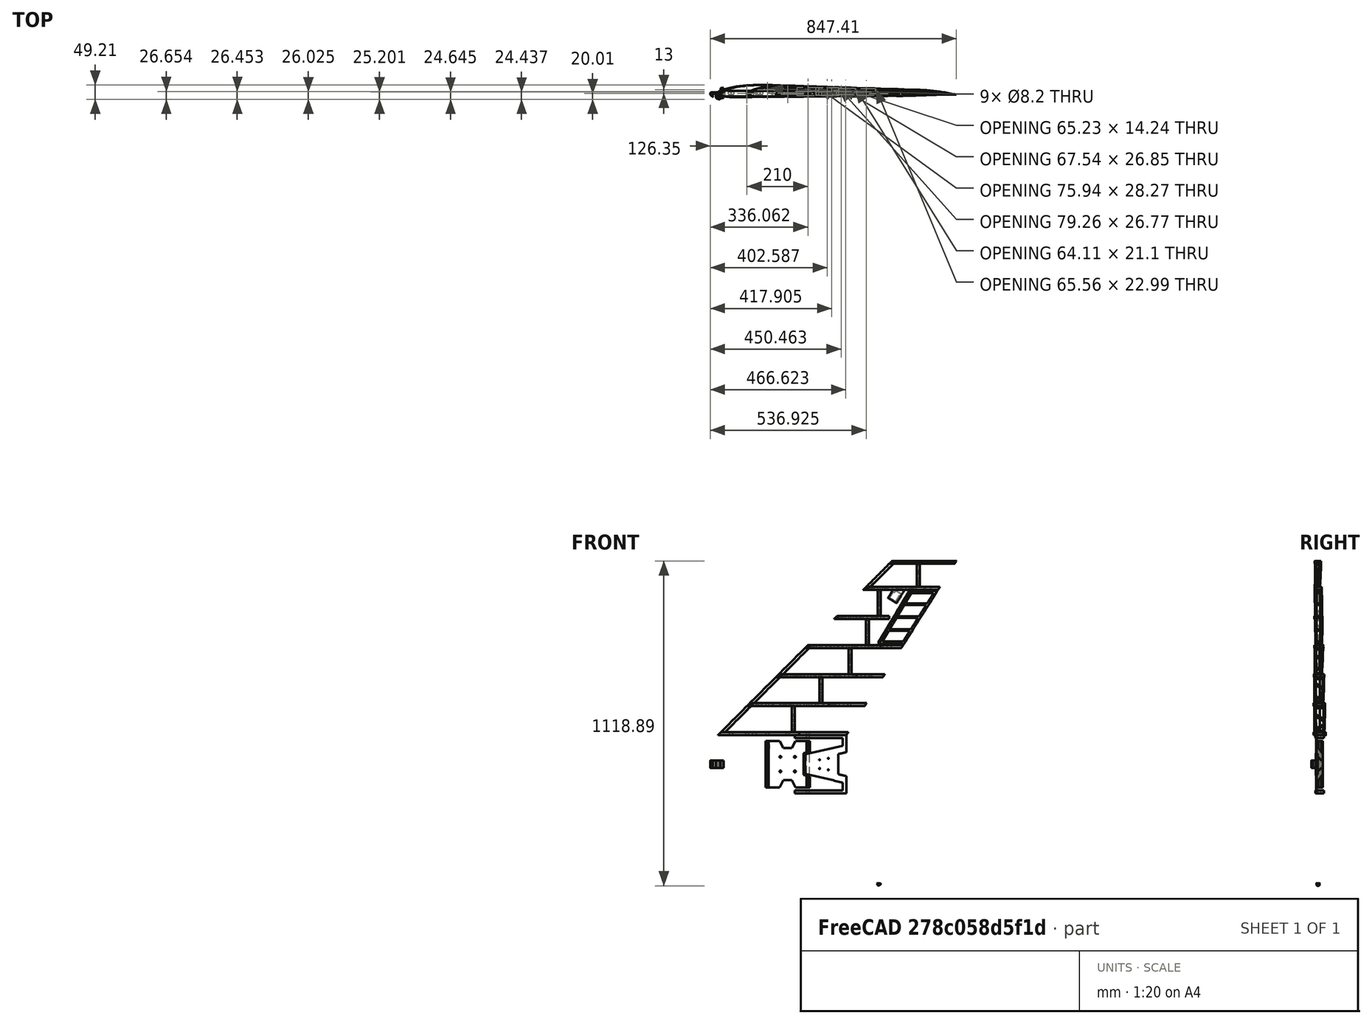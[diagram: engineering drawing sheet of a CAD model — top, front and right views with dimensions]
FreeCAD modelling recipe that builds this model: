
FCSTD DOCUMENT  (FreeCAD 1.0R39109 (Git))
Label: SD7037_mirrored
License: All rights reserved
LicenseURL: https://en.wikipedia.org/wiki/All_rights_reserved
objects: Sketcher::SketchObject×213, PartDesign::Pocket×145, PartDesign::Plane×49, PartDesign::Body×35, PartDesign::AdditiveLoft×28, Part::Mirroring×25, PartDesign::Pad×13, PartDesign::Fillet×8, PartDesign::Chamfer×5, Part::Part2DObjectPython×3, PartDesign::FeatureBase×2, Part::Scale×2, Part::Cut×2, App::DocumentObjectGroup×1, PartDesign::ShapeBinder×1
note: 1144 computed .brp shape members not serialized (recipe doc carries the construction recipe); baked Part::Feature solids carry a one-line shape summary decoded from their .brp

FEATURE [Part::Part2DObjectPython] Wire  # Draft 2D object (typed FeaturePython)
  Area = 0.0605284
  ChamferSize = 0
  Closed = true
  End = (1,0,0)
  FilletRadius = 0
  Length = 2.02979
  MakeFace = true
  Points = (61) [(1,0,0),(0.99672,0.00042,0),(0.98707,0.0018,0),(0.97146,0.00436,0),(0.95041,0.00811,0),(0.9245,0.01295,0),(0.89425,0.01865,0),(0.86015,0.0249,0),+53 more]
  Start = (1,0,0)
  Subdivisions = 0
FEATURE [App::DocumentObjectGroup] sd7037
  Group = -> [Wire]
FEATURE [Part::Part2DObjectPython] BSpline  label="wingtip"  # Draft 2D object (typed FeaturePython)
  Area = 2965.6
  Closed = true
  MakeFace = true
  Parameterization = 1
  Points = (60) [(221,0,0),(220.275,0.09282,0),(218.142,0.3978,0),(214.693,0.96356,0),(210.041,1.79231,0),(204.315,2.86195,0),(197.629,4.12165,0),(190.093,5.5029,0),+52 more]
FEATURE [Part::Part2DObjectPython] BSpline001  label="wingbase"  # Draft 2D object (typed FeaturePython)
  Area = 11862.4
  Closed = true
  MakeFace = true
  Parameterization = 1
  Points = (60) [(442,0,0),(440.55,0.18564,0),(436.285,0.7956,0),(429.385,1.92712,0),(420.081,3.58462,0),(408.629,5.7239,0),(395.258,8.2433,0),(380.186,11.0058,0),+52 more]
FEATURE [Sketcher::SketchObject] Sketch
  ArcFitTolerance = 1e-06
  FullyConstrained = false
  MakeInternals = false
  Placement = pos=(600,0,-600) rot=(0,0,1;0rad)
  sketch-geometry (123):
    g0: BSplineCurve PolesCount=61 KnotsCount=61 Degree=3 IsPeriodic=1
    g1-g61: Circle [constr] x61 (B-spline internal-alignment scaffolding for g0; pole/knot coordinates omitted)
    g62-g122: GeomPoint [constr] x61 (B-spline internal-alignment scaffolding for g0; pole/knot coordinates omitted)
  constraints (123):
    c: InternalAlignment(g1,g0)
    c: Weight(g1) = 1
    c: InternalAlignment(g2,g0)
    c: Equal(g2,g1)
    c: InternalAlignment(g3,g0)
    c: Equal(g3,g1)
    c: InternalAlignment(g4,g0)
    c: Equal(g4,g1)
    c: InternalAlignment(g5,g0)
    c: Equal(g5,g1)
    c: InternalAlignment(g6,g0)
    c: Equal(g6,g1)
    c: InternalAlignment(g7,g0)
    c: Equal(g7,g1)
    c: InternalAlignment(g8,g0)
    c: Equal(g8,g1)
    c: InternalAlignment(g9,g0)
    c: Equal(g9,g1)
    c: InternalAlignment(g10,g0)
    c: Equal(g10,g1)
    c: InternalAlignment(g11,g0)
    c: Equal(g11,g1)
    c: InternalAlignment(g12,g0)
    c: Equal(g12,g1)
    c: InternalAlignment(g13,g0)
    c: Equal(g13,g1)
    c: InternalAlignment(g14,g0)
    c: Equal(g14,g1)
    c: InternalAlignment(g15,g0)
    c: Equal(g15,g1)
    c: InternalAlignment(g16,g0)
    c: Equal(g16,g1)
    c: InternalAlignment(g17,g0)
    c: Equal(g17,g1)
    c: InternalAlignment(g18,g0)
    c: Equal(g18,g1)
    c: InternalAlignment(g19,g0)
    c: Equal(g19,g1)
    c: InternalAlignment(g20,g0)
    c: Equal(g20,g1)
    c: InternalAlignment(g21,g0)
    c: Equal(g21,g1)
    c: InternalAlignment(g22,g0)
    c: Equal(g22,g1)
    c: InternalAlignment(g23,g0)
    c: Equal(g23,g1)
    c: InternalAlignment(g24,g0)
    c: Equal(g24,g1)
    c: InternalAlignment(g25,g0)
    c: Equal(g25,g1)
    c: InternalAlignment(g26,g0)
    c: Equal(g26,g1)
    c: InternalAlignment(g27,g0)
    c: Equal(g27,g1)
    c: InternalAlignment(g28,g0)
    c: Equal(g28,g1)
    c: InternalAlignment(g29,g0)
    c: Equal(g29,g1)
    c: InternalAlignment(g30,g0)
    c: Equal(g30,g1)
    c: InternalAlignment(g31,g0)
    c: Equal(g31,g1)
    c: InternalAlignment(g32,g0)
    c: Equal(g32,g1)
    c: InternalAlignment(g33,g0)
    c: Equal(g33,g1)
    c: InternalAlignment(g34,g0)
    c: Equal(g34,g1)
    c: InternalAlignment(g35,g0)
    c: Equal(g35,g1)
    c: InternalAlignment(g36,g0)
    c: Equal(g36,g1)
    c: InternalAlignment(g37,g0)
    c: Equal(g37,g1)
    c: InternalAlignment(g38,g0)
    c: Equal(g38,g1)
    c: InternalAlignment(g39,g0)
    c: Equal(g39,g1)
    c: InternalAlignment(g40,g0)
    c: Equal(g40,g1)
    c: InternalAlignment(g41,g0)
    c: Equal(g41,g1)
    c: InternalAlignment(g42,g0)
    c: Equal(g42,g1)
    c: InternalAlignment(g43,g0)
    c: Equal(g43,g1)
    c: InternalAlignment(g44,g0)
    c: Equal(g44,g1)
    c: InternalAlignment(g45,g0)
    c: Equal(g45,g1)
    c: InternalAlignment(g46,g0)
    c: Equal(g46,g1)
    c: InternalAlignment(g47,g0)
    c: Equal(g47,g1)
    c: InternalAlignment(g48,g0)
    c: Equal(g48,g1)
    c: InternalAlignment(g49,g0)
    c: Equal(g49,g1)
    c: InternalAlignment(g50,g0)
    c: Equal(g50,g1)
    c: InternalAlignment(g51,g0)
    c: Equal(g51,g1)
    c: InternalAlignment(g52,g0)
    c: Equal(g52,g1)
    c: InternalAlignment(g53,g0)
    c: Equal(g53,g1)
    c: InternalAlignment(g54,g0)
    c: Equal(g54,g1)
    c: InternalAlignment(g55,g0)
    c: Equal(g55,g1)
    c: InternalAlignment(g56,g0)
    c: Equal(g56,g1)
    c: InternalAlignment(g57,g0)
    c: Equal(g57,g1)
    c: InternalAlignment(g58,g0)
    c: Equal(g58,g1)
    c: InternalAlignment(g59,g0)
    c: Equal(g59,g1)
    c: InternalAlignment(g60,g0)
    c: Equal(g60,g1)
    c: InternalAlignment(g61,g0)
    c: Equal(g61,g1)
    c: InternalAlignment(g62-g122 -> g0) x61
FEATURE [Sketcher::SketchObject] Sketch001
  ArcFitTolerance = 1e-06
  FullyConstrained = false
  MakeInternals = false
  sketch-geometry (123):
    g0: BSplineCurve PolesCount=61 KnotsCount=61 Degree=3 IsPeriodic=1
    g1-g61: Circle [constr] x61 (B-spline internal-alignment scaffolding for g0; pole/knot coordinates omitted)
    g62-g122: GeomPoint [constr] x61 (B-spline internal-alignment scaffolding for g0; pole/knot coordinates omitted)
  constraints (123):
    c: InternalAlignment(g1,g0)
    c: Weight(g1) = 1
    c: InternalAlignment(g2,g0)
    c: Equal(g2,g1)
    c: InternalAlignment(g3,g0)
    c: Equal(g3,g1)
    c: InternalAlignment(g4,g0)
    c: Equal(g4,g1)
    c: InternalAlignment(g5,g0)
    c: Equal(g5,g1)
    c: InternalAlignment(g6,g0)
    c: Equal(g6,g1)
    c: InternalAlignment(g7,g0)
    c: Equal(g7,g1)
    c: InternalAlignment(g8,g0)
    c: Equal(g8,g1)
    c: InternalAlignment(g9,g0)
    c: Equal(g9,g1)
    c: InternalAlignment(g10,g0)
    c: Equal(g10,g1)
    c: InternalAlignment(g11,g0)
    c: Equal(g11,g1)
    c: InternalAlignment(g12,g0)
    c: Equal(g12,g1)
    c: InternalAlignment(g13,g0)
    c: Equal(g13,g1)
    c: InternalAlignment(g14,g0)
    c: Equal(g14,g1)
    c: InternalAlignment(g15,g0)
    c: Equal(g15,g1)
    c: InternalAlignment(g16,g0)
    c: Equal(g16,g1)
    c: InternalAlignment(g17,g0)
    c: Equal(g17,g1)
    c: InternalAlignment(g18,g0)
    c: Equal(g18,g1)
    c: InternalAlignment(g19,g0)
    c: Equal(g19,g1)
    c: InternalAlignment(g20,g0)
    c: Equal(g20,g1)
    c: InternalAlignment(g21,g0)
    c: Equal(g21,g1)
    c: InternalAlignment(g22,g0)
    c: Equal(g22,g1)
    c: InternalAlignment(g23,g0)
    c: Equal(g23,g1)
    c: InternalAlignment(g24,g0)
    c: Equal(g24,g1)
    c: InternalAlignment(g25,g0)
    c: Equal(g25,g1)
    c: InternalAlignment(g26,g0)
    c: Equal(g26,g1)
    c: InternalAlignment(g27,g0)
    c: Equal(g27,g1)
    c: InternalAlignment(g28,g0)
    c: Equal(g28,g1)
    c: InternalAlignment(g29,g0)
    c: Equal(g29,g1)
    c: InternalAlignment(g30,g0)
    c: Equal(g30,g1)
    c: InternalAlignment(g31,g0)
    c: Equal(g31,g1)
    c: InternalAlignment(g32,g0)
    c: Equal(g32,g1)
    c: InternalAlignment(g33,g0)
    c: Equal(g33,g1)
    c: InternalAlignment(g34,g0)
    c: Equal(g34,g1)
    c: InternalAlignment(g35,g0)
    c: Equal(g35,g1)
    c: InternalAlignment(g36,g0)
    c: Equal(g36,g1)
    c: InternalAlignment(g37,g0)
    c: Equal(g37,g1)
    c: InternalAlignment(g38,g0)
    c: Equal(g38,g1)
    c: InternalAlignment(g39,g0)
    c: Equal(g39,g1)
    c: InternalAlignment(g40,g0)
    c: Equal(g40,g1)
    c: InternalAlignment(g41,g0)
    c: Equal(g41,g1)
    c: InternalAlignment(g42,g0)
    c: Equal(g42,g1)
    c: InternalAlignment(g43,g0)
    c: Equal(g43,g1)
    c: InternalAlignment(g44,g0)
    c: Equal(g44,g1)
    c: InternalAlignment(g45,g0)
    c: Equal(g45,g1)
    c: InternalAlignment(g46,g0)
    c: Equal(g46,g1)
    c: InternalAlignment(g47,g0)
    c: Equal(g47,g1)
    c: InternalAlignment(g48,g0)
    c: Equal(g48,g1)
    c: InternalAlignment(g49,g0)
    c: Equal(g49,g1)
    c: InternalAlignment(g50,g0)
    c: Equal(g50,g1)
    c: InternalAlignment(g51,g0)
    c: Equal(g51,g1)
    c: InternalAlignment(g52,g0)
    c: Equal(g52,g1)
    c: InternalAlignment(g53,g0)
    c: Equal(g53,g1)
    c: InternalAlignment(g54,g0)
    c: Equal(g54,g1)
    c: InternalAlignment(g55,g0)
    c: Equal(g55,g1)
    c: InternalAlignment(g56,g0)
    c: Equal(g56,g1)
    c: InternalAlignment(g57,g0)
    c: Equal(g57,g1)
    c: InternalAlignment(g58,g0)
    c: Equal(g58,g1)
    c: InternalAlignment(g59,g0)
    c: Equal(g59,g1)
    c: InternalAlignment(g60,g0)
    c: Equal(g60,g1)
    c: InternalAlignment(g61,g0)
    c: Equal(g61,g1)
    c: InternalAlignment(g62-g122 -> g0) x61
FEATURE [PartDesign::AdditiveLoft] AdditiveLoft
  Closed = false
  Profile = -> Sketch001
  Refine = true
  Ruled = false
  Sections = -> [Sketch]
  Suppressed = false
FEATURE [PartDesign::Plane] DatumPlane
  AttachmentOffset = pos=(0,0,0) rot=(0,-1,0;0.785398rad)
  AttachmentSupport = -> [AdditiveLoft]
  Length = 397.552
  MapMode = 5
  Placement = pos=(0,0,0) rot=(0,-1,0;0.785398rad)
  ResizeMode = 0
  Width = 78.2374
FEATURE [Sketcher::SketchObject] Sketch002
  ArcFitTolerance = 1e-06
  AttachmentSupport = -> [DatumPlane]
  FullyConstrained = false
  MakeInternals = false
  MapMode = 5
  Placement = pos=(0,0,0) rot=(0,-1,0;0.785398rad)
  sketch-geometry (1):
    g0: Circle CenterX=28.3343 CenterY=4.75298 CenterZ=0 NormalX=0 NormalY=0 NormalZ=1 AngleXU=0 Radius=4.1
  constraints (1):
    c: Diameter(g0) = 8.2
FEATURE [PartDesign::Pocket] Pocket
  BaseFeature = -> AdditiveLoft
  Direction = (0.707107,0,-0.707107)
  Length = 1000
  Length2 = 5
  Profile = -> Sketch002
  ReferenceAxis = -> Sketch002 [N_Axis]
  Refine = true
  Suppressed = false
  Type = 0
FEATURE [Sketcher::SketchObject] Sketch003
  ArcFitTolerance = 1e-06
  FullyConstrained = false
  MakeInternals = false
  Placement = pos=(600,0,-600) rot=(0,0,1;0rad)
  sketch-geometry (123):
    g0: BSplineCurve PolesCount=61 KnotsCount=61 Degree=3 IsPeriodic=1
    g1-g61: Circle [constr] x61 (B-spline internal-alignment scaffolding for g0; pole/knot coordinates omitted)
    g62-g122: GeomPoint [constr] x61 (B-spline internal-alignment scaffolding for g0; pole/knot coordinates omitted)
  constraints (123):
    c: InternalAlignment(g1,g0)
    c: Weight(g1) = 1
    c: InternalAlignment(g2,g0)
    c: Equal(g2,g1)
    c: InternalAlignment(g3,g0)
    c: Equal(g3,g1)
    c: InternalAlignment(g4,g0)
    c: Equal(g4,g1)
    c: InternalAlignment(g5,g0)
    c: Equal(g5,g1)
    c: InternalAlignment(g6,g0)
    c: Equal(g6,g1)
    c: InternalAlignment(g7,g0)
    c: Equal(g7,g1)
    c: InternalAlignment(g8,g0)
    c: Equal(g8,g1)
    c: InternalAlignment(g9,g0)
    c: Equal(g9,g1)
    c: InternalAlignment(g10,g0)
    c: Equal(g10,g1)
    c: InternalAlignment(g11,g0)
    c: Equal(g11,g1)
    c: InternalAlignment(g12,g0)
    c: Equal(g12,g1)
    c: InternalAlignment(g13,g0)
    c: Equal(g13,g1)
    c: InternalAlignment(g14,g0)
    c: Equal(g14,g1)
    c: InternalAlignment(g15,g0)
    c: Equal(g15,g1)
    c: InternalAlignment(g16,g0)
    c: Equal(g16,g1)
    c: InternalAlignment(g17,g0)
    c: Equal(g17,g1)
    c: InternalAlignment(g18,g0)
    c: Equal(g18,g1)
    c: InternalAlignment(g19,g0)
    c: Equal(g19,g1)
    c: InternalAlignment(g20,g0)
    c: Equal(g20,g1)
    c: InternalAlignment(g21,g0)
    c: Equal(g21,g1)
    c: InternalAlignment(g22,g0)
    c: Equal(g22,g1)
    c: InternalAlignment(g23,g0)
    c: Equal(g23,g1)
    c: InternalAlignment(g24,g0)
    c: Equal(g24,g1)
    c: InternalAlignment(g25,g0)
    c: Equal(g25,g1)
    c: InternalAlignment(g26,g0)
    c: Equal(g26,g1)
    c: InternalAlignment(g27,g0)
    c: Equal(g27,g1)
    c: InternalAlignment(g28,g0)
    c: Equal(g28,g1)
    c: InternalAlignment(g29,g0)
    c: Equal(g29,g1)
    c: InternalAlignment(g30,g0)
    c: Equal(g30,g1)
    c: InternalAlignment(g31,g0)
    c: Equal(g31,g1)
    c: InternalAlignment(g32,g0)
    c: Equal(g32,g1)
    c: InternalAlignment(g33,g0)
    c: Equal(g33,g1)
    c: InternalAlignment(g34,g0)
    c: Equal(g34,g1)
    c: InternalAlignment(g35,g0)
    c: Equal(g35,g1)
    c: InternalAlignment(g36,g0)
    c: Equal(g36,g1)
    c: InternalAlignment(g37,g0)
    c: Equal(g37,g1)
    c: InternalAlignment(g38,g0)
    c: Equal(g38,g1)
    c: InternalAlignment(g39,g0)
    c: Equal(g39,g1)
    c: InternalAlignment(g40,g0)
    c: Equal(g40,g1)
    c: InternalAlignment(g41,g0)
    c: Equal(g41,g1)
    c: InternalAlignment(g42,g0)
    c: Equal(g42,g1)
    c: InternalAlignment(g43,g0)
    c: Equal(g43,g1)
    c: InternalAlignment(g44,g0)
    c: Equal(g44,g1)
    c: InternalAlignment(g45,g0)
    c: Equal(g45,g1)
    c: InternalAlignment(g46,g0)
    c: Equal(g46,g1)
    c: InternalAlignment(g47,g0)
    c: Equal(g47,g1)
    c: InternalAlignment(g48,g0)
    c: Equal(g48,g1)
    c: InternalAlignment(g49,g0)
    c: Equal(g49,g1)
    c: InternalAlignment(g50,g0)
    c: Equal(g50,g1)
    c: InternalAlignment(g51,g0)
    c: Equal(g51,g1)
    c: InternalAlignment(g52,g0)
    c: Equal(g52,g1)
    c: InternalAlignment(g53,g0)
    c: Equal(g53,g1)
    c: InternalAlignment(g54,g0)
    c: Equal(g54,g1)
    c: InternalAlignment(g55,g0)
    c: Equal(g55,g1)
    c: InternalAlignment(g56,g0)
    c: Equal(g56,g1)
    c: InternalAlignment(g57,g0)
    c: Equal(g57,g1)
    c: InternalAlignment(g58,g0)
    c: Equal(g58,g1)
    c: InternalAlignment(g59,g0)
    c: Equal(g59,g1)
    c: InternalAlignment(g60,g0)
    c: Equal(g60,g1)
    c: InternalAlignment(g61,g0)
    c: Equal(g61,g1)
    c: InternalAlignment(g62-g122 -> g0) x61
FEATURE [Sketcher::SketchObject] Sketch004
  ArcFitTolerance = 1e-06
  FullyConstrained = false
  MakeInternals = false
  sketch-geometry (123):
    g0: BSplineCurve PolesCount=61 KnotsCount=61 Degree=3 IsPeriodic=1
    g1-g61: Circle [constr] x61 (B-spline internal-alignment scaffolding for g0; pole/knot coordinates omitted)
    g62-g122: GeomPoint [constr] x61 (B-spline internal-alignment scaffolding for g0; pole/knot coordinates omitted)
  constraints (123):
    c: InternalAlignment(g1,g0)
    c: Weight(g1) = 1
    c: InternalAlignment(g2,g0)
    c: Equal(g2,g1)
    c: InternalAlignment(g3,g0)
    c: Equal(g3,g1)
    c: InternalAlignment(g4,g0)
    c: Equal(g4,g1)
    c: InternalAlignment(g5,g0)
    c: Equal(g5,g1)
    c: InternalAlignment(g6,g0)
    c: Equal(g6,g1)
    c: InternalAlignment(g7,g0)
    c: Equal(g7,g1)
    c: InternalAlignment(g8,g0)
    c: Equal(g8,g1)
    c: InternalAlignment(g9,g0)
    c: Equal(g9,g1)
    c: InternalAlignment(g10,g0)
    c: Equal(g10,g1)
    c: InternalAlignment(g11,g0)
    c: Equal(g11,g1)
    c: InternalAlignment(g12,g0)
    c: Equal(g12,g1)
    c: InternalAlignment(g13,g0)
    c: Equal(g13,g1)
    c: InternalAlignment(g14,g0)
    c: Equal(g14,g1)
    c: InternalAlignment(g15,g0)
    c: Equal(g15,g1)
    c: InternalAlignment(g16,g0)
    c: Equal(g16,g1)
    c: InternalAlignment(g17,g0)
    c: Equal(g17,g1)
    c: InternalAlignment(g18,g0)
    c: Equal(g18,g1)
    c: InternalAlignment(g19,g0)
    c: Equal(g19,g1)
    c: InternalAlignment(g20,g0)
    c: Equal(g20,g1)
    c: InternalAlignment(g21,g0)
    c: Equal(g21,g1)
    c: InternalAlignment(g22,g0)
    c: Equal(g22,g1)
    c: InternalAlignment(g23,g0)
    c: Equal(g23,g1)
    c: InternalAlignment(g24,g0)
    c: Equal(g24,g1)
    c: InternalAlignment(g25,g0)
    c: Equal(g25,g1)
    c: InternalAlignment(g26,g0)
    c: Equal(g26,g1)
    c: InternalAlignment(g27,g0)
    c: Equal(g27,g1)
    c: InternalAlignment(g28,g0)
    c: Equal(g28,g1)
    c: InternalAlignment(g29,g0)
    c: Equal(g29,g1)
    c: InternalAlignment(g30,g0)
    c: Equal(g30,g1)
    c: InternalAlignment(g31,g0)
    c: Equal(g31,g1)
    c: InternalAlignment(g32,g0)
    c: Equal(g32,g1)
    c: InternalAlignment(g33,g0)
    c: Equal(g33,g1)
    c: InternalAlignment(g34,g0)
    c: Equal(g34,g1)
    c: InternalAlignment(g35,g0)
    c: Equal(g35,g1)
    c: InternalAlignment(g36,g0)
    c: Equal(g36,g1)
    c: InternalAlignment(g37,g0)
    c: Equal(g37,g1)
    c: InternalAlignment(g38,g0)
    c: Equal(g38,g1)
    c: InternalAlignment(g39,g0)
    c: Equal(g39,g1)
    c: InternalAlignment(g40,g0)
    c: Equal(g40,g1)
    c: InternalAlignment(g41,g0)
    c: Equal(g41,g1)
    c: InternalAlignment(g42,g0)
    c: Equal(g42,g1)
    c: InternalAlignment(g43,g0)
    c: Equal(g43,g1)
    c: InternalAlignment(g44,g0)
    c: Equal(g44,g1)
    c: InternalAlignment(g45,g0)
    c: Equal(g45,g1)
    c: InternalAlignment(g46,g0)
    c: Equal(g46,g1)
    c: InternalAlignment(g47,g0)
    c: Equal(g47,g1)
    c: InternalAlignment(g48,g0)
    c: Equal(g48,g1)
    c: InternalAlignment(g49,g0)
    c: Equal(g49,g1)
    c: InternalAlignment(g50,g0)
    c: Equal(g50,g1)
    c: InternalAlignment(g51,g0)
    c: Equal(g51,g1)
    c: InternalAlignment(g52,g0)
    c: Equal(g52,g1)
    c: InternalAlignment(g53,g0)
    c: Equal(g53,g1)
    c: InternalAlignment(g54,g0)
    c: Equal(g54,g1)
    c: InternalAlignment(g55,g0)
    c: Equal(g55,g1)
    c: InternalAlignment(g56,g0)
    c: Equal(g56,g1)
    c: InternalAlignment(g57,g0)
    c: Equal(g57,g1)
    c: InternalAlignment(g58,g0)
    c: Equal(g58,g1)
    c: InternalAlignment(g59,g0)
    c: Equal(g59,g1)
    c: InternalAlignment(g60,g0)
    c: Equal(g60,g1)
    c: InternalAlignment(g61,g0)
    c: Equal(g61,g1)
    c: InternalAlignment(g62-g122 -> g0) x61
FEATURE [PartDesign::AdditiveLoft] AdditiveLoft001
  Closed = false
  Profile = -> Sketch004
  Refine = true
  Ruled = false
  Sections = -> [Sketch003]
  Suppressed = false
FEATURE [PartDesign::Plane] DatumPlane001
  AttachmentOffset = pos=(0,0,0) rot=(0,-1,0;0.785398rad)
  AttachmentSupport = -> [AdditiveLoft001]
  Length = 412.402
  MapMode = 5
  Placement = pos=(0,0,0) rot=(0,-1,0;0.785398rad)
  ResizeMode = 0
  Width = 84.5785
FEATURE [Sketcher::SketchObject] Sketch005
  ArcFitTolerance = 1e-06
  AttachmentSupport = -> [DatumPlane001]
  FullyConstrained = false
  MakeInternals = false
  MapMode = 5
  Placement = pos=(0,0,0) rot=(0,-1,0;0.785398rad)
  sketch-geometry (1):
    g0: Circle CenterX=28.3343 CenterY=4.75298 CenterZ=0 NormalX=0 NormalY=0 NormalZ=1 AngleXU=0 Radius=4.1
  constraints (1):
    c: Diameter(g0) = 8.2
FEATURE [PartDesign::Pocket] Pocket001
  BaseFeature = -> AdditiveLoft001
  Direction = (0.707107,0,-0.707107)
  Length = 1000
  Length2 = 5
  Profile = -> Sketch005
  ReferenceAxis = -> Sketch005 [N_Axis]
  Refine = true
  Suppressed = false
  Type = 0
FEATURE [Sketcher::SketchObject] Sketch006
  ArcFitTolerance = 1e-06
  FullyConstrained = false
  MakeInternals = false
  Placement = pos=(600,0,-600) rot=(0,0,1;0rad)
  sketch-geometry (123):
    g0: BSplineCurve PolesCount=61 KnotsCount=61 Degree=3 IsPeriodic=1
    g1-g61: Circle [constr] x61 (B-spline internal-alignment scaffolding for g0; pole/knot coordinates omitted)
    g62-g122: GeomPoint [constr] x61 (B-spline internal-alignment scaffolding for g0; pole/knot coordinates omitted)
  constraints (123):
    c: InternalAlignment(g1,g0)
    c: Weight(g1) = 1
    c: InternalAlignment(g2,g0)
    c: Equal(g2,g1)
    c: InternalAlignment(g3,g0)
    c: Equal(g3,g1)
    c: InternalAlignment(g4,g0)
    c: Equal(g4,g1)
    c: InternalAlignment(g5,g0)
    c: Equal(g5,g1)
    c: InternalAlignment(g6,g0)
    c: Equal(g6,g1)
    c: InternalAlignment(g7,g0)
    c: Equal(g7,g1)
    c: InternalAlignment(g8,g0)
    c: Equal(g8,g1)
    c: InternalAlignment(g9,g0)
    c: Equal(g9,g1)
    c: InternalAlignment(g10,g0)
    c: Equal(g10,g1)
    c: InternalAlignment(g11,g0)
    c: Equal(g11,g1)
    c: InternalAlignment(g12,g0)
    c: Equal(g12,g1)
    c: InternalAlignment(g13,g0)
    c: Equal(g13,g1)
    c: InternalAlignment(g14,g0)
    c: Equal(g14,g1)
    c: InternalAlignment(g15,g0)
    c: Equal(g15,g1)
    c: InternalAlignment(g16,g0)
    c: Equal(g16,g1)
    c: InternalAlignment(g17,g0)
    c: Equal(g17,g1)
    c: InternalAlignment(g18,g0)
    c: Equal(g18,g1)
    c: InternalAlignment(g19,g0)
    c: Equal(g19,g1)
    c: InternalAlignment(g20,g0)
    c: Equal(g20,g1)
    c: InternalAlignment(g21,g0)
    c: Equal(g21,g1)
    c: InternalAlignment(g22,g0)
    c: Equal(g22,g1)
    c: InternalAlignment(g23,g0)
    c: Equal(g23,g1)
    c: InternalAlignment(g24,g0)
    c: Equal(g24,g1)
    c: InternalAlignment(g25,g0)
    c: Equal(g25,g1)
    c: InternalAlignment(g26,g0)
    c: Equal(g26,g1)
    c: InternalAlignment(g27,g0)
    c: Equal(g27,g1)
    c: InternalAlignment(g28,g0)
    c: Equal(g28,g1)
    c: InternalAlignment(g29,g0)
    c: Equal(g29,g1)
    c: InternalAlignment(g30,g0)
    c: Equal(g30,g1)
    c: InternalAlignment(g31,g0)
    c: Equal(g31,g1)
    c: InternalAlignment(g32,g0)
    c: Equal(g32,g1)
    c: InternalAlignment(g33,g0)
    c: Equal(g33,g1)
    c: InternalAlignment(g34,g0)
    c: Equal(g34,g1)
    c: InternalAlignment(g35,g0)
    c: Equal(g35,g1)
    c: InternalAlignment(g36,g0)
    c: Equal(g36,g1)
    c: InternalAlignment(g37,g0)
    c: Equal(g37,g1)
    c: InternalAlignment(g38,g0)
    c: Equal(g38,g1)
    c: InternalAlignment(g39,g0)
    c: Equal(g39,g1)
    c: InternalAlignment(g40,g0)
    c: Equal(g40,g1)
    c: InternalAlignment(g41,g0)
    c: Equal(g41,g1)
    c: InternalAlignment(g42,g0)
    c: Equal(g42,g1)
    c: InternalAlignment(g43,g0)
    c: Equal(g43,g1)
    c: InternalAlignment(g44,g0)
    c: Equal(g44,g1)
    c: InternalAlignment(g45,g0)
    c: Equal(g45,g1)
    c: InternalAlignment(g46,g0)
    c: Equal(g46,g1)
    c: InternalAlignment(g47,g0)
    c: Equal(g47,g1)
    c: InternalAlignment(g48,g0)
    c: Equal(g48,g1)
    c: InternalAlignment(g49,g0)
    c: Equal(g49,g1)
    c: InternalAlignment(g50,g0)
    c: Equal(g50,g1)
    c: InternalAlignment(g51,g0)
    c: Equal(g51,g1)
    c: InternalAlignment(g52,g0)
    c: Equal(g52,g1)
    c: InternalAlignment(g53,g0)
    c: Equal(g53,g1)
    c: InternalAlignment(g54,g0)
    c: Equal(g54,g1)
    c: InternalAlignment(g55,g0)
    c: Equal(g55,g1)
    c: InternalAlignment(g56,g0)
    c: Equal(g56,g1)
    c: InternalAlignment(g57,g0)
    c: Equal(g57,g1)
    c: InternalAlignment(g58,g0)
    c: Equal(g58,g1)
    c: InternalAlignment(g59,g0)
    c: Equal(g59,g1)
    c: InternalAlignment(g60,g0)
    c: Equal(g60,g1)
    c: InternalAlignment(g61,g0)
    c: Equal(g61,g1)
    c: InternalAlignment(g62-g122 -> g0) x61
FEATURE [Sketcher::SketchObject] Sketch007
  ArcFitTolerance = 1e-06
  FullyConstrained = false
  MakeInternals = false
  sketch-geometry (123):
    g0: BSplineCurve PolesCount=61 KnotsCount=61 Degree=3 IsPeriodic=1
    g1-g61: Circle [constr] x61 (B-spline internal-alignment scaffolding for g0; pole/knot coordinates omitted)
    g62-g122: GeomPoint [constr] x61 (B-spline internal-alignment scaffolding for g0; pole/knot coordinates omitted)
  constraints (123):
    c: InternalAlignment(g1,g0)
    c: Weight(g1) = 1
    c: InternalAlignment(g2,g0)
    c: Equal(g2,g1)
    c: InternalAlignment(g3,g0)
    c: Equal(g3,g1)
    c: InternalAlignment(g4,g0)
    c: Equal(g4,g1)
    c: InternalAlignment(g5,g0)
    c: Equal(g5,g1)
    c: InternalAlignment(g6,g0)
    c: Equal(g6,g1)
    c: InternalAlignment(g7,g0)
    c: Equal(g7,g1)
    c: InternalAlignment(g8,g0)
    c: Equal(g8,g1)
    c: InternalAlignment(g9,g0)
    c: Equal(g9,g1)
    c: InternalAlignment(g10,g0)
    c: Equal(g10,g1)
    c: InternalAlignment(g11,g0)
    c: Equal(g11,g1)
    c: InternalAlignment(g12,g0)
    c: Equal(g12,g1)
    c: InternalAlignment(g13,g0)
    c: Equal(g13,g1)
    c: InternalAlignment(g14,g0)
    c: Equal(g14,g1)
    c: InternalAlignment(g15,g0)
    c: Equal(g15,g1)
    c: InternalAlignment(g16,g0)
    c: Equal(g16,g1)
    c: InternalAlignment(g17,g0)
    c: Equal(g17,g1)
    c: InternalAlignment(g18,g0)
    c: Equal(g18,g1)
    c: InternalAlignment(g19,g0)
    c: Equal(g19,g1)
    c: InternalAlignment(g20,g0)
    c: Equal(g20,g1)
    c: InternalAlignment(g21,g0)
    c: Equal(g21,g1)
    c: InternalAlignment(g22,g0)
    c: Equal(g22,g1)
    c: InternalAlignment(g23,g0)
    c: Equal(g23,g1)
    c: InternalAlignment(g24,g0)
    c: Equal(g24,g1)
    c: InternalAlignment(g25,g0)
    c: Equal(g25,g1)
    c: InternalAlignment(g26,g0)
    c: Equal(g26,g1)
    c: InternalAlignment(g27,g0)
    c: Equal(g27,g1)
    c: InternalAlignment(g28,g0)
    c: Equal(g28,g1)
    c: InternalAlignment(g29,g0)
    c: Equal(g29,g1)
    c: InternalAlignment(g30,g0)
    c: Equal(g30,g1)
    c: InternalAlignment(g31,g0)
    c: Equal(g31,g1)
    c: InternalAlignment(g32,g0)
    c: Equal(g32,g1)
    c: InternalAlignment(g33,g0)
    c: Equal(g33,g1)
    c: InternalAlignment(g34,g0)
    c: Equal(g34,g1)
    c: InternalAlignment(g35,g0)
    c: Equal(g35,g1)
    c: InternalAlignment(g36,g0)
    c: Equal(g36,g1)
    c: InternalAlignment(g37,g0)
    c: Equal(g37,g1)
    c: InternalAlignment(g38,g0)
    c: Equal(g38,g1)
    c: InternalAlignment(g39,g0)
    c: Equal(g39,g1)
    c: InternalAlignment(g40,g0)
    c: Equal(g40,g1)
    c: InternalAlignment(g41,g0)
    c: Equal(g41,g1)
    c: InternalAlignment(g42,g0)
    c: Equal(g42,g1)
    c: InternalAlignment(g43,g0)
    c: Equal(g43,g1)
    c: InternalAlignment(g44,g0)
    c: Equal(g44,g1)
    c: InternalAlignment(g45,g0)
    c: Equal(g45,g1)
    c: InternalAlignment(g46,g0)
    c: Equal(g46,g1)
    c: InternalAlignment(g47,g0)
    c: Equal(g47,g1)
    c: InternalAlignment(g48,g0)
    c: Equal(g48,g1)
    c: InternalAlignment(g49,g0)
    c: Equal(g49,g1)
    c: InternalAlignment(g50,g0)
    c: Equal(g50,g1)
    c: InternalAlignment(g51,g0)
    c: Equal(g51,g1)
    c: InternalAlignment(g52,g0)
    c: Equal(g52,g1)
    c: InternalAlignment(g53,g0)
    c: Equal(g53,g1)
    c: InternalAlignment(g54,g0)
    c: Equal(g54,g1)
    c: InternalAlignment(g55,g0)
    c: Equal(g55,g1)
    c: InternalAlignment(g56,g0)
    c: Equal(g56,g1)
    c: InternalAlignment(g57,g0)
    c: Equal(g57,g1)
    c: InternalAlignment(g58,g0)
    c: Equal(g58,g1)
    c: InternalAlignment(g59,g0)
    c: Equal(g59,g1)
    c: InternalAlignment(g60,g0)
    c: Equal(g60,g1)
    c: InternalAlignment(g61,g0)
    c: Equal(g61,g1)
    c: InternalAlignment(g62-g122 -> g0) x61
FEATURE [PartDesign::AdditiveLoft] AdditiveLoft002
  Closed = false
  Profile = -> Sketch007
  Refine = true
  Ruled = false
  Sections = -> [Sketch006]
  Suppressed = false
FEATURE [PartDesign::Plane] DatumPlane002
  AttachmentOffset = pos=(0,0,0) rot=(0,-1,0;0.785398rad)
  AttachmentSupport = -> [AdditiveLoft002]
  Length = 554.997
  MapMode = 5
  Placement = pos=(0,0,0) rot=(0,-1,0;0.785398rad)
  ResizeMode = 0
  Width = 85.8053
FEATURE [Sketcher::SketchObject] Sketch008
  ArcFitTolerance = 1e-06
  AttachmentSupport = -> [DatumPlane002]
  FullyConstrained = false
  MakeInternals = false
  MapMode = 5
  Placement = pos=(0,0,0) rot=(0,-1,0;0.785398rad)
  sketch-geometry (1):
    g0: Circle CenterX=28.3343 CenterY=4.75298 CenterZ=0 NormalX=0 NormalY=0 NormalZ=1 AngleXU=0 Radius=4.1
  constraints (1):
    c: Diameter(g0) = 8.2
FEATURE [PartDesign::Pocket] Pocket002
  BaseFeature = -> AdditiveLoft002
  Direction = (0.707107,0,-0.707107)
  Length = 1000
  Length2 = 5
  Profile = -> Sketch008
  ReferenceAxis = -> Sketch008 [N_Axis]
  Refine = true
  Suppressed = false
  Type = 0
FEATURE [Sketcher::SketchObject] Sketch009
  ArcFitTolerance = 1e-06
  FullyConstrained = false
  MakeInternals = false
  Placement = pos=(600,0,-600) rot=(0,0,1;0rad)
  sketch-geometry (123):
    g0: BSplineCurve PolesCount=61 KnotsCount=61 Degree=3 IsPeriodic=1
    g1-g61: Circle [constr] x61 (B-spline internal-alignment scaffolding for g0; pole/knot coordinates omitted)
    g62-g122: GeomPoint [constr] x61 (B-spline internal-alignment scaffolding for g0; pole/knot coordinates omitted)
  constraints (123):
    c: InternalAlignment(g1,g0)
    c: Weight(g1) = 1
    c: InternalAlignment(g2,g0)
    c: Equal(g2,g1)
    c: InternalAlignment(g3,g0)
    c: Equal(g3,g1)
    c: InternalAlignment(g4,g0)
    c: Equal(g4,g1)
    c: InternalAlignment(g5,g0)
    c: Equal(g5,g1)
    c: InternalAlignment(g6,g0)
    c: Equal(g6,g1)
    c: InternalAlignment(g7,g0)
    c: Equal(g7,g1)
    c: InternalAlignment(g8,g0)
    c: Equal(g8,g1)
    c: InternalAlignment(g9,g0)
    c: Equal(g9,g1)
    c: InternalAlignment(g10,g0)
    c: Equal(g10,g1)
    c: InternalAlignment(g11,g0)
    c: Equal(g11,g1)
    c: InternalAlignment(g12,g0)
    c: Equal(g12,g1)
    c: InternalAlignment(g13,g0)
    c: Equal(g13,g1)
    c: InternalAlignment(g14,g0)
    c: Equal(g14,g1)
    c: InternalAlignment(g15,g0)
    c: Equal(g15,g1)
    c: InternalAlignment(g16,g0)
    c: Equal(g16,g1)
    c: InternalAlignment(g17,g0)
    c: Equal(g17,g1)
    c: InternalAlignment(g18,g0)
    c: Equal(g18,g1)
    c: InternalAlignment(g19,g0)
    c: Equal(g19,g1)
    c: InternalAlignment(g20,g0)
    c: Equal(g20,g1)
    c: InternalAlignment(g21,g0)
    c: Equal(g21,g1)
    c: InternalAlignment(g22,g0)
    c: Equal(g22,g1)
    c: InternalAlignment(g23,g0)
    c: Equal(g23,g1)
    c: InternalAlignment(g24,g0)
    c: Equal(g24,g1)
    c: InternalAlignment(g25,g0)
    c: Equal(g25,g1)
    c: InternalAlignment(g26,g0)
    c: Equal(g26,g1)
    c: InternalAlignment(g27,g0)
    c: Equal(g27,g1)
    c: InternalAlignment(g28,g0)
    c: Equal(g28,g1)
    c: InternalAlignment(g29,g0)
    c: Equal(g29,g1)
    c: InternalAlignment(g30,g0)
    c: Equal(g30,g1)
    c: InternalAlignment(g31,g0)
    c: Equal(g31,g1)
    c: InternalAlignment(g32,g0)
    c: Equal(g32,g1)
    c: InternalAlignment(g33,g0)
    c: Equal(g33,g1)
    c: InternalAlignment(g34,g0)
    c: Equal(g34,g1)
    c: InternalAlignment(g35,g0)
    c: Equal(g35,g1)
    c: InternalAlignment(g36,g0)
    c: Equal(g36,g1)
    c: InternalAlignment(g37,g0)
    c: Equal(g37,g1)
    c: InternalAlignment(g38,g0)
    c: Equal(g38,g1)
    c: InternalAlignment(g39,g0)
    c: Equal(g39,g1)
    c: InternalAlignment(g40,g0)
    c: Equal(g40,g1)
    c: InternalAlignment(g41,g0)
    c: Equal(g41,g1)
    c: InternalAlignment(g42,g0)
    c: Equal(g42,g1)
    c: InternalAlignment(g43,g0)
    c: Equal(g43,g1)
    c: InternalAlignment(g44,g0)
    c: Equal(g44,g1)
    c: InternalAlignment(g45,g0)
    c: Equal(g45,g1)
    c: InternalAlignment(g46,g0)
    c: Equal(g46,g1)
    c: InternalAlignment(g47,g0)
    c: Equal(g47,g1)
    c: InternalAlignment(g48,g0)
    c: Equal(g48,g1)
    c: InternalAlignment(g49,g0)
    c: Equal(g49,g1)
    c: InternalAlignment(g50,g0)
    c: Equal(g50,g1)
    c: InternalAlignment(g51,g0)
    c: Equal(g51,g1)
    c: InternalAlignment(g52,g0)
    c: Equal(g52,g1)
    c: InternalAlignment(g53,g0)
    c: Equal(g53,g1)
    c: InternalAlignment(g54,g0)
    c: Equal(g54,g1)
    c: InternalAlignment(g55,g0)
    c: Equal(g55,g1)
    c: InternalAlignment(g56,g0)
    c: Equal(g56,g1)
    c: InternalAlignment(g57,g0)
    c: Equal(g57,g1)
    c: InternalAlignment(g58,g0)
    c: Equal(g58,g1)
    c: InternalAlignment(g59,g0)
    c: Equal(g59,g1)
    c: InternalAlignment(g60,g0)
    c: Equal(g60,g1)
    c: InternalAlignment(g61,g0)
    c: Equal(g61,g1)
    c: InternalAlignment(g62-g122 -> g0) x61
FEATURE [Sketcher::SketchObject] Sketch010
  ArcFitTolerance = 1e-06
  FullyConstrained = false
  MakeInternals = false
  sketch-geometry (123):
    g0: BSplineCurve PolesCount=61 KnotsCount=61 Degree=3 IsPeriodic=1
    g1-g61: Circle [constr] x61 (B-spline internal-alignment scaffolding for g0; pole/knot coordinates omitted)
    g62-g122: GeomPoint [constr] x61 (B-spline internal-alignment scaffolding for g0; pole/knot coordinates omitted)
  constraints (123):
    c: InternalAlignment(g1,g0)
    c: Weight(g1) = 1
    c: InternalAlignment(g2,g0)
    c: Equal(g2,g1)
    c: InternalAlignment(g3,g0)
    c: Equal(g3,g1)
    c: InternalAlignment(g4,g0)
    c: Equal(g4,g1)
    c: InternalAlignment(g5,g0)
    c: Equal(g5,g1)
    c: InternalAlignment(g6,g0)
    c: Equal(g6,g1)
    c: InternalAlignment(g7,g0)
    c: Equal(g7,g1)
    c: InternalAlignment(g8,g0)
    c: Equal(g8,g1)
    c: InternalAlignment(g9,g0)
    c: Equal(g9,g1)
    c: InternalAlignment(g10,g0)
    c: Equal(g10,g1)
    c: InternalAlignment(g11,g0)
    c: Equal(g11,g1)
    c: InternalAlignment(g12,g0)
    c: Equal(g12,g1)
    c: InternalAlignment(g13,g0)
    c: Equal(g13,g1)
    c: InternalAlignment(g14,g0)
    c: Equal(g14,g1)
    c: InternalAlignment(g15,g0)
    c: Equal(g15,g1)
    c: InternalAlignment(g16,g0)
    c: Equal(g16,g1)
    c: InternalAlignment(g17,g0)
    c: Equal(g17,g1)
    c: InternalAlignment(g18,g0)
    c: Equal(g18,g1)
    c: InternalAlignment(g19,g0)
    c: Equal(g19,g1)
    c: InternalAlignment(g20,g0)
    c: Equal(g20,g1)
    c: InternalAlignment(g21,g0)
    c: Equal(g21,g1)
    c: InternalAlignment(g22,g0)
    c: Equal(g22,g1)
    c: InternalAlignment(g23,g0)
    c: Equal(g23,g1)
    c: InternalAlignment(g24,g0)
    c: Equal(g24,g1)
    c: InternalAlignment(g25,g0)
    c: Equal(g25,g1)
    c: InternalAlignment(g26,g0)
    c: Equal(g26,g1)
    c: InternalAlignment(g27,g0)
    c: Equal(g27,g1)
    c: InternalAlignment(g28,g0)
    c: Equal(g28,g1)
    c: InternalAlignment(g29,g0)
    c: Equal(g29,g1)
    c: InternalAlignment(g30,g0)
    c: Equal(g30,g1)
    c: InternalAlignment(g31,g0)
    c: Equal(g31,g1)
    c: InternalAlignment(g32,g0)
    c: Equal(g32,g1)
    c: InternalAlignment(g33,g0)
    c: Equal(g33,g1)
    c: InternalAlignment(g34,g0)
    c: Equal(g34,g1)
    c: InternalAlignment(g35,g0)
    c: Equal(g35,g1)
    c: InternalAlignment(g36,g0)
    c: Equal(g36,g1)
    c: InternalAlignment(g37,g0)
    c: Equal(g37,g1)
    c: InternalAlignment(g38,g0)
    c: Equal(g38,g1)
    c: InternalAlignment(g39,g0)
    c: Equal(g39,g1)
    c: InternalAlignment(g40,g0)
    c: Equal(g40,g1)
    c: InternalAlignment(g41,g0)
    c: Equal(g41,g1)
    c: InternalAlignment(g42,g0)
    c: Equal(g42,g1)
    c: InternalAlignment(g43,g0)
    c: Equal(g43,g1)
    c: InternalAlignment(g44,g0)
    c: Equal(g44,g1)
    c: InternalAlignment(g45,g0)
    c: Equal(g45,g1)
    c: InternalAlignment(g46,g0)
    c: Equal(g46,g1)
    c: InternalAlignment(g47,g0)
    c: Equal(g47,g1)
    c: InternalAlignment(g48,g0)
    c: Equal(g48,g1)
    c: InternalAlignment(g49,g0)
    c: Equal(g49,g1)
    c: InternalAlignment(g50,g0)
    c: Equal(g50,g1)
    c: InternalAlignment(g51,g0)
    c: Equal(g51,g1)
    c: InternalAlignment(g52,g0)
    c: Equal(g52,g1)
    c: InternalAlignment(g53,g0)
    c: Equal(g53,g1)
    c: InternalAlignment(g54,g0)
    c: Equal(g54,g1)
    c: InternalAlignment(g55,g0)
    c: Equal(g55,g1)
    c: InternalAlignment(g56,g0)
    c: Equal(g56,g1)
    c: InternalAlignment(g57,g0)
    c: Equal(g57,g1)
    c: InternalAlignment(g58,g0)
    c: Equal(g58,g1)
    c: InternalAlignment(g59,g0)
    c: Equal(g59,g1)
    c: InternalAlignment(g60,g0)
    c: Equal(g60,g1)
    c: InternalAlignment(g61,g0)
    c: Equal(g61,g1)
    c: InternalAlignment(g62-g122 -> g0) x61
FEATURE [PartDesign::AdditiveLoft] AdditiveLoft003
  Closed = false
  Profile = -> Sketch010
  Refine = true
  Ruled = false
  Sections = -> [Sketch009]
  Suppressed = false
FEATURE [PartDesign::Plane] DatumPlane003
  AttachmentOffset = pos=(0,0,0) rot=(0,-1,0;0.785398rad)
  AttachmentSupport = -> [AdditiveLoft003]
  Length = 700.703
  MapMode = 5
  Placement = pos=(0,0,0) rot=(0,-1,0;0.785398rad)
  ResizeMode = 0
  Width = 86.4487
FEATURE [Sketcher::SketchObject] Sketch011
  ArcFitTolerance = 1e-06
  AttachmentSupport = -> [DatumPlane003]
  FullyConstrained = false
  MakeInternals = false
  MapMode = 5
  Placement = pos=(0,0,0) rot=(0,-1,0;0.785398rad)
  sketch-geometry (1):
    g0: Circle CenterX=28.3343 CenterY=4.75298 CenterZ=0 NormalX=0 NormalY=0 NormalZ=1 AngleXU=0 Radius=4.1
  constraints (1):
    c: Diameter(g0) = 8.2
FEATURE [PartDesign::Pocket] Pocket003
  BaseFeature = -> AdditiveLoft003
  Direction = (0.707107,0,-0.707107)
  Length = 1000
  Length2 = 5
  Profile = -> Sketch011
  ReferenceAxis = -> Sketch011 [N_Axis]
  Refine = true
  Suppressed = false
  Type = 0
FEATURE [Sketcher::SketchObject] Sketch012
  ArcFitTolerance = 1e-06
  FullyConstrained = false
  MakeInternals = false
  Placement = pos=(600,0,-600) rot=(0,0,1;0rad)
  sketch-geometry (123):
    g0: BSplineCurve PolesCount=61 KnotsCount=61 Degree=3 IsPeriodic=1
    g1-g61: Circle [constr] x61 (B-spline internal-alignment scaffolding for g0; pole/knot coordinates omitted)
    g62-g122: GeomPoint [constr] x61 (B-spline internal-alignment scaffolding for g0; pole/knot coordinates omitted)
  constraints (123):
    c: InternalAlignment(g1,g0)
    c: Weight(g1) = 1
    c: InternalAlignment(g2,g0)
    c: Equal(g2,g1)
    c: InternalAlignment(g3,g0)
    c: Equal(g3,g1)
    c: InternalAlignment(g4,g0)
    c: Equal(g4,g1)
    c: InternalAlignment(g5,g0)
    c: Equal(g5,g1)
    c: InternalAlignment(g6,g0)
    c: Equal(g6,g1)
    c: InternalAlignment(g7,g0)
    c: Equal(g7,g1)
    c: InternalAlignment(g8,g0)
    c: Equal(g8,g1)
    c: InternalAlignment(g9,g0)
    c: Equal(g9,g1)
    c: InternalAlignment(g10,g0)
    c: Equal(g10,g1)
    c: InternalAlignment(g11,g0)
    c: Equal(g11,g1)
    c: InternalAlignment(g12,g0)
    c: Equal(g12,g1)
    c: InternalAlignment(g13,g0)
    c: Equal(g13,g1)
    c: InternalAlignment(g14,g0)
    c: Equal(g14,g1)
    c: InternalAlignment(g15,g0)
    c: Equal(g15,g1)
    c: InternalAlignment(g16,g0)
    c: Equal(g16,g1)
    c: InternalAlignment(g17,g0)
    c: Equal(g17,g1)
    c: InternalAlignment(g18,g0)
    c: Equal(g18,g1)
    c: InternalAlignment(g19,g0)
    c: Equal(g19,g1)
    c: InternalAlignment(g20,g0)
    c: Equal(g20,g1)
    c: InternalAlignment(g21,g0)
    c: Equal(g21,g1)
    c: InternalAlignment(g22,g0)
    c: Equal(g22,g1)
    c: InternalAlignment(g23,g0)
    c: Equal(g23,g1)
    c: InternalAlignment(g24,g0)
    c: Equal(g24,g1)
    c: InternalAlignment(g25,g0)
    c: Equal(g25,g1)
    c: InternalAlignment(g26,g0)
    c: Equal(g26,g1)
    c: InternalAlignment(g27,g0)
    c: Equal(g27,g1)
    c: InternalAlignment(g28,g0)
    c: Equal(g28,g1)
    c: InternalAlignment(g29,g0)
    c: Equal(g29,g1)
    c: InternalAlignment(g30,g0)
    c: Equal(g30,g1)
    c: InternalAlignment(g31,g0)
    c: Equal(g31,g1)
    c: InternalAlignment(g32,g0)
    c: Equal(g32,g1)
    c: InternalAlignment(g33,g0)
    c: Equal(g33,g1)
    c: InternalAlignment(g34,g0)
    c: Equal(g34,g1)
    c: InternalAlignment(g35,g0)
    c: Equal(g35,g1)
    c: InternalAlignment(g36,g0)
    c: Equal(g36,g1)
    c: InternalAlignment(g37,g0)
    c: Equal(g37,g1)
    c: InternalAlignment(g38,g0)
    c: Equal(g38,g1)
    c: InternalAlignment(g39,g0)
    c: Equal(g39,g1)
    c: InternalAlignment(g40,g0)
    c: Equal(g40,g1)
    c: InternalAlignment(g41,g0)
    c: Equal(g41,g1)
    c: InternalAlignment(g42,g0)
    c: Equal(g42,g1)
    c: InternalAlignment(g43,g0)
    c: Equal(g43,g1)
    c: InternalAlignment(g44,g0)
    c: Equal(g44,g1)
    c: InternalAlignment(g45,g0)
    c: Equal(g45,g1)
    c: InternalAlignment(g46,g0)
    c: Equal(g46,g1)
    c: InternalAlignment(g47,g0)
    c: Equal(g47,g1)
    c: InternalAlignment(g48,g0)
    c: Equal(g48,g1)
    c: InternalAlignment(g49,g0)
    c: Equal(g49,g1)
    c: InternalAlignment(g50,g0)
    c: Equal(g50,g1)
    c: InternalAlignment(g51,g0)
    c: Equal(g51,g1)
    c: InternalAlignment(g52,g0)
    c: Equal(g52,g1)
    c: InternalAlignment(g53,g0)
    c: Equal(g53,g1)
    c: InternalAlignment(g54,g0)
    c: Equal(g54,g1)
    c: InternalAlignment(g55,g0)
    c: Equal(g55,g1)
    c: InternalAlignment(g56,g0)
    c: Equal(g56,g1)
    c: InternalAlignment(g57,g0)
    c: Equal(g57,g1)
    c: InternalAlignment(g58,g0)
    c: Equal(g58,g1)
    c: InternalAlignment(g59,g0)
    c: Equal(g59,g1)
    c: InternalAlignment(g60,g0)
    c: Equal(g60,g1)
    c: InternalAlignment(g61,g0)
    c: Equal(g61,g1)
    c: InternalAlignment(g62-g122 -> g0) x61
FEATURE [Sketcher::SketchObject] Sketch013
  ArcFitTolerance = 1e-06
  FullyConstrained = false
  MakeInternals = false
  sketch-geometry (123):
    g0: BSplineCurve PolesCount=61 KnotsCount=61 Degree=3 IsPeriodic=1
    g1-g61: Circle [constr] x61 (B-spline internal-alignment scaffolding for g0; pole/knot coordinates omitted)
    g62-g122: GeomPoint [constr] x61 (B-spline internal-alignment scaffolding for g0; pole/knot coordinates omitted)
  constraints (123):
    c: InternalAlignment(g1,g0)
    c: Weight(g1) = 1
    c: InternalAlignment(g2,g0)
    c: Equal(g2,g1)
    c: InternalAlignment(g3,g0)
    c: Equal(g3,g1)
    c: InternalAlignment(g4,g0)
    c: Equal(g4,g1)
    c: InternalAlignment(g5,g0)
    c: Equal(g5,g1)
    c: InternalAlignment(g6,g0)
    c: Equal(g6,g1)
    c: InternalAlignment(g7,g0)
    c: Equal(g7,g1)
    c: InternalAlignment(g8,g0)
    c: Equal(g8,g1)
    c: InternalAlignment(g9,g0)
    c: Equal(g9,g1)
    c: InternalAlignment(g10,g0)
    c: Equal(g10,g1)
    c: InternalAlignment(g11,g0)
    c: Equal(g11,g1)
    c: InternalAlignment(g12,g0)
    c: Equal(g12,g1)
    c: InternalAlignment(g13,g0)
    c: Equal(g13,g1)
    c: InternalAlignment(g14,g0)
    c: Equal(g14,g1)
    c: InternalAlignment(g15,g0)
    c: Equal(g15,g1)
    c: InternalAlignment(g16,g0)
    c: Equal(g16,g1)
    c: InternalAlignment(g17,g0)
    c: Equal(g17,g1)
    c: InternalAlignment(g18,g0)
    c: Equal(g18,g1)
    c: InternalAlignment(g19,g0)
    c: Equal(g19,g1)
    c: InternalAlignment(g20,g0)
    c: Equal(g20,g1)
    c: InternalAlignment(g21,g0)
    c: Equal(g21,g1)
    c: InternalAlignment(g22,g0)
    c: Equal(g22,g1)
    c: InternalAlignment(g23,g0)
    c: Equal(g23,g1)
    c: InternalAlignment(g24,g0)
    c: Equal(g24,g1)
    c: InternalAlignment(g25,g0)
    c: Equal(g25,g1)
    c: InternalAlignment(g26,g0)
    c: Equal(g26,g1)
    c: InternalAlignment(g27,g0)
    c: Equal(g27,g1)
    c: InternalAlignment(g28,g0)
    c: Equal(g28,g1)
    c: InternalAlignment(g29,g0)
    c: Equal(g29,g1)
    c: InternalAlignment(g30,g0)
    c: Equal(g30,g1)
    c: InternalAlignment(g31,g0)
    c: Equal(g31,g1)
    c: InternalAlignment(g32,g0)
    c: Equal(g32,g1)
    c: InternalAlignment(g33,g0)
    c: Equal(g33,g1)
    c: InternalAlignment(g34,g0)
    c: Equal(g34,g1)
    c: InternalAlignment(g35,g0)
    c: Equal(g35,g1)
    c: InternalAlignment(g36,g0)
    c: Equal(g36,g1)
    c: InternalAlignment(g37,g0)
    c: Equal(g37,g1)
    c: InternalAlignment(g38,g0)
    c: Equal(g38,g1)
    c: InternalAlignment(g39,g0)
    c: Equal(g39,g1)
    c: InternalAlignment(g40,g0)
    c: Equal(g40,g1)
    c: InternalAlignment(g41,g0)
    c: Equal(g41,g1)
    c: InternalAlignment(g42,g0)
    c: Equal(g42,g1)
    c: InternalAlignment(g43,g0)
    c: Equal(g43,g1)
    c: InternalAlignment(g44,g0)
    c: Equal(g44,g1)
    c: InternalAlignment(g45,g0)
    c: Equal(g45,g1)
    c: InternalAlignment(g46,g0)
    c: Equal(g46,g1)
    c: InternalAlignment(g47,g0)
    c: Equal(g47,g1)
    c: InternalAlignment(g48,g0)
    c: Equal(g48,g1)
    c: InternalAlignment(g49,g0)
    c: Equal(g49,g1)
    c: InternalAlignment(g50,g0)
    c: Equal(g50,g1)
    c: InternalAlignment(g51,g0)
    c: Equal(g51,g1)
    c: InternalAlignment(g52,g0)
    c: Equal(g52,g1)
    c: InternalAlignment(g53,g0)
    c: Equal(g53,g1)
    c: InternalAlignment(g54,g0)
    c: Equal(g54,g1)
    c: InternalAlignment(g55,g0)
    c: Equal(g55,g1)
    c: InternalAlignment(g56,g0)
    c: Equal(g56,g1)
    c: InternalAlignment(g57,g0)
    c: Equal(g57,g1)
    c: InternalAlignment(g58,g0)
    c: Equal(g58,g1)
    c: InternalAlignment(g59,g0)
    c: Equal(g59,g1)
    c: InternalAlignment(g60,g0)
    c: Equal(g60,g1)
    c: InternalAlignment(g61,g0)
    c: Equal(g61,g1)
    c: InternalAlignment(g62-g122 -> g0) x61
FEATURE [PartDesign::AdditiveLoft] AdditiveLoft004
  Closed = false
  Profile = -> Sketch013
  Refine = true
  Ruled = false
  Sections = -> [Sketch012]
  Suppressed = false
FEATURE [PartDesign::Plane] DatumPlane004
  AttachmentOffset = pos=(0,0,0) rot=(0,-1,0;0.785398rad)
  AttachmentSupport = -> [AdditiveLoft004]
  Length = 780.707
  MapMode = 5
  Placement = pos=(0,0,0) rot=(0,-1,0;0.785398rad)
  ResizeMode = 0
  Width = 88.5274
FEATURE [Sketcher::SketchObject] Sketch014
  ArcFitTolerance = 1e-06
  AttachmentSupport = -> [DatumPlane004]
  FullyConstrained = false
  MakeInternals = false
  MapMode = 5
  Placement = pos=(0,0,0) rot=(0,-1,0;0.785398rad)
  sketch-geometry (1):
    g0: Circle CenterX=28.3343 CenterY=4.75298 CenterZ=0 NormalX=0 NormalY=0 NormalZ=1 AngleXU=0 Radius=4.1
  constraints (1):
    c: Diameter(g0) = 8.2
FEATURE [PartDesign::Pocket] Pocket004
  BaseFeature = -> AdditiveLoft004
  Direction = (0.707107,0,-0.707107)
  Length = 1000
  Length2 = 5
  Profile = -> Sketch014
  ReferenceAxis = -> Sketch014 [N_Axis]
  Refine = true
  Suppressed = false
  Type = 0
FEATURE [Sketcher::SketchObject] Sketch015
  ArcFitTolerance = 1e-06
  FullyConstrained = false
  MakeInternals = false
  Placement = pos=(600,0,-600) rot=(0,0,1;0rad)
  sketch-geometry (123):
    g0: BSplineCurve PolesCount=61 KnotsCount=61 Degree=3 IsPeriodic=1
    g1-g61: Circle [constr] x61 (B-spline internal-alignment scaffolding for g0; pole/knot coordinates omitted)
    g62-g122: GeomPoint [constr] x61 (B-spline internal-alignment scaffolding for g0; pole/knot coordinates omitted)
  constraints (123):
    c: InternalAlignment(g1,g0)
    c: Weight(g1) = 1
    c: InternalAlignment(g2,g0)
    c: Equal(g2,g1)
    c: InternalAlignment(g3,g0)
    c: Equal(g3,g1)
    c: InternalAlignment(g4,g0)
    c: Equal(g4,g1)
    c: InternalAlignment(g5,g0)
    c: Equal(g5,g1)
    c: InternalAlignment(g6,g0)
    c: Equal(g6,g1)
    c: InternalAlignment(g7,g0)
    c: Equal(g7,g1)
    c: InternalAlignment(g8,g0)
    c: Equal(g8,g1)
    c: InternalAlignment(g9,g0)
    c: Equal(g9,g1)
    c: InternalAlignment(g10,g0)
    c: Equal(g10,g1)
    c: InternalAlignment(g11,g0)
    c: Equal(g11,g1)
    c: InternalAlignment(g12,g0)
    c: Equal(g12,g1)
    c: InternalAlignment(g13,g0)
    c: Equal(g13,g1)
    c: InternalAlignment(g14,g0)
    c: Equal(g14,g1)
    c: InternalAlignment(g15,g0)
    c: Equal(g15,g1)
    c: InternalAlignment(g16,g0)
    c: Equal(g16,g1)
    c: InternalAlignment(g17,g0)
    c: Equal(g17,g1)
    c: InternalAlignment(g18,g0)
    c: Equal(g18,g1)
    c: InternalAlignment(g19,g0)
    c: Equal(g19,g1)
    c: InternalAlignment(g20,g0)
    c: Equal(g20,g1)
    c: InternalAlignment(g21,g0)
    c: Equal(g21,g1)
    c: InternalAlignment(g22,g0)
    c: Equal(g22,g1)
    c: InternalAlignment(g23,g0)
    c: Equal(g23,g1)
    c: InternalAlignment(g24,g0)
    c: Equal(g24,g1)
    c: InternalAlignment(g25,g0)
    c: Equal(g25,g1)
    c: InternalAlignment(g26,g0)
    c: Equal(g26,g1)
    c: InternalAlignment(g27,g0)
    c: Equal(g27,g1)
    c: InternalAlignment(g28,g0)
    c: Equal(g28,g1)
    c: InternalAlignment(g29,g0)
    c: Equal(g29,g1)
    c: InternalAlignment(g30,g0)
    c: Equal(g30,g1)
    c: InternalAlignment(g31,g0)
    c: Equal(g31,g1)
    c: InternalAlignment(g32,g0)
    c: Equal(g32,g1)
    c: InternalAlignment(g33,g0)
    c: Equal(g33,g1)
    c: InternalAlignment(g34,g0)
    c: Equal(g34,g1)
    c: InternalAlignment(g35,g0)
    c: Equal(g35,g1)
    c: InternalAlignment(g36,g0)
    c: Equal(g36,g1)
    c: InternalAlignment(g37,g0)
    c: Equal(g37,g1)
    c: InternalAlignment(g38,g0)
    c: Equal(g38,g1)
    c: InternalAlignment(g39,g0)
    c: Equal(g39,g1)
    c: InternalAlignment(g40,g0)
    c: Equal(g40,g1)
    c: InternalAlignment(g41,g0)
    c: Equal(g41,g1)
    c: InternalAlignment(g42,g0)
    c: Equal(g42,g1)
    c: InternalAlignment(g43,g0)
    c: Equal(g43,g1)
    c: InternalAlignment(g44,g0)
    c: Equal(g44,g1)
    c: InternalAlignment(g45,g0)
    c: Equal(g45,g1)
    c: InternalAlignment(g46,g0)
    c: Equal(g46,g1)
    c: InternalAlignment(g47,g0)
    c: Equal(g47,g1)
    c: InternalAlignment(g48,g0)
    c: Equal(g48,g1)
    c: InternalAlignment(g49,g0)
    c: Equal(g49,g1)
    c: InternalAlignment(g50,g0)
    c: Equal(g50,g1)
    c: InternalAlignment(g51,g0)
    c: Equal(g51,g1)
    c: InternalAlignment(g52,g0)
    c: Equal(g52,g1)
    c: InternalAlignment(g53,g0)
    c: Equal(g53,g1)
    c: InternalAlignment(g54,g0)
    c: Equal(g54,g1)
    c: InternalAlignment(g55,g0)
    c: Equal(g55,g1)
    c: InternalAlignment(g56,g0)
    c: Equal(g56,g1)
    c: InternalAlignment(g57,g0)
    c: Equal(g57,g1)
    c: InternalAlignment(g58,g0)
    c: Equal(g58,g1)
    c: InternalAlignment(g59,g0)
    c: Equal(g59,g1)
    c: InternalAlignment(g60,g0)
    c: Equal(g60,g1)
    c: InternalAlignment(g61,g0)
    c: Equal(g61,g1)
    c: InternalAlignment(g62-g122 -> g0) x61
FEATURE [Sketcher::SketchObject] Sketch016
  ArcFitTolerance = 1e-06
  FullyConstrained = false
  MakeInternals = false
  sketch-geometry (123):
    g0: BSplineCurve PolesCount=61 KnotsCount=61 Degree=3 IsPeriodic=1
    g1-g61: Circle [constr] x61 (B-spline internal-alignment scaffolding for g0; pole/knot coordinates omitted)
    g62-g122: GeomPoint [constr] x61 (B-spline internal-alignment scaffolding for g0; pole/knot coordinates omitted)
  constraints (123):
    c: InternalAlignment(g1,g0)
    c: Weight(g1) = 1
    c: InternalAlignment(g2,g0)
    c: Equal(g2,g1)
    c: InternalAlignment(g3,g0)
    c: Equal(g3,g1)
    c: InternalAlignment(g4,g0)
    c: Equal(g4,g1)
    c: InternalAlignment(g5,g0)
    c: Equal(g5,g1)
    c: InternalAlignment(g6,g0)
    c: Equal(g6,g1)
    c: InternalAlignment(g7,g0)
    c: Equal(g7,g1)
    c: InternalAlignment(g8,g0)
    c: Equal(g8,g1)
    c: InternalAlignment(g9,g0)
    c: Equal(g9,g1)
    c: InternalAlignment(g10,g0)
    c: Equal(g10,g1)
    c: InternalAlignment(g11,g0)
    c: Equal(g11,g1)
    c: InternalAlignment(g12,g0)
    c: Equal(g12,g1)
    c: InternalAlignment(g13,g0)
    c: Equal(g13,g1)
    c: InternalAlignment(g14,g0)
    c: Equal(g14,g1)
    c: InternalAlignment(g15,g0)
    c: Equal(g15,g1)
    c: InternalAlignment(g16,g0)
    c: Equal(g16,g1)
    c: InternalAlignment(g17,g0)
    c: Equal(g17,g1)
    c: InternalAlignment(g18,g0)
    c: Equal(g18,g1)
    c: InternalAlignment(g19,g0)
    c: Equal(g19,g1)
    c: InternalAlignment(g20,g0)
    c: Equal(g20,g1)
    c: InternalAlignment(g21,g0)
    c: Equal(g21,g1)
    c: InternalAlignment(g22,g0)
    c: Equal(g22,g1)
    c: InternalAlignment(g23,g0)
    c: Equal(g23,g1)
    c: InternalAlignment(g24,g0)
    c: Equal(g24,g1)
    c: InternalAlignment(g25,g0)
    c: Equal(g25,g1)
    c: InternalAlignment(g26,g0)
    c: Equal(g26,g1)
    c: InternalAlignment(g27,g0)
    c: Equal(g27,g1)
    c: InternalAlignment(g28,g0)
    c: Equal(g28,g1)
    c: InternalAlignment(g29,g0)
    c: Equal(g29,g1)
    c: InternalAlignment(g30,g0)
    c: Equal(g30,g1)
    c: InternalAlignment(g31,g0)
    c: Equal(g31,g1)
    c: InternalAlignment(g32,g0)
    c: Equal(g32,g1)
    c: InternalAlignment(g33,g0)
    c: Equal(g33,g1)
    c: InternalAlignment(g34,g0)
    c: Equal(g34,g1)
    c: InternalAlignment(g35,g0)
    c: Equal(g35,g1)
    c: InternalAlignment(g36,g0)
    c: Equal(g36,g1)
    c: InternalAlignment(g37,g0)
    c: Equal(g37,g1)
    c: InternalAlignment(g38,g0)
    c: Equal(g38,g1)
    c: InternalAlignment(g39,g0)
    c: Equal(g39,g1)
    c: InternalAlignment(g40,g0)
    c: Equal(g40,g1)
    c: InternalAlignment(g41,g0)
    c: Equal(g41,g1)
    c: InternalAlignment(g42,g0)
    c: Equal(g42,g1)
    c: InternalAlignment(g43,g0)
    c: Equal(g43,g1)
    c: InternalAlignment(g44,g0)
    c: Equal(g44,g1)
    c: InternalAlignment(g45,g0)
    c: Equal(g45,g1)
    c: InternalAlignment(g46,g0)
    c: Equal(g46,g1)
    c: InternalAlignment(g47,g0)
    c: Equal(g47,g1)
    c: InternalAlignment(g48,g0)
    c: Equal(g48,g1)
    c: InternalAlignment(g49,g0)
    c: Equal(g49,g1)
    c: InternalAlignment(g50,g0)
    c: Equal(g50,g1)
    c: InternalAlignment(g51,g0)
    c: Equal(g51,g1)
    c: InternalAlignment(g52,g0)
    c: Equal(g52,g1)
    c: InternalAlignment(g53,g0)
    c: Equal(g53,g1)
    c: InternalAlignment(g54,g0)
    c: Equal(g54,g1)
    c: InternalAlignment(g55,g0)
    c: Equal(g55,g1)
    c: InternalAlignment(g56,g0)
    c: Equal(g56,g1)
    c: InternalAlignment(g57,g0)
    c: Equal(g57,g1)
    c: InternalAlignment(g58,g0)
    c: Equal(g58,g1)
    c: InternalAlignment(g59,g0)
    c: Equal(g59,g1)
    c: InternalAlignment(g60,g0)
    c: Equal(g60,g1)
    c: InternalAlignment(g61,g0)
    c: Equal(g61,g1)
    c: InternalAlignment(g62-g122 -> g0) x61
FEATURE [PartDesign::AdditiveLoft] AdditiveLoft005
  Closed = false
  Profile = -> Sketch016
  Refine = true
  Ruled = false
  Sections = -> [Sketch015]
  Suppressed = false
FEATURE [PartDesign::Plane] DatumPlane005
  AttachmentOffset = pos=(0,0,0) rot=(0,-1,0;0.785398rad)
  AttachmentSupport = -> [AdditiveLoft005]
  Length = 979.625
  MapMode = 5
  Placement = pos=(0,0,0) rot=(0,-1,0;0.785398rad)
  ResizeMode = 0
  Width = 93.2747
FEATURE [Sketcher::SketchObject] Sketch017
  ArcFitTolerance = 1e-06
  AttachmentSupport = -> [DatumPlane005]
  FullyConstrained = false
  MakeInternals = false
  MapMode = 5
  Placement = pos=(0,0,0) rot=(0,-1,0;0.785398rad)
  sketch-geometry (1):
    g0: Circle CenterX=28.3343 CenterY=4.75298 CenterZ=0 NormalX=0 NormalY=0 NormalZ=1 AngleXU=0 Radius=4.1
  constraints (1):
    c: Diameter(g0) = 8.2
FEATURE [PartDesign::Pocket] Pocket005
  BaseFeature = -> AdditiveLoft005
  Direction = (0.707107,0,-0.707107)
  Length = 1000
  Length2 = 5
  Profile = -> Sketch017
  ReferenceAxis = -> Sketch017 [N_Axis]
  Refine = true
  Suppressed = false
  Type = 0
FEATURE [Sketcher::SketchObject] Sketch018
  ArcFitTolerance = 1e-06
  FullyConstrained = false
  MakeInternals = false
  Placement = pos=(600,0,-600) rot=(0,0,1;0rad)
  sketch-geometry (123):
    g0: BSplineCurve PolesCount=61 KnotsCount=61 Degree=3 IsPeriodic=1
    g1-g61: Circle [constr] x61 (B-spline internal-alignment scaffolding for g0; pole/knot coordinates omitted)
    g62-g122: GeomPoint [constr] x61 (B-spline internal-alignment scaffolding for g0; pole/knot coordinates omitted)
  constraints (123):
    c: InternalAlignment(g1,g0)
    c: Weight(g1) = 1
    c: InternalAlignment(g2,g0)
    c: Equal(g2,g1)
    c: InternalAlignment(g3,g0)
    c: Equal(g3,g1)
    c: InternalAlignment(g4,g0)
    c: Equal(g4,g1)
    c: InternalAlignment(g5,g0)
    c: Equal(g5,g1)
    c: InternalAlignment(g6,g0)
    c: Equal(g6,g1)
    c: InternalAlignment(g7,g0)
    c: Equal(g7,g1)
    c: InternalAlignment(g8,g0)
    c: Equal(g8,g1)
    c: InternalAlignment(g9,g0)
    c: Equal(g9,g1)
    c: InternalAlignment(g10,g0)
    c: Equal(g10,g1)
    c: InternalAlignment(g11,g0)
    c: Equal(g11,g1)
    c: InternalAlignment(g12,g0)
    c: Equal(g12,g1)
    c: InternalAlignment(g13,g0)
    c: Equal(g13,g1)
    c: InternalAlignment(g14,g0)
    c: Equal(g14,g1)
    c: InternalAlignment(g15,g0)
    c: Equal(g15,g1)
    c: InternalAlignment(g16,g0)
    c: Equal(g16,g1)
    c: InternalAlignment(g17,g0)
    c: Equal(g17,g1)
    c: InternalAlignment(g18,g0)
    c: Equal(g18,g1)
    c: InternalAlignment(g19,g0)
    c: Equal(g19,g1)
    c: InternalAlignment(g20,g0)
    c: Equal(g20,g1)
    c: InternalAlignment(g21,g0)
    c: Equal(g21,g1)
    c: InternalAlignment(g22,g0)
    c: Equal(g22,g1)
    c: InternalAlignment(g23,g0)
    c: Equal(g23,g1)
    c: InternalAlignment(g24,g0)
    c: Equal(g24,g1)
    c: InternalAlignment(g25,g0)
    c: Equal(g25,g1)
    c: InternalAlignment(g26,g0)
    c: Equal(g26,g1)
    c: InternalAlignment(g27,g0)
    c: Equal(g27,g1)
    c: InternalAlignment(g28,g0)
    c: Equal(g28,g1)
    c: InternalAlignment(g29,g0)
    c: Equal(g29,g1)
    c: InternalAlignment(g30,g0)
    c: Equal(g30,g1)
    c: InternalAlignment(g31,g0)
    c: Equal(g31,g1)
    c: InternalAlignment(g32,g0)
    c: Equal(g32,g1)
    c: InternalAlignment(g33,g0)
    c: Equal(g33,g1)
    c: InternalAlignment(g34,g0)
    c: Equal(g34,g1)
    c: InternalAlignment(g35,g0)
    c: Equal(g35,g1)
    c: InternalAlignment(g36,g0)
    c: Equal(g36,g1)
    c: InternalAlignment(g37,g0)
    c: Equal(g37,g1)
    c: InternalAlignment(g38,g0)
    c: Equal(g38,g1)
    c: InternalAlignment(g39,g0)
    c: Equal(g39,g1)
    c: InternalAlignment(g40,g0)
    c: Equal(g40,g1)
    c: InternalAlignment(g41,g0)
    c: Equal(g41,g1)
    c: InternalAlignment(g42,g0)
    c: Equal(g42,g1)
    c: InternalAlignment(g43,g0)
    c: Equal(g43,g1)
    c: InternalAlignment(g44,g0)
    c: Equal(g44,g1)
    c: InternalAlignment(g45,g0)
    c: Equal(g45,g1)
    c: InternalAlignment(g46,g0)
    c: Equal(g46,g1)
    c: InternalAlignment(g47,g0)
    c: Equal(g47,g1)
    c: InternalAlignment(g48,g0)
    c: Equal(g48,g1)
    c: InternalAlignment(g49,g0)
    c: Equal(g49,g1)
    c: InternalAlignment(g50,g0)
    c: Equal(g50,g1)
    c: InternalAlignment(g51,g0)
    c: Equal(g51,g1)
    c: InternalAlignment(g52,g0)
    c: Equal(g52,g1)
    c: InternalAlignment(g53,g0)
    c: Equal(g53,g1)
    c: InternalAlignment(g54,g0)
    c: Equal(g54,g1)
    c: InternalAlignment(g55,g0)
    c: Equal(g55,g1)
    c: InternalAlignment(g56,g0)
    c: Equal(g56,g1)
    c: InternalAlignment(g57,g0)
    c: Equal(g57,g1)
    c: InternalAlignment(g58,g0)
    c: Equal(g58,g1)
    c: InternalAlignment(g59,g0)
    c: Equal(g59,g1)
    c: InternalAlignment(g60,g0)
    c: Equal(g60,g1)
    c: InternalAlignment(g61,g0)
    c: Equal(g61,g1)
    c: InternalAlignment(g62-g122 -> g0) x61
FEATURE [Sketcher::SketchObject] Sketch019
  ArcFitTolerance = 1e-06
  FullyConstrained = false
  MakeInternals = false
  sketch-geometry (123):
    g0: BSplineCurve PolesCount=61 KnotsCount=61 Degree=3 IsPeriodic=1
    g1-g61: Circle [constr] x61 (B-spline internal-alignment scaffolding for g0; pole/knot coordinates omitted)
    g62-g122: GeomPoint [constr] x61 (B-spline internal-alignment scaffolding for g0; pole/knot coordinates omitted)
  constraints (123):
    c: InternalAlignment(g1,g0)
    c: Weight(g1) = 1
    c: InternalAlignment(g2,g0)
    c: Equal(g2,g1)
    c: InternalAlignment(g3,g0)
    c: Equal(g3,g1)
    c: InternalAlignment(g4,g0)
    c: Equal(g4,g1)
    c: InternalAlignment(g5,g0)
    c: Equal(g5,g1)
    c: InternalAlignment(g6,g0)
    c: Equal(g6,g1)
    c: InternalAlignment(g7,g0)
    c: Equal(g7,g1)
    c: InternalAlignment(g8,g0)
    c: Equal(g8,g1)
    c: InternalAlignment(g9,g0)
    c: Equal(g9,g1)
    c: InternalAlignment(g10,g0)
    c: Equal(g10,g1)
    c: InternalAlignment(g11,g0)
    c: Equal(g11,g1)
    c: InternalAlignment(g12,g0)
    c: Equal(g12,g1)
    c: InternalAlignment(g13,g0)
    c: Equal(g13,g1)
    c: InternalAlignment(g14,g0)
    c: Equal(g14,g1)
    c: InternalAlignment(g15,g0)
    c: Equal(g15,g1)
    c: InternalAlignment(g16,g0)
    c: Equal(g16,g1)
    c: InternalAlignment(g17,g0)
    c: Equal(g17,g1)
    c: InternalAlignment(g18,g0)
    c: Equal(g18,g1)
    c: InternalAlignment(g19,g0)
    c: Equal(g19,g1)
    c: InternalAlignment(g20,g0)
    c: Equal(g20,g1)
    c: InternalAlignment(g21,g0)
    c: Equal(g21,g1)
    c: InternalAlignment(g22,g0)
    c: Equal(g22,g1)
    c: InternalAlignment(g23,g0)
    c: Equal(g23,g1)
    c: InternalAlignment(g24,g0)
    c: Equal(g24,g1)
    c: InternalAlignment(g25,g0)
    c: Equal(g25,g1)
    c: InternalAlignment(g26,g0)
    c: Equal(g26,g1)
    c: InternalAlignment(g27,g0)
    c: Equal(g27,g1)
    c: InternalAlignment(g28,g0)
    c: Equal(g28,g1)
    c: InternalAlignment(g29,g0)
    c: Equal(g29,g1)
    c: InternalAlignment(g30,g0)
    c: Equal(g30,g1)
    c: InternalAlignment(g31,g0)
    c: Equal(g31,g1)
    c: InternalAlignment(g32,g0)
    c: Equal(g32,g1)
    c: InternalAlignment(g33,g0)
    c: Equal(g33,g1)
    c: InternalAlignment(g34,g0)
    c: Equal(g34,g1)
    c: InternalAlignment(g35,g0)
    c: Equal(g35,g1)
    c: InternalAlignment(g36,g0)
    c: Equal(g36,g1)
    c: InternalAlignment(g37,g0)
    c: Equal(g37,g1)
    c: InternalAlignment(g38,g0)
    c: Equal(g38,g1)
    c: InternalAlignment(g39,g0)
    c: Equal(g39,g1)
    c: InternalAlignment(g40,g0)
    c: Equal(g40,g1)
    c: InternalAlignment(g41,g0)
    c: Equal(g41,g1)
    c: InternalAlignment(g42,g0)
    c: Equal(g42,g1)
    c: InternalAlignment(g43,g0)
    c: Equal(g43,g1)
    c: InternalAlignment(g44,g0)
    c: Equal(g44,g1)
    c: InternalAlignment(g45,g0)
    c: Equal(g45,g1)
    c: InternalAlignment(g46,g0)
    c: Equal(g46,g1)
    c: InternalAlignment(g47,g0)
    c: Equal(g47,g1)
    c: InternalAlignment(g48,g0)
    c: Equal(g48,g1)
    c: InternalAlignment(g49,g0)
    c: Equal(g49,g1)
    c: InternalAlignment(g50,g0)
    c: Equal(g50,g1)
    c: InternalAlignment(g51,g0)
    c: Equal(g51,g1)
    c: InternalAlignment(g52,g0)
    c: Equal(g52,g1)
    c: InternalAlignment(g53,g0)
    c: Equal(g53,g1)
    c: InternalAlignment(g54,g0)
    c: Equal(g54,g1)
    c: InternalAlignment(g55,g0)
    c: Equal(g55,g1)
    c: InternalAlignment(g56,g0)
    c: Equal(g56,g1)
    c: InternalAlignment(g57,g0)
    c: Equal(g57,g1)
    c: InternalAlignment(g58,g0)
    c: Equal(g58,g1)
    c: InternalAlignment(g59,g0)
    c: Equal(g59,g1)
    c: InternalAlignment(g60,g0)
    c: Equal(g60,g1)
    c: InternalAlignment(g61,g0)
    c: Equal(g61,g1)
    c: InternalAlignment(g62-g122 -> g0) x61
FEATURE [PartDesign::AdditiveLoft] AdditiveLoft006
  Closed = false
  Profile = -> Sketch019
  Refine = true
  Ruled = false
  Sections = -> [Sketch018]
  Suppressed = false
FEATURE [PartDesign::Plane] DatumPlane006
  AttachmentOffset = pos=(0,0,0) rot=(0,-1,0;0.785398rad)
  AttachmentSupport = -> [AdditiveLoft006]
  Length = 1085.8
  MapMode = 5
  Placement = pos=(0,0,0) rot=(0,-1,0;0.785398rad)
  ResizeMode = 0
  Width = 95.6111
FEATURE [Sketcher::SketchObject] Sketch020
  ArcFitTolerance = 1e-06
  AttachmentSupport = -> [DatumPlane006]
  FullyConstrained = false
  MakeInternals = false
  MapMode = 5
  Placement = pos=(0,0,0) rot=(0,-1,0;0.785398rad)
  sketch-geometry (1):
    g0: Circle CenterX=28.3343 CenterY=4.75298 CenterZ=0 NormalX=0 NormalY=0 NormalZ=1 AngleXU=0 Radius=4.1
  constraints (1):
    c: Diameter(g0) = 8.2
FEATURE [PartDesign::Pocket] Pocket006
  BaseFeature = -> AdditiveLoft006
  Direction = (0.707107,0,-0.707107)
  Length = 1000
  Length2 = 5
  Profile = -> Sketch020
  ReferenceAxis = -> Sketch020 [N_Axis]
  Refine = true
  Suppressed = false
  Type = 0
FEATURE [Sketcher::SketchObject] Sketch021
  ArcFitTolerance = 1e-06
  AttachmentSupport = -> [Pocket]
  FullyConstrained = false
  MakeInternals = false
  MapMode = 5
  Placement = pos=(0,0,-600) rot=(1,0,0;3.14159rad)
  sketch-geometry (4):
    g0: LineSegment StartX=-85.1873 StartY=206.739 StartZ=0 EndX=-85.1873 EndY=-145.098 EndZ=0
    g1: LineSegment StartX=-85.1873 StartY=-145.098 StartZ=0 EndX=963.672 EndY=-145.098 EndZ=0
    g2: LineSegment StartX=963.672 StartY=-145.098 StartZ=0 EndX=963.672 EndY=206.739 EndZ=0
    g3: LineSegment StartX=963.672 StartY=206.739 StartZ=0 EndX=-85.1873 EndY=206.739 EndZ=0
  constraints (8):
    c: Coincident(g0,g1)
    c: Coincident(g1,g2)
    c: Coincident(g2,g3)
    c: Coincident(g3,g0)
    c: Vertical(g0)
    c: Vertical(g2)
    c: Horizontal(g1)
    c: Horizontal(g3)
FEATURE [PartDesign::Pocket] Pocket007
  BaseFeature = -> Pocket
  Direction = (0,0,1)
  Length = 590
  Length2 = 5
  Profile = -> Sketch021
  ReferenceAxis = -> Sketch021 [N_Axis]
  Refine = true
  Suppressed = false
  Type = 0
FEATURE [Sketcher::SketchObject] Sketch022
  ArcFitTolerance = 1e-06
  AttachmentSupport = -> [Pocket001]
  FullyConstrained = false
  MakeInternals = false
  MapMode = 5
  sketch-geometry (4):
    g0: LineSegment StartX=-74.3122 StartY=118.602 StartZ=0 EndX=-74.3122 EndY=-69.0004 EndZ=0
    g1: LineSegment StartX=-74.3122 StartY=-69.0005 StartZ=0 EndX=870.96 EndY=-69.0005 EndZ=0
    g2: LineSegment StartX=870.96 StartY=-69.0005 StartZ=0 EndX=870.96 EndY=118.602 EndZ=0
    g3: LineSegment StartX=870.96 StartY=118.602 StartZ=0 EndX=-74.3122 EndY=118.602 EndZ=0
  constraints (8):
    c: Coincident(g0,g1)
    c: Coincident(g1,g2)
    c: Coincident(g2,g3)
    c: Coincident(g3,g0)
    c: Vertical(g0)
    c: Vertical(g2)
    c: Horizontal(g1)
    c: Horizontal(g3)
FEATURE [PartDesign::Pocket] Pocket008
  BaseFeature = -> Pocket001
  Direction = (0,0,-1)
  Length = 100
  Length2 = 5
  Profile = -> Sketch022
  ReferenceAxis = -> Sketch022 [N_Axis]
  Refine = true
  Suppressed = false
  Type = 0
FEATURE [Sketcher::SketchObject] Sketch023
  ArcFitTolerance = 1e-06
  AttachmentSupport = -> [Pocket008]
  FullyConstrained = false
  MakeInternals = false
  MapMode = 5
  Placement = pos=(0,0,-600) rot=(1,0,0;3.14159rad)
  sketch-geometry (4):
    g0: LineSegment StartX=26.9533 StartY=164.686 StartZ=0 EndX=26.9533 EndY=-77.9053 EndZ=0
    g1: LineSegment StartX=26.9533 StartY=-77.9053 StartZ=0 EndX=1059.07 EndY=-77.9053 EndZ=0
    g2: LineSegment StartX=1059.07 StartY=-77.9053 StartZ=0 EndX=1059.07 EndY=164.686 EndZ=0
    g3: LineSegment StartX=1059.07 StartY=164.686 StartZ=0 EndX=26.9533 EndY=164.686 EndZ=0
  constraints (8):
    c: Coincident(g0,g1)
    c: Coincident(g1,g2)
    c: Coincident(g2,g3)
    c: Coincident(g3,g0)
    c: Vertical(g0)
    c: Vertical(g2)
    c: Horizontal(g1)
    c: Horizontal(g3)
FEATURE [PartDesign::Pocket] Pocket009
  BaseFeature = -> Pocket008
  Direction = (0,0,1)
  Length = 490
  Length2 = 5
  Profile = -> Sketch023
  ReferenceAxis = -> Sketch023 [N_Axis]
  Refine = true
  Suppressed = false
  Type = 0
FEATURE [Sketcher::SketchObject] Sketch024
  ArcFitTolerance = 1e-06
  AttachmentSupport = -> [Pocket002]
  FullyConstrained = false
  MakeInternals = false
  MapMode = 5
  sketch-geometry (4):
    g0: LineSegment StartX=-34.6749 StartY=103.814 StartZ=0 EndX=-34.6749 EndY=-124.102 EndZ=0
    g1: LineSegment StartX=-34.6749 StartY=-124.102 StartZ=0 EndX=635.695 EndY=-124.102 EndZ=0
    g2: LineSegment StartX=635.695 StartY=-124.102 StartZ=0 EndX=635.695 EndY=103.814 EndZ=0
    g3: LineSegment StartX=635.695 StartY=103.814 StartZ=0 EndX=-34.6749 EndY=103.814 EndZ=0
  constraints (8):
    c: Coincident(g0,g1)
    c: Coincident(g1,g2)
    c: Coincident(g2,g3)
    c: Coincident(g3,g0)
    c: Vertical(g0)
    c: Vertical(g2)
    c: Horizontal(g1)
    c: Horizontal(g3)
FEATURE [PartDesign::Pocket] Pocket010
  BaseFeature = -> Pocket002
  Direction = (0,0,-1)
  Length = 200
  Length2 = 5
  Profile = -> Sketch024
  ReferenceAxis = -> Sketch024 [N_Axis]
  Refine = true
  Suppressed = false
  Type = 0
FEATURE [Sketcher::SketchObject] Sketch025
  ArcFitTolerance = 1e-06
  AttachmentSupport = -> [Pocket010]
  FullyConstrained = false
  MakeInternals = false
  MapMode = 5
  Placement = pos=(0,0,-600) rot=(1,0,0;3.14159rad)
  sketch-geometry (4):
    g0: LineSegment StartX=120.377 StartY=171.986 StartZ=0 EndX=120.377 EndY=-157.538 EndZ=0
    g1: LineSegment StartX=120.377 StartY=-157.538 StartZ=0 EndX=998.806 EndY=-157.538 EndZ=0
    g2: LineSegment StartX=998.806 StartY=-157.538 StartZ=0 EndX=998.806 EndY=171.986 EndZ=0
    g3: LineSegment StartX=998.806 StartY=171.986 StartZ=0 EndX=120.377 EndY=171.986 EndZ=0
  constraints (8):
    c: Coincident(g0,g1)
    c: Coincident(g1,g2)
    c: Coincident(g2,g3)
    c: Coincident(g3,g0)
    c: Vertical(g0)
    c: Vertical(g2)
    c: Horizontal(g1)
    c: Horizontal(g3)
FEATURE [PartDesign::Pocket] Pocket011
  BaseFeature = -> Pocket010
  Direction = (0,0,1)
  Length = 390
  Length2 = 5
  Profile = -> Sketch025
  ReferenceAxis = -> Sketch025 [N_Axis]
  Refine = true
  Suppressed = false
  Type = 0
FEATURE [Sketcher::SketchObject] Sketch026
  ArcFitTolerance = 1e-06
  AttachmentSupport = -> [Pocket003]
  FullyConstrained = false
  MakeInternals = false
  MapMode = 5
  sketch-geometry (4):
    g0: LineSegment StartX=-344.991 StartY=348.339 StartZ=0 EndX=-344.991 EndY=-308.863 EndZ=0
    g1: LineSegment StartX=-344.991 StartY=-308.863 StartZ=0 EndX=993.672 EndY=-308.863 EndZ=0
    g2: LineSegment StartX=993.672 StartY=-308.863 StartZ=0 EndX=993.672 EndY=348.339 EndZ=0
    g3: LineSegment StartX=993.672 StartY=348.339 StartZ=0 EndX=-344.991 EndY=348.339 EndZ=0
  constraints (8):
    c: Coincident(g0,g1)
    c: Coincident(g1,g2)
    c: Coincident(g2,g3)
    c: Coincident(g3,g0)
    c: Vertical(g0)
    c: Vertical(g2)
    c: Horizontal(g1)
    c: Horizontal(g3)
FEATURE [PartDesign::Pocket] Pocket012
  BaseFeature = -> Pocket003
  Direction = (0,0,-1)
  Length = 300
  Length2 = 5
  Profile = -> Sketch026
  ReferenceAxis = -> Sketch026 [N_Axis]
  Refine = true
  Suppressed = false
  Type = 0
FEATURE [Sketcher::SketchObject] Sketch027
  ArcFitTolerance = 1e-06
  AttachmentSupport = -> [Pocket012]
  FullyConstrained = false
  MakeInternals = false
  MapMode = 5
  Placement = pos=(0,0,-600) rot=(1,0,0;3.14159rad)
  sketch-geometry (4):
    g0: LineSegment StartX=196.967 StartY=129.212 StartZ=0 EndX=196.967 EndY=-99.542 EndZ=0
    g1: LineSegment StartX=196.967 StartY=-99.542 StartZ=0 EndX=981.265 EndY=-99.542 EndZ=0
    g2: LineSegment StartX=981.265 StartY=-99.542 StartZ=0 EndX=981.265 EndY=129.212 EndZ=0
    g3: LineSegment StartX=981.265 StartY=129.212 StartZ=0 EndX=196.967 EndY=129.212 EndZ=0
  constraints (8):
    c: Coincident(g0,g1)
    c: Coincident(g1,g2)
    c: Coincident(g2,g3)
    c: Coincident(g3,g0)
    c: Vertical(g0)
    c: Vertical(g2)
    c: Horizontal(g1)
    c: Horizontal(g3)
FEATURE [PartDesign::Pocket] Pocket013
  BaseFeature = -> Pocket012
  Direction = (0,0,1)
  Length = 290
  Length2 = 5
  Profile = -> Sketch027
  ReferenceAxis = -> Sketch027 [N_Axis]
  Refine = true
  Suppressed = false
  Type = 0
FEATURE [Sketcher::SketchObject] Sketch028
  ArcFitTolerance = 1e-06
  AttachmentSupport = -> [Pocket004]
  FullyConstrained = false
  MakeInternals = false
  MapMode = 5
  sketch-geometry (4):
    g0: LineSegment StartX=-165.265 StartY=216.038 StartZ=0 EndX=-165.265 EndY=-118.015 EndZ=0
    g1: LineSegment StartX=-165.265 StartY=-118.015 StartZ=0 EndX=853.838 EndY=-118.015 EndZ=0
    g2: LineSegment StartX=853.838 StartY=-118.015 StartZ=0 EndX=853.838 EndY=216.038 EndZ=0
    g3: LineSegment StartX=853.838 StartY=216.038 StartZ=0 EndX=-165.265 EndY=216.038 EndZ=0
  constraints (8):
    c: Coincident(g0,g1)
    c: Coincident(g1,g2)
    c: Coincident(g2,g3)
    c: Coincident(g3,g0)
    c: Vertical(g0)
    c: Vertical(g2)
    c: Horizontal(g1)
    c: Horizontal(g3)
FEATURE [PartDesign::Pocket] Pocket014
  BaseFeature = -> Pocket004
  Direction = (0,0,-1)
  Length = 400
  Length2 = 5
  Profile = -> Sketch028
  ReferenceAxis = -> Sketch028 [N_Axis]
  Refine = true
  Suppressed = false
  Type = 0
FEATURE [Sketcher::SketchObject] Sketch029
  ArcFitTolerance = 1e-06
  AttachmentSupport = -> [Pocket014]
  FullyConstrained = false
  MakeInternals = false
  MapMode = 5
  Placement = pos=(0,0,-600) rot=(1,0,0;3.14159rad)
  sketch-geometry (4):
    g0: LineSegment StartX=315.981 StartY=60.9079 StartZ=0 EndX=315.981 EndY=-70.6615 EndZ=0
    g1: LineSegment StartX=315.981 StartY=-70.6615 StartZ=0 EndX=912.479 EndY=-70.6615 EndZ=0
    g2: LineSegment StartX=912.479 StartY=-70.6615 StartZ=0 EndX=912.479 EndY=60.9079 EndZ=0
    g3: LineSegment StartX=912.479 StartY=60.9079 StartZ=0 EndX=315.981 EndY=60.9079 EndZ=0
  constraints (8):
    c: Coincident(g0,g1)
    c: Coincident(g1,g2)
    c: Coincident(g2,g3)
    c: Coincident(g3,g0)
    c: Vertical(g0)
    c: Vertical(g2)
    c: Horizontal(g1)
    c: Horizontal(g3)
FEATURE [PartDesign::Pocket] Pocket015
  BaseFeature = -> Pocket014
  Direction = (0,0,1)
  Length = 190
  Length2 = 5
  Profile = -> Sketch029
  ReferenceAxis = -> Sketch029 [N_Axis]
  Refine = true
  Suppressed = false
  Type = 0
FEATURE [Sketcher::SketchObject] Sketch030
  ArcFitTolerance = 1e-06
  AttachmentSupport = -> [Pocket005]
  FullyConstrained = false
  MakeInternals = false
  MapMode = 5
  sketch-geometry (4):
    g0: LineSegment StartX=-414.799 StartY=329.855 StartZ=0 EndX=-414.799 EndY=-231.413 EndZ=0
    g1: LineSegment StartX=-414.799 StartY=-231.413 StartZ=0 EndX=1174.17 EndY=-231.413 EndZ=0
    g2: LineSegment StartX=1174.17 StartY=-231.413 StartZ=0 EndX=1174.17 EndY=329.855 EndZ=0
    g3: LineSegment StartX=1174.17 StartY=329.855 StartZ=0 EndX=-414.799 EndY=329.855 EndZ=0
  constraints (8):
    c: Coincident(g0,g1)
    c: Coincident(g1,g2)
    c: Coincident(g2,g3)
    c: Coincident(g3,g0)
    c: Vertical(g0)
    c: Vertical(g2)
    c: Horizontal(g1)
    c: Horizontal(g3)
FEATURE [PartDesign::Pocket] Pocket016
  BaseFeature = -> Pocket005
  Direction = (0,0,-1)
  Length = 500
  Length2 = 5
  Profile = -> Sketch030
  ReferenceAxis = -> Sketch030 [N_Axis]
  Refine = true
  Suppressed = false
  Type = 0
FEATURE [Sketcher::SketchObject] Sketch031
  ArcFitTolerance = 1e-06
  AttachmentSupport = -> [Pocket016]
  FullyConstrained = false
  MakeInternals = false
  MapMode = 5
  Placement = pos=(0,0,-600) rot=(1,0,0;3.14159rad)
  sketch-geometry (4):
    g0: LineSegment StartX=419.766 StartY=113.124 StartZ=0 EndX=419.766 EndY=-100.841 EndZ=0
    g1: LineSegment StartX=419.766 StartY=-100.841 StartZ=0 EndX=947.907 EndY=-100.841 EndZ=0
    g2: LineSegment StartX=947.907 StartY=-100.841 StartZ=0 EndX=947.907 EndY=113.124 EndZ=0
    g3: LineSegment StartX=947.907 StartY=113.124 StartZ=0 EndX=419.766 EndY=113.124 EndZ=0
  constraints (8):
    c: Coincident(g0,g1)
    c: Coincident(g1,g2)
    c: Coincident(g2,g3)
    c: Coincident(g3,g0)
    c: Vertical(g0)
    c: Vertical(g2)
    c: Horizontal(g1)
    c: Horizontal(g3)
FEATURE [PartDesign::Pocket] Pocket017
  BaseFeature = -> Pocket016
  Direction = (0,0,1)
  Length = 90
  Length2 = 5
  Profile = -> Sketch031
  ReferenceAxis = -> Sketch031 [N_Axis]
  Refine = true
  Suppressed = false
  Type = 0
FEATURE [Sketcher::SketchObject] Sketch032
  ArcFitTolerance = 1e-06
  AttachmentSupport = -> [Pocket006]
  FullyConstrained = false
  MakeInternals = false
  MapMode = 5
  sketch-geometry (4):
    g0: LineSegment StartX=-130.893 StartY=206.881 StartZ=0 EndX=-130.893 EndY=-202.09 EndZ=0
    g1: LineSegment StartX=-130.893 StartY=-202.09 StartZ=0 EndX=1174.56 EndY=-202.09 EndZ=0
    g2: LineSegment StartX=1174.56 StartY=-202.09 StartZ=0 EndX=1174.56 EndY=206.881 EndZ=0
    g3: LineSegment StartX=1174.56 StartY=206.881 StartZ=0 EndX=-130.893 EndY=206.881 EndZ=0
  constraints (8):
    c: Coincident(g0,g1)
    c: Coincident(g1,g2)
    c: Coincident(g2,g3)
    c: Coincident(g3,g0)
    c: Vertical(g0)
    c: Vertical(g2)
    c: Horizontal(g1)
    c: Horizontal(g3)
FEATURE [PartDesign::Pocket] Pocket018
  BaseFeature = -> Pocket006
  Direction = (0,0,-1)
  Length = 590
  Length2 = 5
  Profile = -> Sketch032
  ReferenceAxis = -> Sketch032 [N_Axis]
  Refine = true
  Suppressed = false
  Type = 0
FEATURE [Sketcher::SketchObject] Sketch033
  ArcFitTolerance = 1e-06
  AttachmentSupport = -> [Pocket018]
  FullyConstrained = false
  MakeInternals = false
  MapMode = 5
  Placement = pos=(0,0,-600) rot=(1,0,0;3.14159rad)
  sketch-geometry (41):
    g0: LineSegment StartX=622.272 StartY=-9.09095 StartZ=0 EndX=622.272 EndY=2.65076 EndZ=0
    g1: LineSegment StartX=622.272 StartY=2.65076 StartZ=0 EndX=615.944 EndY=2.41174 EndZ=0
    g2: LineSegment StartX=615.944 StartY=2.41174 StartZ=0 EndX=611.391 EndY=2.06446 EndZ=0
    g3: LineSegment StartX=611.391 StartY=2.06446 StartZ=0 EndX=607.57 EndY=1.52425 EndZ=0
    g4: LineSegment StartX=607.57 StartY=1.52425 StartZ=0 EndX=604.406 EndY=0.906861 EndZ=0
    g5: LineSegment StartX=604.406 StartY=0.906861 StartZ=0 EndX=602.824 EndY=0.250887 EndZ=0
    g6: LineSegment StartX=602.824 StartY=0.250887 StartZ=0 EndX=602.631 EndY=-0.983889 EndZ=0
    g7: LineSegment StartX=602.631 StartY=-0.983889 StartZ=0 EndX=603.982 EndY=-2.60453 EndZ=0
    g8: LineSegment StartX=603.982 StartY=-2.60453 StartZ=0 EndX=606.451 EndY=-4.34094 EndZ=0
    g9: LineSegment StartX=606.451 StartY=-4.34094 StartZ=0 EndX=608.767 EndY=-5.42136 EndZ=0
    g10: LineSegment StartX=608.767 StartY=-5.42136 StartZ=0 EndX=611.583 EndY=-6.61755 EndZ=0
    g11: LineSegment StartX=611.583 StartY=-6.61755 StartZ=0 EndX=613.981 EndY=-7.41803 EndZ=0
    g12: LineSegment StartX=613.981 StartY=-7.41803 StartZ=0 EndX=616.407 EndY=-8.2382 EndZ=0
    g13: LineSegment StartX=616.407 StartY=-8.2382 StartZ=0 EndX=618.606 EndY=-8.97135 EndZ=0
    g14: LineSegment StartX=618.606 StartY=-8.97135 StartZ=0 EndX=620.77 EndY=-9.58189 EndZ=0
    g15: LineSegment StartX=620.77 StartY=-9.58189 StartZ=0 EndX=622.272 EndY=-9.82025 EndZ=0
    g16: LineSegment StartX=622.272 StartY=-9.82025 StartZ=0 EndX=622.272 EndY=-9.09095 EndZ=0
    g17: LineSegment StartX=784.834 StartY=-1.79823 StartZ=0 EndX=784.834 EndY=-3.99384 EndZ=0
    g18: LineSegment StartX=784.834 StartY=-3.99384 StartZ=0 EndX=768.945 EndY=-6.7131 EndZ=0
    g19: LineSegment StartX=768.945 StartY=-6.7131 StartZ=0 EndX=757.689 EndY=-8.24877 EndZ=0
    g20: LineSegment StartX=757.689 StartY=-8.24877 StartZ=0 EndX=752.959 EndY=-1.2705 EndZ=0
    g21: LineSegment StartX=752.959 StartY=-1.2705 StartZ=0 EndX=768.238 EndY=-1.79823 EndZ=0
    g22: LineSegment StartX=768.238 StartY=-1.79823 StartZ=0 EndX=777.747 EndY=-1.79823 EndZ=0
    g23: LineSegment StartX=777.747 StartY=-1.79823 StartZ=0 EndX=784.834 EndY=-1.79823 EndZ=0
    g24: LineSegment StartX=753.14 StartY=-8.87517 StartZ=0 EndX=747.811 EndY=-1.0133 EndZ=0
    g25: LineSegment StartX=753.14 StartY=-8.87517 StartZ=0 EndX=736.521 EndY=-10.9456 EndZ=0
    g26: LineSegment StartX=736.521 StartY=-10.9456 StartZ=0 EndX=727.789 EndY=-11.8784 EndZ=0
    g27: LineSegment StartX=727.789 StartY=-11.8784 StartZ=0 EndX=718.222 EndY=-12.7318 EndZ=0
    g28: LineSegment StartX=718.222 StartY=-12.7318 StartZ=0 EndX=711.079 EndY=-13.2783 EndZ=0
    g29: LineSegment StartX=711.079 StartY=-13.2783 StartZ=0 EndX=719.382 EndY=0 EndZ=0
    g30: LineSegment StartX=719.382 StartY=0 StartZ=0 EndX=737.395 EndY=-0.797295 EndZ=0
    g31: LineSegment StartX=737.395 StartY=-0.797295 StartZ=0 EndX=747.811 EndY=-1.0133 EndZ=0
    g32: LineSegment StartX=714.396 StartY=0.172416 StartZ=0 EndX=705.846 EndY=-13.5027 EndZ=0
    g33: LineSegment StartX=705.846 StartY=-13.5027 StartZ=0 EndX=684.767 EndY=-14.2148 EndZ=0
    g34: LineSegment StartX=684.767 StartY=-14.2148 StartZ=0 EndX=675.331 EndY=-14.2148 EndZ=0
    g35: LineSegment StartX=675.331 StartY=-14.2148 StartZ=0 EndX=664.237 EndY=1.35063 EndZ=0
    g36: LineSegment StartX=664.237 StartY=1.35063 StartZ=0 EndX=714.396 EndY=0.172416 EndZ=0
    g37: LineSegment StartX=647.42 StartY=1.98171 StartZ=0 EndX=647.42 EndY=-13.1521 EndZ=0
    g38: LineSegment StartX=647.42 StartY=-13.1521 StartZ=0 EndX=668.784 EndY=-14.3504 EndZ=0
    g39: LineSegment StartX=668.784 StartY=-14.3504 StartZ=0 EndX=658.785 EndY=1.40188 EndZ=0
    g40: LineSegment StartX=658.785 StartY=1.40188 StartZ=0 EndX=647.42 EndY=1.98171 EndZ=0
  constraints (51):
    c: Vertical(g0)
    c: Coincident(g0,g1)
    c: Coincident(g1,g2)
    c: Coincident(g2,g3)
    c: Coincident(g3,g4)
    c: Coincident(g4,g5)
    c: Coincident(g5,g6)
    c: Coincident(g6,g7)
    c: Coincident(g7,g8)
    c: Coincident(g8,g9)
    c: Coincident(g9,g10)
    c: Coincident(g10,g11)
    c: Coincident(g11,g12)
    c: Coincident(g12,g13)
    c: Coincident(g13,g14)
    c: Coincident(g14,g15)
    c: Coincident(g15,g16)
    c: Coincident(g16,g0)
    c: Vertical(g16)
    c: Vertical(g17)
    c: Coincident(g17,g18)
    c: Coincident(g18,g19)
    c: Coincident(g19,g20)
    c: Coincident(g20,g21)
    c: Coincident(g21,g22)
    c: Horizontal(g22)
    c: Coincident(g22,g23)
    c: Coincident(g23,g17)
    c: Horizontal(g23)
    c: Parallel(g20,g24)
    c: Coincident(g24,g25)
    c: Coincident(g25,g26)
    c: Coincident(g26,g27)
    c: Coincident(g27,g28)
    c: Coincident(g28,g29)
    c: PointOnObject(g29,g-1)
    c: Coincident(g29,g30)
    c: Coincident(g30,g31)
    c: Coincident(g31,g24)
    c: Coincident(g32,g33)
    c: Coincident(g33,g34)
    c: Horizontal(g34)
    c: Coincident(g34,g35)
    c: Coincident(g35,g36)
    c: Coincident(g36,g32)
    c: Parallel(g29,g32)
    c: Vertical(g37)
    c: Coincident(g37,g38)
    c: Coincident(g38,g39)
    c: Coincident(g39,g40)
    c: Coincident(g40,g37)
FEATURE [PartDesign::Pocket] Pocket019
  BaseFeature = -> Pocket018
  Direction = (0,0,1)
  Length = 15
  Length2 = 5
  Profile = -> Sketch033
  ReferenceAxis = -> Sketch033 [N_Axis]
  Refine = true
  Suppressed = false
  Type = 0
FEATURE [PartDesign::Body] Body006
  AllowCompound = false
  Group = -> [Sketch019,Sketch018,AdditiveLoft006,DatumPlane006,Sketch020,Pocket006,Sketch032,Pocket018,Sketch033,Pocket019]
  Origin = -> Origin006
  Placement = pos=(0,0,-100) rot=(0,0,1;0rad)
  Tip = -> Pocket019
FEATURE [Sketcher::SketchObject] Sketch034
  ArcFitTolerance = 1e-06
  AttachmentSupport = -> [Pocket017]
  FullyConstrained = false
  MakeInternals = false
  MapMode = 5
  Placement = pos=(0,0,-510) rot=(1,0,0;3.14159rad)
  sketch-geometry (45):
    g0: LineSegment StartX=532.976 StartY=-11.1364 StartZ=0 EndX=532.976 EndY=2.92211 EndZ=0
    g1: LineSegment StartX=532.976 StartY=2.92211 StartZ=0 EndX=530.009 EndY=2.78788 EndZ=0
    g2: LineSegment StartX=530.009 StartY=2.78788 StartZ=0 EndX=522.08 EndY=2.34558 EndZ=0
    g3: LineSegment StartX=522.08 StartY=2.34558 StartZ=0 EndX=517.625 EndY=1.96648 EndZ=0
    g4: LineSegment StartX=517.625 StartY=1.96648 StartZ=0 EndX=514.687 EndY=1.52419 EndZ=0
    g5: LineSegment StartX=514.687 StartY=1.52419 StartZ=0 EndX=513.202 EndY=0.987121 EndZ=0
    g6: LineSegment StartX=513.202 StartY=0.987121 StartZ=0 EndX=512.404 EndY=0 EndZ=0
    g7: LineSegment StartX=512.404 StartY=0 StartZ=0 EndX=512.447 EndY=-1.01113 EndZ=0
    g8: LineSegment StartX=512.447 StartY=-1.01113 StartZ=0 EndX=512.981 EndY=-2.04573 EndZ=0
    g9: LineSegment StartX=512.981 StartY=-2.04573 StartZ=0 EndX=513.932 EndY=-2.86253 EndZ=0
    g10: LineSegment StartX=513.932 StartY=-2.86253 StartZ=0 EndX=516.867 EndY=-4.50992 EndZ=0
    g11: LineSegment StartX=516.867 StartY=-4.50992 StartZ=0 EndX=519.236 EndY=-5.89997 EndZ=0
    g12: LineSegment StartX=519.236 StartY=-5.89997 StartZ=0 EndX=523.249 EndY=-7.66914 EndZ=0
    g13: LineSegment StartX=523.249 StartY=-7.66914 StartZ=0 EndX=527.608 EndY=-9.50148 EndZ=0
    g14: LineSegment StartX=527.608 StartY=-9.50148 StartZ=0 EndX=531.026 EndY=-10.5855 EndZ=0
    g15: LineSegment StartX=531.026 StartY=-10.5855 StartZ=0 EndX=532.976 EndY=-11.1364 EndZ=0
    g16: LineSegment StartX=709.1 StartY=-1.48937 StartZ=0 EndX=709.1 EndY=-7.02794 EndZ=0
    g17: LineSegment StartX=709.1 StartY=-7.02794 StartZ=0 EndX=681.162 EndY=-10.1406 EndZ=0
    g18: LineSegment StartX=681.162 StartY=-10.1406 StartZ=0 EndX=669.975 EndY=-11.3087 EndZ=0
    g19: LineSegment StartX=669.975 StartY=-11.3087 StartZ=0 EndX=663.046 EndY=-0.328372 EndZ=0
    g20: LineSegment StartX=663.046 StartY=-0.328372 StartZ=0 EndX=681.551 EndY=-1.11233 EndZ=0
    g21: LineSegment StartX=681.551 StartY=-1.11233 StartZ=0 EndX=709.1 EndY=-1.48937 EndZ=0
    g22: LineSegment StartX=665.656 StartY=-12.5357 StartZ=0 EndX=658 EndY=-0.404047 EndZ=0
    g23: LineSegment StartX=658 StartY=-0.404047 StartZ=0 EndX=634.363 EndY=0.273619 EndZ=0
    g24: LineSegment StartX=634.363 StartY=0.273619 StartZ=0 EndX=626.916 EndY=0.464469 EndZ=0
    g25: LineSegment StartX=626.916 StartY=0.464469 StartZ=0 EndX=618.81 EndY=-16.0334 EndZ=0
    g26: LineSegment StartX=618.81 StartY=-16.0334 StartZ=0 EndX=632.431 EndY=-15.4678 EndZ=0
    g27: LineSegment StartX=632.431 StartY=-15.4678 StartZ=0 EndX=646.309 EndY=-14.6728 EndZ=0
    g28: LineSegment StartX=646.309 StartY=-14.6728 StartZ=0 EndX=657.348 EndY=-13.4775 EndZ=0
    g29: LineSegment StartX=657.348 StartY=-13.4775 StartZ=0 EndX=665.656 EndY=-12.5357 EndZ=0
    g30: LineSegment StartX=613.242 StartY=-16.2059 StartZ=0 EndX=620.736 EndY=0.853957 EndZ=0
    g31: LineSegment StartX=620.736 StartY=0.853957 StartZ=0 EndX=577.175 EndY=1.79781 EndZ=0
    g32: LineSegment StartX=577.175 StartY=1.79781 StartZ=0 EndX=586.447 EndY=-16.4101 EndZ=0
    g33: LineSegment StartX=586.447 StartY=-16.4101 StartZ=0 EndX=600.127 EndY=-16.6772 EndZ=0
    g34: LineSegment StartX=600.127 StartY=-16.6772 StartZ=0 EndX=613.242 EndY=-16.2059 EndZ=0
    g35: LineSegment StartX=581.436 StartY=-16.5461 StartZ=0 EndX=571.633 EndY=2.02311 EndZ=0
    g36: LineSegment StartX=571.633 StartY=2.02311 StartZ=0 EndX=558.06 EndY=2.02311 EndZ=0
    g37: LineSegment StartX=558.06 StartY=2.02311 StartZ=0 EndX=558.06 EndY=-14.8494 EndZ=0
    g38: LineSegment StartX=558.06 StartY=-14.8494 StartZ=0 EndX=566.119 EndY=-16.0748 EndZ=0
    g39: LineSegment StartX=566.119 StartY=-16.0748 StartZ=0 EndX=572.104 EndY=-16.5461 EndZ=0
    g40: LineSegment StartX=572.104 StartY=-16.5461 StartZ=0 EndX=581.436 EndY=-16.5461 EndZ=0
    g41: LineSegment StartX=713.989 StartY=-1.92489 StartZ=0 EndX=713.989 EndY=-6.32731 EndZ=0
    g42: LineSegment StartX=713.989 StartY=-6.32731 StartZ=0 EndX=732.41 EndY=-3.44908 EndZ=0
    g43: LineSegment StartX=732.41 StartY=-3.44908 StartZ=0 EndX=732.41 EndY=-1.92489 EndZ=0
    g44: LineSegment StartX=732.41 StartY=-1.92489 StartZ=0 EndX=713.989 EndY=-1.92489 EndZ=0
  constraints (54):
    c: Vertical(g0)
    c: Coincident(g0,g1)
    c: Coincident(g1,g2)
    c: Coincident(g2,g3)
    c: Coincident(g3,g4)
    c: Coincident(g4,g5)
    c: Coincident(g5,g6)
    c: PointOnObject(g6,g-1)
    c: Coincident(g6,g7)
    c: Coincident(g7,g8)
    c: Coincident(g8,g9)
    c: Coincident(g9,g10)
    c: Coincident(g10,g11)
    c: Coincident(g11,g12)
    c: Coincident(g12,g13)
    c: Coincident(g13,g14)
    c: Coincident(g14,g15)
    c: Vertical(g16)
    c: Coincident(g16,g17)
    c: Coincident(g17,g18)
    c: Coincident(g18,g19)
    c: Coincident(g19,g20)
    c: Coincident(g20,g21)
    c: Coincident(g21,g16)
    c: Parallel(g19,g22)
    c: Coincident(g22,g23)
    c: Coincident(g23,g24)
    c: Coincident(g24,g25)
    c: Coincident(g25,g26)
    c: Coincident(g26,g27)
    c: Coincident(g27,g28)
    c: Coincident(g28,g29)
    c: Coincident(g29,g22)
    c: Coincident(g30,g31)
    c: Coincident(g31,g32)
    c: Coincident(g32,g33)
    c: Coincident(g33,g34)
    c: Coincident(g34,g30)
    c: Coincident(g35,g36)
    c: Horizontal(g36)
    c: Coincident(g36,g37)
    c: Vertical(g37)
    c: Coincident(g37,g38)
    c: Coincident(g38,g39)
    c: Coincident(g39,g40)
    c: Coincident(g40,g35)
    c: Vertical(g41)
    c: Coincident(g41,g42)
    c: Coincident(g42,g43)
    c: Vertical(g43)
    c: Coincident(g43,g44)
    c: Coincident(g44,g41)
    c: Horizontal(g44)
    c: Coincident(g15,g0)
FEATURE [PartDesign::Pocket] Pocket020
  BaseFeature = -> Pocket017
  Direction = (0,0,1)
  Length = 15
  Length2 = 5
  Profile = -> Sketch034
  ReferenceAxis = -> Sketch034 [N_Axis]
  Refine = true
  Suppressed = false
  Type = 0
FEATURE [Sketcher::SketchObject] Sketch035
  ArcFitTolerance = 1e-06
  AttachmentSupport = -> [Pocket020]
  FullyConstrained = true
  MakeInternals = false
  MapMode = 5
  Placement = pos=(0,0,-500) rot=(0,0,1;0rad)
  sketch-geometry (1):
    g0: Circle CenterX=667 CenterY=6.6 CenterZ=0 NormalX=0 NormalY=0 NormalZ=1 AngleXU=0 Radius=6.5
  constraints (3):
    c: DistanceX(g-1,g0) = 667
    c: Diameter(g0) = 13
    c: DistanceY(g-1,g0) = 6.6
FEATURE [PartDesign::Pad] Pad
  BaseFeature = -> Pocket020
  Direction = (0,0,1)
  Length = 10
  Length2 = 10
  Profile = -> Sketch035
  ReferenceAxis = -> Sketch035 [N_Axis]
  Refine = true
  Reversed = true
  Suppressed = false
  Type = 0
FEATURE [Sketcher::SketchObject] Sketch036
  ArcFitTolerance = 1e-06
  AttachmentSupport = -> [Pad]
  FullyConstrained = false
  MakeInternals = false
  MapMode = 5
  Placement = pos=(0,0,-500) rot=(0,0,1;0rad)
  sketch-geometry (4):
    g0: LineSegment StartX=661.402 StartY=2.07122 StartZ=0 EndX=661.402 EndY=-0.319658 EndZ=0
    g1: LineSegment StartX=661.402 StartY=-0.319658 StartZ=0 EndX=667.051 EndY=-0.319658 EndZ=0
    g2: LineSegment StartX=667.051 StartY=-0.319658 StartZ=0 EndX=667.051 EndY=2.07122 EndZ=0
    g3: LineSegment StartX=667.051 StartY=2.07122 StartZ=0 EndX=661.402 EndY=2.07122 EndZ=0
  constraints (8):
    c: Coincident(g0,g1)
    c: Coincident(g1,g2)
    c: Coincident(g2,g3)
    c: Coincident(g3,g0)
    c: Vertical(g0)
    c: Vertical(g2)
    c: Horizontal(g1)
    c: Horizontal(g3)
FEATURE [PartDesign::Pad] Pad001
  BaseFeature = -> Pad
  Direction = (0,0,1)
  Length = 10
  Length2 = 10
  Profile = -> Sketch036
  ReferenceAxis = -> Sketch036 [N_Axis]
  Refine = true
  Reversed = true
  Suppressed = false
  Type = 0
FEATURE [PartDesign::Plane] DatumPlane007
  AttachmentOffset = pos=(0,0,-404) rot=(0,-1,0;0.54042rad)
  AttachmentSupport = -> [Pad001]
  Length = 1180.87
  MapMode = 5
  Placement = pos=(0,0,-904) rot=(0,-1,0;0.54042rad)
  ResizeMode = 0
  Width = 97.608
FEATURE [Sketcher::SketchObject] Sketch037
  ArcFitTolerance = 1e-06
  AttachmentSupport = -> [DatumPlane007]
  FullyConstrained = true
  MakeInternals = false
  MapMode = 5
  Placement = pos=(0,0,-904) rot=(0,-1,0;0.54042rad)
  sketch-geometry (1):
    g0: Circle CenterX=779.81 CenterY=6.5 CenterZ=0 NormalX=0 NormalY=0 NormalZ=1 AngleXU=0 Radius=2.5
  constraints (3):
    c: Diameter(g0) = 5
    c: DistanceY(g-1,g0) = 6.5
    c: DistanceX(g-1,g0) = 779.81
FEATURE [PartDesign::Pad] Pad002
  BaseFeature = -> Pad001
  Direction = (-0.514496,0,0.857493)
  Length = 20
  Length2 = 10
  Profile = -> Sketch037
  ReferenceAxis = -> Sketch037 [N_Axis]
  Refine = true
  Suppressed = false
  Type = 0
FEATURE [PartDesign::Body] Body005
  AllowCompound = false
  Group = -> [Sketch016,Sketch015,AdditiveLoft005,DatumPlane005,Sketch017,Pocket005,Sketch030,Pocket016,Sketch031,Pocket017,Sketch034,Pocket020,Sketch035,Pad,Sketch036,Pad001,DatumPlane007,Sketch037,Pad002]
  Origin = -> Origin005
  Placement = pos=(0,0,-100) rot=(0,0,1;0rad)
  Tip = -> Pad002
FEATURE [Sketcher::SketchObject] Sketch038
  ArcFitTolerance = 1e-06
  AttachmentSupport = -> [Pocket015]
  FullyConstrained = false
  MakeInternals = false
  MapMode = 5
  Placement = pos=(0,0,-410) rot=(1,0,0;3.14159rad)
  sketch-geometry (6):
    g0: LineSegment StartX=694.6 StartY=8.83161 StartZ=0 EndX=589.6 EndY=8.83161 EndZ=0
    g1: LineSegment StartX=589.6 StartY=8.83161 StartZ=0 EndX=589.6 EndY=-59.5023 EndZ=0
    g2: LineSegment StartX=589.6 StartY=-59.5023 StartZ=0 EndX=694.205 EndY=-59.5023 EndZ=0
    g3: LineSegment StartX=694.205 StartY=-59.5023 StartZ=0 EndX=702.61 EndY=-59.5023 EndZ=0
    g4: LineSegment StartX=702.61 StartY=-59.5023 StartZ=0 EndX=702.61 EndY=8.83161 EndZ=0
    g5: LineSegment StartX=702.61 StartY=8.83161 StartZ=0 EndX=694.6 EndY=8.83161 EndZ=0
  constraints (14):
    c: Coincident(g0,g1)
    c: Coincident(g1,g2)
    c: Horizontal(g0)
    c: Horizontal(g2)
    c: Vertical(g1)
    c: DistanceX(g-1,g0) = 694.6
    c: Coincident(g3,g2)
    c: Horizontal(g3)
    c: Coincident(g4,g3)
    c: Vertical(g4)
    c: Coincident(g5,g0)
    c: Horizontal(g5)
    c: DistanceX(g0,g0) = 105
    c: Coincident(g4,g5)
FEATURE [PartDesign::Pocket] Pocket021
  BaseFeature = -> Pocket015
  Direction = (0,0,1)
  Length = 15
  Length2 = 5
  Profile = -> Sketch038
  ReferenceAxis = -> Sketch038 [N_Axis]
  Refine = true
  Suppressed = false
  Type = 0
FEATURE [Sketcher::SketchObject] Sketch039
  ArcFitTolerance = 1e-06
  AttachmentSupport = -> [Pocket021]
  FullyConstrained = false
  MakeInternals = false
  MapMode = 5
  Placement = pos=(0,0,-410) rot=(1,0,0;3.14159rad)
  sketch-geometry (36):
    g0: LineSegment StartX=586.898 StartY=-0.494744 StartZ=0 EndX=586.898 EndY=-15.4277 EndZ=0
    g1: LineSegment StartX=586.898 StartY=-15.4277 StartZ=0 EndX=570.919 EndY=-16.9384 EndZ=0
    g2: LineSegment StartX=570.919 StartY=-16.9384 StartZ=0 EndX=560.053 EndY=-17.81 EndZ=0
    g3: LineSegment StartX=560.053 StartY=-17.81 StartZ=0 EndX=548.723 EndY=-18.4491 EndZ=0
    g4: LineSegment StartX=548.723 StartY=-18.4491 StartZ=0 EndX=537.509 EndY=1.01599 EndZ=0
    g5: LineSegment StartX=537.509 StartY=1.01599 StartZ=0 EndX=586.898 EndY=-0.494744 EndZ=0
    g6: LineSegment StartX=543.354 StartY=-19.0257 StartZ=0 EndX=531.526 EndY=1.78558 EndZ=0
    g7: LineSegment StartX=531.526 StartY=1.78558 StartZ=0 EndX=514.466 EndY=2.42335 EndZ=0
    g8: LineSegment StartX=514.466 StartY=2.42335 StartZ=0 EndX=500.02 EndY=2.90169 EndZ=0
    g9: LineSegment StartX=500.02 StartY=2.90169 StartZ=0 EndX=491.613 EndY=3.06718 EndZ=0
    g10: LineSegment StartX=491.613 StartY=3.06718 StartZ=0 EndX=477.795 EndY=-19.1898 EndZ=0
    g11: LineSegment StartX=477.795 StartY=-19.1898 StartZ=0 EndX=492.707 EndY=-19.6873 EndZ=0
    g12: LineSegment StartX=492.707 StartY=-19.6873 StartZ=0 EndX=513.052 EndY=-19.9219 EndZ=0
    g13: LineSegment StartX=513.052 StartY=-19.9219 StartZ=0 EndX=528.638 EndY=-19.7391 EndZ=0
    g14: LineSegment StartX=528.638 StartY=-19.7391 StartZ=0 EndX=543.354 EndY=-19.0257 EndZ=0
    g15: LineSegment StartX=486.381 StartY=3.93493 StartZ=0 EndX=473.616 EndY=-18.7157 EndZ=0
    g16: LineSegment StartX=473.616 StartY=-18.7157 StartZ=0 EndX=465.476 EndY=-17.9756 EndZ=0
    g17: LineSegment StartX=465.476 StartY=-17.9756 StartZ=0 EndX=459.517 EndY=-17.3135 EndZ=0
    g18: LineSegment StartX=459.517 StartY=-17.3135 StartZ=0 EndX=457.388 EndY=-17.0619 EndZ=0
    g19: LineSegment StartX=457.388 StartY=-17.0619 StartZ=0 EndX=457.388 EndY=4.55483 EndZ=0
    g20: LineSegment StartX=457.388 StartY=4.55483 StartZ=0 EndX=464.599 EndY=4.38382 EndZ=0
    g21: LineSegment StartX=464.599 StartY=4.38382 StartZ=0 EndX=472.486 EndY=4.25557 EndZ=0
    g22: LineSegment StartX=472.486 StartY=4.25557 StartZ=0 EndX=486.381 EndY=3.93493 EndZ=0
    g23: LineSegment StartX=431.847 StartY=4.34849 StartZ=0 EndX=431.847 EndY=-12.3575 EndZ=0
    g24: LineSegment StartX=431.847 StartY=-12.3575 StartZ=0 EndX=428.203 EndY=-10.9898 EndZ=0
    g25: LineSegment StartX=428.203 StartY=-10.9898 StartZ=0 EndX=423.037 EndY=-8.82135 EndZ=0
    g26: LineSegment StartX=423.037 StartY=-8.82135 StartZ=0 EndX=417.679 EndY=-6.23837 EndZ=0
    g27: LineSegment StartX=417.679 StartY=-6.23837 StartZ=0 EndX=414.459 EndY=-3.78295 EndZ=0
    g28: LineSegment StartX=414.459 StartY=-3.78295 StartZ=0 EndX=412.258 EndY=-1.51885 EndZ=0
    g29: LineSegment StartX=412.258 StartY=-1.51885 StartZ=0 EndX=411.716 EndY=-0.211416 EndZ=0
    g30: LineSegment StartX=411.716 StartY=-0.211416 StartZ=0 EndX=411.748 EndY=0.5858 EndZ=0
    g31: LineSegment StartX=411.748 StartY=0.5858 StartZ=0 EndX=412.769 EndY=1.19168 EndZ=0
    g32: LineSegment StartX=412.769 StartY=1.19168 StartZ=0 EndX=416.053 EndY=2.18023 EndZ=0
    g33: LineSegment StartX=416.053 StartY=2.18023 StartZ=0 EndX=422.176 EndY=3.32822 EndZ=0
    g34: LineSegment StartX=422.176 StartY=3.32822 StartZ=0 EndX=430.02 EndY=4.2211 EndZ=0
    g35: LineSegment StartX=430.02 StartY=4.2211 StartZ=0 EndX=431.847 EndY=4.34849 EndZ=0
  constraints (39):
    c: Vertical(g0)
    c: Coincident(g0,g1)
    c: Coincident(g1,g2)
    c: Coincident(g2,g3)
    c: Coincident(g3,g4)
    c: Coincident(g4,g5)
    c: Coincident(g5,g0)
    c: Coincident(g6,g7)
    c: Coincident(g7,g8)
    c: Coincident(g8,g9)
    c: Coincident(g9,g10)
    c: Coincident(g10,g11)
    c: Coincident(g11,g12)
    c: Coincident(g12,g13)
    c: Coincident(g13,g14)
    c: Coincident(g14,g6)
    c: Coincident(g15,g16)
    c: Coincident(g16,g17)
    c: Coincident(g17,g18)
    c: Coincident(g18,g19)
    c: Vertical(g19)
    c: Coincident(g19,g20)
    c: Coincident(g20,g21)
    c: Coincident(g21,g22)
    c: Coincident(g22,g15)
    c: Vertical(g23)
    c: Coincident(g23,g24)
    c: Coincident(g24,g25)
    c: Coincident(g25,g26)
    c: Coincident(g26,g27)
    c: Coincident(g27,g28)
    c: Coincident(g28,g29)
    c: Coincident(g29,g30)
    c: Coincident(g30,g31)
    c: Coincident(g31,g32)
    c: Coincident(g32,g33)
    c: Coincident(g33,g34)
    c: Coincident(g34,g35)
    c: Coincident(g35,g23)
FEATURE [PartDesign::Pocket] Pocket022
  BaseFeature = -> Pocket021
  Direction = (0,0,1)
  Length = 15
  Length2 = 5
  Profile = -> Sketch039
  ReferenceAxis = -> Sketch039 [N_Axis]
  Refine = true
  Suppressed = false
  Type = 0
FEATURE [PartDesign::Body] Body004
  AllowCompound = false
  Group = -> [Sketch013,Sketch012,AdditiveLoft004,DatumPlane004,Sketch014,Pocket004,Sketch028,Pocket014,Sketch029,Pocket015,Sketch038,Pocket021,Sketch039,Pocket022]
  Origin = -> Origin004
  Placement = pos=(0,0,-100) rot=(0,0,1;0rad)
  Tip = -> Pocket022
FEATURE [Sketcher::SketchObject] Sketch040
  ArcFitTolerance = 1e-06
  AttachmentSupport = -> [Pocket013]
  FullyConstrained = false
  MakeInternals = false
  MapMode = 5
  Placement = pos=(0,0,-310) rot=(1,0,0;3.14159rad)
  sketch-geometry (56):
    g0: LineSegment StartX=332.032 StartY=3.92783 StartZ=0 EndX=332.032 EndY=-12.0562 EndZ=0
    g1: LineSegment StartX=332.032 StartY=-12.0562 StartZ=0 EndX=330.396 EndY=-11.418 EndZ=0
    g2: LineSegment StartX=330.396 StartY=-11.418 StartZ=0 EndX=325.235 EndY=-9.31772 EndZ=0
    g3: LineSegment StartX=325.235 StartY=-9.31772 StartZ=0 EndX=321.545 EndY=-7.54348 EndZ=0
    g4: LineSegment StartX=321.545 StartY=-7.54348 StartZ=0 EndX=318.351 EndY=-5.6273 EndZ=0
    g5: LineSegment StartX=318.351 StartY=-5.6273 StartZ=0 EndX=315.441 EndY=-3.71112 EndZ=0
    g6: LineSegment StartX=315.441 StartY=-3.71112 StartZ=0 EndX=314.022 EndY=-2.22077 EndZ=0
    g7: LineSegment StartX=314.022 StartY=-2.22077 StartZ=0 EndX=313.099 EndY=-0.659436 EndZ=0
    g8: LineSegment StartX=313.099 StartY=-0.659436 StartZ=0 EndX=312.957 EndY=0.476075 EndZ=0
    g9: LineSegment StartX=312.957 StartY=0.476075 StartZ=0 EndX=313.596 EndY=0.901893 EndZ=0
    g10: LineSegment StartX=313.596 StartY=0.901893 StartZ=0 EndX=315.654 EndY=1.75353 EndZ=0
    g11: LineSegment StartX=315.654 StartY=1.75353 StartZ=0 EndX=318.777 EndY=2.60516 EndZ=0
    g12: LineSegment StartX=318.777 StartY=2.60516 StartZ=0 EndX=322.325 EndY=3.10195 EndZ=0
    g13: LineSegment StartX=322.325 StartY=3.10195 StartZ=0 EndX=327.435 EndY=3.52776 EndZ=0
    g14: LineSegment StartX=327.435 StartY=3.52776 StartZ=0 EndX=332.032 EndY=3.92783 EndZ=0
    g15: LineSegment StartX=596.656 StartY=-2.47566 StartZ=0 EndX=596.656 EndY=-4.90277 EndZ=0
    g16: LineSegment StartX=596.656 StartY=-4.90277 StartZ=0 EndX=568.724 EndY=-9.51106 EndZ=0
    g17: LineSegment StartX=568.724 StartY=-9.51106 StartZ=0 EndX=547.062 EndY=-12.2805 EndZ=0
    g18: LineSegment StartX=547.062 StartY=-12.2805 StartZ=0 EndX=536.786 EndY=-13.5531 EndZ=0
    g19: LineSegment StartX=536.786 StartY=-13.5531 StartZ=0 EndX=527.534 EndY=-0.989378 EndZ=0
    g20: LineSegment StartX=527.534 StartY=-0.989378 StartZ=0 EndX=547.951 EndY=-1.76517 EndZ=0
    g21: LineSegment StartX=547.951 StartY=-1.76517 StartZ=0 EndX=582.087 EndY=-2.61681 EndZ=0
    g22: LineSegment StartX=582.087 StartY=-2.61681 StartZ=0 EndX=596.656 EndY=-2.47566 EndZ=0
    g23: LineSegment StartX=531.003 StartY=-14.2202 StartZ=0 EndX=520.9 EndY=-0.500741 EndZ=0
    g24: LineSegment StartX=531.003 StartY=-14.2202 StartZ=0 EndX=505.941 EndY=-17.0028 EndZ=0
    g25: LineSegment StartX=505.941 StartY=-17.0028 StartZ=0 EndX=482.916 EndY=-18.8581 EndZ=0
    g26: LineSegment StartX=482.916 StartY=-18.8581 StartZ=0 EndX=470.676 EndY=-19.744 EndZ=0
    g27: LineSegment StartX=470.676 StartY=-19.744 StartZ=0 EndX=480.564 EndY=0.541013 EndZ=0
    g28: LineSegment StartX=480.564 StartY=0.541013 StartZ=0 EndX=493.641 EndY=0.022556 EndZ=0
    g29: LineSegment StartX=493.641 StartY=0.022556 StartZ=0 EndX=506.533 EndY=-0.26288 EndZ=0
    g30: LineSegment StartX=506.533 StartY=-0.26288 StartZ=0 EndX=515.762 EndY=-0.310453 EndZ=0
    g31: LineSegment StartX=515.762 StartY=-0.310453 StartZ=0 EndX=520.9 EndY=-0.500741 EndZ=0
    g32: LineSegment StartX=475.564 StartY=0.974291 StartZ=0 EndX=464.963 EndY=-20.7733 EndZ=0
    g33: LineSegment StartX=475.564 StartY=0.974291 StartZ=0 EndX=453.041 EndY=1.52388 EndZ=0
    g34: LineSegment StartX=453.041 StartY=1.52388 StartZ=0 EndX=427.59 EndY=2.38018 EndZ=0
    g35: LineSegment StartX=427.59 StartY=2.38018 StartZ=0 EndX=415.511 EndY=2.89765 EndZ=0
    g36: LineSegment StartX=415.511 StartY=2.89765 StartZ=0 EndX=431.488 EndY=-22.3382 EndZ=0
    g37: LineSegment StartX=431.488 StartY=-22.3382 StartZ=0 EndX=441.844 EndY=-22.1764 EndZ=0
    g38: LineSegment StartX=441.844 StartY=-22.1764 StartZ=0 EndX=450.773 EndY=-21.9213 EndZ=0
    g39: LineSegment StartX=450.773 StartY=-21.9213 StartZ=0 EndX=460.18 EndY=-21.2835 EndZ=0
    g40: LineSegment StartX=460.18 StartY=-21.2835 StartZ=0 EndX=464.963 EndY=-20.7733 EndZ=0
    g41: LineSegment StartX=425.327 StartY=-22.6169 StartZ=0 EndX=408.845 EndY=3.41656 EndZ=0
    g42: LineSegment StartX=408.845 StartY=3.41656 StartZ=0 EndX=398.718 EndY=3.65025 EndZ=0
    g43: LineSegment StartX=398.718 StartY=3.65025 StartZ=0 EndX=388.942 EndY=4.00079 EndZ=0
    g44: LineSegment StartX=388.942 StartY=4.00079 StartZ=0 EndX=379.162 EndY=4.1568 EndZ=0
    g45: LineSegment StartX=379.162 StartY=4.1568 StartZ=0 EndX=371.688 EndY=4.23449 EndZ=0
    g46: LineSegment StartX=371.688 StartY=4.23449 StartZ=0 EndX=357.783 EndY=4.06055 EndZ=0
    g47: LineSegment StartX=357.783 StartY=4.06055 StartZ=0 EndX=357.783 EndY=-18.082 EndZ=0
    g48: LineSegment StartX=357.783 StartY=-18.082 StartZ=0 EndX=365.437 EndY=-19.1346 EndZ=0
    g49: LineSegment StartX=365.437 StartY=-19.1346 StartZ=0 EndX=373.765 EndY=-20.2573 EndZ=0
    g50: LineSegment StartX=373.765 StartY=-20.2573 StartZ=0 EndX=383.403 EndY=-21.3544 EndZ=0
    g51: LineSegment StartX=383.403 StartY=-21.3544 StartZ=0 EndX=390.321 EndY=-21.8765 EndZ=0
    g52: LineSegment StartX=390.321 StartY=-21.8765 StartZ=0 EndX=400.065 EndY=-22.3975 EndZ=0
    g53: LineSegment StartX=400.065 StartY=-22.3975 StartZ=0 EndX=410.412 EndY=-22.6053 EndZ=0
    g54: LineSegment StartX=410.412 StartY=-22.6053 StartZ=0 EndX=418.714 EndY=-22.5792 EndZ=0
    g55: LineSegment StartX=418.714 StartY=-22.5792 StartZ=0 EndX=425.327 EndY=-22.6169 EndZ=0
  constraints (62):
    c: Vertical(g0)
    c: Coincident(g0,g1)
    c: Coincident(g1,g2)
    c: Coincident(g2,g3)
    c: Coincident(g3,g4)
    c: Coincident(g4,g5)
    c: Coincident(g5,g6)
    c: Coincident(g6,g7)
    c: Coincident(g7,g8)
    c: Coincident(g8,g9)
    c: Coincident(g9,g10)
    c: Coincident(g10,g11)
    c: Coincident(g11,g12)
    c: Coincident(g12,g13)
    c: Coincident(g13,g14)
    c: Coincident(g14,g0)
    c: Vertical(g15)
    c: Coincident(g15,g16)
    c: Coincident(g16,g17)
    c: Coincident(g17,g18)
    c: Coincident(g18,g19)
    c: Coincident(g19,g20)
    c: Coincident(g20,g21)
    c: Coincident(g21,g22)
    c: Coincident(g22,g15)
    c: Parallel(g19,g23)
    c: Coincident(g23,g24)
    c: Coincident(g24,g25)
    c: Coincident(g25,g26)
    c: Coincident(g26,g27)
    c: Coincident(g27,g28)
    c: Coincident(g28,g29)
    c: Coincident(g29,g30)
    c: Coincident(g30,g31)
    c: Coincident(g31,g23)
    c: Parallel(g27,g32)
    c: Coincident(g32,g33)
    c: Coincident(g33,g34)
    c: Coincident(g34,g35)
    c: Coincident(g35,g36)
    c: Coincident(g36,g37)
    c: Coincident(g37,g38)
    c: Coincident(g38,g39)
    c: Coincident(g39,g40)
    c: Coincident(g40,g32)
    c: Coincident(g41,g42)
    c: Coincident(g42,g43)
    c: Coincident(g43,g44)
    c: Coincident(g44,g45)
    c: Coincident(g45,g46)
    c: Coincident(g46,g47)
    c: Vertical(g47)
    c: Coincident(g47,g48)
    c: Coincident(g48,g49)
    c: Coincident(g49,g50)
    c: Coincident(g50,g51)
    c: Coincident(g51,g52)
    c: Coincident(g52,g53)
    c: Coincident(g53,g54)
    c: Coincident(g54,g55)
    c: Coincident(g55,g41)
    c: Parallel(g36,g41)
FEATURE [PartDesign::Pocket] Pocket023
  BaseFeature = -> Pocket013
  Direction = (0,0,1)
  Length = 15
  Length2 = 5
  Profile = -> Sketch040
  ReferenceAxis = -> Sketch040 [N_Axis]
  Refine = true
  Suppressed = false
  Type = 0
FEATURE [Sketcher::SketchObject] Sketch041
  ArcFitTolerance = 1e-06
  AttachmentSupport = -> [Pocket023]
  FullyConstrained = false
  MakeInternals = false
  MapMode = 5
  Placement = pos=(0,0,-310) rot=(1,0,0;3.14159rad)
  sketch-geometry (1):
    g0: Circle CenterX=553.316 CenterY=-6.6 CenterZ=0 NormalX=0 NormalY=0 NormalZ=1 AngleXU=0 Radius=6.5
  constraints (2):
    c: Diameter(g0) = 13
    c: DistanceY(g0,g-1) = 6.6
FEATURE [PartDesign::Pad] Pad003
  BaseFeature = -> Pocket023
  Direction = (0,0,-1)
  Length = 10
  Length2 = 10
  Profile = -> Sketch041
  ReferenceAxis = -> Sketch041 [N_Axis]
  Refine = true
  Reversed = true
  Suppressed = false
  Type = 0
FEATURE [PartDesign::Plane] DatumPlane008
  AttachmentOffset = pos=(0,0,328) rot=(0,1,0;0.54042rad)
  AttachmentSupport = -> [Pad003]
  Length = 865.135
  MapMode = 5
  Placement = pos=(0,0,-638) rot=(0.963715,0,0.266934;3.14159rad)
  ResizeMode = 0
  Width = 90.6085
FEATURE [Sketcher::SketchObject] Sketch042
  ArcFitTolerance = 1e-06
  AttachmentSupport = -> [DatumPlane008]
  FullyConstrained = false
  MakeInternals = false
  MapMode = 5
  Placement = pos=(0,0,-638) rot=(0.963715,0,0.266934;3.14159rad)
  sketch-geometry (1):
    g0: Circle CenterX=642.946 CenterY=-6.5 CenterZ=0 NormalX=0 NormalY=0 NormalZ=1 AngleXU=0 Radius=2.5
  constraints (2):
    c: Diameter(g0) = 5
    c: DistanceY(g0,g-1) = 6.5
FEATURE [PartDesign::Pad] Pad004
  BaseFeature = -> Pad003
  Direction = (0.514496,0,-0.857493)
  Length = 20
  Length2 = 10
  Profile = -> Sketch042
  ReferenceAxis = -> Sketch042 [N_Axis]
  Refine = true
  Suppressed = false
  Type = 0
FEATURE [Sketcher::SketchObject] Sketch043
  ArcFitTolerance = 1e-06
  FullyConstrained = false
  MakeInternals = false
  Placement = pos=(600,0,-600) rot=(0,0,1;0rad)
  sketch-geometry (123):
    g0: BSplineCurve PolesCount=61 KnotsCount=61 Degree=3 IsPeriodic=1
    g1-g61: Circle [constr] x61 (B-spline internal-alignment scaffolding for g0; pole/knot coordinates omitted)
    g62-g122: GeomPoint [constr] x61 (B-spline internal-alignment scaffolding for g0; pole/knot coordinates omitted)
  constraints (123):
    c: InternalAlignment(g1,g0)
    c: Weight(g1) = 1
    c: InternalAlignment(g2,g0)
    c: Equal(g2,g1)
    c: InternalAlignment(g3,g0)
    c: Equal(g3,g1)
    c: InternalAlignment(g4,g0)
    c: Equal(g4,g1)
    c: InternalAlignment(g5,g0)
    c: Equal(g5,g1)
    c: InternalAlignment(g6,g0)
    c: Equal(g6,g1)
    c: InternalAlignment(g7,g0)
    c: Equal(g7,g1)
    c: InternalAlignment(g8,g0)
    c: Equal(g8,g1)
    c: InternalAlignment(g9,g0)
    c: Equal(g9,g1)
    c: InternalAlignment(g10,g0)
    c: Equal(g10,g1)
    c: InternalAlignment(g11,g0)
    c: Equal(g11,g1)
    c: InternalAlignment(g12,g0)
    c: Equal(g12,g1)
    c: InternalAlignment(g13,g0)
    c: Equal(g13,g1)
    c: InternalAlignment(g14,g0)
    c: Equal(g14,g1)
    c: InternalAlignment(g15,g0)
    c: Equal(g15,g1)
    c: InternalAlignment(g16,g0)
    c: Equal(g16,g1)
    c: InternalAlignment(g17,g0)
    c: Equal(g17,g1)
    c: InternalAlignment(g18,g0)
    c: Equal(g18,g1)
    c: InternalAlignment(g19,g0)
    c: Equal(g19,g1)
    c: InternalAlignment(g20,g0)
    c: Equal(g20,g1)
    c: InternalAlignment(g21,g0)
    c: Equal(g21,g1)
    c: InternalAlignment(g22,g0)
    c: Equal(g22,g1)
    c: InternalAlignment(g23,g0)
    c: Equal(g23,g1)
    c: InternalAlignment(g24,g0)
    c: Equal(g24,g1)
    c: InternalAlignment(g25,g0)
    c: Equal(g25,g1)
    c: InternalAlignment(g26,g0)
    c: Equal(g26,g1)
    c: InternalAlignment(g27,g0)
    c: Equal(g27,g1)
    c: InternalAlignment(g28,g0)
    c: Equal(g28,g1)
    c: InternalAlignment(g29,g0)
    c: Equal(g29,g1)
    c: InternalAlignment(g30,g0)
    c: Equal(g30,g1)
    c: InternalAlignment(g31,g0)
    c: Equal(g31,g1)
    c: InternalAlignment(g32,g0)
    c: Equal(g32,g1)
    c: InternalAlignment(g33,g0)
    c: Equal(g33,g1)
    c: InternalAlignment(g34,g0)
    c: Equal(g34,g1)
    c: InternalAlignment(g35,g0)
    c: Equal(g35,g1)
    c: InternalAlignment(g36,g0)
    c: Equal(g36,g1)
    c: InternalAlignment(g37,g0)
    c: Equal(g37,g1)
    c: InternalAlignment(g38,g0)
    c: Equal(g38,g1)
    c: InternalAlignment(g39,g0)
    c: Equal(g39,g1)
    c: InternalAlignment(g40,g0)
    c: Equal(g40,g1)
    c: InternalAlignment(g41,g0)
    c: Equal(g41,g1)
    c: InternalAlignment(g42,g0)
    c: Equal(g42,g1)
    c: InternalAlignment(g43,g0)
    c: Equal(g43,g1)
    c: InternalAlignment(g44,g0)
    c: Equal(g44,g1)
    c: InternalAlignment(g45,g0)
    c: Equal(g45,g1)
    c: InternalAlignment(g46,g0)
    c: Equal(g46,g1)
    c: InternalAlignment(g47,g0)
    c: Equal(g47,g1)
    c: InternalAlignment(g48,g0)
    c: Equal(g48,g1)
    c: InternalAlignment(g49,g0)
    c: Equal(g49,g1)
    c: InternalAlignment(g50,g0)
    c: Equal(g50,g1)
    c: InternalAlignment(g51,g0)
    c: Equal(g51,g1)
    c: InternalAlignment(g52,g0)
    c: Equal(g52,g1)
    c: InternalAlignment(g53,g0)
    c: Equal(g53,g1)
    c: InternalAlignment(g54,g0)
    c: Equal(g54,g1)
    c: InternalAlignment(g55,g0)
    c: Equal(g55,g1)
    c: InternalAlignment(g56,g0)
    c: Equal(g56,g1)
    c: InternalAlignment(g57,g0)
    c: Equal(g57,g1)
    c: InternalAlignment(g58,g0)
    c: Equal(g58,g1)
    c: InternalAlignment(g59,g0)
    c: Equal(g59,g1)
    c: InternalAlignment(g60,g0)
    c: Equal(g60,g1)
    c: InternalAlignment(g61,g0)
    c: Equal(g61,g1)
    c: InternalAlignment(g62-g122 -> g0) x61
FEATURE [Sketcher::SketchObject] Sketch044
  ArcFitTolerance = 1e-06
  FullyConstrained = false
  MakeInternals = false
  sketch-geometry (123):
    g0: BSplineCurve PolesCount=61 KnotsCount=61 Degree=3 IsPeriodic=1
    g1-g61: Circle [constr] x61 (B-spline internal-alignment scaffolding for g0; pole/knot coordinates omitted)
    g62-g122: GeomPoint [constr] x61 (B-spline internal-alignment scaffolding for g0; pole/knot coordinates omitted)
  constraints (123):
    c: InternalAlignment(g1,g0)
    c: Weight(g1) = 1
    c: InternalAlignment(g2,g0)
    c: Equal(g2,g1)
    c: InternalAlignment(g3,g0)
    c: Equal(g3,g1)
    c: InternalAlignment(g4,g0)
    c: Equal(g4,g1)
    c: InternalAlignment(g5,g0)
    c: Equal(g5,g1)
    c: InternalAlignment(g6,g0)
    c: Equal(g6,g1)
    c: InternalAlignment(g7,g0)
    c: Equal(g7,g1)
    c: InternalAlignment(g8,g0)
    c: Equal(g8,g1)
    c: InternalAlignment(g9,g0)
    c: Equal(g9,g1)
    c: InternalAlignment(g10,g0)
    c: Equal(g10,g1)
    c: InternalAlignment(g11,g0)
    c: Equal(g11,g1)
    c: InternalAlignment(g12,g0)
    c: Equal(g12,g1)
    c: InternalAlignment(g13,g0)
    c: Equal(g13,g1)
    c: InternalAlignment(g14,g0)
    c: Equal(g14,g1)
    c: InternalAlignment(g15,g0)
    c: Equal(g15,g1)
    c: InternalAlignment(g16,g0)
    c: Equal(g16,g1)
    c: InternalAlignment(g17,g0)
    c: Equal(g17,g1)
    c: InternalAlignment(g18,g0)
    c: Equal(g18,g1)
    c: InternalAlignment(g19,g0)
    c: Equal(g19,g1)
    c: InternalAlignment(g20,g0)
    c: Equal(g20,g1)
    c: InternalAlignment(g21,g0)
    c: Equal(g21,g1)
    c: InternalAlignment(g22,g0)
    c: Equal(g22,g1)
    c: InternalAlignment(g23,g0)
    c: Equal(g23,g1)
    c: InternalAlignment(g24,g0)
    c: Equal(g24,g1)
    c: InternalAlignment(g25,g0)
    c: Equal(g25,g1)
    c: InternalAlignment(g26,g0)
    c: Equal(g26,g1)
    c: InternalAlignment(g27,g0)
    c: Equal(g27,g1)
    c: InternalAlignment(g28,g0)
    c: Equal(g28,g1)
    c: InternalAlignment(g29,g0)
    c: Equal(g29,g1)
    c: InternalAlignment(g30,g0)
    c: Equal(g30,g1)
    c: InternalAlignment(g31,g0)
    c: Equal(g31,g1)
    c: InternalAlignment(g32,g0)
    c: Equal(g32,g1)
    c: InternalAlignment(g33,g0)
    c: Equal(g33,g1)
    c: InternalAlignment(g34,g0)
    c: Equal(g34,g1)
    c: InternalAlignment(g35,g0)
    c: Equal(g35,g1)
    c: InternalAlignment(g36,g0)
    c: Equal(g36,g1)
    c: InternalAlignment(g37,g0)
    c: Equal(g37,g1)
    c: InternalAlignment(g38,g0)
    c: Equal(g38,g1)
    c: InternalAlignment(g39,g0)
    c: Equal(g39,g1)
    c: InternalAlignment(g40,g0)
    c: Equal(g40,g1)
    c: InternalAlignment(g41,g0)
    c: Equal(g41,g1)
    c: InternalAlignment(g42,g0)
    c: Equal(g42,g1)
    c: InternalAlignment(g43,g0)
    c: Equal(g43,g1)
    c: InternalAlignment(g44,g0)
    c: Equal(g44,g1)
    c: InternalAlignment(g45,g0)
    c: Equal(g45,g1)
    c: InternalAlignment(g46,g0)
    c: Equal(g46,g1)
    c: InternalAlignment(g47,g0)
    c: Equal(g47,g1)
    c: InternalAlignment(g48,g0)
    c: Equal(g48,g1)
    c: InternalAlignment(g49,g0)
    c: Equal(g49,g1)
    c: InternalAlignment(g50,g0)
    c: Equal(g50,g1)
    c: InternalAlignment(g51,g0)
    c: Equal(g51,g1)
    c: InternalAlignment(g52,g0)
    c: Equal(g52,g1)
    c: InternalAlignment(g53,g0)
    c: Equal(g53,g1)
    c: InternalAlignment(g54,g0)
    c: Equal(g54,g1)
    c: InternalAlignment(g55,g0)
    c: Equal(g55,g1)
    c: InternalAlignment(g56,g0)
    c: Equal(g56,g1)
    c: InternalAlignment(g57,g0)
    c: Equal(g57,g1)
    c: InternalAlignment(g58,g0)
    c: Equal(g58,g1)
    c: InternalAlignment(g59,g0)
    c: Equal(g59,g1)
    c: InternalAlignment(g60,g0)
    c: Equal(g60,g1)
    c: InternalAlignment(g61,g0)
    c: Equal(g61,g1)
    c: InternalAlignment(g62-g122 -> g0) x61
FEATURE [PartDesign::AdditiveLoft] AdditiveLoft007
  Closed = false
  Profile = -> Sketch044
  Refine = true
  Ruled = false
  Sections = -> [Sketch043]
  Suppressed = false
FEATURE [PartDesign::Plane] DatumPlane009
  AttachmentOffset = pos=(0,0,0) rot=(0,-1,0;0.785398rad)
  AttachmentSupport = -> [AdditiveLoft007]
  Length = 743.192
  MapMode = 5
  Placement = pos=(0,0,0) rot=(0,-1,0;0.785398rad)
  ResizeMode = 0
  Width = 87.5666
FEATURE [Sketcher::SketchObject] Sketch045
  ArcFitTolerance = 1e-06
  AttachmentSupport = -> [DatumPlane009]
  FullyConstrained = false
  MakeInternals = false
  MapMode = 5
  Placement = pos=(0,0,0) rot=(0,-1,0;0.785398rad)
  sketch-geometry (1):
    g0: Circle CenterX=28.3343 CenterY=4.75298 CenterZ=0 NormalX=0 NormalY=0 NormalZ=1 AngleXU=0 Radius=4.1
  constraints (1):
    c: Diameter(g0) = 8.2
FEATURE [PartDesign::Pocket] Pocket024
  BaseFeature = -> AdditiveLoft007
  Direction = (0.707107,0,-0.707107)
  Length = 1000
  Length2 = 5
  Profile = -> Sketch045
  ReferenceAxis = -> Sketch045 [N_Axis]
  Refine = true
  Suppressed = false
  Type = 0
FEATURE [Sketcher::SketchObject] Sketch046
  ArcFitTolerance = 1e-06
  AttachmentSupport = -> [Pocket024]
  FullyConstrained = false
  MakeInternals = false
  MapMode = 5
  sketch-geometry (4):
    g0: LineSegment StartX=-344.991 StartY=348.339 StartZ=0 EndX=-344.991 EndY=-308.863 EndZ=0
    g1: LineSegment StartX=-344.991 StartY=-308.863 StartZ=0 EndX=993.672 EndY=-308.863 EndZ=0
    g2: LineSegment StartX=993.672 StartY=-308.863 StartZ=0 EndX=993.672 EndY=348.339 EndZ=0
    g3: LineSegment StartX=993.672 StartY=348.339 StartZ=0 EndX=-344.991 EndY=348.339 EndZ=0
  constraints (8):
    c: Coincident(g0,g1)
    c: Coincident(g1,g2)
    c: Coincident(g2,g3)
    c: Coincident(g3,g0)
    c: Vertical(g0)
    c: Vertical(g2)
    c: Horizontal(g1)
    c: Horizontal(g3)
FEATURE [PartDesign::Pocket] Pocket025
  BaseFeature = -> Pocket024
  Direction = (0,0,-1)
  Length = 300
  Length2 = 5
  Profile = -> Sketch046
  ReferenceAxis = -> Sketch046 [N_Axis]
  Refine = true
  Suppressed = false
  Type = 0
FEATURE [Sketcher::SketchObject] Sketch047
  ArcFitTolerance = 1e-06
  AttachmentSupport = -> [Pocket025]
  FullyConstrained = false
  MakeInternals = false
  MapMode = 5
  Placement = pos=(0,0,-600) rot=(1,0,0;3.14159rad)
  sketch-geometry (4):
    g0: LineSegment StartX=196.967 StartY=129.212 StartZ=0 EndX=196.967 EndY=-99.542 EndZ=0
    g1: LineSegment StartX=196.967 StartY=-99.542 StartZ=0 EndX=981.265 EndY=-99.542 EndZ=0
    g2: LineSegment StartX=981.265 StartY=-99.542 StartZ=0 EndX=981.265 EndY=129.212 EndZ=0
    g3: LineSegment StartX=981.265 StartY=129.212 StartZ=0 EndX=196.967 EndY=129.212 EndZ=0
  constraints (8):
    c: Coincident(g0,g1)
    c: Coincident(g1,g2)
    c: Coincident(g2,g3)
    c: Coincident(g3,g0)
    c: Vertical(g0)
    c: Vertical(g2)
    c: Horizontal(g1)
    c: Horizontal(g3)
FEATURE [PartDesign::Pocket] Pocket026
  BaseFeature = -> Pocket025
  Direction = (0,0,1)
  Length = 290
  Length2 = 5
  Profile = -> Sketch047
  ReferenceAxis = -> Sketch047 [N_Axis]
  Refine = true
  Suppressed = false
  Type = 0
FEATURE [Sketcher::SketchObject] Sketch048
  ArcFitTolerance = 1e-06
  AttachmentSupport = -> [Pocket026]
  FullyConstrained = false
  MakeInternals = false
  MapMode = 5
  Placement = pos=(0,0,-310) rot=(1,0,0;3.14159rad)
  sketch-geometry (56):
    g0: LineSegment StartX=332.032 StartY=3.92783 StartZ=0 EndX=332.032 EndY=-12.0562 EndZ=0
    g1: LineSegment StartX=332.032 StartY=-12.0562 StartZ=0 EndX=330.396 EndY=-11.418 EndZ=0
    g2: LineSegment StartX=330.396 StartY=-11.418 StartZ=0 EndX=325.235 EndY=-9.31772 EndZ=0
    g3: LineSegment StartX=325.235 StartY=-9.31772 StartZ=0 EndX=321.545 EndY=-7.54348 EndZ=0
    g4: LineSegment StartX=321.545 StartY=-7.54348 StartZ=0 EndX=318.351 EndY=-5.6273 EndZ=0
    g5: LineSegment StartX=318.351 StartY=-5.6273 StartZ=0 EndX=315.441 EndY=-3.71112 EndZ=0
    g6: LineSegment StartX=315.441 StartY=-3.71112 StartZ=0 EndX=314.022 EndY=-2.22077 EndZ=0
    g7: LineSegment StartX=314.022 StartY=-2.22077 StartZ=0 EndX=313.099 EndY=-0.659436 EndZ=0
    g8: LineSegment StartX=313.099 StartY=-0.659436 StartZ=0 EndX=312.957 EndY=0.476075 EndZ=0
    g9: LineSegment StartX=312.957 StartY=0.476075 StartZ=0 EndX=313.596 EndY=0.901893 EndZ=0
    g10: LineSegment StartX=313.596 StartY=0.901893 StartZ=0 EndX=315.654 EndY=1.75353 EndZ=0
    g11: LineSegment StartX=315.654 StartY=1.75353 StartZ=0 EndX=318.777 EndY=2.60516 EndZ=0
    g12: LineSegment StartX=318.777 StartY=2.60516 StartZ=0 EndX=322.325 EndY=3.10195 EndZ=0
    g13: LineSegment StartX=322.325 StartY=3.10195 StartZ=0 EndX=327.435 EndY=3.52776 EndZ=0
    g14: LineSegment StartX=327.435 StartY=3.52776 StartZ=0 EndX=332.032 EndY=3.92783 EndZ=0
    g15: LineSegment StartX=596.656 StartY=-2.47566 StartZ=0 EndX=596.656 EndY=-4.90277 EndZ=0
    g16: LineSegment StartX=596.656 StartY=-4.90277 StartZ=0 EndX=568.724 EndY=-9.51106 EndZ=0
    g17: LineSegment StartX=568.724 StartY=-9.51106 StartZ=0 EndX=547.062 EndY=-12.2805 EndZ=0
    g18: LineSegment StartX=547.062 StartY=-12.2805 StartZ=0 EndX=536.786 EndY=-13.5531 EndZ=0
    g19: LineSegment StartX=536.786 StartY=-13.5531 StartZ=0 EndX=527.534 EndY=-0.989378 EndZ=0
    g20: LineSegment StartX=527.534 StartY=-0.989378 StartZ=0 EndX=547.951 EndY=-1.76517 EndZ=0
    g21: LineSegment StartX=547.951 StartY=-1.76517 StartZ=0 EndX=582.087 EndY=-2.61681 EndZ=0
    g22: LineSegment StartX=582.087 StartY=-2.61681 StartZ=0 EndX=596.656 EndY=-2.47566 EndZ=0
    g23: LineSegment StartX=531.003 StartY=-14.2202 StartZ=0 EndX=520.9 EndY=-0.500741 EndZ=0
    g24: LineSegment StartX=531.003 StartY=-14.2202 StartZ=0 EndX=505.941 EndY=-17.0028 EndZ=0
    g25: LineSegment StartX=505.941 StartY=-17.0028 StartZ=0 EndX=482.916 EndY=-18.8581 EndZ=0
    g26: LineSegment StartX=482.916 StartY=-18.8581 StartZ=0 EndX=470.676 EndY=-19.744 EndZ=0
    g27: LineSegment StartX=470.676 StartY=-19.744 StartZ=0 EndX=480.564 EndY=0.541013 EndZ=0
    g28: LineSegment StartX=480.564 StartY=0.541013 StartZ=0 EndX=493.641 EndY=0.022556 EndZ=0
    g29: LineSegment StartX=493.641 StartY=0.022556 StartZ=0 EndX=506.533 EndY=-0.26288 EndZ=0
    g30: LineSegment StartX=506.533 StartY=-0.26288 StartZ=0 EndX=515.762 EndY=-0.310453 EndZ=0
    g31: LineSegment StartX=515.762 StartY=-0.310453 StartZ=0 EndX=520.9 EndY=-0.500741 EndZ=0
    g32: LineSegment StartX=475.564 StartY=0.974291 StartZ=0 EndX=464.963 EndY=-20.7733 EndZ=0
    g33: LineSegment StartX=475.564 StartY=0.974291 StartZ=0 EndX=453.041 EndY=1.52388 EndZ=0
    g34: LineSegment StartX=453.041 StartY=1.52388 StartZ=0 EndX=427.59 EndY=2.38018 EndZ=0
    g35: LineSegment StartX=427.59 StartY=2.38018 StartZ=0 EndX=415.511 EndY=2.89765 EndZ=0
    g36: LineSegment StartX=415.511 StartY=2.89765 StartZ=0 EndX=431.488 EndY=-22.3382 EndZ=0
    g37: LineSegment StartX=431.488 StartY=-22.3382 StartZ=0 EndX=441.844 EndY=-22.1764 EndZ=0
    g38: LineSegment StartX=441.844 StartY=-22.1764 StartZ=0 EndX=450.773 EndY=-21.9213 EndZ=0
    g39: LineSegment StartX=450.773 StartY=-21.9213 StartZ=0 EndX=460.18 EndY=-21.2835 EndZ=0
    g40: LineSegment StartX=460.18 StartY=-21.2835 StartZ=0 EndX=464.963 EndY=-20.7733 EndZ=0
    g41: LineSegment StartX=425.327 StartY=-22.6169 StartZ=0 EndX=408.845 EndY=3.41656 EndZ=0
    g42: LineSegment StartX=408.845 StartY=3.41656 StartZ=0 EndX=398.718 EndY=3.65025 EndZ=0
    g43: LineSegment StartX=398.718 StartY=3.65025 StartZ=0 EndX=388.942 EndY=4.00079 EndZ=0
    g44: LineSegment StartX=388.942 StartY=4.00079 StartZ=0 EndX=379.162 EndY=4.1568 EndZ=0
    g45: LineSegment StartX=379.162 StartY=4.1568 StartZ=0 EndX=371.688 EndY=4.23449 EndZ=0
    g46: LineSegment StartX=371.688 StartY=4.23449 StartZ=0 EndX=357.783 EndY=4.06055 EndZ=0
    g47: LineSegment StartX=357.783 StartY=4.06055 StartZ=0 EndX=357.783 EndY=-18.082 EndZ=0
    g48: LineSegment StartX=357.783 StartY=-18.082 StartZ=0 EndX=365.437 EndY=-19.1346 EndZ=0
    g49: LineSegment StartX=365.437 StartY=-19.1346 StartZ=0 EndX=373.765 EndY=-20.2573 EndZ=0
    g50: LineSegment StartX=373.765 StartY=-20.2573 StartZ=0 EndX=383.403 EndY=-21.3544 EndZ=0
    g51: LineSegment StartX=383.403 StartY=-21.3544 StartZ=0 EndX=390.321 EndY=-21.8765 EndZ=0
    g52: LineSegment StartX=390.321 StartY=-21.8765 StartZ=0 EndX=400.065 EndY=-22.3975 EndZ=0
    g53: LineSegment StartX=400.065 StartY=-22.3975 StartZ=0 EndX=410.412 EndY=-22.6053 EndZ=0
    g54: LineSegment StartX=410.412 StartY=-22.6053 StartZ=0 EndX=418.714 EndY=-22.5792 EndZ=0
    g55: LineSegment StartX=418.714 StartY=-22.5792 StartZ=0 EndX=425.327 EndY=-22.6169 EndZ=0
  constraints (62):
    c: Vertical(g0)
    c: Coincident(g0,g1)
    c: Coincident(g1,g2)
    c: Coincident(g2,g3)
    c: Coincident(g3,g4)
    c: Coincident(g4,g5)
    c: Coincident(g5,g6)
    c: Coincident(g6,g7)
    c: Coincident(g7,g8)
    c: Coincident(g8,g9)
    c: Coincident(g9,g10)
    c: Coincident(g10,g11)
    c: Coincident(g11,g12)
    c: Coincident(g12,g13)
    c: Coincident(g13,g14)
    c: Coincident(g14,g0)
    c: Vertical(g15)
    c: Coincident(g15,g16)
    c: Coincident(g16,g17)
    c: Coincident(g17,g18)
    c: Coincident(g18,g19)
    c: Coincident(g19,g20)
    c: Coincident(g20,g21)
    c: Coincident(g21,g22)
    c: Coincident(g22,g15)
    c: Parallel(g19,g23)
    c: Coincident(g23,g24)
    c: Coincident(g24,g25)
    c: Coincident(g25,g26)
    c: Coincident(g26,g27)
    c: Coincident(g27,g28)
    c: Coincident(g28,g29)
    c: Coincident(g29,g30)
    c: Coincident(g30,g31)
    c: Coincident(g31,g23)
    c: Parallel(g27,g32)
    c: Coincident(g32,g33)
    c: Coincident(g33,g34)
    c: Coincident(g34,g35)
    c: Coincident(g35,g36)
    c: Coincident(g36,g37)
    c: Coincident(g37,g38)
    c: Coincident(g38,g39)
    c: Coincident(g39,g40)
    c: Coincident(g40,g32)
    c: Coincident(g41,g42)
    c: Coincident(g42,g43)
    c: Coincident(g43,g44)
    c: Coincident(g44,g45)
    c: Coincident(g45,g46)
    c: Coincident(g46,g47)
    c: Vertical(g47)
    c: Coincident(g47,g48)
    c: Coincident(g48,g49)
    c: Coincident(g49,g50)
    c: Coincident(g50,g51)
    c: Coincident(g51,g52)
    c: Coincident(g52,g53)
    c: Coincident(g53,g54)
    c: Coincident(g54,g55)
    c: Coincident(g55,g41)
    c: Parallel(g36,g41)
FEATURE [PartDesign::Pocket] Pocket027
  BaseFeature = -> Pocket026
  Direction = (0,0,1)
  Length = 15
  Length2 = 5
  Profile = -> Sketch048
  ReferenceAxis = -> Sketch048 [N_Axis]
  Refine = true
  Suppressed = false
  Type = 0
FEATURE [Sketcher::SketchObject] Sketch049
  ArcFitTolerance = 1e-06
  AttachmentSupport = -> [Pocket027]
  FullyConstrained = false
  MakeInternals = false
  MapMode = 5
  Placement = pos=(0,0,-310) rot=(1,0,0;3.14159rad)
  sketch-geometry (1):
    g0: Circle CenterX=553.316 CenterY=-6.6 CenterZ=0 NormalX=0 NormalY=0 NormalZ=1 AngleXU=0 Radius=6.5
  constraints (2):
    c: Diameter(g0) = 13
    c: DistanceY(g0,g-1) = 6.6
FEATURE [PartDesign::Pad] Pad005
  BaseFeature = -> Pocket027
  Direction = (0,0,-1)
  Length = 10
  Length2 = 10
  Profile = -> Sketch049
  ReferenceAxis = -> Sketch049 [N_Axis]
  Refine = true
  Reversed = true
  Suppressed = false
  Type = 0
FEATURE [PartDesign::Plane] DatumPlane010
  AttachmentOffset = pos=(0,0,328) rot=(0,1,0;0.54042rad)
  AttachmentSupport = -> [Pad005]
  Length = 930.255
  MapMode = 5
  Placement = pos=(0,0,-638) rot=(0.963715,0,0.266934;3.14159rad)
  ResizeMode = 0
  Width = 92.1452
FEATURE [Sketcher::SketchObject] Sketch050
  ArcFitTolerance = 1e-06
  AttachmentSupport = -> [DatumPlane010]
  FullyConstrained = false
  MakeInternals = false
  MapMode = 5
  Placement = pos=(0,0,-638) rot=(0.963715,0,0.266934;3.14159rad)
  sketch-geometry (1):
    g0: Circle CenterX=642.946 CenterY=-6.5 CenterZ=0 NormalX=0 NormalY=0 NormalZ=1 AngleXU=0 Radius=2.5
  constraints (2):
    c: Diameter(g0) = 5
    c: DistanceY(g0,g-1) = 6.5
FEATURE [PartDesign::Pad] Pad006
  BaseFeature = -> Pad005
  Direction = (0.514496,0,-0.857493)
  Length = 20
  Length2 = 10
  Profile = -> Sketch050
  ReferenceAxis = -> Sketch050 [N_Axis]
  Refine = true
  Suppressed = false
  Type = 0
FEATURE [Sketcher::SketchObject] Sketch051
  ArcFitTolerance = 1e-06
  AttachmentSupport = -> [Pad004]
  FullyConstrained = false
  MakeInternals = false
  MapMode = 5
  Placement = pos=(0,0,-310) rot=(1,0,0;3.14159rad)
  sketch-geometry (4):
    g0: LineSegment StartX=560 StartY=2.94348 StartZ=0 EndX=560 EndY=-14.7871 EndZ=0
    g1: LineSegment StartX=560 StartY=-14.7871 StartZ=0 EndX=644.72 EndY=-14.7871 EndZ=0
    g2: LineSegment StartX=644.72 StartY=-14.7871 StartZ=0 EndX=644.72 EndY=2.94348 EndZ=0
    g3: LineSegment StartX=644.72 StartY=2.94348 StartZ=0 EndX=560 EndY=2.94348 EndZ=0
  constraints (9):
    c: Coincident(g0,g1)
    c: Coincident(g1,g2)
    c: Coincident(g2,g3)
    c: Coincident(g3,g0)
    c: Vertical(g0)
    c: Vertical(g2)
    c: Horizontal(g1)
    c: Horizontal(g3)
    c: DistanceX(g-1,g0) = 560
FEATURE [PartDesign::Pocket] Pocket028
  BaseFeature = -> Pad004
  Direction = (0,0,1)
  Length = 15
  Length2 = 5
  Profile = -> Sketch051
  ReferenceAxis = -> Sketch051 [N_Axis]
  Refine = true
  Suppressed = false
  Type = 0
FEATURE [PartDesign::Body] Body003
  AllowCompound = false
  Group = -> [Sketch010,Sketch009,AdditiveLoft003,DatumPlane003,Sketch011,Pocket003,Sketch026,Pocket012,Sketch027,Pocket013,Sketch040,Pocket023,Sketch041,Pad003,DatumPlane008,Sketch042,Pad004,Sketch051,Pocket028]
  Origin = -> Origin003
  Placement = pos=(0,0,-100) rot=(0,0,1;0rad)
  Tip = -> Pocket028
FEATURE [Sketcher::SketchObject] Sketch052
  ArcFitTolerance = 1e-06
  AttachmentSupport = -> [Pad006]
  FullyConstrained = false
  MakeInternals = false
  MapMode = 5
  Placement = pos=(0,0,-310) rot=(1,0,0;3.14159rad)
  sketch-geometry (4):
    g0: LineSegment StartX=263.238 StartY=35.4122 StartZ=0 EndX=263.238 EndY=-50.8588 EndZ=0
    g1: LineSegment StartX=263.238 StartY=-50.8588 StartZ=0 EndX=560 EndY=-50.8588 EndZ=0
    g2: LineSegment StartX=560 StartY=-50.8588 StartZ=0 EndX=560 EndY=35.4122 EndZ=0
    g3: LineSegment StartX=560 StartY=35.4122 StartZ=0 EndX=263.238 EndY=35.4122 EndZ=0
  constraints (9):
    c: Coincident(g0,g1)
    c: Coincident(g1,g2)
    c: Coincident(g2,g3)
    c: Coincident(g3,g0)
    c: Vertical(g0)
    c: Vertical(g2)
    c: Horizontal(g1)
    c: Horizontal(g3)
    c: DistanceX(g-1,g2) = 560
FEATURE [PartDesign::Pocket] Pocket029
  BaseFeature = -> Pad006
  Direction = (0,0,1)
  Length = 20
  Length2 = 5
  Midplane = true
  Profile = -> Sketch052
  ReferenceAxis = -> Sketch052 [N_Axis]
  Refine = true
  Suppressed = false
  Type = 0
FEATURE [PartDesign::Body] Body007
  AllowCompound = false
  Group = -> [Sketch044,Sketch043,AdditiveLoft007,DatumPlane009,Sketch045,Pocket024,Sketch046,Pocket025,Sketch047,Pocket026,Sketch048,Pocket027,Sketch049,Pad005,DatumPlane010,Sketch050,Pad006,Sketch052,Pocket029]
  Origin = -> Origin007
  Placement = pos=(0,0,-100) rot=(0,0,1;0rad)
  Tip = -> Pocket029
FEATURE [Sketcher::SketchObject] Sketch053
  ArcFitTolerance = 1e-06
  AttachmentSupport = -> [Pocket011]
  FullyConstrained = false
  MakeInternals = false
  MapMode = 5
  Placement = pos=(0,0,-210) rot=(1,0,0;3.14159rad)
  sketch-geometry (69):
    g0: LineSegment StartX=232.935 StartY=-13.2277 StartZ=0 EndX=232.935 EndY=3.96212 EndZ=0
    g1: LineSegment StartX=232.935 StartY=3.96212 StartZ=0 EndX=230.333 EndY=3.82301 EndZ=0
    g2: LineSegment StartX=230.333 StartY=3.82301 StartZ=0 EndX=226.374 EndY=3.53509 EndZ=0
    g3: LineSegment StartX=226.374 StartY=3.53509 StartZ=0 EndX=223.207 EndY=3.1032 EndZ=0
    g4: LineSegment StartX=223.207 StartY=3.1032 StartZ=0 EndX=219.176 EndY=2.45538 EndZ=0
    g5: LineSegment StartX=219.176 StartY=2.45538 StartZ=0 EndX=215.793 EndY=1.80756 EndZ=0
    g6: LineSegment StartX=215.793 StartY=1.80756 StartZ=0 EndX=213.633 EndY=1.08775 EndZ=0
    g7: LineSegment StartX=213.633 StartY=1.08775 StartZ=0 EndX=212.553 EndY=0 EndZ=0
    g8: LineSegment StartX=212.553 StartY=0 StartZ=0 EndX=213.273 EndY=-1.86345 EndZ=0
    g9: LineSegment StartX=213.273 StartY=-1.86345 StartZ=0 EndX=214.569 EndY=-3.37504 EndZ=0
    g10: LineSegment StartX=214.569 StartY=-3.37504 StartZ=0 EndX=216.512 EndY=-4.88663 EndZ=0
    g11: LineSegment StartX=216.512 StartY=-4.88663 StartZ=0 EndX=218.888 EndY=-6.61416 EndZ=0
    g12: LineSegment StartX=218.888 StartY=-6.61416 StartZ=0 EndX=221.623 EndY=-8.26971 EndZ=0
    g13: LineSegment StartX=221.623 StartY=-8.26971 StartZ=0 EndX=224.862 EndY=-9.85328 EndZ=0
    g14: LineSegment StartX=224.862 StartY=-9.85328 StartZ=0 EndX=227.597 EndY=-11.1489 EndZ=0
    g15: LineSegment StartX=227.597 StartY=-11.1489 StartZ=0 EndX=230.621 EndY=-12.3726 EndZ=0
    g16: LineSegment StartX=230.621 StartY=-12.3726 StartZ=0 EndX=232.935 EndY=-13.2277 EndZ=0
    g17: LineSegment StartX=529.448 StartY=-5.42158 StartZ=0 EndX=529.373 EndY=-2.77124 EndZ=0
    g18: LineSegment StartX=529.373 StartY=-2.77124 StartZ=0 EndX=518.644 EndY=-2.45257 EndZ=0
    g19: LineSegment StartX=518.644 StartY=-2.45257 StartZ=0 EndX=507.384 EndY=-2.45257 EndZ=0
    g20: LineSegment StartX=507.384 StartY=-2.45257 StartZ=0 EndX=492.088 EndY=-2.1339 EndZ=0
    g21: LineSegment StartX=492.088 StartY=-2.1339 StartZ=0 EndX=474.647 EndY=-1.51705 EndZ=0
    g22: LineSegment StartX=474.647 StartY=-1.51705 StartZ=0 EndX=468.174 EndY=-1.28599 EndZ=0
    g23: LineSegment StartX=468.174 StartY=-1.28599 StartZ=0 EndX=476.745 EndY=-13.3358 EndZ=0
    g24: LineSegment StartX=476.745 StartY=-13.3358 StartZ=0 EndX=493.617 EndY=-10.9006 EndZ=0
    g25: LineSegment StartX=493.617 StartY=-10.9006 StartZ=0 EndX=505.184 EndY=-9.07429 EndZ=0
    g26: LineSegment StartX=505.184 StartY=-9.07429 StartZ=0 EndX=516.49 EndY=-7.42187 EndZ=0
    g27: LineSegment StartX=516.49 StartY=-7.42187 StartZ=0 EndX=524.752 EndY=-6.2043 EndZ=0
    g28: LineSegment StartX=524.752 StartY=-6.2043 StartZ=0 EndX=529.448 EndY=-5.42158 EndZ=0
    g29: LineSegment StartX=472.33 StartY=-14.3284 StartZ=0 EndX=463.007 EndY=-1.22045 EndZ=0
    g30: LineSegment StartX=463.007 StartY=-1.22045 StartZ=0 EndX=436.979 EndY=-0.55496 EndZ=0
    g31: LineSegment StartX=436.979 StartY=-0.55496 StartZ=0 EndX=421.281 EndY=-0.0939564 EndZ=0
    g32: LineSegment StartX=421.281 StartY=-0.0939564 StartZ=0 EndX=408.215 EndY=-21.1936 EndZ=0
    g33: LineSegment StartX=408.215 StartY=-21.1936 StartZ=0 EndX=422.281 EndY=-20.1232 EndZ=0
    g34: LineSegment StartX=422.281 StartY=-20.1232 StartZ=0 EndX=436.37 EndY=-18.8185 EndZ=0
    g35: LineSegment StartX=436.37 StartY=-18.8185 StartZ=0 EndX=450.546 EndY=-17.0789 EndZ=0
    g36: LineSegment StartX=450.546 StartY=-17.0789 StartZ=0 EndX=464.722 EndY=-15.5133 EndZ=0
    g37: LineSegment StartX=464.722 StartY=-15.5133 StartZ=0 EndX=472.33 EndY=-14.3284 EndZ=0
    g38: LineSegment StartX=402.538 StartY=-21.4405 StartZ=0 EndX=415.866 EndY=0.0815263 EndZ=0
    g39: LineSegment StartX=415.866 StartY=0.0815263 StartZ=0 EndX=393.968 EndY=0.858652 EndZ=0
    g40: LineSegment StartX=393.968 StartY=0.858652 StartZ=0 EndX=379.742 EndY=1.33409 EndZ=0
    g41: LineSegment StartX=379.742 StartY=1.33409 StartZ=0 EndX=367.191 EndY=1.7451 EndZ=0
    g42: LineSegment StartX=367.191 StartY=1.7451 StartZ=0 EndX=355.656 EndY=2.10097 EndZ=0
    g43: LineSegment StartX=355.656 StartY=2.10097 StartZ=0 EndX=344.334 EndY=2.58371 EndZ=0
    g44: LineSegment StartX=344.334 StartY=2.58371 StartZ=0 EndX=336.607 EndY=2.93983 EndZ=0
    g45: LineSegment StartX=336.607 StartY=2.93983 StartZ=0 EndX=353.364 EndY=-23.826 EndZ=0
    g46: LineSegment StartX=353.364 StartY=-23.826 StartZ=0 EndX=368.687 EndY=-23.2476 EndZ=0
    g47: LineSegment StartX=368.687 StartY=-23.2476 StartZ=0 EndX=385.349 EndY=-22.4641 EndZ=0
    g48: LineSegment StartX=385.349 StartY=-22.4641 StartZ=0 EndX=397.881 EndY=-21.6807 EndZ=0
    g49: LineSegment StartX=397.881 StartY=-21.6807 StartZ=0 EndX=402.538 EndY=-21.4405 EndZ=0
    g50: LineSegment StartX=347.682 StartY=-24.0752 StartZ=0 EndX=330.602 EndY=3.20634 EndZ=0
    g51: LineSegment StartX=330.602 StartY=3.20634 StartZ=0 EndX=312.355 EndY=3.43929 EndZ=0
    g52: LineSegment StartX=312.355 StartY=3.43929 StartZ=0 EndX=297.314 EndY=3.73057 EndZ=0
    g53: LineSegment StartX=297.314 StartY=3.73057 StartZ=0 EndX=286.58 EndY=4.11889 EndZ=0
    g54: LineSegment StartX=286.58 StartY=4.11889 StartZ=0 EndX=271.742 EndY=-21.5893 EndZ=0
    g55: LineSegment StartX=271.742 StartY=-21.5893 StartZ=0 EndX=279.89 EndY=-22.1672 EndZ=0
    g56: LineSegment StartX=279.89 StartY=-22.1672 StartZ=0 EndX=293.298 EndY=-23.0415 EndZ=0
    g57: LineSegment StartX=293.298 StartY=-23.0415 StartZ=0 EndX=308.688 EndY=-23.8574 EndZ=0
    g58: LineSegment StartX=308.688 StartY=-23.8574 StartZ=0 EndX=319.648 EndY=-24.0905 EndZ=0
    g59: LineSegment StartX=319.648 StartY=-24.0905 StartZ=0 EndX=332.415 EndY=-24.1486 EndZ=0
    g60: LineSegment StartX=332.415 StartY=-24.1486 StartZ=0 EndX=341.218 EndY=-24.0902 EndZ=0
    g61: LineSegment StartX=341.218 StartY=-24.0902 StartZ=0 EndX=347.682 EndY=-24.0752 EndZ=0
    g62: LineSegment StartX=281.696 StartY=4.48378 StartZ=0 EndX=267.107 EndY=-20.7944 EndZ=0
    g63: LineSegment StartX=267.107 StartY=-20.7944 StartZ=0 EndX=262.676 EndY=-20.2115 EndZ=0
    g64: LineSegment StartX=262.676 StartY=-20.2115 StartZ=0 EndX=258.595 EndY=-19.7452 EndZ=0
    g65: LineSegment StartX=258.595 StartY=-19.7452 StartZ=0 EndX=258.595 EndY=4.97283 EndZ=0
    g66: LineSegment StartX=258.595 StartY=4.97283 StartZ=0 EndX=267.689 EndY=4.85636 EndZ=0
    g67: LineSegment StartX=267.689 StartY=4.85636 StartZ=0 EndX=275.21 EndY=4.73986 EndZ=0
    g68: LineSegment StartX=275.21 StartY=4.73986 StartZ=0 EndX=281.696 EndY=4.48378 EndZ=0
  constraints (76):
    c: Vertical(g0)
    c: Coincident(g0,g1)
    c: Coincident(g1,g2)
    c: Coincident(g2,g3)
    c: Coincident(g3,g4)
    c: Coincident(g4,g5)
    c: Coincident(g5,g6)
    c: Coincident(g6,g7)
    c: PointOnObject(g7,g-1)
    c: Coincident(g7,g8)
    c: Coincident(g8,g9)
    c: Coincident(g9,g10)
    c: Coincident(g10,g11)
    c: Coincident(g11,g12)
    c: Coincident(g12,g13)
    c: Coincident(g13,g14)
    c: Coincident(g14,g15)
    c: Coincident(g15,g16)
    c: Coincident(g0,g16)
    c: Coincident(g17,g18)
    c: Coincident(g18,g19)
    c: Coincident(g19,g20)
    c: Coincident(g20,g21)
    c: Coincident(g21,g22)
    c: Coincident(g22,g23)
    c: Coincident(g23,g24)
    c: Coincident(g24,g25)
    c: Coincident(g25,g26)
    c: Coincident(g26,g27)
    c: Coincident(g27,g28)
    c: Coincident(g28,g17)
    c: Parallel(g23,g29)
    c: Coincident(g29,g30)
    c: Coincident(g30,g31)
    c: Coincident(g31,g32)
    c: Coincident(g32,g33)
    c: Coincident(g33,g34)
    c: Coincident(g34,g35)
    c: Coincident(g35,g36)
    c: Coincident(g36,g37)
    c: Coincident(g37,g29)
    c: Coincident(g38,g39)
    c: Coincident(g39,g40)
    c: Coincident(g40,g41)
    c: Coincident(g41,g42)
    c: Coincident(g42,g43)
    c: Coincident(g43,g44)
    c: Coincident(g44,g45)
    c: Coincident(g45,g46)
    c: Coincident(g46,g47)
    c: Coincident(g47,g48)
    c: Coincident(g48,g49)
    c: Coincident(g49,g38)
    c: Parallel(g38,g32)
    c: Coincident(g50,g51)
    c: Coincident(g51,g52)
    c: Coincident(g52,g53)
    c: Coincident(g53,g54)
    c: Coincident(g54,g55)
    c: Coincident(g55,g56)
    c: Coincident(g56,g57)
    c: Coincident(g57,g58)
    c: Coincident(g58,g59)
    c: Coincident(g59,g60)
    c: Coincident(g60,g61)
    c: Coincident(g61,g50)
    c: Parallel(g45,g50)
    c: Coincident(g62,g63)
    c: Coincident(g63,g64)
    c: Coincident(g64,g65)
    c: Vertical(g65)
    c: Coincident(g65,g66)
    c: Coincident(g66,g67)
    c: Coincident(g67,g68)
    c: Coincident(g68,g62)
    c: Parallel(g54,g62)
FEATURE [PartDesign::Pocket] Pocket030
  BaseFeature = -> Pocket011
  Direction = (0,0,1)
  Length = 15
  Length2 = 5
  Profile = -> Sketch053
  ReferenceAxis = -> Sketch053 [N_Axis]
  Refine = true
  Suppressed = false
  Type = 0
FEATURE [Sketcher::SketchObject] Sketch054
  ArcFitTolerance = 1e-06
  FullyConstrained = false
  MakeInternals = false
  Placement = pos=(600,0,-600) rot=(0,0,1;0rad)
  sketch-geometry (123):
    g0: BSplineCurve PolesCount=61 KnotsCount=61 Degree=3 IsPeriodic=1
    g1-g61: Circle [constr] x61 (B-spline internal-alignment scaffolding for g0; pole/knot coordinates omitted)
    g62-g122: GeomPoint [constr] x61 (B-spline internal-alignment scaffolding for g0; pole/knot coordinates omitted)
  constraints (123):
    c: InternalAlignment(g1,g0)
    c: Weight(g1) = 1
    c: InternalAlignment(g2,g0)
    c: Equal(g2,g1)
    c: InternalAlignment(g3,g0)
    c: Equal(g3,g1)
    c: InternalAlignment(g4,g0)
    c: Equal(g4,g1)
    c: InternalAlignment(g5,g0)
    c: Equal(g5,g1)
    c: InternalAlignment(g6,g0)
    c: Equal(g6,g1)
    c: InternalAlignment(g7,g0)
    c: Equal(g7,g1)
    c: InternalAlignment(g8,g0)
    c: Equal(g8,g1)
    c: InternalAlignment(g9,g0)
    c: Equal(g9,g1)
    c: InternalAlignment(g10,g0)
    c: Equal(g10,g1)
    c: InternalAlignment(g11,g0)
    c: Equal(g11,g1)
    c: InternalAlignment(g12,g0)
    c: Equal(g12,g1)
    c: InternalAlignment(g13,g0)
    c: Equal(g13,g1)
    c: InternalAlignment(g14,g0)
    c: Equal(g14,g1)
    c: InternalAlignment(g15,g0)
    c: Equal(g15,g1)
    c: InternalAlignment(g16,g0)
    c: Equal(g16,g1)
    c: InternalAlignment(g17,g0)
    c: Equal(g17,g1)
    c: InternalAlignment(g18,g0)
    c: Equal(g18,g1)
    c: InternalAlignment(g19,g0)
    c: Equal(g19,g1)
    c: InternalAlignment(g20,g0)
    c: Equal(g20,g1)
    c: InternalAlignment(g21,g0)
    c: Equal(g21,g1)
    c: InternalAlignment(g22,g0)
    c: Equal(g22,g1)
    c: InternalAlignment(g23,g0)
    c: Equal(g23,g1)
    c: InternalAlignment(g24,g0)
    c: Equal(g24,g1)
    c: InternalAlignment(g25,g0)
    c: Equal(g25,g1)
    c: InternalAlignment(g26,g0)
    c: Equal(g26,g1)
    c: InternalAlignment(g27,g0)
    c: Equal(g27,g1)
    c: InternalAlignment(g28,g0)
    c: Equal(g28,g1)
    c: InternalAlignment(g29,g0)
    c: Equal(g29,g1)
    c: InternalAlignment(g30,g0)
    c: Equal(g30,g1)
    c: InternalAlignment(g31,g0)
    c: Equal(g31,g1)
    c: InternalAlignment(g32,g0)
    c: Equal(g32,g1)
    c: InternalAlignment(g33,g0)
    c: Equal(g33,g1)
    c: InternalAlignment(g34,g0)
    c: Equal(g34,g1)
    c: InternalAlignment(g35,g0)
    c: Equal(g35,g1)
    c: InternalAlignment(g36,g0)
    c: Equal(g36,g1)
    c: InternalAlignment(g37,g0)
    c: Equal(g37,g1)
    c: InternalAlignment(g38,g0)
    c: Equal(g38,g1)
    c: InternalAlignment(g39,g0)
    c: Equal(g39,g1)
    c: InternalAlignment(g40,g0)
    c: Equal(g40,g1)
    c: InternalAlignment(g41,g0)
    c: Equal(g41,g1)
    c: InternalAlignment(g42,g0)
    c: Equal(g42,g1)
    c: InternalAlignment(g43,g0)
    c: Equal(g43,g1)
    c: InternalAlignment(g44,g0)
    c: Equal(g44,g1)
    c: InternalAlignment(g45,g0)
    c: Equal(g45,g1)
    c: InternalAlignment(g46,g0)
    c: Equal(g46,g1)
    c: InternalAlignment(g47,g0)
    c: Equal(g47,g1)
    c: InternalAlignment(g48,g0)
    c: Equal(g48,g1)
    c: InternalAlignment(g49,g0)
    c: Equal(g49,g1)
    c: InternalAlignment(g50,g0)
    c: Equal(g50,g1)
    c: InternalAlignment(g51,g0)
    c: Equal(g51,g1)
    c: InternalAlignment(g52,g0)
    c: Equal(g52,g1)
    c: InternalAlignment(g53,g0)
    c: Equal(g53,g1)
    c: InternalAlignment(g54,g0)
    c: Equal(g54,g1)
    c: InternalAlignment(g55,g0)
    c: Equal(g55,g1)
    c: InternalAlignment(g56,g0)
    c: Equal(g56,g1)
    c: InternalAlignment(g57,g0)
    c: Equal(g57,g1)
    c: InternalAlignment(g58,g0)
    c: Equal(g58,g1)
    c: InternalAlignment(g59,g0)
    c: Equal(g59,g1)
    c: InternalAlignment(g60,g0)
    c: Equal(g60,g1)
    c: InternalAlignment(g61,g0)
    c: Equal(g61,g1)
    c: InternalAlignment(g62-g122 -> g0) x61
FEATURE [Sketcher::SketchObject] Sketch055
  ArcFitTolerance = 1e-06
  FullyConstrained = false
  MakeInternals = false
  sketch-geometry (123):
    g0: BSplineCurve PolesCount=61 KnotsCount=61 Degree=3 IsPeriodic=1
    g1-g61: Circle [constr] x61 (B-spline internal-alignment scaffolding for g0; pole/knot coordinates omitted)
    g62-g122: GeomPoint [constr] x61 (B-spline internal-alignment scaffolding for g0; pole/knot coordinates omitted)
  constraints (123):
    c: InternalAlignment(g1,g0)
    c: Weight(g1) = 1
    c: InternalAlignment(g2,g0)
    c: Equal(g2,g1)
    c: InternalAlignment(g3,g0)
    c: Equal(g3,g1)
    c: InternalAlignment(g4,g0)
    c: Equal(g4,g1)
    c: InternalAlignment(g5,g0)
    c: Equal(g5,g1)
    c: InternalAlignment(g6,g0)
    c: Equal(g6,g1)
    c: InternalAlignment(g7,g0)
    c: Equal(g7,g1)
    c: InternalAlignment(g8,g0)
    c: Equal(g8,g1)
    c: InternalAlignment(g9,g0)
    c: Equal(g9,g1)
    c: InternalAlignment(g10,g0)
    c: Equal(g10,g1)
    c: InternalAlignment(g11,g0)
    c: Equal(g11,g1)
    c: InternalAlignment(g12,g0)
    c: Equal(g12,g1)
    c: InternalAlignment(g13,g0)
    c: Equal(g13,g1)
    c: InternalAlignment(g14,g0)
    c: Equal(g14,g1)
    c: InternalAlignment(g15,g0)
    c: Equal(g15,g1)
    c: InternalAlignment(g16,g0)
    c: Equal(g16,g1)
    c: InternalAlignment(g17,g0)
    c: Equal(g17,g1)
    c: InternalAlignment(g18,g0)
    c: Equal(g18,g1)
    c: InternalAlignment(g19,g0)
    c: Equal(g19,g1)
    c: InternalAlignment(g20,g0)
    c: Equal(g20,g1)
    c: InternalAlignment(g21,g0)
    c: Equal(g21,g1)
    c: InternalAlignment(g22,g0)
    c: Equal(g22,g1)
    c: InternalAlignment(g23,g0)
    c: Equal(g23,g1)
    c: InternalAlignment(g24,g0)
    c: Equal(g24,g1)
    c: InternalAlignment(g25,g0)
    c: Equal(g25,g1)
    c: InternalAlignment(g26,g0)
    c: Equal(g26,g1)
    c: InternalAlignment(g27,g0)
    c: Equal(g27,g1)
    c: InternalAlignment(g28,g0)
    c: Equal(g28,g1)
    c: InternalAlignment(g29,g0)
    c: Equal(g29,g1)
    c: InternalAlignment(g30,g0)
    c: Equal(g30,g1)
    c: InternalAlignment(g31,g0)
    c: Equal(g31,g1)
    c: InternalAlignment(g32,g0)
    c: Equal(g32,g1)
    c: InternalAlignment(g33,g0)
    c: Equal(g33,g1)
    c: InternalAlignment(g34,g0)
    c: Equal(g34,g1)
    c: InternalAlignment(g35,g0)
    c: Equal(g35,g1)
    c: InternalAlignment(g36,g0)
    c: Equal(g36,g1)
    c: InternalAlignment(g37,g0)
    c: Equal(g37,g1)
    c: InternalAlignment(g38,g0)
    c: Equal(g38,g1)
    c: InternalAlignment(g39,g0)
    c: Equal(g39,g1)
    c: InternalAlignment(g40,g0)
    c: Equal(g40,g1)
    c: InternalAlignment(g41,g0)
    c: Equal(g41,g1)
    c: InternalAlignment(g42,g0)
    c: Equal(g42,g1)
    c: InternalAlignment(g43,g0)
    c: Equal(g43,g1)
    c: InternalAlignment(g44,g0)
    c: Equal(g44,g1)
    c: InternalAlignment(g45,g0)
    c: Equal(g45,g1)
    c: InternalAlignment(g46,g0)
    c: Equal(g46,g1)
    c: InternalAlignment(g47,g0)
    c: Equal(g47,g1)
    c: InternalAlignment(g48,g0)
    c: Equal(g48,g1)
    c: InternalAlignment(g49,g0)
    c: Equal(g49,g1)
    c: InternalAlignment(g50,g0)
    c: Equal(g50,g1)
    c: InternalAlignment(g51,g0)
    c: Equal(g51,g1)
    c: InternalAlignment(g52,g0)
    c: Equal(g52,g1)
    c: InternalAlignment(g53,g0)
    c: Equal(g53,g1)
    c: InternalAlignment(g54,g0)
    c: Equal(g54,g1)
    c: InternalAlignment(g55,g0)
    c: Equal(g55,g1)
    c: InternalAlignment(g56,g0)
    c: Equal(g56,g1)
    c: InternalAlignment(g57,g0)
    c: Equal(g57,g1)
    c: InternalAlignment(g58,g0)
    c: Equal(g58,g1)
    c: InternalAlignment(g59,g0)
    c: Equal(g59,g1)
    c: InternalAlignment(g60,g0)
    c: Equal(g60,g1)
    c: InternalAlignment(g61,g0)
    c: Equal(g61,g1)
    c: InternalAlignment(g62-g122 -> g0) x61
FEATURE [PartDesign::AdditiveLoft] AdditiveLoft008
  Closed = false
  Profile = -> Sketch055
  Refine = true
  Ruled = false
  Sections = -> [Sketch054]
  Suppressed = false
FEATURE [PartDesign::Plane] DatumPlane011
  AttachmentOffset = pos=(0,0,0) rot=(0,-1,0;0.785398rad)
  AttachmentSupport = -> [AdditiveLoft008]
  Length = 624.615
  MapMode = 5
  Placement = pos=(0,0,0) rot=(0,-1,0;0.785398rad)
  ResizeMode = 0
  Width = 84.3586
FEATURE [Sketcher::SketchObject] Sketch056
  ArcFitTolerance = 1e-06
  AttachmentSupport = -> [DatumPlane011]
  FullyConstrained = false
  MakeInternals = false
  MapMode = 5
  Placement = pos=(0,0,0) rot=(0,-1,0;0.785398rad)
  sketch-geometry (1):
    g0: Circle CenterX=28.3343 CenterY=4.75298 CenterZ=0 NormalX=0 NormalY=0 NormalZ=1 AngleXU=0 Radius=4.1
  constraints (1):
    c: Diameter(g0) = 8.2
FEATURE [PartDesign::Pocket] Pocket031
  BaseFeature = -> AdditiveLoft008
  Direction = (0.707107,0,-0.707107)
  Length = 1000
  Length2 = 5
  Profile = -> Sketch056
  ReferenceAxis = -> Sketch056 [N_Axis]
  Refine = true
  Suppressed = false
  Type = 0
FEATURE [Sketcher::SketchObject] Sketch057
  ArcFitTolerance = 1e-06
  AttachmentSupport = -> [Pocket031]
  FullyConstrained = false
  MakeInternals = false
  MapMode = 5
  sketch-geometry (4):
    g0: LineSegment StartX=-34.6749 StartY=103.814 StartZ=0 EndX=-34.6749 EndY=-124.102 EndZ=0
    g1: LineSegment StartX=-34.6749 StartY=-124.102 StartZ=0 EndX=635.695 EndY=-124.102 EndZ=0
    g2: LineSegment StartX=635.695 StartY=-124.102 StartZ=0 EndX=635.695 EndY=103.814 EndZ=0
    g3: LineSegment StartX=635.695 StartY=103.814 StartZ=0 EndX=-34.6749 EndY=103.814 EndZ=0
  constraints (8):
    c: Coincident(g0,g1)
    c: Coincident(g1,g2)
    c: Coincident(g2,g3)
    c: Coincident(g3,g0)
    c: Vertical(g0)
    c: Vertical(g2)
    c: Horizontal(g1)
    c: Horizontal(g3)
FEATURE [PartDesign::Pocket] Pocket032
  BaseFeature = -> Pocket031
  Direction = (0,0,-1)
  Length = 200
  Length2 = 5
  Profile = -> Sketch057
  ReferenceAxis = -> Sketch057 [N_Axis]
  Refine = true
  Suppressed = false
  Type = 0
FEATURE [Sketcher::SketchObject] Sketch058
  ArcFitTolerance = 1e-06
  AttachmentSupport = -> [Pocket032]
  FullyConstrained = false
  MakeInternals = false
  MapMode = 5
  Placement = pos=(0,0,-600) rot=(1,0,0;3.14159rad)
  sketch-geometry (4):
    g0: LineSegment StartX=120.377 StartY=171.986 StartZ=0 EndX=120.377 EndY=-157.538 EndZ=0
    g1: LineSegment StartX=120.377 StartY=-157.538 StartZ=0 EndX=998.806 EndY=-157.538 EndZ=0
    g2: LineSegment StartX=998.806 StartY=-157.538 StartZ=0 EndX=998.806 EndY=171.986 EndZ=0
    g3: LineSegment StartX=998.806 StartY=171.986 StartZ=0 EndX=120.377 EndY=171.986 EndZ=0
  constraints (8):
    c: Coincident(g0,g1)
    c: Coincident(g1,g2)
    c: Coincident(g2,g3)
    c: Coincident(g3,g0)
    c: Vertical(g0)
    c: Vertical(g2)
    c: Horizontal(g1)
    c: Horizontal(g3)
FEATURE [PartDesign::Pocket] Pocket033
  BaseFeature = -> Pocket032
  Direction = (0,0,1)
  Length = 390
  Length2 = 5
  Profile = -> Sketch058
  ReferenceAxis = -> Sketch058 [N_Axis]
  Refine = true
  Suppressed = false
  Type = 0
FEATURE [Sketcher::SketchObject] Sketch059
  ArcFitTolerance = 1e-06
  AttachmentSupport = -> [Pocket033]
  FullyConstrained = false
  MakeInternals = false
  MapMode = 5
  Placement = pos=(0,0,-210) rot=(1,0,0;3.14159rad)
  sketch-geometry (69):
    g0: LineSegment StartX=232.935 StartY=-13.2277 StartZ=0 EndX=232.935 EndY=3.96212 EndZ=0
    g1: LineSegment StartX=232.935 StartY=3.96212 StartZ=0 EndX=230.333 EndY=3.82301 EndZ=0
    g2: LineSegment StartX=230.333 StartY=3.82301 StartZ=0 EndX=226.374 EndY=3.53509 EndZ=0
    g3: LineSegment StartX=226.374 StartY=3.53509 StartZ=0 EndX=223.207 EndY=3.1032 EndZ=0
    g4: LineSegment StartX=223.207 StartY=3.1032 StartZ=0 EndX=219.176 EndY=2.45538 EndZ=0
    g5: LineSegment StartX=219.176 StartY=2.45538 StartZ=0 EndX=215.793 EndY=1.80756 EndZ=0
    g6: LineSegment StartX=215.793 StartY=1.80756 StartZ=0 EndX=213.633 EndY=1.08775 EndZ=0
    g7: LineSegment StartX=213.633 StartY=1.08775 StartZ=0 EndX=212.553 EndY=0 EndZ=0
    g8: LineSegment StartX=212.553 StartY=0 StartZ=0 EndX=213.273 EndY=-1.86345 EndZ=0
    g9: LineSegment StartX=213.273 StartY=-1.86345 StartZ=0 EndX=214.569 EndY=-3.37504 EndZ=0
    g10: LineSegment StartX=214.569 StartY=-3.37504 StartZ=0 EndX=216.512 EndY=-4.88663 EndZ=0
    g11: LineSegment StartX=216.512 StartY=-4.88663 StartZ=0 EndX=218.888 EndY=-6.61416 EndZ=0
    g12: LineSegment StartX=218.888 StartY=-6.61416 StartZ=0 EndX=221.623 EndY=-8.26971 EndZ=0
    g13: LineSegment StartX=221.623 StartY=-8.26971 StartZ=0 EndX=224.862 EndY=-9.85328 EndZ=0
    g14: LineSegment StartX=224.862 StartY=-9.85328 StartZ=0 EndX=227.597 EndY=-11.1489 EndZ=0
    g15: LineSegment StartX=227.597 StartY=-11.1489 StartZ=0 EndX=230.621 EndY=-12.3726 EndZ=0
    g16: LineSegment StartX=230.621 StartY=-12.3726 StartZ=0 EndX=232.935 EndY=-13.2277 EndZ=0
    g17: LineSegment StartX=529.448 StartY=-5.42158 StartZ=0 EndX=529.373 EndY=-2.77124 EndZ=0
    g18: LineSegment StartX=529.373 StartY=-2.77124 StartZ=0 EndX=518.644 EndY=-2.45257 EndZ=0
    g19: LineSegment StartX=518.644 StartY=-2.45257 StartZ=0 EndX=507.384 EndY=-2.45257 EndZ=0
    g20: LineSegment StartX=507.384 StartY=-2.45257 StartZ=0 EndX=492.088 EndY=-2.1339 EndZ=0
    g21: LineSegment StartX=492.088 StartY=-2.1339 StartZ=0 EndX=474.647 EndY=-1.51705 EndZ=0
    g22: LineSegment StartX=474.647 StartY=-1.51705 StartZ=0 EndX=468.174 EndY=-1.28599 EndZ=0
    g23: LineSegment StartX=468.174 StartY=-1.28599 StartZ=0 EndX=476.745 EndY=-13.3358 EndZ=0
    g24: LineSegment StartX=476.745 StartY=-13.3358 StartZ=0 EndX=493.617 EndY=-10.9006 EndZ=0
    g25: LineSegment StartX=493.617 StartY=-10.9006 StartZ=0 EndX=505.184 EndY=-9.07429 EndZ=0
    g26: LineSegment StartX=505.184 StartY=-9.07429 StartZ=0 EndX=516.49 EndY=-7.42187 EndZ=0
    g27: LineSegment StartX=516.49 StartY=-7.42187 StartZ=0 EndX=524.752 EndY=-6.2043 EndZ=0
    g28: LineSegment StartX=524.752 StartY=-6.2043 StartZ=0 EndX=529.448 EndY=-5.42158 EndZ=0
    g29: LineSegment StartX=472.33 StartY=-14.3284 StartZ=0 EndX=463.007 EndY=-1.22045 EndZ=0
    g30: LineSegment StartX=463.007 StartY=-1.22045 StartZ=0 EndX=436.979 EndY=-0.55496 EndZ=0
    g31: LineSegment StartX=436.979 StartY=-0.55496 StartZ=0 EndX=421.281 EndY=-0.0939564 EndZ=0
    g32: LineSegment StartX=421.281 StartY=-0.0939564 StartZ=0 EndX=408.215 EndY=-21.1936 EndZ=0
    g33: LineSegment StartX=408.215 StartY=-21.1936 StartZ=0 EndX=422.281 EndY=-20.1232 EndZ=0
    g34: LineSegment StartX=422.281 StartY=-20.1232 StartZ=0 EndX=436.37 EndY=-18.8185 EndZ=0
    g35: LineSegment StartX=436.37 StartY=-18.8185 StartZ=0 EndX=450.546 EndY=-17.0789 EndZ=0
    g36: LineSegment StartX=450.546 StartY=-17.0789 StartZ=0 EndX=464.722 EndY=-15.5133 EndZ=0
    g37: LineSegment StartX=464.722 StartY=-15.5133 StartZ=0 EndX=472.33 EndY=-14.3284 EndZ=0
    g38: LineSegment StartX=402.538 StartY=-21.4405 StartZ=0 EndX=415.866 EndY=0.0815263 EndZ=0
    g39: LineSegment StartX=415.866 StartY=0.0815263 StartZ=0 EndX=393.968 EndY=0.858652 EndZ=0
    g40: LineSegment StartX=393.968 StartY=0.858652 StartZ=0 EndX=379.742 EndY=1.33409 EndZ=0
    g41: LineSegment StartX=379.742 StartY=1.33409 StartZ=0 EndX=367.191 EndY=1.7451 EndZ=0
    g42: LineSegment StartX=367.191 StartY=1.7451 StartZ=0 EndX=355.656 EndY=2.10097 EndZ=0
    g43: LineSegment StartX=355.656 StartY=2.10097 StartZ=0 EndX=344.334 EndY=2.58371 EndZ=0
    g44: LineSegment StartX=344.334 StartY=2.58371 StartZ=0 EndX=336.607 EndY=2.93983 EndZ=0
    g45: LineSegment StartX=336.607 StartY=2.93983 StartZ=0 EndX=353.364 EndY=-23.826 EndZ=0
    g46: LineSegment StartX=353.364 StartY=-23.826 StartZ=0 EndX=368.687 EndY=-23.2476 EndZ=0
    g47: LineSegment StartX=368.687 StartY=-23.2476 StartZ=0 EndX=385.349 EndY=-22.4641 EndZ=0
    g48: LineSegment StartX=385.349 StartY=-22.4641 StartZ=0 EndX=397.881 EndY=-21.6807 EndZ=0
    g49: LineSegment StartX=397.881 StartY=-21.6807 StartZ=0 EndX=402.538 EndY=-21.4405 EndZ=0
    g50: LineSegment StartX=347.682 StartY=-24.0752 StartZ=0 EndX=330.602 EndY=3.20634 EndZ=0
    g51: LineSegment StartX=330.602 StartY=3.20634 StartZ=0 EndX=312.355 EndY=3.43929 EndZ=0
    g52: LineSegment StartX=312.355 StartY=3.43929 StartZ=0 EndX=297.314 EndY=3.73057 EndZ=0
    g53: LineSegment StartX=297.314 StartY=3.73057 StartZ=0 EndX=286.58 EndY=4.11889 EndZ=0
    g54: LineSegment StartX=286.58 StartY=4.11889 StartZ=0 EndX=271.742 EndY=-21.5893 EndZ=0
    g55: LineSegment StartX=271.742 StartY=-21.5893 StartZ=0 EndX=279.89 EndY=-22.1672 EndZ=0
    g56: LineSegment StartX=279.89 StartY=-22.1672 StartZ=0 EndX=293.298 EndY=-23.0415 EndZ=0
    g57: LineSegment StartX=293.298 StartY=-23.0415 StartZ=0 EndX=308.688 EndY=-23.8574 EndZ=0
    g58: LineSegment StartX=308.688 StartY=-23.8574 StartZ=0 EndX=319.648 EndY=-24.0905 EndZ=0
    g59: LineSegment StartX=319.648 StartY=-24.0905 StartZ=0 EndX=332.415 EndY=-24.1486 EndZ=0
    g60: LineSegment StartX=332.415 StartY=-24.1486 StartZ=0 EndX=341.218 EndY=-24.0902 EndZ=0
    g61: LineSegment StartX=341.218 StartY=-24.0902 StartZ=0 EndX=347.682 EndY=-24.0752 EndZ=0
    g62: LineSegment StartX=281.696 StartY=4.48378 StartZ=0 EndX=267.107 EndY=-20.7944 EndZ=0
    g63: LineSegment StartX=267.107 StartY=-20.7944 StartZ=0 EndX=262.676 EndY=-20.2115 EndZ=0
    g64: LineSegment StartX=262.676 StartY=-20.2115 StartZ=0 EndX=258.595 EndY=-19.7452 EndZ=0
    g65: LineSegment StartX=258.595 StartY=-19.7452 StartZ=0 EndX=258.595 EndY=4.97283 EndZ=0
    g66: LineSegment StartX=258.595 StartY=4.97283 StartZ=0 EndX=267.689 EndY=4.85636 EndZ=0
    g67: LineSegment StartX=267.689 StartY=4.85636 StartZ=0 EndX=275.21 EndY=4.73986 EndZ=0
    g68: LineSegment StartX=275.21 StartY=4.73986 StartZ=0 EndX=281.696 EndY=4.48378 EndZ=0
  constraints (76):
    c: Vertical(g0)
    c: Coincident(g0,g1)
    c: Coincident(g1,g2)
    c: Coincident(g2,g3)
    c: Coincident(g3,g4)
    c: Coincident(g4,g5)
    c: Coincident(g5,g6)
    c: Coincident(g6,g7)
    c: PointOnObject(g7,g-1)
    c: Coincident(g7,g8)
    c: Coincident(g8,g9)
    c: Coincident(g9,g10)
    c: Coincident(g10,g11)
    c: Coincident(g11,g12)
    c: Coincident(g12,g13)
    c: Coincident(g13,g14)
    c: Coincident(g14,g15)
    c: Coincident(g15,g16)
    c: Coincident(g0,g16)
    c: Coincident(g17,g18)
    c: Coincident(g18,g19)
    c: Coincident(g19,g20)
    c: Coincident(g20,g21)
    c: Coincident(g21,g22)
    c: Coincident(g22,g23)
    c: Coincident(g23,g24)
    c: Coincident(g24,g25)
    c: Coincident(g25,g26)
    c: Coincident(g26,g27)
    c: Coincident(g27,g28)
    c: Coincident(g28,g17)
    c: Parallel(g23,g29)
    c: Coincident(g29,g30)
    c: Coincident(g30,g31)
    c: Coincident(g31,g32)
    c: Coincident(g32,g33)
    c: Coincident(g33,g34)
    c: Coincident(g34,g35)
    c: Coincident(g35,g36)
    c: Coincident(g36,g37)
    c: Coincident(g37,g29)
    c: Coincident(g38,g39)
    c: Coincident(g39,g40)
    c: Coincident(g40,g41)
    c: Coincident(g41,g42)
    c: Coincident(g42,g43)
    c: Coincident(g43,g44)
    c: Coincident(g44,g45)
    c: Coincident(g45,g46)
    c: Coincident(g46,g47)
    c: Coincident(g47,g48)
    c: Coincident(g48,g49)
    c: Coincident(g49,g38)
    c: Parallel(g38,g32)
    c: Coincident(g50,g51)
    c: Coincident(g51,g52)
    c: Coincident(g52,g53)
    c: Coincident(g53,g54)
    c: Coincident(g54,g55)
    c: Coincident(g55,g56)
    c: Coincident(g56,g57)
    c: Coincident(g57,g58)
    c: Coincident(g58,g59)
    c: Coincident(g59,g60)
    c: Coincident(g60,g61)
    c: Coincident(g61,g50)
    c: Parallel(g45,g50)
    c: Coincident(g62,g63)
    c: Coincident(g63,g64)
    c: Coincident(g64,g65)
    c: Vertical(g65)
    c: Coincident(g65,g66)
    c: Coincident(g66,g67)
    c: Coincident(g67,g68)
    c: Coincident(g68,g62)
    c: Parallel(g54,g62)
FEATURE [PartDesign::Pocket] Pocket034
  BaseFeature = -> Pocket033
  Direction = (0,0,1)
  Length = 15
  Length2 = 5
  Profile = -> Sketch059
  ReferenceAxis = -> Sketch059 [N_Axis]
  Refine = true
  Suppressed = false
  Type = 0
FEATURE [Sketcher::SketchObject] Sketch060
  ArcFitTolerance = 1e-06
  AttachmentSupport = -> [Pocket030]
  FullyConstrained = false
  MakeInternals = false
  MapMode = 5
  Placement = pos=(0,0,-210) rot=(1,0,0;3.14159rad)
  sketch-geometry (4):
    g0: LineSegment StartX=478 StartY=13.3545 StartZ=0 EndX=478 EndY=-28.4769 EndZ=0
    g1: LineSegment StartX=478 StartY=-28.4769 StartZ=0 EndX=652.571 EndY=-28.4769 EndZ=0
    g2: LineSegment StartX=652.571 StartY=-28.4769 StartZ=0 EndX=652.571 EndY=13.3545 EndZ=0
    g3: LineSegment StartX=652.571 StartY=13.3545 StartZ=0 EndX=478 EndY=13.3545 EndZ=0
  constraints (9):
    c: Coincident(g0,g1)
    c: Coincident(g1,g2)
    c: Coincident(g2,g3)
    c: Coincident(g3,g0)
    c: Vertical(g0)
    c: Vertical(g2)
    c: Horizontal(g1)
    c: Horizontal(g3)
    c: DistanceX(g-1,g0) = 478
FEATURE [Sketcher::SketchObject] Sketch061
  ArcFitTolerance = 1e-06
  AttachmentSupport = -> [Pocket034]
  FullyConstrained = false
  MakeInternals = false
  MapMode = 5
  Placement = pos=(0,0,-210) rot=(1,0,0;3.14159rad)
  sketch-geometry (4):
    g0: LineSegment StartX=151.191 StartY=62.2487 StartZ=0 EndX=151.191 EndY=-99.9829 EndZ=0
    g1: LineSegment StartX=151.191 StartY=-99.9829 StartZ=0 EndX=478 EndY=-99.9829 EndZ=0
    g2: LineSegment StartX=478 StartY=-99.9829 StartZ=0 EndX=478 EndY=62.2487 EndZ=0
    g3: LineSegment StartX=478 StartY=62.2487 StartZ=0 EndX=151.191 EndY=62.2487 EndZ=0
  constraints (9):
    c: Coincident(g0,g1)
    c: Coincident(g1,g2)
    c: Coincident(g2,g3)
    c: Coincident(g3,g0)
    c: Vertical(g0)
    c: Vertical(g2)
    c: Horizontal(g1)
    c: Horizontal(g3)
    c: DistanceX(g-1,g2) = 478
FEATURE [PartDesign::Pocket] Pocket035
  BaseFeature = -> Pocket034
  Direction = (0,0,1)
  Length = 15
  Length2 = 5
  Profile = -> Sketch061
  ReferenceAxis = -> Sketch061 [N_Axis]
  Refine = true
  Suppressed = false
  Type = 0
FEATURE [PartDesign::Body] Body008
  AllowCompound = false
  Group = -> [Sketch055,Sketch054,AdditiveLoft008,DatumPlane011,Sketch056,Pocket031,Sketch057,Pocket032,Sketch058,Pocket033,Sketch059,Pocket034,Sketch061,Pocket035]
  Origin = -> Origin008
  Placement = pos=(0,0,-100) rot=(0,0,1;0rad)
  Tip = -> Pocket035
FEATURE [PartDesign::Pocket] Pocket036
  BaseFeature = -> Pocket030
  Direction = (0,0,1)
  Length = 15
  Length2 = 5
  Profile = -> Sketch060
  ReferenceAxis = -> Sketch060 [N_Axis]
  Refine = true
  Suppressed = false
  Type = 0
FEATURE [PartDesign::Body] Body002
  AllowCompound = false
  Group = -> [Sketch007,Sketch006,AdditiveLoft002,DatumPlane002,Sketch008,Pocket002,Sketch024,Pocket010,Sketch025,Pocket011,Sketch053,Pocket030,Sketch060,Pocket036]
  Origin = -> Origin002
  Placement = pos=(0,0,-100) rot=(0,0,1;0rad)
  Tip = -> Pocket036
FEATURE [Sketcher::SketchObject] Sketch062
  ArcFitTolerance = 1e-06
  AttachmentSupport = -> [Pocket009]
  FullyConstrained = false
  MakeInternals = false
  MapMode = 5
  Placement = pos=(0,0,-110) rot=(1,0,0;3.14159rad)
  sketch-geometry (64):
    g0: LineSegment StartX=131.615 StartY=-13.8563 StartZ=0 EndX=131.615 EndY=4.74903 EndZ=0
    g1: LineSegment StartX=131.615 StartY=4.74903 StartZ=0 EndX=126.762 EndY=4.05077 EndZ=0
    g2: LineSegment StartX=126.762 StartY=4.05077 StartZ=0 EndX=121.398 EndY=3.23596 EndZ=0
    g3: LineSegment StartX=121.398 StartY=3.23596 StartZ=0 EndX=117.609 EndY=2.65394 EndZ=0
    g4: LineSegment StartX=117.609 StartY=2.65394 StartZ=0 EndX=114.461 EndY=1.60538 EndZ=0
    g5: LineSegment StartX=114.461 StartY=1.60538 StartZ=0 EndX=112.828 EndY=0.731336 EndZ=0
    g6: LineSegment StartX=112.828 StartY=0.731336 StartZ=0 EndX=112.128 EndY=0 EndZ=0
    g7: LineSegment StartX=112.128 StartY=0 StartZ=0 EndX=112.303 EndY=-0.95915 EndZ=0
    g8: LineSegment StartX=112.303 StartY=-0.95915 StartZ=0 EndX=113.119 EndY=-2.30019 EndZ=0
    g9: LineSegment StartX=113.119 StartY=-2.30019 StartZ=0 EndX=115.159 EndY=-4.3994 EndZ=0
    g10: LineSegment StartX=115.159 StartY=-4.3994 StartZ=0 EndX=118.073 EndY=-6.84862 EndZ=0
    g11: LineSegment StartX=118.073 StartY=-6.84862 StartZ=0 EndX=121.395 EndY=-8.88986 EndZ=0
    g12: LineSegment StartX=121.395 StartY=-8.88986 StartZ=0 EndX=125.243 EndY=-10.8146 EndZ=0
    g13: LineSegment StartX=125.243 StartY=-10.8146 StartZ=0 EndX=129.381 EndY=-12.9144 EndZ=0
    g14: LineSegment StartX=129.381 StartY=-12.9144 StartZ=0 EndX=131.615 EndY=-13.8563 EndZ=0
    g15: LineSegment StartX=456.728 StartY=-6.97805 StartZ=0 EndX=456.728 EndY=-2.77376 EndZ=0
    g16: LineSegment StartX=456.728 StartY=-2.77376 StartZ=0 EndX=444.473 EndY=-2.77376 EndZ=0
    g17: LineSegment StartX=444.473 StartY=-2.77376 StartZ=0 EndX=430.721 EndY=-2.53251 EndZ=0
    g18: LineSegment StartX=430.721 StartY=-2.53251 StartZ=0 EndX=419.576 EndY=-2.29126 EndZ=0
    g19: LineSegment StartX=419.576 StartY=-2.29126 StartZ=0 EndX=405.248 EndY=-1.99854 EndZ=0
    g20: LineSegment StartX=405.248 StartY=-1.99854 StartZ=0 EndX=391.498 EndY=-1.51681 EndZ=0
    g21: LineSegment StartX=391.498 StartY=-1.51681 StartZ=0 EndX=401.723 EndY=-15.753 EndZ=0
    g22: LineSegment StartX=401.723 StartY=-15.753 StartZ=0 EndX=417.216 EndY=-13.54 EndZ=0
    g23: LineSegment StartX=417.216 StartY=-13.54 StartZ=0 EndX=432.077 EndY=-10.9345 EndZ=0
    g24: LineSegment StartX=432.077 StartY=-10.9345 StartZ=0 EndX=447.999 EndY=-8.4738 EndZ=0
    g25: LineSegment StartX=447.999 StartY=-8.4738 StartZ=0 EndX=456.728 EndY=-6.97805 EndZ=0
    g26: LineSegment StartX=397.242 StartY=-16.8147 StartZ=0 EndX=385.617 EndY=-0.630676 EndZ=0
    g27: LineSegment StartX=385.617 StartY=-0.630676 StartZ=0 EndX=375.298 EndY=-0.398599 EndZ=0
    g28: LineSegment StartX=375.298 StartY=-0.398599 StartZ=0 EndX=363.461 EndY=-0.159949 EndZ=0
    g29: LineSegment StartX=363.461 StartY=-0.159949 StartZ=0 EndX=353.629 EndY=0.221889 EndZ=0
    g30: LineSegment StartX=353.629 StartY=0.221889 StartZ=0 EndX=343.415 EndY=0.603728 EndZ=0
    g31: LineSegment StartX=343.415 StartY=0.603728 StartZ=0 EndX=335.141 EndY=0.494975 EndZ=0
    g32: LineSegment StartX=335.141 StartY=0.494975 StartZ=0 EndX=321.314 EndY=-24.0625 EndZ=0
    g33: LineSegment StartX=321.314 StartY=-24.0625 StartZ=0 EndX=334.103 EndY=-23.4378 EndZ=0
    g34: LineSegment StartX=334.103 StartY=-23.4378 StartZ=0 EndX=343.031 EndY=-22.6097 EndZ=0
    g35: LineSegment StartX=343.031 StartY=-22.6097 StartZ=0 EndX=352.43 EndY=-21.684 EndZ=0
    g36: LineSegment StartX=352.43 StartY=-21.684 StartZ=0 EndX=360.745 EndY=-20.8145 EndZ=0
    g37: LineSegment StartX=360.745 StartY=-20.8145 StartZ=0 EndX=371.414 EndY=-19.8817 EndZ=0
    g38: LineSegment StartX=371.414 StartY=-19.8817 StartZ=0 EndX=379.75 EndY=-19.1238 EndZ=0
    g39: LineSegment StartX=379.75 StartY=-19.1238 StartZ=0 EndX=388.728 EndY=-18.0162 EndZ=0
    g40: LineSegment StartX=388.728 StartY=-18.0162 StartZ=0 EndX=397.242 EndY=-16.8147 EndZ=0
    g41: LineSegment StartX=282.044 StartY=2.90825 StartZ=0 EndX=296.203 EndY=-25.8857 EndZ=0
    g42: LineSegment StartX=296.203 StartY=-25.8857 StartZ=0 EndX=289.375 EndY=-26.1898 EndZ=0
    g43: LineSegment StartX=289.375 StartY=-26.1898 StartZ=0 EndX=272.288 EndY=-26.8103 EndZ=0
    g44: LineSegment StartX=272.288 StartY=-26.8103 StartZ=0 EndX=259.745 EndY=-27.0379 EndZ=0
    g45: LineSegment StartX=259.745 StartY=-27.0379 StartZ=0 EndX=249.901 EndY=-27.0493 EndZ=0
    g46: LineSegment StartX=249.901 StartY=-27.0493 StartZ=0 EndX=233.501 EndY=4.36556 EndZ=0
    g47: LineSegment StartX=233.501 StartY=4.36556 StartZ=0 EndX=243.094 EndY=3.92907 EndZ=0
    g48: LineSegment StartX=243.094 StartY=3.92907 StartZ=0 EndX=253.595 EndY=3.78588 EndZ=0
    g49: LineSegment StartX=253.595 StartY=3.78588 StartZ=0 EndX=265.05 EndY=3.40404 EndZ=0
    g50: LineSegment StartX=265.05 StartY=3.40404 StartZ=0 EndX=275.169 EndY=3.11766 EndZ=0
    g51: LineSegment StartX=275.169 StartY=3.11766 StartZ=0 EndX=282.044 EndY=2.90825 EndZ=0
    g52: LineSegment StartX=245.031 StartY=-27.2218 StartZ=0 EndX=228.388 EndY=4.65846 EndZ=0
    g53: LineSegment StartX=245.031 StartY=-27.2218 StartZ=0 EndX=235.231 EndY=-27.2331 EndZ=0
    g54: LineSegment StartX=235.231 StartY=-27.2331 StartZ=0 EndX=223.865 EndY=-27.0543 EndZ=0
    g55: LineSegment StartX=223.865 StartY=-27.0543 StartZ=0 EndX=212.219 EndY=-26.7202 EndZ=0
    g56: LineSegment StartX=212.219 StartY=-26.7202 StartZ=0 EndX=191.07 EndY=-25.1947 EndZ=0
    g57: LineSegment StartX=185.283 StartY=5.70484 StartZ=0 EndX=201.134 EndY=5.37441 EndZ=0
    g58: LineSegment StartX=201.134 StartY=5.37441 StartZ=0 EndX=208.529 EndY=5.18341 EndZ=0
    g59: LineSegment StartX=208.529 StartY=5.18341 StartZ=0 EndX=215.787 EndY=5.0403 EndZ=0
    g60: LineSegment StartX=215.787 StartY=5.0403 StartZ=0 EndX=221.997 EndY=4.84856 EndZ=0
    g61: LineSegment StartX=221.997 StartY=4.84856 StartZ=0 EndX=228.388 EndY=4.65846 EndZ=0
    g62: LineSegment StartX=185.283 StartY=5.70484 StartZ=0 EndX=191.07 EndY=-25.1947 EndZ=0
    g63: Circle CenterX=170 CenterY=-17 CenterZ=0 NormalX=0 NormalY=0 NormalZ=1 AngleXU=0 Radius=4.1
  constraints (71):
    c: Vertical(g0)
    c: Coincident(g0,g1)
    c: Coincident(g1,g2)
    c: Coincident(g2,g3)
    c: Coincident(g3,g4)
    c: Coincident(g4,g5)
    c: Coincident(g5,g6)
    c: PointOnObject(g6,g-1)
    c: Coincident(g6,g7)
    c: Coincident(g7,g8)
    c: Coincident(g8,g9)
    c: Coincident(g9,g10)
    c: Coincident(g10,g11)
    c: Coincident(g11,g12)
    c: Coincident(g12,g13)
    c: Coincident(g13,g14)
    c: Coincident(g14,g0)
    c: Vertical(g15)
    c: Coincident(g15,g16)
    c: Coincident(g16,g17)
    c: Coincident(g17,g18)
    c: Coincident(g18,g19)
    c: Coincident(g19,g20)
    c: Coincident(g20,g21)
    c: Coincident(g21,g22)
    c: Coincident(g22,g23)
    c: Coincident(g23,g24)
    c: Coincident(g24,g25)
    c: Coincident(g25,g15)
    c: Coincident(g26,g27)
    c: Coincident(g27,g28)
    c: Coincident(g28,g29)
    c: Coincident(g29,g30)
    c: Coincident(g30,g31)
    c: Coincident(g31,g32)
    c: Coincident(g32,g33)
    c: Coincident(g33,g34)
    c: Coincident(g34,g35)
    c: Coincident(g35,g36)
    c: Coincident(g36,g37)
    c: Coincident(g37,g38)
    c: Coincident(g38,g39)
    c: Coincident(g39,g40)
    c: Coincident(g40,g26)
    c: Parallel(g21,g26)
    c: Coincident(g42,g43)
    c: Coincident(g43,g44)
    c: Coincident(g44,g45)
    c: Coincident(g46,g47)
    c: Coincident(g47,g48)
    c: Coincident(g48,g49)
    c: Coincident(g49,g50)
    c: Coincident(g50,g51)
    c: Parallel(g46,g52)
    c: Coincident(g52,g53)
    c: Coincident(g53,g54)
    c: Coincident(g54,g55)
    c: Coincident(g55,g56)
    c: Coincident(g57,g58)
    c: Coincident(g58,g59)
    c: Coincident(g59,g60)
    c: Coincident(g60,g61)
    c: Coincident(g61,g52)
    c: Coincident(g46,g45)
    c: Coincident(g41,g51)
    c: Coincident(g41,g42)
    c: Coincident(g62,g57)
    c: Coincident(g62,g56)
    c: Diameter(g63) = 8.2
    c: DistanceY(g63,g-1) = 17
    c: DistanceX(g-1,g63) = 170
FEATURE [PartDesign::Pocket] Pocket037
  BaseFeature = -> Pocket009
  Direction = (0,0,1)
  Length = 15
  Length2 = 5
  Profile = -> Sketch062
  ReferenceAxis = -> Sketch062 [N_Axis]
  Refine = true
  Suppressed = false
  Type = 0
FEATURE [Sketcher::SketchObject] Sketch063
  ArcFitTolerance = 1e-06
  FullyConstrained = false
  MakeInternals = false
  Placement = pos=(600,0,-600) rot=(0,0,1;0rad)
  sketch-geometry (123):
    g0: BSplineCurve PolesCount=61 KnotsCount=61 Degree=3 IsPeriodic=1
    g1-g61: Circle [constr] x61 (B-spline internal-alignment scaffolding for g0; pole/knot coordinates omitted)
    g62-g122: GeomPoint [constr] x61 (B-spline internal-alignment scaffolding for g0; pole/knot coordinates omitted)
  constraints (123):
    c: InternalAlignment(g1,g0)
    c: Weight(g1) = 1
    c: InternalAlignment(g2,g0)
    c: Equal(g2,g1)
    c: InternalAlignment(g3,g0)
    c: Equal(g3,g1)
    c: InternalAlignment(g4,g0)
    c: Equal(g4,g1)
    c: InternalAlignment(g5,g0)
    c: Equal(g5,g1)
    c: InternalAlignment(g6,g0)
    c: Equal(g6,g1)
    c: InternalAlignment(g7,g0)
    c: Equal(g7,g1)
    c: InternalAlignment(g8,g0)
    c: Equal(g8,g1)
    c: InternalAlignment(g9,g0)
    c: Equal(g9,g1)
    c: InternalAlignment(g10,g0)
    c: Equal(g10,g1)
    c: InternalAlignment(g11,g0)
    c: Equal(g11,g1)
    c: InternalAlignment(g12,g0)
    c: Equal(g12,g1)
    c: InternalAlignment(g13,g0)
    c: Equal(g13,g1)
    c: InternalAlignment(g14,g0)
    c: Equal(g14,g1)
    c: InternalAlignment(g15,g0)
    c: Equal(g15,g1)
    c: InternalAlignment(g16,g0)
    c: Equal(g16,g1)
    c: InternalAlignment(g17,g0)
    c: Equal(g17,g1)
    c: InternalAlignment(g18,g0)
    c: Equal(g18,g1)
    c: InternalAlignment(g19,g0)
    c: Equal(g19,g1)
    c: InternalAlignment(g20,g0)
    c: Equal(g20,g1)
    c: InternalAlignment(g21,g0)
    c: Equal(g21,g1)
    c: InternalAlignment(g22,g0)
    c: Equal(g22,g1)
    c: InternalAlignment(g23,g0)
    c: Equal(g23,g1)
    c: InternalAlignment(g24,g0)
    c: Equal(g24,g1)
    c: InternalAlignment(g25,g0)
    c: Equal(g25,g1)
    c: InternalAlignment(g26,g0)
    c: Equal(g26,g1)
    c: InternalAlignment(g27,g0)
    c: Equal(g27,g1)
    c: InternalAlignment(g28,g0)
    c: Equal(g28,g1)
    c: InternalAlignment(g29,g0)
    c: Equal(g29,g1)
    c: InternalAlignment(g30,g0)
    c: Equal(g30,g1)
    c: InternalAlignment(g31,g0)
    c: Equal(g31,g1)
    c: InternalAlignment(g32,g0)
    c: Equal(g32,g1)
    c: InternalAlignment(g33,g0)
    c: Equal(g33,g1)
    c: InternalAlignment(g34,g0)
    c: Equal(g34,g1)
    c: InternalAlignment(g35,g0)
    c: Equal(g35,g1)
    c: InternalAlignment(g36,g0)
    c: Equal(g36,g1)
    c: InternalAlignment(g37,g0)
    c: Equal(g37,g1)
    c: InternalAlignment(g38,g0)
    c: Equal(g38,g1)
    c: InternalAlignment(g39,g0)
    c: Equal(g39,g1)
    c: InternalAlignment(g40,g0)
    c: Equal(g40,g1)
    c: InternalAlignment(g41,g0)
    c: Equal(g41,g1)
    c: InternalAlignment(g42,g0)
    c: Equal(g42,g1)
    c: InternalAlignment(g43,g0)
    c: Equal(g43,g1)
    c: InternalAlignment(g44,g0)
    c: Equal(g44,g1)
    c: InternalAlignment(g45,g0)
    c: Equal(g45,g1)
    c: InternalAlignment(g46,g0)
    c: Equal(g46,g1)
    c: InternalAlignment(g47,g0)
    c: Equal(g47,g1)
    c: InternalAlignment(g48,g0)
    c: Equal(g48,g1)
    c: InternalAlignment(g49,g0)
    c: Equal(g49,g1)
    c: InternalAlignment(g50,g0)
    c: Equal(g50,g1)
    c: InternalAlignment(g51,g0)
    c: Equal(g51,g1)
    c: InternalAlignment(g52,g0)
    c: Equal(g52,g1)
    c: InternalAlignment(g53,g0)
    c: Equal(g53,g1)
    c: InternalAlignment(g54,g0)
    c: Equal(g54,g1)
    c: InternalAlignment(g55,g0)
    c: Equal(g55,g1)
    c: InternalAlignment(g56,g0)
    c: Equal(g56,g1)
    c: InternalAlignment(g57,g0)
    c: Equal(g57,g1)
    c: InternalAlignment(g58,g0)
    c: Equal(g58,g1)
    c: InternalAlignment(g59,g0)
    c: Equal(g59,g1)
    c: InternalAlignment(g60,g0)
    c: Equal(g60,g1)
    c: InternalAlignment(g61,g0)
    c: Equal(g61,g1)
    c: InternalAlignment(g62-g122 -> g0) x61
FEATURE [Sketcher::SketchObject] Sketch064
  ArcFitTolerance = 1e-06
  FullyConstrained = false
  MakeInternals = false
  sketch-geometry (123):
    g0: BSplineCurve PolesCount=61 KnotsCount=61 Degree=3 IsPeriodic=1
    g1-g61: Circle [constr] x61 (B-spline internal-alignment scaffolding for g0; pole/knot coordinates omitted)
    g62-g122: GeomPoint [constr] x61 (B-spline internal-alignment scaffolding for g0; pole/knot coordinates omitted)
  constraints (123):
    c: InternalAlignment(g1,g0)
    c: Weight(g1) = 1
    c: InternalAlignment(g2,g0)
    c: Equal(g2,g1)
    c: InternalAlignment(g3,g0)
    c: Equal(g3,g1)
    c: InternalAlignment(g4,g0)
    c: Equal(g4,g1)
    c: InternalAlignment(g5,g0)
    c: Equal(g5,g1)
    c: InternalAlignment(g6,g0)
    c: Equal(g6,g1)
    c: InternalAlignment(g7,g0)
    c: Equal(g7,g1)
    c: InternalAlignment(g8,g0)
    c: Equal(g8,g1)
    c: InternalAlignment(g9,g0)
    c: Equal(g9,g1)
    c: InternalAlignment(g10,g0)
    c: Equal(g10,g1)
    c: InternalAlignment(g11,g0)
    c: Equal(g11,g1)
    c: InternalAlignment(g12,g0)
    c: Equal(g12,g1)
    c: InternalAlignment(g13,g0)
    c: Equal(g13,g1)
    c: InternalAlignment(g14,g0)
    c: Equal(g14,g1)
    c: InternalAlignment(g15,g0)
    c: Equal(g15,g1)
    c: InternalAlignment(g16,g0)
    c: Equal(g16,g1)
    c: InternalAlignment(g17,g0)
    c: Equal(g17,g1)
    c: InternalAlignment(g18,g0)
    c: Equal(g18,g1)
    c: InternalAlignment(g19,g0)
    c: Equal(g19,g1)
    c: InternalAlignment(g20,g0)
    c: Equal(g20,g1)
    c: InternalAlignment(g21,g0)
    c: Equal(g21,g1)
    c: InternalAlignment(g22,g0)
    c: Equal(g22,g1)
    c: InternalAlignment(g23,g0)
    c: Equal(g23,g1)
    c: InternalAlignment(g24,g0)
    c: Equal(g24,g1)
    c: InternalAlignment(g25,g0)
    c: Equal(g25,g1)
    c: InternalAlignment(g26,g0)
    c: Equal(g26,g1)
    c: InternalAlignment(g27,g0)
    c: Equal(g27,g1)
    c: InternalAlignment(g28,g0)
    c: Equal(g28,g1)
    c: InternalAlignment(g29,g0)
    c: Equal(g29,g1)
    c: InternalAlignment(g30,g0)
    c: Equal(g30,g1)
    c: InternalAlignment(g31,g0)
    c: Equal(g31,g1)
    c: InternalAlignment(g32,g0)
    c: Equal(g32,g1)
    c: InternalAlignment(g33,g0)
    c: Equal(g33,g1)
    c: InternalAlignment(g34,g0)
    c: Equal(g34,g1)
    c: InternalAlignment(g35,g0)
    c: Equal(g35,g1)
    c: InternalAlignment(g36,g0)
    c: Equal(g36,g1)
    c: InternalAlignment(g37,g0)
    c: Equal(g37,g1)
    c: InternalAlignment(g38,g0)
    c: Equal(g38,g1)
    c: InternalAlignment(g39,g0)
    c: Equal(g39,g1)
    c: InternalAlignment(g40,g0)
    c: Equal(g40,g1)
    c: InternalAlignment(g41,g0)
    c: Equal(g41,g1)
    c: InternalAlignment(g42,g0)
    c: Equal(g42,g1)
    c: InternalAlignment(g43,g0)
    c: Equal(g43,g1)
    c: InternalAlignment(g44,g0)
    c: Equal(g44,g1)
    c: InternalAlignment(g45,g0)
    c: Equal(g45,g1)
    c: InternalAlignment(g46,g0)
    c: Equal(g46,g1)
    c: InternalAlignment(g47,g0)
    c: Equal(g47,g1)
    c: InternalAlignment(g48,g0)
    c: Equal(g48,g1)
    c: InternalAlignment(g49,g0)
    c: Equal(g49,g1)
    c: InternalAlignment(g50,g0)
    c: Equal(g50,g1)
    c: InternalAlignment(g51,g0)
    c: Equal(g51,g1)
    c: InternalAlignment(g52,g0)
    c: Equal(g52,g1)
    c: InternalAlignment(g53,g0)
    c: Equal(g53,g1)
    c: InternalAlignment(g54,g0)
    c: Equal(g54,g1)
    c: InternalAlignment(g55,g0)
    c: Equal(g55,g1)
    c: InternalAlignment(g56,g0)
    c: Equal(g56,g1)
    c: InternalAlignment(g57,g0)
    c: Equal(g57,g1)
    c: InternalAlignment(g58,g0)
    c: Equal(g58,g1)
    c: InternalAlignment(g59,g0)
    c: Equal(g59,g1)
    c: InternalAlignment(g60,g0)
    c: Equal(g60,g1)
    c: InternalAlignment(g61,g0)
    c: Equal(g61,g1)
    c: InternalAlignment(g62-g122 -> g0) x61
FEATURE [PartDesign::AdditiveLoft] AdditiveLoft009
  Closed = false
  Profile = -> Sketch064
  Refine = true
  Ruled = false
  Sections = -> [Sketch063]
  Suppressed = false
FEATURE [PartDesign::Plane] DatumPlane012
  AttachmentOffset = pos=(0,0,0) rot=(0,-1,0;0.785398rad)
  AttachmentSupport = -> [AdditiveLoft009]
  Length = 505.706
  MapMode = 5
  Placement = pos=(0,0,0) rot=(0,-1,0;0.785398rad)
  ResizeMode = 0
  Width = 80.8184
FEATURE [Sketcher::SketchObject] Sketch065
  ArcFitTolerance = 1e-06
  AttachmentSupport = -> [DatumPlane012]
  FullyConstrained = false
  MakeInternals = false
  MapMode = 5
  Placement = pos=(0,0,0) rot=(0,-1,0;0.785398rad)
  sketch-geometry (1):
    g0: Circle CenterX=28.3343 CenterY=4.75298 CenterZ=0 NormalX=0 NormalY=0 NormalZ=1 AngleXU=0 Radius=4.1
  constraints (1):
    c: Diameter(g0) = 8.2
FEATURE [PartDesign::Pocket] Pocket038
  BaseFeature = -> AdditiveLoft009
  Direction = (0.707107,0,-0.707107)
  Length = 1000
  Length2 = 5
  Profile = -> Sketch065
  ReferenceAxis = -> Sketch065 [N_Axis]
  Refine = true
  Suppressed = false
  Type = 0
FEATURE [Sketcher::SketchObject] Sketch066
  ArcFitTolerance = 1e-06
  AttachmentSupport = -> [Pocket038]
  FullyConstrained = false
  MakeInternals = false
  MapMode = 5
  sketch-geometry (4):
    g0: LineSegment StartX=-74.3122 StartY=118.602 StartZ=0 EndX=-74.3122 EndY=-69.0005 EndZ=0
    g1: LineSegment StartX=-74.3122 StartY=-69.0004 StartZ=0 EndX=870.96 EndY=-69.0004 EndZ=0
    g2: LineSegment StartX=870.96 StartY=-69.0004 StartZ=0 EndX=870.96 EndY=118.602 EndZ=0
    g3: LineSegment StartX=870.96 StartY=118.602 StartZ=0 EndX=-74.3122 EndY=118.602 EndZ=0
  constraints (8):
    c: Coincident(g0,g1)
    c: Coincident(g1,g2)
    c: Coincident(g2,g3)
    c: Coincident(g3,g0)
    c: Vertical(g0)
    c: Vertical(g2)
    c: Horizontal(g1)
    c: Horizontal(g3)
FEATURE [PartDesign::Pocket] Pocket039
  BaseFeature = -> Pocket038
  Direction = (0,0,-1)
  Length = 100
  Length2 = 5
  Profile = -> Sketch066
  ReferenceAxis = -> Sketch066 [N_Axis]
  Refine = true
  Suppressed = false
  Type = 0
FEATURE [Sketcher::SketchObject] Sketch067
  ArcFitTolerance = 1e-06
  AttachmentSupport = -> [Pocket039]
  FullyConstrained = false
  MakeInternals = false
  MapMode = 5
  Placement = pos=(0,0,-600) rot=(1,0,0;3.14159rad)
  sketch-geometry (4):
    g0: LineSegment StartX=26.9533 StartY=164.686 StartZ=0 EndX=26.9533 EndY=-77.9053 EndZ=0
    g1: LineSegment StartX=26.9533 StartY=-77.9053 StartZ=0 EndX=1059.07 EndY=-77.9053 EndZ=0
    g2: LineSegment StartX=1059.07 StartY=-77.9053 StartZ=0 EndX=1059.07 EndY=164.686 EndZ=0
    g3: LineSegment StartX=1059.07 StartY=164.686 StartZ=0 EndX=26.9533 EndY=164.686 EndZ=0
  constraints (8):
    c: Coincident(g0,g1)
    c: Coincident(g1,g2)
    c: Coincident(g2,g3)
    c: Coincident(g3,g0)
    c: Vertical(g0)
    c: Vertical(g2)
    c: Horizontal(g1)
    c: Horizontal(g3)
FEATURE [PartDesign::Pocket] Pocket040
  BaseFeature = -> Pocket039
  Direction = (0,0,1)
  Length = 490
  Length2 = 5
  Profile = -> Sketch067
  ReferenceAxis = -> Sketch067 [N_Axis]
  Refine = true
  Suppressed = false
  Type = 0
FEATURE [Sketcher::SketchObject] Sketch068
  ArcFitTolerance = 1e-06
  AttachmentSupport = -> [Pocket040]
  FullyConstrained = false
  MakeInternals = false
  MapMode = 5
  Placement = pos=(0,0,-110) rot=(1,0,0;3.14159rad)
  sketch-geometry (80):
    g0: LineSegment StartX=131.615 StartY=-13.8563 StartZ=0 EndX=131.615 EndY=4.74903 EndZ=0
    g1: LineSegment StartX=131.615 StartY=4.74903 StartZ=0 EndX=126.762 EndY=4.05077 EndZ=0
    g2: LineSegment StartX=126.762 StartY=4.05077 StartZ=0 EndX=121.398 EndY=3.23596 EndZ=0
    g3: LineSegment StartX=121.398 StartY=3.23596 StartZ=0 EndX=117.609 EndY=2.65394 EndZ=0
    g4: LineSegment StartX=117.609 StartY=2.65394 StartZ=0 EndX=114.461 EndY=1.60538 EndZ=0
    g5: LineSegment StartX=114.461 StartY=1.60538 StartZ=0 EndX=112.828 EndY=0.731336 EndZ=0
    g6: LineSegment StartX=112.828 StartY=0.731336 StartZ=0 EndX=112.128 EndY=0 EndZ=0
    g7: LineSegment StartX=112.128 StartY=0 StartZ=0 EndX=112.303 EndY=-0.95915 EndZ=0
    g8: LineSegment StartX=112.303 StartY=-0.95915 StartZ=0 EndX=113.119 EndY=-2.30019 EndZ=0
    g9: LineSegment StartX=113.119 StartY=-2.30019 StartZ=0 EndX=115.159 EndY=-4.3994 EndZ=0
    g10: LineSegment StartX=115.159 StartY=-4.3994 StartZ=0 EndX=118.073 EndY=-6.84862 EndZ=0
    g11: LineSegment StartX=118.073 StartY=-6.84862 StartZ=0 EndX=121.395 EndY=-8.88986 EndZ=0
    g12: LineSegment StartX=121.395 StartY=-8.88986 StartZ=0 EndX=125.243 EndY=-10.8146 EndZ=0
    g13: LineSegment StartX=125.243 StartY=-10.8146 StartZ=0 EndX=129.381 EndY=-12.9144 EndZ=0
    g14: LineSegment StartX=129.381 StartY=-12.9144 StartZ=0 EndX=131.615 EndY=-13.8563 EndZ=0
    g15: LineSegment StartX=456.728 StartY=-6.97805 StartZ=0 EndX=456.728 EndY=-2.77376 EndZ=0
    g16: LineSegment StartX=456.728 StartY=-2.77376 StartZ=0 EndX=444.473 EndY=-2.77376 EndZ=0
    g17: LineSegment StartX=444.473 StartY=-2.77376 StartZ=0 EndX=430.721 EndY=-2.53251 EndZ=0
    g18: LineSegment StartX=430.721 StartY=-2.53251 StartZ=0 EndX=419.576 EndY=-2.29126 EndZ=0
    g19: LineSegment StartX=419.576 StartY=-2.29126 StartZ=0 EndX=405.248 EndY=-1.99854 EndZ=0
    g20: LineSegment StartX=405.248 StartY=-1.99854 StartZ=0 EndX=391.498 EndY=-1.51681 EndZ=0
    g21: LineSegment StartX=391.498 StartY=-1.51681 StartZ=0 EndX=401.723 EndY=-15.753 EndZ=0
    g22: LineSegment StartX=401.723 StartY=-15.753 StartZ=0 EndX=417.216 EndY=-13.54 EndZ=0
    g23: LineSegment StartX=417.216 StartY=-13.54 StartZ=0 EndX=432.077 EndY=-10.9345 EndZ=0
    g24: LineSegment StartX=432.077 StartY=-10.9345 StartZ=0 EndX=447.999 EndY=-8.4738 EndZ=0
    g25: LineSegment StartX=447.999 StartY=-8.4738 StartZ=0 EndX=456.728 EndY=-6.97805 EndZ=0
    g26: LineSegment StartX=397.242 StartY=-16.8147 StartZ=0 EndX=385.617 EndY=-0.630676 EndZ=0
    g27: LineSegment StartX=385.617 StartY=-0.630676 StartZ=0 EndX=375.298 EndY=-0.398599 EndZ=0
    g28: LineSegment StartX=375.298 StartY=-0.398599 StartZ=0 EndX=363.461 EndY=-0.159949 EndZ=0
    g29: LineSegment StartX=363.461 StartY=-0.159949 StartZ=0 EndX=353.629 EndY=0.221889 EndZ=0
    g30: LineSegment StartX=353.629 StartY=0.221889 StartZ=0 EndX=343.415 EndY=0.603728 EndZ=0
    g31: LineSegment StartX=343.415 StartY=0.603728 StartZ=0 EndX=334.198 EndY=0.953662 EndZ=0
    g32: LineSegment StartX=334.198 StartY=0.953662 StartZ=0 EndX=322.257 EndY=-24.5211 EndZ=0
    g33: LineSegment StartX=322.257 StartY=-24.5211 StartZ=0 EndX=334.103 EndY=-23.4378 EndZ=0
    g34: LineSegment StartX=334.103 StartY=-23.4378 StartZ=0 EndX=343.031 EndY=-22.6097 EndZ=0
    g35: LineSegment StartX=343.031 StartY=-22.6097 StartZ=0 EndX=352.43 EndY=-21.684 EndZ=0
    g36: LineSegment StartX=352.43 StartY=-21.684 StartZ=0 EndX=360.745 EndY=-20.8145 EndZ=0
    g37: LineSegment StartX=360.745 StartY=-20.8145 StartZ=0 EndX=371.414 EndY=-19.8817 EndZ=0
    g38: LineSegment StartX=371.414 StartY=-19.8817 StartZ=0 EndX=379.75 EndY=-19.1238 EndZ=0
    g39: LineSegment StartX=379.75 StartY=-19.1238 StartZ=0 EndX=388.728 EndY=-18.0162 EndZ=0
    g40: LineSegment StartX=388.728 StartY=-18.0162 StartZ=0 EndX=397.242 EndY=-16.8147 EndZ=0
    g41: LineSegment StartX=329.504 StartY=1.30384 StartZ=0 EndX=317.298 EndY=-24.7356 EndZ=0
    g42: LineSegment StartX=317.298 StartY=-24.7356 StartZ=0 EndX=304.506 EndY=-25.3307 EndZ=0
    g43: LineSegment StartX=304.506 StartY=-25.3307 StartZ=0 EndX=289.375 EndY=-26.1898 EndZ=0
    g44: LineSegment StartX=289.375 StartY=-26.1898 StartZ=0 EndX=272.288 EndY=-26.8103 EndZ=0
    g45: LineSegment StartX=272.288 StartY=-26.8103 StartZ=0 EndX=259.745 EndY=-27.0379 EndZ=0
    g46: LineSegment StartX=259.745 StartY=-27.0379 StartZ=0 EndX=249.901 EndY=-27.0493 EndZ=0
    g47: LineSegment StartX=249.901 StartY=-27.0493 StartZ=0 EndX=233.501 EndY=4.36556 EndZ=0
    g48: LineSegment StartX=233.501 StartY=4.36556 StartZ=0 EndX=243.094 EndY=3.92907 EndZ=0
    g49: LineSegment StartX=243.094 StartY=3.92907 StartZ=0 EndX=253.595 EndY=3.78588 EndZ=0
    g50: LineSegment StartX=253.595 StartY=3.78588 StartZ=0 EndX=265.05 EndY=3.40404 EndZ=0
    g51: LineSegment StartX=265.05 StartY=3.40404 StartZ=0 EndX=275.169 EndY=3.11766 EndZ=0
    g52: LineSegment StartX=275.169 StartY=3.11766 StartZ=0 EndX=286.396 EndY=2.97312 EndZ=0
    g53: LineSegment StartX=286.396 StartY=2.97312 StartZ=0 EndX=297.231 EndY=2.59128 EndZ=0
    g54: LineSegment StartX=297.231 StartY=2.59128 StartZ=0 EndX=306.252 EndY=2.20944 EndZ=0
    g55: LineSegment StartX=306.252 StartY=2.20944 StartZ=0 EndX=313.144 EndY=1.92289 EndZ=0
    g56: LineSegment StartX=313.144 StartY=1.92289 StartZ=0 EndX=322.015 EndY=1.57501 EndZ=0
    g57: LineSegment StartX=322.015 StartY=1.57501 StartZ=0 EndX=329.504 EndY=1.30384 EndZ=0
    g58: LineSegment StartX=245.031 StartY=-27.2218 StartZ=0 EndX=228.388 EndY=4.65846 EndZ=0
    g59: LineSegment StartX=245.031 StartY=-27.2218 StartZ=0 EndX=235.231 EndY=-27.2331 EndZ=0
    g60: LineSegment StartX=235.231 StartY=-27.2331 StartZ=0 EndX=223.865 EndY=-27.0543 EndZ=0
    g61: LineSegment StartX=223.865 StartY=-27.0543 StartZ=0 EndX=212.219 EndY=-26.7202 EndZ=0
    g62: LineSegment StartX=212.219 StartY=-26.7202 StartZ=0 EndX=198.319 EndY=-25.527 EndZ=0
    g63: LineSegment StartX=198.319 StartY=-25.527 StartZ=0 EndX=187.341 EndY=-24.5724 EndZ=0
    g64: LineSegment StartX=187.341 StartY=-24.5724 StartZ=0 EndX=179.37 EndY=-23.761 EndZ=0
    g65: LineSegment StartX=179.37 StartY=-23.761 StartZ=0 EndX=173.309 EndY=-23.2491 EndZ=0
    g66: LineSegment StartX=173.309 StartY=-23.2491 StartZ=0 EndX=184.954 EndY=5.81717 EndZ=0
    g67: LineSegment StartX=184.954 StartY=5.81717 StartZ=0 EndX=192.295 EndY=5.53943 EndZ=0
    g68: LineSegment StartX=192.295 StartY=5.53943 StartZ=0 EndX=201.134 EndY=5.37441 EndZ=0
    g69: LineSegment StartX=201.134 StartY=5.37441 StartZ=0 EndX=208.529 EndY=5.18341 EndZ=0
    g70: LineSegment StartX=208.529 StartY=5.18341 StartZ=0 EndX=215.787 EndY=5.0403 EndZ=0
    g71: LineSegment StartX=215.787 StartY=5.0403 StartZ=0 EndX=221.997 EndY=4.84856 EndZ=0
    g72: LineSegment StartX=221.997 StartY=4.84856 StartZ=0 EndX=228.388 EndY=4.65846 EndZ=0
    g73: LineSegment StartX=168.938 StartY=-22.8012 StartZ=0 EndX=180.507 EndY=6.07631 EndZ=0
    g74: LineSegment StartX=180.507 StartY=6.07631 StartZ=0 EndX=170.252 EndY=6.17293 EndZ=0
    g75: LineSegment StartX=170.252 StartY=6.17293 StartZ=0 EndX=162.95 EndY=6.07748 EndZ=0
    g76: LineSegment StartX=162.95 StartY=6.07748 StartZ=0 EndX=158.204 EndY=5.93976 EndZ=0
    g77: LineSegment StartX=158.204 StartY=5.93976 StartZ=0 EndX=158.204 EndY=-21.1102 EndZ=0
    g78: LineSegment StartX=158.204 StartY=-21.1102 StartZ=0 EndX=162.285 EndY=-21.9264 EndZ=0
    g79: LineSegment StartX=162.285 StartY=-21.9264 StartZ=0 EndX=168.938 EndY=-22.8012 EndZ=0
  constraints (88):
    c: Vertical(g0)
    c: Coincident(g0,g1)
    c: Coincident(g1,g2)
    c: Coincident(g2,g3)
    c: Coincident(g3,g4)
    c: Coincident(g4,g5)
    c: Coincident(g5,g6)
    c: PointOnObject(g6,g-1)
    c: Coincident(g6,g7)
    c: Coincident(g7,g8)
    c: Coincident(g8,g9)
    c: Coincident(g9,g10)
    c: Coincident(g10,g11)
    c: Coincident(g11,g12)
    c: Coincident(g12,g13)
    c: Coincident(g13,g14)
    c: Coincident(g14,g0)
    c: Vertical(g15)
    c: Coincident(g15,g16)
    c: Coincident(g16,g17)
    c: Coincident(g17,g18)
    c: Coincident(g18,g19)
    c: Coincident(g19,g20)
    c: Coincident(g20,g21)
    c: Coincident(g21,g22)
    c: Coincident(g22,g23)
    c: Coincident(g23,g24)
    c: Coincident(g24,g25)
    c: Coincident(g25,g15)
    c: Coincident(g26,g27)
    c: Coincident(g27,g28)
    c: Coincident(g28,g29)
    c: Coincident(g29,g30)
    c: Coincident(g30,g31)
    c: Coincident(g31,g32)
    c: Coincident(g32,g33)
    c: Coincident(g33,g34)
    c: Coincident(g34,g35)
    c: Coincident(g35,g36)
    c: Coincident(g36,g37)
    c: Coincident(g37,g38)
    c: Coincident(g38,g39)
    c: Coincident(g39,g40)
    c: Coincident(g40,g26)
    c: Parallel(g21,g26)
    c: Parallel(g32,g41)
    c: Coincident(g41,g42)
    c: Coincident(g42,g43)
    c: Coincident(g43,g44)
    c: Coincident(g44,g45)
    c: Coincident(g45,g46)
    c: Coincident(g47,g48)
    c: Coincident(g48,g49)
    c: Coincident(g49,g50)
    c: Coincident(g50,g51)
    c: Coincident(g51,g52)
    c: Coincident(g52,g53)
    c: Coincident(g53,g54)
    c: Coincident(g54,g55)
    c: Coincident(g55,g56)
    c: Coincident(g56,g57)
    c: Coincident(g57,g41)
    c: Parallel(g47,g58)
    c: Coincident(g58,g59)
    c: Coincident(g59,g60)
    c: Coincident(g60,g61)
    c: Coincident(g61,g62)
    c: Coincident(g62,g63)
    c: Coincident(g63,g64)
    c: Coincident(g64,g65)
    c: Coincident(g65,g66)
    c: Coincident(g66,g67)
    c: Coincident(g67,g68)
    c: Coincident(g68,g69)
    c: Coincident(g69,g70)
    c: Coincident(g70,g71)
    c: Coincident(g71,g72)
    c: Coincident(g72,g58)
    c: Coincident(g73,g74)
    c: Coincident(g74,g75)
    c: Coincident(g75,g76)
    c: Coincident(g76,g77)
    c: Vertical(g77)
    c: Coincident(g77,g78)
    c: Coincident(g78,g79)
    c: Coincident(g79,g73)
    c: Parallel(g73,g66)
    c: Coincident(g47,g46)
FEATURE [PartDesign::Pocket] Pocket041
  BaseFeature = -> Pocket040
  Direction = (0,0,1)
  Length = 15
  Length2 = 5
  Profile = -> Sketch068
  ReferenceAxis = -> Sketch068 [N_Axis]
  Refine = true
  Suppressed = false
  Type = 0
FEATURE [Sketcher::SketchObject] Sketch069
  ArcFitTolerance = 1e-06
  AttachmentSupport = -> [Pocket037]
  FullyConstrained = false
  MakeInternals = false
  MapMode = 5
  Placement = pos=(0,0,-110) rot=(1,0,0;3.14159rad)
  sketch-geometry (4):
    g0: LineSegment StartX=382 StartY=9.52426 StartZ=0 EndX=382 EndY=-24.3239 EndZ=0
    g1: LineSegment StartX=382 StartY=-24.3239 StartZ=0 EndX=516.705 EndY=-24.3239 EndZ=0
    g2: LineSegment StartX=516.705 StartY=-24.3239 StartZ=0 EndX=516.705 EndY=9.52426 EndZ=0
    g3: LineSegment StartX=516.705 StartY=9.52426 StartZ=0 EndX=382 EndY=9.52426 EndZ=0
  constraints (9):
    c: Coincident(g0,g1)
    c: Coincident(g1,g2)
    c: Coincident(g2,g3)
    c: Coincident(g3,g0)
    c: Vertical(g0)
    c: Vertical(g2)
    c: Horizontal(g1)
    c: Horizontal(g3)
    c: DistanceX(g-1,g0) = 382
FEATURE [Sketcher::SketchObject] Sketch070
  ArcFitTolerance = 1e-06
  AttachmentSupport = -> [Pocket041]
  FullyConstrained = false
  MakeInternals = false
  MapMode = 5
  Placement = pos=(0,0,-110) rot=(1,0,0;3.14159rad)
  sketch-geometry (4):
    g0: LineSegment StartX=74.3403 StartY=44.6512 StartZ=0 EndX=74.3403 EndY=-86.4098 EndZ=0
    g1: LineSegment StartX=74.3403 StartY=-86.4098 StartZ=0 EndX=382 EndY=-86.4098 EndZ=0
    g2: LineSegment StartX=382 StartY=-86.4098 StartZ=0 EndX=382 EndY=44.6512 EndZ=0
    g3: LineSegment StartX=382 StartY=44.6512 StartZ=0 EndX=74.3403 EndY=44.6512 EndZ=0
  constraints (9):
    c: Coincident(g0,g1)
    c: Coincident(g1,g2)
    c: Coincident(g2,g3)
    c: Coincident(g3,g0)
    c: Vertical(g0)
    c: Vertical(g2)
    c: Horizontal(g1)
    c: Horizontal(g3)
    c: DistanceX(g-1,g2) = 382
FEATURE [PartDesign::Pocket] Pocket042
  BaseFeature = -> Pocket041
  Direction = (0,0,1)
  Length = 15
  Length2 = 5
  Profile = -> Sketch070
  ReferenceAxis = -> Sketch070 [N_Axis]
  Refine = true
  Suppressed = false
  Type = 0
FEATURE [PartDesign::Body] Body009
  AllowCompound = false
  Group = -> [Sketch064,Sketch063,AdditiveLoft009,DatumPlane012,Sketch065,Pocket038,Sketch066,Pocket039,Sketch067,Pocket040,Sketch068,Pocket041,Sketch070,Pocket042]
  Origin = -> Origin009
  Placement = pos=(0,0,-100) rot=(0,0,1;0rad)
  Tip = -> Pocket042
FEATURE [PartDesign::Pocket] Pocket043
  BaseFeature = -> Pocket037
  Direction = (0,0,1)
  Length = 15
  Length2 = 5
  Profile = -> Sketch069
  ReferenceAxis = -> Sketch069 [N_Axis]
  Refine = true
  Suppressed = false
  Type = 0
FEATURE [Sketcher::SketchObject] Sketch071
  ArcFitTolerance = 1e-06
  AttachmentSupport = -> [Pocket007]
  FullyConstrained = true
  MakeInternals = false
  MapMode = 5
  Placement = pos=(0,0,-10) rot=(1,0,0;3.14159rad)
  sketch-geometry (4):
    g0: Circle CenterX=310 CenterY=-12 CenterZ=0 NormalX=0 NormalY=0 NormalZ=1 AngleXU=0 Radius=4.1
    g1: Circle CenterX=240 CenterY=-5 CenterZ=0 NormalX=0 NormalY=0 NormalZ=1 AngleXU=0 Radius=4.1
    g2: Circle CenterX=170 CenterY=-17 CenterZ=0 NormalX=0 NormalY=0 NormalZ=1 AngleXU=0 Radius=4.1
    g3: Circle CenterX=100 CenterY=-4 CenterZ=0 NormalX=0 NormalY=0 NormalZ=1 AngleXU=0 Radius=4.1
  constraints (12):
    c: Diameter(g0) = 8.2
    c: Diameter(g1) = 8.2
    c: Diameter(g2) = 8.2
    c: Diameter(g3) = 8.2
    c: DistanceX(g-1,g3) = 100
    c: DistanceX(g3,g2) = 70
    c: DistanceX(g2,g1) = 70
    c: DistanceX(g1,g0) = 70
    c: DistanceY(g3,g-1) = 4
    c: DistanceY(g2,g-1) = 17
    c: DistanceY(g1,g-1) = 5
    c: DistanceY(g0,g-1) = 12
FEATURE [PartDesign::Pocket] Pocket044
  BaseFeature = -> Pocket007
  Direction = (0,0,1)
  Length = 15
  Length2 = 5
  Profile = -> Sketch071
  ReferenceAxis = -> Sketch071 [N_Axis]
  Refine = true
  Suppressed = false
  Type = 0
FEATURE [Sketcher::SketchObject] Sketch072
  ArcFitTolerance = 1e-06
  AttachmentSupport = -> [Pocket044]
  FullyConstrained = false
  MakeInternals = false
  MapMode = 5
  Placement = pos=(0,0,-10) rot=(1,0,0;3.14159rad)
  sketch-geometry (4):
    g0: LineSegment StartX=0 StartY=50.2756 StartZ=0 EndX=0 EndY=-78.0723 EndZ=0
    g1: LineSegment StartX=0 StartY=-78.0723 StartZ=0 EndX=280 EndY=-78.0723 EndZ=0
    g2: LineSegment StartX=280 StartY=-78.0723 StartZ=0 EndX=280 EndY=50.2756 EndZ=0
    g3: LineSegment StartX=280 StartY=50.2756 StartZ=0 EndX=0 EndY=50.2756 EndZ=0
  constraints (10):
    c: Coincident(g0,g1)
    c: Coincident(g1,g2)
    c: Coincident(g2,g3)
    c: Coincident(g3,g0)
    c: Vertical(g0)
    c: Vertical(g2)
    c: Horizontal(g1)
    c: Horizontal(g3)
    c: PointOnObject(g0,g-2)
    c: DistanceX(g-1,g2) = 280
FEATURE [Sketcher::SketchObject] Sketch073
  ArcFitTolerance = 1e-06
  FullyConstrained = false
  MakeInternals = false
  Placement = pos=(600,0,-600) rot=(0,0,1;0rad)
  sketch-geometry (123):
    g0: BSplineCurve PolesCount=61 KnotsCount=61 Degree=3 IsPeriodic=1
    g1-g61: Circle [constr] x61 (B-spline internal-alignment scaffolding for g0; pole/knot coordinates omitted)
    g62-g122: GeomPoint [constr] x61 (B-spline internal-alignment scaffolding for g0; pole/knot coordinates omitted)
  constraints (123):
    c: InternalAlignment(g1,g0)
    c: Weight(g1) = 1
    c: InternalAlignment(g2,g0)
    c: Equal(g2,g1)
    c: InternalAlignment(g3,g0)
    c: Equal(g3,g1)
    c: InternalAlignment(g4,g0)
    c: Equal(g4,g1)
    c: InternalAlignment(g5,g0)
    c: Equal(g5,g1)
    c: InternalAlignment(g6,g0)
    c: Equal(g6,g1)
    c: InternalAlignment(g7,g0)
    c: Equal(g7,g1)
    c: InternalAlignment(g8,g0)
    c: Equal(g8,g1)
    c: InternalAlignment(g9,g0)
    c: Equal(g9,g1)
    c: InternalAlignment(g10,g0)
    c: Equal(g10,g1)
    c: InternalAlignment(g11,g0)
    c: Equal(g11,g1)
    c: InternalAlignment(g12,g0)
    c: Equal(g12,g1)
    c: InternalAlignment(g13,g0)
    c: Equal(g13,g1)
    c: InternalAlignment(g14,g0)
    c: Equal(g14,g1)
    c: InternalAlignment(g15,g0)
    c: Equal(g15,g1)
    c: InternalAlignment(g16,g0)
    c: Equal(g16,g1)
    c: InternalAlignment(g17,g0)
    c: Equal(g17,g1)
    c: InternalAlignment(g18,g0)
    c: Equal(g18,g1)
    c: InternalAlignment(g19,g0)
    c: Equal(g19,g1)
    c: InternalAlignment(g20,g0)
    c: Equal(g20,g1)
    c: InternalAlignment(g21,g0)
    c: Equal(g21,g1)
    c: InternalAlignment(g22,g0)
    c: Equal(g22,g1)
    c: InternalAlignment(g23,g0)
    c: Equal(g23,g1)
    c: InternalAlignment(g24,g0)
    c: Equal(g24,g1)
    c: InternalAlignment(g25,g0)
    c: Equal(g25,g1)
    c: InternalAlignment(g26,g0)
    c: Equal(g26,g1)
    c: InternalAlignment(g27,g0)
    c: Equal(g27,g1)
    c: InternalAlignment(g28,g0)
    c: Equal(g28,g1)
    c: InternalAlignment(g29,g0)
    c: Equal(g29,g1)
    c: InternalAlignment(g30,g0)
    c: Equal(g30,g1)
    c: InternalAlignment(g31,g0)
    c: Equal(g31,g1)
    c: InternalAlignment(g32,g0)
    c: Equal(g32,g1)
    c: InternalAlignment(g33,g0)
    c: Equal(g33,g1)
    c: InternalAlignment(g34,g0)
    c: Equal(g34,g1)
    c: InternalAlignment(g35,g0)
    c: Equal(g35,g1)
    c: InternalAlignment(g36,g0)
    c: Equal(g36,g1)
    c: InternalAlignment(g37,g0)
    c: Equal(g37,g1)
    c: InternalAlignment(g38,g0)
    c: Equal(g38,g1)
    c: InternalAlignment(g39,g0)
    c: Equal(g39,g1)
    c: InternalAlignment(g40,g0)
    c: Equal(g40,g1)
    c: InternalAlignment(g41,g0)
    c: Equal(g41,g1)
    c: InternalAlignment(g42,g0)
    c: Equal(g42,g1)
    c: InternalAlignment(g43,g0)
    c: Equal(g43,g1)
    c: InternalAlignment(g44,g0)
    c: Equal(g44,g1)
    c: InternalAlignment(g45,g0)
    c: Equal(g45,g1)
    c: InternalAlignment(g46,g0)
    c: Equal(g46,g1)
    c: InternalAlignment(g47,g0)
    c: Equal(g47,g1)
    c: InternalAlignment(g48,g0)
    c: Equal(g48,g1)
    c: InternalAlignment(g49,g0)
    c: Equal(g49,g1)
    c: InternalAlignment(g50,g0)
    c: Equal(g50,g1)
    c: InternalAlignment(g51,g0)
    c: Equal(g51,g1)
    c: InternalAlignment(g52,g0)
    c: Equal(g52,g1)
    c: InternalAlignment(g53,g0)
    c: Equal(g53,g1)
    c: InternalAlignment(g54,g0)
    c: Equal(g54,g1)
    c: InternalAlignment(g55,g0)
    c: Equal(g55,g1)
    c: InternalAlignment(g56,g0)
    c: Equal(g56,g1)
    c: InternalAlignment(g57,g0)
    c: Equal(g57,g1)
    c: InternalAlignment(g58,g0)
    c: Equal(g58,g1)
    c: InternalAlignment(g59,g0)
    c: Equal(g59,g1)
    c: InternalAlignment(g60,g0)
    c: Equal(g60,g1)
    c: InternalAlignment(g61,g0)
    c: Equal(g61,g1)
    c: InternalAlignment(g62-g122 -> g0) x61
FEATURE [Sketcher::SketchObject] Sketch074
  ArcFitTolerance = 1e-06
  FullyConstrained = false
  MakeInternals = false
  sketch-geometry (123):
    g0: BSplineCurve PolesCount=61 KnotsCount=61 Degree=3 IsPeriodic=1
    g1-g61: Circle [constr] x61 (B-spline internal-alignment scaffolding for g0; pole/knot coordinates omitted)
    g62-g122: GeomPoint [constr] x61 (B-spline internal-alignment scaffolding for g0; pole/knot coordinates omitted)
  constraints (123):
    c: InternalAlignment(g1,g0)
    c: Weight(g1) = 1
    c: InternalAlignment(g2,g0)
    c: Equal(g2,g1)
    c: InternalAlignment(g3,g0)
    c: Equal(g3,g1)
    c: InternalAlignment(g4,g0)
    c: Equal(g4,g1)
    c: InternalAlignment(g5,g0)
    c: Equal(g5,g1)
    c: InternalAlignment(g6,g0)
    c: Equal(g6,g1)
    c: InternalAlignment(g7,g0)
    c: Equal(g7,g1)
    c: InternalAlignment(g8,g0)
    c: Equal(g8,g1)
    c: InternalAlignment(g9,g0)
    c: Equal(g9,g1)
    c: InternalAlignment(g10,g0)
    c: Equal(g10,g1)
    c: InternalAlignment(g11,g0)
    c: Equal(g11,g1)
    c: InternalAlignment(g12,g0)
    c: Equal(g12,g1)
    c: InternalAlignment(g13,g0)
    c: Equal(g13,g1)
    c: InternalAlignment(g14,g0)
    c: Equal(g14,g1)
    c: InternalAlignment(g15,g0)
    c: Equal(g15,g1)
    c: InternalAlignment(g16,g0)
    c: Equal(g16,g1)
    c: InternalAlignment(g17,g0)
    c: Equal(g17,g1)
    c: InternalAlignment(g18,g0)
    c: Equal(g18,g1)
    c: InternalAlignment(g19,g0)
    c: Equal(g19,g1)
    c: InternalAlignment(g20,g0)
    c: Equal(g20,g1)
    c: InternalAlignment(g21,g0)
    c: Equal(g21,g1)
    c: InternalAlignment(g22,g0)
    c: Equal(g22,g1)
    c: InternalAlignment(g23,g0)
    c: Equal(g23,g1)
    c: InternalAlignment(g24,g0)
    c: Equal(g24,g1)
    c: InternalAlignment(g25,g0)
    c: Equal(g25,g1)
    c: InternalAlignment(g26,g0)
    c: Equal(g26,g1)
    c: InternalAlignment(g27,g0)
    c: Equal(g27,g1)
    c: InternalAlignment(g28,g0)
    c: Equal(g28,g1)
    c: InternalAlignment(g29,g0)
    c: Equal(g29,g1)
    c: InternalAlignment(g30,g0)
    c: Equal(g30,g1)
    c: InternalAlignment(g31,g0)
    c: Equal(g31,g1)
    c: InternalAlignment(g32,g0)
    c: Equal(g32,g1)
    c: InternalAlignment(g33,g0)
    c: Equal(g33,g1)
    c: InternalAlignment(g34,g0)
    c: Equal(g34,g1)
    c: InternalAlignment(g35,g0)
    c: Equal(g35,g1)
    c: InternalAlignment(g36,g0)
    c: Equal(g36,g1)
    c: InternalAlignment(g37,g0)
    c: Equal(g37,g1)
    c: InternalAlignment(g38,g0)
    c: Equal(g38,g1)
    c: InternalAlignment(g39,g0)
    c: Equal(g39,g1)
    c: InternalAlignment(g40,g0)
    c: Equal(g40,g1)
    c: InternalAlignment(g41,g0)
    c: Equal(g41,g1)
    c: InternalAlignment(g42,g0)
    c: Equal(g42,g1)
    c: InternalAlignment(g43,g0)
    c: Equal(g43,g1)
    c: InternalAlignment(g44,g0)
    c: Equal(g44,g1)
    c: InternalAlignment(g45,g0)
    c: Equal(g45,g1)
    c: InternalAlignment(g46,g0)
    c: Equal(g46,g1)
    c: InternalAlignment(g47,g0)
    c: Equal(g47,g1)
    c: InternalAlignment(g48,g0)
    c: Equal(g48,g1)
    c: InternalAlignment(g49,g0)
    c: Equal(g49,g1)
    c: InternalAlignment(g50,g0)
    c: Equal(g50,g1)
    c: InternalAlignment(g51,g0)
    c: Equal(g51,g1)
    c: InternalAlignment(g52,g0)
    c: Equal(g52,g1)
    c: InternalAlignment(g53,g0)
    c: Equal(g53,g1)
    c: InternalAlignment(g54,g0)
    c: Equal(g54,g1)
    c: InternalAlignment(g55,g0)
    c: Equal(g55,g1)
    c: InternalAlignment(g56,g0)
    c: Equal(g56,g1)
    c: InternalAlignment(g57,g0)
    c: Equal(g57,g1)
    c: InternalAlignment(g58,g0)
    c: Equal(g58,g1)
    c: InternalAlignment(g59,g0)
    c: Equal(g59,g1)
    c: InternalAlignment(g60,g0)
    c: Equal(g60,g1)
    c: InternalAlignment(g61,g0)
    c: Equal(g61,g1)
    c: InternalAlignment(g62-g122 -> g0) x61
FEATURE [PartDesign::AdditiveLoft] AdditiveLoft010
  Closed = false
  Profile = -> Sketch074
  Refine = true
  Ruled = false
  Sections = -> [Sketch073]
  Suppressed = false
FEATURE [PartDesign::Plane] DatumPlane013
  AttachmentOffset = pos=(0,0,0) rot=(0,-1,0;0.785398rad)
  AttachmentSupport = -> [AdditiveLoft010]
  Length = 275.193
  MapMode = 5
  Placement = pos=(0,0,0) rot=(0,-1,0;0.785398rad)
  ResizeMode = 0
  Width = 82.3516
FEATURE [Sketcher::SketchObject] Sketch075
  ArcFitTolerance = 1e-06
  AttachmentSupport = -> [DatumPlane013]
  FullyConstrained = false
  MakeInternals = false
  MapMode = 5
  Placement = pos=(0,0,0) rot=(0,-1,0;0.785398rad)
  sketch-geometry (1):
    g0: Circle CenterX=28.3343 CenterY=4.75298 CenterZ=0 NormalX=0 NormalY=0 NormalZ=1 AngleXU=0 Radius=4.1
  constraints (1):
    c: Diameter(g0) = 8.2
FEATURE [PartDesign::Pocket] Pocket045
  BaseFeature = -> AdditiveLoft010
  Direction = (0.707107,0,-0.707107)
  Length = 1000
  Length2 = 5
  Profile = -> Sketch075
  ReferenceAxis = -> Sketch075 [N_Axis]
  Refine = true
  Suppressed = false
  Type = 0
FEATURE [Sketcher::SketchObject] Sketch076
  ArcFitTolerance = 1e-06
  AttachmentSupport = -> [Pocket045]
  FullyConstrained = false
  MakeInternals = false
  MapMode = 5
  Placement = pos=(0,0,-600) rot=(1,0,0;3.14159rad)
  sketch-geometry (4):
    g0: LineSegment StartX=-85.1873 StartY=206.739 StartZ=0 EndX=-85.1873 EndY=-145.098 EndZ=0
    g1: LineSegment StartX=-85.1873 StartY=-145.098 StartZ=0 EndX=963.672 EndY=-145.098 EndZ=0
    g2: LineSegment StartX=963.672 StartY=-145.098 StartZ=0 EndX=963.672 EndY=206.739 EndZ=0
    g3: LineSegment StartX=963.672 StartY=206.739 StartZ=0 EndX=-85.1873 EndY=206.739 EndZ=0
  constraints (8):
    c: Coincident(g0,g1)
    c: Coincident(g1,g2)
    c: Coincident(g2,g3)
    c: Coincident(g3,g0)
    c: Vertical(g0)
    c: Vertical(g2)
    c: Horizontal(g1)
    c: Horizontal(g3)
FEATURE [PartDesign::Pocket] Pocket046
  BaseFeature = -> Pocket045
  Direction = (0,0,1)
  Length = 590
  Length2 = 5
  Profile = -> Sketch076
  ReferenceAxis = -> Sketch076 [N_Axis]
  Refine = true
  Suppressed = false
  Type = 0
FEATURE [Sketcher::SketchObject] Sketch077
  ArcFitTolerance = 1e-06
  AttachmentSupport = -> [Pocket046]
  FullyConstrained = true
  MakeInternals = false
  MapMode = 5
  Placement = pos=(0,0,-10) rot=(1,0,0;3.14159rad)
  sketch-geometry (4):
    g0: Circle CenterX=310 CenterY=-12 CenterZ=0 NormalX=0 NormalY=0 NormalZ=1 AngleXU=0 Radius=4.1
    g1: Circle CenterX=240 CenterY=-5 CenterZ=0 NormalX=0 NormalY=0 NormalZ=1 AngleXU=0 Radius=4.1
    g2: Circle CenterX=170 CenterY=-17 CenterZ=0 NormalX=0 NormalY=0 NormalZ=1 AngleXU=0 Radius=4.1
    g3: Circle CenterX=100 CenterY=-4 CenterZ=0 NormalX=0 NormalY=0 NormalZ=1 AngleXU=0 Radius=4.1
  constraints (12):
    c: Diameter(g0) = 8.2
    c: Diameter(g1) = 8.2
    c: Diameter(g2) = 8.2
    c: Diameter(g3) = 8.2
    c: DistanceX(g-1,g3) = 100
    c: DistanceX(g3,g2) = 70
    c: DistanceX(g2,g1) = 70
    c: DistanceX(g1,g0) = 70
    c: DistanceY(g3,g-1) = 4
    c: DistanceY(g2,g-1) = 17
    c: DistanceY(g1,g-1) = 5
    c: DistanceY(g0,g-1) = 12
FEATURE [PartDesign::Pocket] Pocket047
  BaseFeature = -> Pocket046
  Direction = (0,0,1)
  Length = 15
  Length2 = 5
  Profile = -> Sketch077
  ReferenceAxis = -> Sketch077 [N_Axis]
  Refine = true
  Suppressed = false
  Type = 0
FEATURE [Sketcher::SketchObject] Sketch078
  ArcFitTolerance = 1e-06
  AttachmentSupport = -> [Pocket047]
  FullyConstrained = false
  MakeInternals = false
  MapMode = 5
  Placement = pos=(0,0,-10) rot=(1,0,0;3.14159rad)
  sketch-geometry (4):
    g0: LineSegment StartX=493.108 StartY=42.5769 StartZ=0 EndX=493.108 EndY=-78.0723 EndZ=0
    g1: LineSegment StartX=493.108 StartY=-78.0723 StartZ=0 EndX=280 EndY=-78.0723 EndZ=0
    g2: LineSegment StartX=280 StartY=-78.0723 StartZ=0 EndX=280 EndY=42.5769 EndZ=0
    g3: LineSegment StartX=280 StartY=42.5769 StartZ=0 EndX=493.108 EndY=42.5769 EndZ=0
  constraints (9):
    c: Coincident(g0,g1)
    c: Coincident(g1,g2)
    c: Coincident(g2,g3)
    c: Coincident(g3,g0)
    c: Vertical(g0)
    c: Vertical(g2)
    c: Horizontal(g1)
    c: Horizontal(g3)
    c: DistanceX(g-1,g2) = 280
FEATURE [PartDesign::Pocket] Pocket048
  BaseFeature = -> Pocket044
  Direction = (0,0,1)
  Length = 15
  Length2 = 5
  Profile = -> Sketch072
  ReferenceAxis = -> Sketch072 [N_Axis]
  Refine = true
  Suppressed = false
  Type = 0
FEATURE [PartDesign::Body] Body
  AllowCompound = false
  Group = -> [Sketch001,Sketch,AdditiveLoft,DatumPlane,Sketch002,Pocket,Sketch021,Pocket007,Sketch071,Pocket044,Sketch072,Pocket048]
  Origin = -> Origin
  Placement = pos=(0,0,-100) rot=(0,0,1;0rad)
  Tip = -> Pocket048
FEATURE [PartDesign::Pocket] Pocket049
  BaseFeature = -> Pocket047
  Direction = (0,0,1)
  Length = 15
  Length2 = 5
  Profile = -> Sketch078
  ReferenceAxis = -> Sketch078 [N_Axis]
  Refine = true
  Suppressed = false
  Type = 0
FEATURE [Part::Mirroring] Part__Mirroring  label="Body (Mirror #1)"
  Base = (0,0,0)
  Normal = (0,0,1)
  Source = -> Body
FEATURE [Part::Mirroring] Part__Mirroring002  label="Body002 (Mirror #3)"
  Base = (0,0,0)
  Normal = (0,0,1)
  Source = -> Body002
FEATURE [Part::Mirroring] Part__Mirroring003  label="Body004 (Mirror #4)"
  Base = (0,0,0)
  Normal = (0,0,1)
  Source = -> Body004
FEATURE [Part::Mirroring] Part__Mirroring004  label="Body005 (Mirror #5)"
  Base = (0,0,0)
  Normal = (0,0,1)
  Source = -> Body005
FEATURE [Part::Mirroring] Part__Mirroring005  label="Body007 (Mirror #6)"
  Base = (0,0,0)
  Normal = (0,0,1)
  Source = -> Body007
FEATURE [Part::Mirroring] Part__Mirroring007  label="Body009 (Mirror #8)"
  Base = (0,0,0)
  Normal = (0,0,1)
  Source = -> Body009
FEATURE [Part::Mirroring] Part__Mirroring008  label="Body008 (Mirror #9)"
  Base = (0,0,0)
  Normal = (0,0,1)
  Source = -> Body008
FEATURE [Part::Mirroring] Part__Mirroring009  label="Body003 (Mirror #10)"
  Base = (0,0,0)
  Normal = (0,0,1)
  Source = -> Body003
FEATURE [Part::Mirroring] Part__Mirroring010  label="Body006 (Mirror #11)"
  Base = (0,0,0)
  Normal = (0,0,1)
  Source = -> Body006
FEATURE [Sketcher::SketchObject] Sketch079
  ArcFitTolerance = 1e-06
  FullyConstrained = false
  MakeInternals = false
  Placement = pos=(600,0,-600) rot=(0,0,1;0rad)
  sketch-geometry (123):
    g0: BSplineCurve PolesCount=61 KnotsCount=61 Degree=3 IsPeriodic=1
    g1-g61: Circle [constr] x61 (B-spline internal-alignment scaffolding for g0; pole/knot coordinates omitted)
    g62-g122: GeomPoint [constr] x61 (B-spline internal-alignment scaffolding for g0; pole/knot coordinates omitted)
  constraints (123):
    c: InternalAlignment(g1,g0)
    c: Weight(g1) = 1
    c: InternalAlignment(g2,g0)
    c: Equal(g2,g1)
    c: InternalAlignment(g3,g0)
    c: Equal(g3,g1)
    c: InternalAlignment(g4,g0)
    c: Equal(g4,g1)
    c: InternalAlignment(g5,g0)
    c: Equal(g5,g1)
    c: InternalAlignment(g6,g0)
    c: Equal(g6,g1)
    c: InternalAlignment(g7,g0)
    c: Equal(g7,g1)
    c: InternalAlignment(g8,g0)
    c: Equal(g8,g1)
    c: InternalAlignment(g9,g0)
    c: Equal(g9,g1)
    c: InternalAlignment(g10,g0)
    c: Equal(g10,g1)
    c: InternalAlignment(g11,g0)
    c: Equal(g11,g1)
    c: InternalAlignment(g12,g0)
    c: Equal(g12,g1)
    c: InternalAlignment(g13,g0)
    c: Equal(g13,g1)
    c: InternalAlignment(g14,g0)
    c: Equal(g14,g1)
    c: InternalAlignment(g15,g0)
    c: Equal(g15,g1)
    c: InternalAlignment(g16,g0)
    c: Equal(g16,g1)
    c: InternalAlignment(g17,g0)
    c: Equal(g17,g1)
    c: InternalAlignment(g18,g0)
    c: Equal(g18,g1)
    c: InternalAlignment(g19,g0)
    c: Equal(g19,g1)
    c: InternalAlignment(g20,g0)
    c: Equal(g20,g1)
    c: InternalAlignment(g21,g0)
    c: Equal(g21,g1)
    c: InternalAlignment(g22,g0)
    c: Equal(g22,g1)
    c: InternalAlignment(g23,g0)
    c: Equal(g23,g1)
    c: InternalAlignment(g24,g0)
    c: Equal(g24,g1)
    c: InternalAlignment(g25,g0)
    c: Equal(g25,g1)
    c: InternalAlignment(g26,g0)
    c: Equal(g26,g1)
    c: InternalAlignment(g27,g0)
    c: Equal(g27,g1)
    c: InternalAlignment(g28,g0)
    c: Equal(g28,g1)
    c: InternalAlignment(g29,g0)
    c: Equal(g29,g1)
    c: InternalAlignment(g30,g0)
    c: Equal(g30,g1)
    c: InternalAlignment(g31,g0)
    c: Equal(g31,g1)
    c: InternalAlignment(g32,g0)
    c: Equal(g32,g1)
    c: InternalAlignment(g33,g0)
    c: Equal(g33,g1)
    c: InternalAlignment(g34,g0)
    c: Equal(g34,g1)
    c: InternalAlignment(g35,g0)
    c: Equal(g35,g1)
    c: InternalAlignment(g36,g0)
    c: Equal(g36,g1)
    c: InternalAlignment(g37,g0)
    c: Equal(g37,g1)
    c: InternalAlignment(g38,g0)
    c: Equal(g38,g1)
    c: InternalAlignment(g39,g0)
    c: Equal(g39,g1)
    c: InternalAlignment(g40,g0)
    c: Equal(g40,g1)
    c: InternalAlignment(g41,g0)
    c: Equal(g41,g1)
    c: InternalAlignment(g42,g0)
    c: Equal(g42,g1)
    c: InternalAlignment(g43,g0)
    c: Equal(g43,g1)
    c: InternalAlignment(g44,g0)
    c: Equal(g44,g1)
    c: InternalAlignment(g45,g0)
    c: Equal(g45,g1)
    c: InternalAlignment(g46,g0)
    c: Equal(g46,g1)
    c: InternalAlignment(g47,g0)
    c: Equal(g47,g1)
    c: InternalAlignment(g48,g0)
    c: Equal(g48,g1)
    c: InternalAlignment(g49,g0)
    c: Equal(g49,g1)
    c: InternalAlignment(g50,g0)
    c: Equal(g50,g1)
    c: InternalAlignment(g51,g0)
    c: Equal(g51,g1)
    c: InternalAlignment(g52,g0)
    c: Equal(g52,g1)
    c: InternalAlignment(g53,g0)
    c: Equal(g53,g1)
    c: InternalAlignment(g54,g0)
    c: Equal(g54,g1)
    c: InternalAlignment(g55,g0)
    c: Equal(g55,g1)
    c: InternalAlignment(g56,g0)
    c: Equal(g56,g1)
    c: InternalAlignment(g57,g0)
    c: Equal(g57,g1)
    c: InternalAlignment(g58,g0)
    c: Equal(g58,g1)
    c: InternalAlignment(g59,g0)
    c: Equal(g59,g1)
    c: InternalAlignment(g60,g0)
    c: Equal(g60,g1)
    c: InternalAlignment(g61,g0)
    c: Equal(g61,g1)
    c: InternalAlignment(g62-g122 -> g0) x61
FEATURE [Sketcher::SketchObject] Sketch080
  ArcFitTolerance = 1e-06
  FullyConstrained = false
  MakeInternals = false
  sketch-geometry (123):
    g0: BSplineCurve PolesCount=61 KnotsCount=61 Degree=3 IsPeriodic=1
    g1-g61: Circle [constr] x61 (B-spline internal-alignment scaffolding for g0; pole/knot coordinates omitted)
    g62-g122: GeomPoint [constr] x61 (B-spline internal-alignment scaffolding for g0; pole/knot coordinates omitted)
  constraints (123):
    c: InternalAlignment(g1,g0)
    c: Weight(g1) = 1
    c: InternalAlignment(g2,g0)
    c: Equal(g2,g1)
    c: InternalAlignment(g3,g0)
    c: Equal(g3,g1)
    c: InternalAlignment(g4,g0)
    c: Equal(g4,g1)
    c: InternalAlignment(g5,g0)
    c: Equal(g5,g1)
    c: InternalAlignment(g6,g0)
    c: Equal(g6,g1)
    c: InternalAlignment(g7,g0)
    c: Equal(g7,g1)
    c: InternalAlignment(g8,g0)
    c: Equal(g8,g1)
    c: InternalAlignment(g9,g0)
    c: Equal(g9,g1)
    c: InternalAlignment(g10,g0)
    c: Equal(g10,g1)
    c: InternalAlignment(g11,g0)
    c: Equal(g11,g1)
    c: InternalAlignment(g12,g0)
    c: Equal(g12,g1)
    c: InternalAlignment(g13,g0)
    c: Equal(g13,g1)
    c: InternalAlignment(g14,g0)
    c: Equal(g14,g1)
    c: InternalAlignment(g15,g0)
    c: Equal(g15,g1)
    c: InternalAlignment(g16,g0)
    c: Equal(g16,g1)
    c: InternalAlignment(g17,g0)
    c: Equal(g17,g1)
    c: InternalAlignment(g18,g0)
    c: Equal(g18,g1)
    c: InternalAlignment(g19,g0)
    c: Equal(g19,g1)
    c: InternalAlignment(g20,g0)
    c: Equal(g20,g1)
    c: InternalAlignment(g21,g0)
    c: Equal(g21,g1)
    c: InternalAlignment(g22,g0)
    c: Equal(g22,g1)
    c: InternalAlignment(g23,g0)
    c: Equal(g23,g1)
    c: InternalAlignment(g24,g0)
    c: Equal(g24,g1)
    c: InternalAlignment(g25,g0)
    c: Equal(g25,g1)
    c: InternalAlignment(g26,g0)
    c: Equal(g26,g1)
    c: InternalAlignment(g27,g0)
    c: Equal(g27,g1)
    c: InternalAlignment(g28,g0)
    c: Equal(g28,g1)
    c: InternalAlignment(g29,g0)
    c: Equal(g29,g1)
    c: InternalAlignment(g30,g0)
    c: Equal(g30,g1)
    c: InternalAlignment(g31,g0)
    c: Equal(g31,g1)
    c: InternalAlignment(g32,g0)
    c: Equal(g32,g1)
    c: InternalAlignment(g33,g0)
    c: Equal(g33,g1)
    c: InternalAlignment(g34,g0)
    c: Equal(g34,g1)
    c: InternalAlignment(g35,g0)
    c: Equal(g35,g1)
    c: InternalAlignment(g36,g0)
    c: Equal(g36,g1)
    c: InternalAlignment(g37,g0)
    c: Equal(g37,g1)
    c: InternalAlignment(g38,g0)
    c: Equal(g38,g1)
    c: InternalAlignment(g39,g0)
    c: Equal(g39,g1)
    c: InternalAlignment(g40,g0)
    c: Equal(g40,g1)
    c: InternalAlignment(g41,g0)
    c: Equal(g41,g1)
    c: InternalAlignment(g42,g0)
    c: Equal(g42,g1)
    c: InternalAlignment(g43,g0)
    c: Equal(g43,g1)
    c: InternalAlignment(g44,g0)
    c: Equal(g44,g1)
    c: InternalAlignment(g45,g0)
    c: Equal(g45,g1)
    c: InternalAlignment(g46,g0)
    c: Equal(g46,g1)
    c: InternalAlignment(g47,g0)
    c: Equal(g47,g1)
    c: InternalAlignment(g48,g0)
    c: Equal(g48,g1)
    c: InternalAlignment(g49,g0)
    c: Equal(g49,g1)
    c: InternalAlignment(g50,g0)
    c: Equal(g50,g1)
    c: InternalAlignment(g51,g0)
    c: Equal(g51,g1)
    c: InternalAlignment(g52,g0)
    c: Equal(g52,g1)
    c: InternalAlignment(g53,g0)
    c: Equal(g53,g1)
    c: InternalAlignment(g54,g0)
    c: Equal(g54,g1)
    c: InternalAlignment(g55,g0)
    c: Equal(g55,g1)
    c: InternalAlignment(g56,g0)
    c: Equal(g56,g1)
    c: InternalAlignment(g57,g0)
    c: Equal(g57,g1)
    c: InternalAlignment(g58,g0)
    c: Equal(g58,g1)
    c: InternalAlignment(g59,g0)
    c: Equal(g59,g1)
    c: InternalAlignment(g60,g0)
    c: Equal(g60,g1)
    c: InternalAlignment(g61,g0)
    c: Equal(g61,g1)
    c: InternalAlignment(g62-g122 -> g0) x61
FEATURE [PartDesign::AdditiveLoft] AdditiveLoft011
  Closed = false
  Profile = -> Sketch080
  Refine = true
  Ruled = false
  Sections = -> [Sketch079]
  Suppressed = false
FEATURE [Sketcher::SketchObject] Sketch081
  ArcFitTolerance = 1e-06
  AttachmentSupport = -> [AdditiveLoft011]
  FullyConstrained = false
  MakeInternals = false
  MapMode = 5
  Placement = pos=(0,0,-600) rot=(1,0,0;3.14159rad)
  sketch-geometry (4):
    g0: LineSegment StartX=-34.2169 StartY=87.65 StartZ=0 EndX=-34.2169 EndY=-91.6403 EndZ=0
    g1: LineSegment StartX=-34.2169 StartY=-91.6403 StartZ=0 EndX=961.453 EndY=-91.6403 EndZ=0
    g2: LineSegment StartX=961.453 StartY=-91.6403 StartZ=0 EndX=961.453 EndY=87.65 EndZ=0
    g3: LineSegment StartX=961.453 StartY=87.65 StartZ=0 EndX=-34.2169 EndY=87.65 EndZ=0
  constraints (8):
    c: Coincident(g0,g1)
    c: Coincident(g1,g2)
    c: Coincident(g2,g3)
    c: Coincident(g3,g0)
    c: Vertical(g0)
    c: Vertical(g2)
    c: Horizontal(g1)
    c: Horizontal(g3)
FEATURE [PartDesign::Pocket] Pocket050
  BaseFeature = -> AdditiveLoft011
  Direction = (0,0,1)
  Length = 500
  Length2 = 5
  Profile = -> Sketch081
  ReferenceAxis = -> Sketch081 [N_Axis]
  Refine = true
  Suppressed = false
  Type = 0
FEATURE [Sketcher::SketchObject] Sketch082
  ArcFitTolerance = 1e-06
  AttachmentSupport = -> [Pocket050]
  FullyConstrained = false
  MakeInternals = false
  MapMode = 5
  sketch-geometry (4):
    g0: LineSegment StartX=-133.424 StartY=119.332 StartZ=0 EndX=-133.424 EndY=-141.213 EndZ=0
    g1: LineSegment StartX=-133.424 StartY=-141.213 StartZ=0 EndX=913.95 EndY=-141.213 EndZ=0
    g2: LineSegment StartX=913.95 StartY=-141.213 StartZ=0 EndX=913.95 EndY=119.332 EndZ=0
    g3: LineSegment StartX=913.95 StartY=119.332 StartZ=0 EndX=-133.424 EndY=119.332 EndZ=0
  constraints (8):
    c: Coincident(g0,g1)
    c: Coincident(g1,g2)
    c: Coincident(g2,g3)
    c: Coincident(g3,g0)
    c: Vertical(g0)
    c: Vertical(g2)
    c: Horizontal(g1)
    c: Horizontal(g3)
FEATURE [PartDesign::Pocket] Pocket051
  BaseFeature = -> Pocket050
  Direction = (0,0,-1)
  Length = 10
  Length2 = 5
  Profile = -> Sketch082
  ReferenceAxis = -> Sketch082 [N_Axis]
  Refine = true
  Suppressed = false
  Type = 0
FEATURE [Sketcher::SketchObject] Sketch083
  ArcFitTolerance = 1e-06
  AttachmentSupport = -> [YZ_Plane011]
  FullyConstrained = false
  MakeInternals = false
  MapMode = 5
  Placement = pos=(0,0,0) rot=(0.57735,0.57735,0.57735;2.0944rad)
  sketch-geometry (4):
    g0: LineSegment StartX=66.7372 StartY=-162.427 StartZ=0 EndX=66.7372 EndY=107.718 EndZ=0
    g1: LineSegment StartX=66.7372 StartY=107.718 StartZ=0 EndX=-45.6436 EndY=107.718 EndZ=0
    g2: LineSegment StartX=-45.6436 StartY=107.718 StartZ=0 EndX=-45.6436 EndY=-162.427 EndZ=0
    g3: LineSegment StartX=-45.6436 StartY=-162.427 StartZ=0 EndX=66.7372 EndY=-162.427 EndZ=0
  constraints (8):
    c: Coincident(g0,g1)
    c: Coincident(g1,g2)
    c: Coincident(g2,g3)
    c: Coincident(g3,g0)
    c: Vertical(g0)
    c: Vertical(g2)
    c: Horizontal(g1)
    c: Horizontal(g3)
FEATURE [PartDesign::Pocket] Pocket052
  BaseFeature = -> Pocket051
  Direction = (-1,0,0)
  Length = 255
  Length2 = 5
  Profile = -> Sketch083
  ReferenceAxis = -> Sketch083 [N_Axis]
  Refine = true
  Reversed = true
  Suppressed = false
  Type = 0
FEATURE [PartDesign::Plane] DatumPlane014
  AttachmentOffset = pos=(0,0,-330) rot=(0,0,1;0rad)
  AttachmentSupport = -> [Pocket052]
  Length = 71.8463
  MapMode = 5
  Placement = pos=(585,0,0) rot=(0.57735,-0.57735,-0.57735;2.0944rad)
  ResizeMode = 0
  Width = 141.618
FEATURE [Sketcher::SketchObject] Sketch084
  ArcFitTolerance = 1e-06
  AttachmentSupport = -> [DatumPlane014]
  FullyConstrained = false
  MakeInternals = false
  MapMode = 5
  Placement = pos=(585,0,0) rot=(0.57735,-0.57735,-0.57735;2.0944rad)
  sketch-geometry (4):
    g0: LineSegment StartX=65.7357 StartY=-131.147 StartZ=0 EndX=65.7357 EndY=82.8431 EndZ=0
    g1: LineSegment StartX=65.7357 StartY=82.8431 StartZ=0 EndX=-74.5523 EndY=82.8431 EndZ=0
    g2: LineSegment StartX=-74.5523 StartY=82.8431 StartZ=0 EndX=-74.5523 EndY=-131.147 EndZ=0
    g3: LineSegment StartX=-74.5523 StartY=-131.147 StartZ=0 EndX=65.7357 EndY=-131.147 EndZ=0
  constraints (8):
    c: Coincident(g0,g1)
    c: Coincident(g1,g2)
    c: Coincident(g2,g3)
    c: Coincident(g3,g0)
    c: Vertical(g0)
    c: Vertical(g2)
    c: Horizontal(g1)
    c: Horizontal(g3)
FEATURE [PartDesign::Pocket] Pocket053
  BaseFeature = -> Pocket052
  Direction = (1,0,0)
  Length = 320
  Length2 = 5
  Profile = -> Sketch084
  ReferenceAxis = -> Sketch084 [N_Axis]
  Refine = true
  Reversed = true
  Suppressed = false
  Type = 0
FEATURE [Sketcher::SketchObject] Sketch085
  ArcFitTolerance = 1e-06
  AttachmentSupport = -> [Pocket053]
  FullyConstrained = false
  MakeInternals = false
  MapMode = 5
  Placement = pos=(255,0,0) rot=(0.57735,-0.57735,-0.57735;2.0944rad)
  sketch-geometry (12):
    g0: LineSegment StartX=-24.932 StartY=-93.1131 StartZ=0 EndX=0.892258 EndY=-93.1131 EndZ=0
    g1: LineSegment StartX=0.892258 StartY=-93.1131 StartZ=0 EndX=0.892258 EndY=-71.732 EndZ=0
    g2: LineSegment StartX=0.892258 StartY=-71.732 StartZ=0 EndX=-24.932 EndY=-54.356 EndZ=0
    g3: LineSegment StartX=-24.932 StartY=-54.356 StartZ=0 EndX=-24.932 EndY=-93.1131 EndZ=0
    g4: LineSegment StartX=-24.99 StartY=-48.0773 StartZ=0 EndX=0.577924 EndY=-65.2808 EndZ=0
    g5: LineSegment StartX=0.577924 StartY=-65.2808 StartZ=0 EndX=-0.0128357 EndY=-22.8241 EndZ=0
    g6: LineSegment StartX=-0.0128357 StartY=-22.8241 StartZ=0 EndX=-24.99 EndY=-36.9306 EndZ=0
    g7: LineSegment StartX=-24.99 StartY=-36.9306 StartZ=0 EndX=-24.99 EndY=-48.0773 EndZ=0
    g8: LineSegment StartX=-24.7701 StartY=-30.9074 StartZ=0 EndX=-0.499186 EndY=-17.1997 EndZ=0
    g9: LineSegment StartX=-0.499186 StartY=-17.1997 StartZ=0 EndX=-0.499186 EndY=-15.3406 EndZ=0
    g10: LineSegment StartX=-0.499186 StartY=-15.3406 StartZ=0 EndX=-24.7701 EndY=-15.3406 EndZ=0
    g11: LineSegment StartX=-24.7701 StartY=-15.3406 StartZ=0 EndX=-24.7701 EndY=-30.9074 EndZ=0
  constraints (21):
    c: Horizontal(g0)
    c: Coincident(g0,g1)
    c: Vertical(g1)
    c: Coincident(g1,g2)
    c: Coincident(g2,g3)
    c: Coincident(g3,g0)
    c: Vertical(g3)
    c: Coincident(g4,g5)
    c: Coincident(g5,g6)
    c: Coincident(g6,g7)
    c: Coincident(g7,g4)
    c: Vertical(g7)
    c: Coincident(g8,g9)
    c: Vertical(g9)
    c: Coincident(g9,g10)
    c: Horizontal(g10)
    c: Coincident(g10,g11)
    c: Coincident(g11,g8)
    c: Vertical(g11)
    c: Parallel(g2,g4)
    c: Parallel(g6,g8)
FEATURE [PartDesign::Pocket] Pocket054
  BaseFeature = -> Pocket053
  Direction = (1,0,0)
  Length = 15
  Length2 = 5
  Profile = -> Sketch085
  ReferenceAxis = -> Sketch085 [N_Axis]
  Refine = true
  Suppressed = false
  Type = 0
FEATURE [PartDesign::Body] Body011
  AllowCompound = false
  Group = -> [Sketch080,Sketch079,AdditiveLoft011,Sketch081,Pocket050,Sketch082,Pocket051,Sketch083,Pocket052,DatumPlane014,Sketch084,Pocket053,Sketch085,Pocket054]
  Origin = -> Origin011
  Placement = pos=(0,0,-100) rot=(0,0,1;0rad)
  Tip = -> Pocket054
FEATURE [Part::Mirroring] Part__Mirroring011  label="Body011 (Mirror #12)"
  Base = (0,0,0)
  Normal = (0,0,1)
  Source = -> Body011
FEATURE [Sketcher::SketchObject] Sketch086
  ArcFitTolerance = 1e-06
  FullyConstrained = false
  MakeInternals = false
  Placement = pos=(600,0,-600) rot=(0,0,1;0rad)
  sketch-geometry (123):
    g0: BSplineCurve PolesCount=61 KnotsCount=61 Degree=3 IsPeriodic=1
    g1-g61: Circle [constr] x61 (B-spline internal-alignment scaffolding for g0; pole/knot coordinates omitted)
    g62-g122: GeomPoint [constr] x61 (B-spline internal-alignment scaffolding for g0; pole/knot coordinates omitted)
  constraints (123):
    c: InternalAlignment(g1,g0)
    c: Weight(g1) = 1
    c: InternalAlignment(g2,g0)
    c: Equal(g2,g1)
    c: InternalAlignment(g3,g0)
    c: Equal(g3,g1)
    c: InternalAlignment(g4,g0)
    c: Equal(g4,g1)
    c: InternalAlignment(g5,g0)
    c: Equal(g5,g1)
    c: InternalAlignment(g6,g0)
    c: Equal(g6,g1)
    c: InternalAlignment(g7,g0)
    c: Equal(g7,g1)
    c: InternalAlignment(g8,g0)
    c: Equal(g8,g1)
    c: InternalAlignment(g9,g0)
    c: Equal(g9,g1)
    c: InternalAlignment(g10,g0)
    c: Equal(g10,g1)
    c: InternalAlignment(g11,g0)
    c: Equal(g11,g1)
    c: InternalAlignment(g12,g0)
    c: Equal(g12,g1)
    c: InternalAlignment(g13,g0)
    c: Equal(g13,g1)
    c: InternalAlignment(g14,g0)
    c: Equal(g14,g1)
    c: InternalAlignment(g15,g0)
    c: Equal(g15,g1)
    c: InternalAlignment(g16,g0)
    c: Equal(g16,g1)
    c: InternalAlignment(g17,g0)
    c: Equal(g17,g1)
    c: InternalAlignment(g18,g0)
    c: Equal(g18,g1)
    c: InternalAlignment(g19,g0)
    c: Equal(g19,g1)
    c: InternalAlignment(g20,g0)
    c: Equal(g20,g1)
    c: InternalAlignment(g21,g0)
    c: Equal(g21,g1)
    c: InternalAlignment(g22,g0)
    c: Equal(g22,g1)
    c: InternalAlignment(g23,g0)
    c: Equal(g23,g1)
    c: InternalAlignment(g24,g0)
    c: Equal(g24,g1)
    c: InternalAlignment(g25,g0)
    c: Equal(g25,g1)
    c: InternalAlignment(g26,g0)
    c: Equal(g26,g1)
    c: InternalAlignment(g27,g0)
    c: Equal(g27,g1)
    c: InternalAlignment(g28,g0)
    c: Equal(g28,g1)
    c: InternalAlignment(g29,g0)
    c: Equal(g29,g1)
    c: InternalAlignment(g30,g0)
    c: Equal(g30,g1)
    c: InternalAlignment(g31,g0)
    c: Equal(g31,g1)
    c: InternalAlignment(g32,g0)
    c: Equal(g32,g1)
    c: InternalAlignment(g33,g0)
    c: Equal(g33,g1)
    c: InternalAlignment(g34,g0)
    c: Equal(g34,g1)
    c: InternalAlignment(g35,g0)
    c: Equal(g35,g1)
    c: InternalAlignment(g36,g0)
    c: Equal(g36,g1)
    c: InternalAlignment(g37,g0)
    c: Equal(g37,g1)
    c: InternalAlignment(g38,g0)
    c: Equal(g38,g1)
    c: InternalAlignment(g39,g0)
    c: Equal(g39,g1)
    c: InternalAlignment(g40,g0)
    c: Equal(g40,g1)
    c: InternalAlignment(g41,g0)
    c: Equal(g41,g1)
    c: InternalAlignment(g42,g0)
    c: Equal(g42,g1)
    c: InternalAlignment(g43,g0)
    c: Equal(g43,g1)
    c: InternalAlignment(g44,g0)
    c: Equal(g44,g1)
    c: InternalAlignment(g45,g0)
    c: Equal(g45,g1)
    c: InternalAlignment(g46,g0)
    c: Equal(g46,g1)
    c: InternalAlignment(g47,g0)
    c: Equal(g47,g1)
    c: InternalAlignment(g48,g0)
    c: Equal(g48,g1)
    c: InternalAlignment(g49,g0)
    c: Equal(g49,g1)
    c: InternalAlignment(g50,g0)
    c: Equal(g50,g1)
    c: InternalAlignment(g51,g0)
    c: Equal(g51,g1)
    c: InternalAlignment(g52,g0)
    c: Equal(g52,g1)
    c: InternalAlignment(g53,g0)
    c: Equal(g53,g1)
    c: InternalAlignment(g54,g0)
    c: Equal(g54,g1)
    c: InternalAlignment(g55,g0)
    c: Equal(g55,g1)
    c: InternalAlignment(g56,g0)
    c: Equal(g56,g1)
    c: InternalAlignment(g57,g0)
    c: Equal(g57,g1)
    c: InternalAlignment(g58,g0)
    c: Equal(g58,g1)
    c: InternalAlignment(g59,g0)
    c: Equal(g59,g1)
    c: InternalAlignment(g60,g0)
    c: Equal(g60,g1)
    c: InternalAlignment(g61,g0)
    c: Equal(g61,g1)
    c: InternalAlignment(g62-g122 -> g0) x61
FEATURE [Sketcher::SketchObject] Sketch087
  ArcFitTolerance = 1e-06
  FullyConstrained = false
  MakeInternals = false
  sketch-geometry (123):
    g0: BSplineCurve PolesCount=61 KnotsCount=61 Degree=3 IsPeriodic=1
    g1-g61: Circle [constr] x61 (B-spline internal-alignment scaffolding for g0; pole/knot coordinates omitted)
    g62-g122: GeomPoint [constr] x61 (B-spline internal-alignment scaffolding for g0; pole/knot coordinates omitted)
  constraints (123):
    c: InternalAlignment(g1,g0)
    c: Weight(g1) = 1
    c: InternalAlignment(g2,g0)
    c: Equal(g2,g1)
    c: InternalAlignment(g3,g0)
    c: Equal(g3,g1)
    c: InternalAlignment(g4,g0)
    c: Equal(g4,g1)
    c: InternalAlignment(g5,g0)
    c: Equal(g5,g1)
    c: InternalAlignment(g6,g0)
    c: Equal(g6,g1)
    c: InternalAlignment(g7,g0)
    c: Equal(g7,g1)
    c: InternalAlignment(g8,g0)
    c: Equal(g8,g1)
    c: InternalAlignment(g9,g0)
    c: Equal(g9,g1)
    c: InternalAlignment(g10,g0)
    c: Equal(g10,g1)
    c: InternalAlignment(g11,g0)
    c: Equal(g11,g1)
    c: InternalAlignment(g12,g0)
    c: Equal(g12,g1)
    c: InternalAlignment(g13,g0)
    c: Equal(g13,g1)
    c: InternalAlignment(g14,g0)
    c: Equal(g14,g1)
    c: InternalAlignment(g15,g0)
    c: Equal(g15,g1)
    c: InternalAlignment(g16,g0)
    c: Equal(g16,g1)
    c: InternalAlignment(g17,g0)
    c: Equal(g17,g1)
    c: InternalAlignment(g18,g0)
    c: Equal(g18,g1)
    c: InternalAlignment(g19,g0)
    c: Equal(g19,g1)
    c: InternalAlignment(g20,g0)
    c: Equal(g20,g1)
    c: InternalAlignment(g21,g0)
    c: Equal(g21,g1)
    c: InternalAlignment(g22,g0)
    c: Equal(g22,g1)
    c: InternalAlignment(g23,g0)
    c: Equal(g23,g1)
    c: InternalAlignment(g24,g0)
    c: Equal(g24,g1)
    c: InternalAlignment(g25,g0)
    c: Equal(g25,g1)
    c: InternalAlignment(g26,g0)
    c: Equal(g26,g1)
    c: InternalAlignment(g27,g0)
    c: Equal(g27,g1)
    c: InternalAlignment(g28,g0)
    c: Equal(g28,g1)
    c: InternalAlignment(g29,g0)
    c: Equal(g29,g1)
    c: InternalAlignment(g30,g0)
    c: Equal(g30,g1)
    c: InternalAlignment(g31,g0)
    c: Equal(g31,g1)
    c: InternalAlignment(g32,g0)
    c: Equal(g32,g1)
    c: InternalAlignment(g33,g0)
    c: Equal(g33,g1)
    c: InternalAlignment(g34,g0)
    c: Equal(g34,g1)
    c: InternalAlignment(g35,g0)
    c: Equal(g35,g1)
    c: InternalAlignment(g36,g0)
    c: Equal(g36,g1)
    c: InternalAlignment(g37,g0)
    c: Equal(g37,g1)
    c: InternalAlignment(g38,g0)
    c: Equal(g38,g1)
    c: InternalAlignment(g39,g0)
    c: Equal(g39,g1)
    c: InternalAlignment(g40,g0)
    c: Equal(g40,g1)
    c: InternalAlignment(g41,g0)
    c: Equal(g41,g1)
    c: InternalAlignment(g42,g0)
    c: Equal(g42,g1)
    c: InternalAlignment(g43,g0)
    c: Equal(g43,g1)
    c: InternalAlignment(g44,g0)
    c: Equal(g44,g1)
    c: InternalAlignment(g45,g0)
    c: Equal(g45,g1)
    c: InternalAlignment(g46,g0)
    c: Equal(g46,g1)
    c: InternalAlignment(g47,g0)
    c: Equal(g47,g1)
    c: InternalAlignment(g48,g0)
    c: Equal(g48,g1)
    c: InternalAlignment(g49,g0)
    c: Equal(g49,g1)
    c: InternalAlignment(g50,g0)
    c: Equal(g50,g1)
    c: InternalAlignment(g51,g0)
    c: Equal(g51,g1)
    c: InternalAlignment(g52,g0)
    c: Equal(g52,g1)
    c: InternalAlignment(g53,g0)
    c: Equal(g53,g1)
    c: InternalAlignment(g54,g0)
    c: Equal(g54,g1)
    c: InternalAlignment(g55,g0)
    c: Equal(g55,g1)
    c: InternalAlignment(g56,g0)
    c: Equal(g56,g1)
    c: InternalAlignment(g57,g0)
    c: Equal(g57,g1)
    c: InternalAlignment(g58,g0)
    c: Equal(g58,g1)
    c: InternalAlignment(g59,g0)
    c: Equal(g59,g1)
    c: InternalAlignment(g60,g0)
    c: Equal(g60,g1)
    c: InternalAlignment(g61,g0)
    c: Equal(g61,g1)
    c: InternalAlignment(g62-g122 -> g0) x61
FEATURE [PartDesign::AdditiveLoft] AdditiveLoft012
  Closed = false
  Profile = -> Sketch087
  Refine = true
  Ruled = false
  Sections = -> [Sketch086]
  Suppressed = false
FEATURE [Sketcher::SketchObject] Sketch088
  ArcFitTolerance = 1e-06
  AttachmentSupport = -> [AdditiveLoft012]
  FullyConstrained = false
  MakeInternals = false
  MapMode = 5
  Placement = pos=(0,0,-600) rot=(1,0,0;3.14159rad)
  sketch-geometry (4):
    g0: LineSegment StartX=-34.2169 StartY=87.65 StartZ=0 EndX=-34.2169 EndY=-91.6403 EndZ=0
    g1: LineSegment StartX=-34.2169 StartY=-91.6403 StartZ=0 EndX=961.453 EndY=-91.6403 EndZ=0
    g2: LineSegment StartX=961.453 StartY=-91.6403 StartZ=0 EndX=961.453 EndY=87.65 EndZ=0
    g3: LineSegment StartX=961.453 StartY=87.65 StartZ=0 EndX=-34.2169 EndY=87.65 EndZ=0
  constraints (8):
    c: Coincident(g0,g1)
    c: Coincident(g1,g2)
    c: Coincident(g2,g3)
    c: Coincident(g3,g0)
    c: Vertical(g0)
    c: Vertical(g2)
    c: Horizontal(g1)
    c: Horizontal(g3)
FEATURE [PartDesign::Pocket] Pocket055
  BaseFeature = -> AdditiveLoft012
  Direction = (0,0,1)
  Length = 400
  Length2 = 5
  Profile = -> Sketch088
  ReferenceAxis = -> Sketch088 [N_Axis]
  Refine = true
  Suppressed = false
  Type = 0
FEATURE [Sketcher::SketchObject] Sketch089
  ArcFitTolerance = 1e-06
  AttachmentSupport = -> [Pocket055]
  FullyConstrained = false
  MakeInternals = false
  MapMode = 5
  sketch-geometry (4):
    g0: LineSegment StartX=-133.424 StartY=119.332 StartZ=0 EndX=-133.424 EndY=-141.213 EndZ=0
    g1: LineSegment StartX=-133.424 StartY=-141.213 StartZ=0 EndX=913.95 EndY=-141.213 EndZ=0
    g2: LineSegment StartX=913.95 StartY=-141.213 StartZ=0 EndX=913.95 EndY=119.332 EndZ=0
    g3: LineSegment StartX=913.95 StartY=119.332 StartZ=0 EndX=-133.424 EndY=119.332 EndZ=0
  constraints (8):
    c: Coincident(g0,g1)
    c: Coincident(g1,g2)
    c: Coincident(g2,g3)
    c: Coincident(g3,g0)
    c: Vertical(g0)
    c: Vertical(g2)
    c: Horizontal(g1)
    c: Horizontal(g3)
FEATURE [PartDesign::Pocket] Pocket056
  BaseFeature = -> Pocket055
  Direction = (0,0,-1)
  Length = 110
  Length2 = 5
  Profile = -> Sketch089
  ReferenceAxis = -> Sketch089 [N_Axis]
  Refine = true
  Suppressed = false
  Type = 0
FEATURE [Sketcher::SketchObject] Sketch090
  ArcFitTolerance = 1e-06
  AttachmentSupport = -> [YZ_Plane012]
  FullyConstrained = false
  MakeInternals = false
  MapMode = 5
  Placement = pos=(0,0,0) rot=(0.57735,0.57735,0.57735;2.0944rad)
  sketch-geometry (4):
    g0: LineSegment StartX=92.8096 StartY=-273.148 StartZ=0 EndX=92.8096 EndY=-52.5871 EndZ=0
    g1: LineSegment StartX=92.8096 StartY=-52.5871 StartZ=0 EndX=-60.8393 EndY=-52.5871 EndZ=0
    g2: LineSegment StartX=-60.8393 StartY=-52.5871 StartZ=0 EndX=-60.8393 EndY=-273.148 EndZ=0
    g3: LineSegment StartX=-60.8393 StartY=-273.148 StartZ=0 EndX=92.8096 EndY=-273.148 EndZ=0
  constraints (8):
    c: Coincident(g0,g1)
    c: Coincident(g1,g2)
    c: Coincident(g2,g3)
    c: Coincident(g3,g0)
    c: Vertical(g0)
    c: Vertical(g2)
    c: Horizontal(g1)
    c: Horizontal(g3)
FEATURE [PartDesign::Pocket] Pocket057
  BaseFeature = -> Pocket056
  Direction = (-1,0,0)
  Length = 350
  Length2 = 5
  Profile = -> Sketch090
  ReferenceAxis = -> Sketch090 [N_Axis]
  Refine = true
  Reversed = true
  Suppressed = false
  Type = 0
FEATURE [PartDesign::Plane] DatumPlane015
  AttachmentOffset = pos=(0,0,-251) rot=(0,0,1;0rad)
  AttachmentSupport = -> [Pocket057]
  Length = 73.8633
  MapMode = 5
  Placement = pos=(601,0,0) rot=(0.57735,-0.57735,-0.57735;2.0944rad)
  ResizeMode = 0
  Width = 246.673
FEATURE [Sketcher::SketchObject] Sketch091
  ArcFitTolerance = 1e-06
  AttachmentSupport = -> [DatumPlane015]
  FullyConstrained = false
  MakeInternals = false
  MapMode = 5
  Placement = pos=(601,0,0) rot=(0.57735,-0.57735,-0.57735;2.0944rad)
  sketch-geometry (4):
    g0: LineSegment StartX=-116.975 StartY=-27.6569 StartZ=0 EndX=-116.975 EndY=-244.512 EndZ=0
    g1: LineSegment StartX=-116.975 StartY=-244.512 StartZ=0 EndX=135.226 EndY=-244.512 EndZ=0
    g2: LineSegment StartX=135.226 StartY=-244.512 StartZ=0 EndX=135.226 EndY=-27.6569 EndZ=0
    g3: LineSegment StartX=135.226 StartY=-27.6569 StartZ=0 EndX=-116.975 EndY=-27.6569 EndZ=0
  constraints (8):
    c: Coincident(g0,g1)
    c: Coincident(g1,g2)
    c: Coincident(g2,g3)
    c: Coincident(g3,g0)
    c: Vertical(g0)
    c: Vertical(g2)
    c: Horizontal(g1)
    c: Horizontal(g3)
FEATURE [PartDesign::Pocket] Pocket058
  BaseFeature = -> Pocket057
  Direction = (1,0,0)
  Length = 241
  Length2 = 5
  Profile = -> Sketch091
  ReferenceAxis = -> Sketch091 [N_Axis]
  Refine = true
  Reversed = true
  Suppressed = false
  Type = 0
FEATURE [Sketcher::SketchObject] Sketch092
  ArcFitTolerance = 1e-06
  AttachmentSupport = -> [Pocket058]
  FullyConstrained = false
  MakeInternals = false
  MapMode = 5
  Placement = pos=(350,0,0) rot=(0.57735,-0.57735,-0.57735;2.0944rad)
  sketch-geometry (17):
    g0: LineSegment StartX=-23.3026 StartY=-193.686 StartZ=0 EndX=1.13193 EndY=-193.686 EndZ=0
    g1: LineSegment StartX=1.13193 StartY=-193.686 StartZ=0 EndX=0.798077 EndY=-178.345 EndZ=0
    g2: LineSegment StartX=0.798077 StartY=-178.345 StartZ=0 EndX=-22.6141 EndY=-163.361 EndZ=0
    g3: LineSegment StartX=-22.6141 StartY=-163.361 StartZ=0 EndX=-22.9867 EndY=-174.579 EndZ=0
    g4: LineSegment StartX=-22.9867 StartY=-174.579 StartZ=0 EndX=-23.1973 EndY=-186.264 EndZ=0
    g5: LineSegment StartX=-23.1973 StartY=-186.264 StartZ=0 EndX=-23.3026 EndY=-193.686 EndZ=0
    g6: LineSegment StartX=-22.6159 StartY=-157.625 StartZ=0 EndX=0.686891 EndY=-172.539 EndZ=0
    g7: LineSegment StartX=0.686891 StartY=-172.539 StartZ=0 EndX=0.627789 EndY=-148.397 EndZ=0
    g8: LineSegment StartX=0.627789 StartY=-148.397 StartZ=0 EndX=0.285187 EndY=-126.491 EndZ=0
    g9: LineSegment StartX=0.285187 StartY=-126.491 StartZ=0 EndX=-22.1861 EndY=-137.858 EndZ=0
    g10: LineSegment StartX=-22.1861 StartY=-137.858 StartZ=0 EndX=-22.2474 EndY=-145.466 EndZ=0
    g11: LineSegment StartX=-22.2474 StartY=-145.466 StartZ=0 EndX=-22.6159 EndY=-157.625 EndZ=0
    g12: LineSegment StartX=-22.0247 StartY=-132.621 StartZ=0 EndX=0.194876 EndY=-121.38 EndZ=0
    g13: LineSegment StartX=0.194876 StartY=-121.38 StartZ=0 EndX=0.1494 EndY=-115.337 EndZ=0
    g14: LineSegment StartX=0.1494 StartY=-115.337 StartZ=0 EndX=-21.415 EndY=-115.337 EndZ=0
    g15: LineSegment StartX=-21.415 StartY=-115.337 StartZ=0 EndX=-21.551 EndY=-121.409 EndZ=0
    g16: LineSegment StartX=-21.551 StartY=-121.409 StartZ=0 EndX=-22.0247 EndY=-132.621 EndZ=0
  constraints (21):
    c: Horizontal(g0)
    c: Coincident(g0,g1)
    c: Coincident(g1,g2)
    c: Coincident(g2,g3)
    c: Coincident(g3,g4)
    c: Coincident(g4,g5)
    c: Coincident(g5,g0)
    c: Coincident(g6,g7)
    c: Coincident(g7,g8)
    c: Coincident(g8,g9)
    c: Coincident(g9,g10)
    c: Coincident(g10,g11)
    c: Coincident(g11,g6)
    c: Coincident(g12,g13)
    c: Coincident(g13,g14)
    c: Horizontal(g14)
    c: Coincident(g14,g15)
    c: Coincident(g15,g16)
    c: Coincident(g16,g12)
    c: Parallel(g2,g6)
    c: Parallel(g9,g12)
FEATURE [PartDesign::Pocket] Pocket059
  BaseFeature = -> Pocket058
  Direction = (1,0,0)
  Length = 15
  Length2 = 5
  Profile = -> Sketch092
  ReferenceAxis = -> Sketch092 [N_Axis]
  Refine = true
  Suppressed = false
  Type = 0
FEATURE [PartDesign::Body] Body012
  AllowCompound = false
  Group = -> [Sketch087,Sketch086,AdditiveLoft012,Sketch088,Pocket055,Sketch089,Pocket056,Sketch090,Pocket057,DatumPlane015,Sketch091,Pocket058,Sketch092,Pocket059]
  Origin = -> Origin012
  Placement = pos=(0,0,-100) rot=(0,0,1;0rad)
  Tip = -> Pocket059
FEATURE [Part::Mirroring] Part__Mirroring012  label="Body012 (Mirror #13)"
  Base = (0,0,0)
  Normal = (0,0,1)
  Source = -> Body012
FEATURE [Sketcher::SketchObject] Sketch093
  ArcFitTolerance = 1e-06
  FullyConstrained = false
  MakeInternals = false
  Placement = pos=(600,0,-600) rot=(0,0,1;0rad)
  sketch-geometry (123):
    g0: BSplineCurve PolesCount=61 KnotsCount=61 Degree=3 IsPeriodic=1
    g1-g61: Circle [constr] x61 (B-spline internal-alignment scaffolding for g0; pole/knot coordinates omitted)
    g62-g122: GeomPoint [constr] x61 (B-spline internal-alignment scaffolding for g0; pole/knot coordinates omitted)
  constraints (123):
    c: InternalAlignment(g1,g0)
    c: Weight(g1) = 1
    c: InternalAlignment(g2,g0)
    c: Equal(g2,g1)
    c: InternalAlignment(g3,g0)
    c: Equal(g3,g1)
    c: InternalAlignment(g4,g0)
    c: Equal(g4,g1)
    c: InternalAlignment(g5,g0)
    c: Equal(g5,g1)
    c: InternalAlignment(g6,g0)
    c: Equal(g6,g1)
    c: InternalAlignment(g7,g0)
    c: Equal(g7,g1)
    c: InternalAlignment(g8,g0)
    c: Equal(g8,g1)
    c: InternalAlignment(g9,g0)
    c: Equal(g9,g1)
    c: InternalAlignment(g10,g0)
    c: Equal(g10,g1)
    c: InternalAlignment(g11,g0)
    c: Equal(g11,g1)
    c: InternalAlignment(g12,g0)
    c: Equal(g12,g1)
    c: InternalAlignment(g13,g0)
    c: Equal(g13,g1)
    c: InternalAlignment(g14,g0)
    c: Equal(g14,g1)
    c: InternalAlignment(g15,g0)
    c: Equal(g15,g1)
    c: InternalAlignment(g16,g0)
    c: Equal(g16,g1)
    c: InternalAlignment(g17,g0)
    c: Equal(g17,g1)
    c: InternalAlignment(g18,g0)
    c: Equal(g18,g1)
    c: InternalAlignment(g19,g0)
    c: Equal(g19,g1)
    c: InternalAlignment(g20,g0)
    c: Equal(g20,g1)
    c: InternalAlignment(g21,g0)
    c: Equal(g21,g1)
    c: InternalAlignment(g22,g0)
    c: Equal(g22,g1)
    c: InternalAlignment(g23,g0)
    c: Equal(g23,g1)
    c: InternalAlignment(g24,g0)
    c: Equal(g24,g1)
    c: InternalAlignment(g25,g0)
    c: Equal(g25,g1)
    c: InternalAlignment(g26,g0)
    c: Equal(g26,g1)
    c: InternalAlignment(g27,g0)
    c: Equal(g27,g1)
    c: InternalAlignment(g28,g0)
    c: Equal(g28,g1)
    c: InternalAlignment(g29,g0)
    c: Equal(g29,g1)
    c: InternalAlignment(g30,g0)
    c: Equal(g30,g1)
    c: InternalAlignment(g31,g0)
    c: Equal(g31,g1)
    c: InternalAlignment(g32,g0)
    c: Equal(g32,g1)
    c: InternalAlignment(g33,g0)
    c: Equal(g33,g1)
    c: InternalAlignment(g34,g0)
    c: Equal(g34,g1)
    c: InternalAlignment(g35,g0)
    c: Equal(g35,g1)
    c: InternalAlignment(g36,g0)
    c: Equal(g36,g1)
    c: InternalAlignment(g37,g0)
    c: Equal(g37,g1)
    c: InternalAlignment(g38,g0)
    c: Equal(g38,g1)
    c: InternalAlignment(g39,g0)
    c: Equal(g39,g1)
    c: InternalAlignment(g40,g0)
    c: Equal(g40,g1)
    c: InternalAlignment(g41,g0)
    c: Equal(g41,g1)
    c: InternalAlignment(g42,g0)
    c: Equal(g42,g1)
    c: InternalAlignment(g43,g0)
    c: Equal(g43,g1)
    c: InternalAlignment(g44,g0)
    c: Equal(g44,g1)
    c: InternalAlignment(g45,g0)
    c: Equal(g45,g1)
    c: InternalAlignment(g46,g0)
    c: Equal(g46,g1)
    c: InternalAlignment(g47,g0)
    c: Equal(g47,g1)
    c: InternalAlignment(g48,g0)
    c: Equal(g48,g1)
    c: InternalAlignment(g49,g0)
    c: Equal(g49,g1)
    c: InternalAlignment(g50,g0)
    c: Equal(g50,g1)
    c: InternalAlignment(g51,g0)
    c: Equal(g51,g1)
    c: InternalAlignment(g52,g0)
    c: Equal(g52,g1)
    c: InternalAlignment(g53,g0)
    c: Equal(g53,g1)
    c: InternalAlignment(g54,g0)
    c: Equal(g54,g1)
    c: InternalAlignment(g55,g0)
    c: Equal(g55,g1)
    c: InternalAlignment(g56,g0)
    c: Equal(g56,g1)
    c: InternalAlignment(g57,g0)
    c: Equal(g57,g1)
    c: InternalAlignment(g58,g0)
    c: Equal(g58,g1)
    c: InternalAlignment(g59,g0)
    c: Equal(g59,g1)
    c: InternalAlignment(g60,g0)
    c: Equal(g60,g1)
    c: InternalAlignment(g61,g0)
    c: Equal(g61,g1)
    c: InternalAlignment(g62-g122 -> g0) x61
FEATURE [Sketcher::SketchObject] Sketch094
  ArcFitTolerance = 1e-06
  FullyConstrained = false
  MakeInternals = false
  sketch-geometry (123):
    g0: BSplineCurve PolesCount=61 KnotsCount=61 Degree=3 IsPeriodic=1
    g1-g61: Circle [constr] x61 (B-spline internal-alignment scaffolding for g0; pole/knot coordinates omitted)
    g62-g122: GeomPoint [constr] x61 (B-spline internal-alignment scaffolding for g0; pole/knot coordinates omitted)
  constraints (123):
    c: InternalAlignment(g1,g0)
    c: Weight(g1) = 1
    c: InternalAlignment(g2,g0)
    c: Equal(g2,g1)
    c: InternalAlignment(g3,g0)
    c: Equal(g3,g1)
    c: InternalAlignment(g4,g0)
    c: Equal(g4,g1)
    c: InternalAlignment(g5,g0)
    c: Equal(g5,g1)
    c: InternalAlignment(g6,g0)
    c: Equal(g6,g1)
    c: InternalAlignment(g7,g0)
    c: Equal(g7,g1)
    c: InternalAlignment(g8,g0)
    c: Equal(g8,g1)
    c: InternalAlignment(g9,g0)
    c: Equal(g9,g1)
    c: InternalAlignment(g10,g0)
    c: Equal(g10,g1)
    c: InternalAlignment(g11,g0)
    c: Equal(g11,g1)
    c: InternalAlignment(g12,g0)
    c: Equal(g12,g1)
    c: InternalAlignment(g13,g0)
    c: Equal(g13,g1)
    c: InternalAlignment(g14,g0)
    c: Equal(g14,g1)
    c: InternalAlignment(g15,g0)
    c: Equal(g15,g1)
    c: InternalAlignment(g16,g0)
    c: Equal(g16,g1)
    c: InternalAlignment(g17,g0)
    c: Equal(g17,g1)
    c: InternalAlignment(g18,g0)
    c: Equal(g18,g1)
    c: InternalAlignment(g19,g0)
    c: Equal(g19,g1)
    c: InternalAlignment(g20,g0)
    c: Equal(g20,g1)
    c: InternalAlignment(g21,g0)
    c: Equal(g21,g1)
    c: InternalAlignment(g22,g0)
    c: Equal(g22,g1)
    c: InternalAlignment(g23,g0)
    c: Equal(g23,g1)
    c: InternalAlignment(g24,g0)
    c: Equal(g24,g1)
    c: InternalAlignment(g25,g0)
    c: Equal(g25,g1)
    c: InternalAlignment(g26,g0)
    c: Equal(g26,g1)
    c: InternalAlignment(g27,g0)
    c: Equal(g27,g1)
    c: InternalAlignment(g28,g0)
    c: Equal(g28,g1)
    c: InternalAlignment(g29,g0)
    c: Equal(g29,g1)
    c: InternalAlignment(g30,g0)
    c: Equal(g30,g1)
    c: InternalAlignment(g31,g0)
    c: Equal(g31,g1)
    c: InternalAlignment(g32,g0)
    c: Equal(g32,g1)
    c: InternalAlignment(g33,g0)
    c: Equal(g33,g1)
    c: InternalAlignment(g34,g0)
    c: Equal(g34,g1)
    c: InternalAlignment(g35,g0)
    c: Equal(g35,g1)
    c: InternalAlignment(g36,g0)
    c: Equal(g36,g1)
    c: InternalAlignment(g37,g0)
    c: Equal(g37,g1)
    c: InternalAlignment(g38,g0)
    c: Equal(g38,g1)
    c: InternalAlignment(g39,g0)
    c: Equal(g39,g1)
    c: InternalAlignment(g40,g0)
    c: Equal(g40,g1)
    c: InternalAlignment(g41,g0)
    c: Equal(g41,g1)
    c: InternalAlignment(g42,g0)
    c: Equal(g42,g1)
    c: InternalAlignment(g43,g0)
    c: Equal(g43,g1)
    c: InternalAlignment(g44,g0)
    c: Equal(g44,g1)
    c: InternalAlignment(g45,g0)
    c: Equal(g45,g1)
    c: InternalAlignment(g46,g0)
    c: Equal(g46,g1)
    c: InternalAlignment(g47,g0)
    c: Equal(g47,g1)
    c: InternalAlignment(g48,g0)
    c: Equal(g48,g1)
    c: InternalAlignment(g49,g0)
    c: Equal(g49,g1)
    c: InternalAlignment(g50,g0)
    c: Equal(g50,g1)
    c: InternalAlignment(g51,g0)
    c: Equal(g51,g1)
    c: InternalAlignment(g52,g0)
    c: Equal(g52,g1)
    c: InternalAlignment(g53,g0)
    c: Equal(g53,g1)
    c: InternalAlignment(g54,g0)
    c: Equal(g54,g1)
    c: InternalAlignment(g55,g0)
    c: Equal(g55,g1)
    c: InternalAlignment(g56,g0)
    c: Equal(g56,g1)
    c: InternalAlignment(g57,g0)
    c: Equal(g57,g1)
    c: InternalAlignment(g58,g0)
    c: Equal(g58,g1)
    c: InternalAlignment(g59,g0)
    c: Equal(g59,g1)
    c: InternalAlignment(g60,g0)
    c: Equal(g60,g1)
    c: InternalAlignment(g61,g0)
    c: Equal(g61,g1)
    c: InternalAlignment(g62-g122 -> g0) x61
FEATURE [PartDesign::AdditiveLoft] AdditiveLoft013
  Closed = false
  Profile = -> Sketch094
  Refine = true
  Ruled = false
  Sections = -> [Sketch093]
  Suppressed = false
FEATURE [Sketcher::SketchObject] Sketch095
  ArcFitTolerance = 1e-06
  AttachmentSupport = -> [AdditiveLoft013]
  FullyConstrained = false
  MakeInternals = false
  MapMode = 5
  Placement = pos=(0,0,-600) rot=(1,0,0;3.14159rad)
  sketch-geometry (4):
    g0: LineSegment StartX=-34.2169 StartY=87.65 StartZ=0 EndX=-34.2169 EndY=-91.6403 EndZ=0
    g1: LineSegment StartX=-34.2169 StartY=-91.6403 StartZ=0 EndX=961.453 EndY=-91.6403 EndZ=0
    g2: LineSegment StartX=961.453 StartY=-91.6403 StartZ=0 EndX=961.453 EndY=87.65 EndZ=0
    g3: LineSegment StartX=961.453 StartY=87.65 StartZ=0 EndX=-34.2169 EndY=87.65 EndZ=0
  constraints (8):
    c: Coincident(g0,g1)
    c: Coincident(g1,g2)
    c: Coincident(g2,g3)
    c: Coincident(g3,g0)
    c: Vertical(g0)
    c: Vertical(g2)
    c: Horizontal(g1)
    c: Horizontal(g3)
FEATURE [PartDesign::Pocket] Pocket060
  BaseFeature = -> AdditiveLoft013
  Direction = (0,0,1)
  Length = 300
  Length2 = 5
  Profile = -> Sketch095
  ReferenceAxis = -> Sketch095 [N_Axis]
  Refine = true
  Suppressed = false
  Type = 0
FEATURE [Sketcher::SketchObject] Sketch096
  ArcFitTolerance = 1e-06
  AttachmentSupport = -> [Pocket060]
  FullyConstrained = false
  MakeInternals = false
  MapMode = 5
  sketch-geometry (4):
    g0: LineSegment StartX=-133.424 StartY=119.332 StartZ=0 EndX=-133.424 EndY=-141.213 EndZ=0
    g1: LineSegment StartX=-133.424 StartY=-141.213 StartZ=0 EndX=913.95 EndY=-141.213 EndZ=0
    g2: LineSegment StartX=913.95 StartY=-141.213 StartZ=0 EndX=913.95 EndY=119.332 EndZ=0
    g3: LineSegment StartX=913.95 StartY=119.332 StartZ=0 EndX=-133.424 EndY=119.332 EndZ=0
  constraints (8):
    c: Coincident(g0,g1)
    c: Coincident(g1,g2)
    c: Coincident(g2,g3)
    c: Coincident(g3,g0)
    c: Vertical(g0)
    c: Vertical(g2)
    c: Horizontal(g1)
    c: Horizontal(g3)
FEATURE [PartDesign::Pocket] Pocket061
  BaseFeature = -> Pocket060
  Direction = (0,0,-1)
  Length = 210
  Length2 = 5
  Profile = -> Sketch096
  ReferenceAxis = -> Sketch096 [N_Axis]
  Refine = true
  Suppressed = false
  Type = 0
FEATURE [Sketcher::SketchObject] Sketch097
  ArcFitTolerance = 1e-06
  AttachmentSupport = -> [YZ_Plane013]
  FullyConstrained = false
  MakeInternals = false
  MapMode = 5
  Placement = pos=(0,0,0) rot=(0.57735,0.57735,0.57735;2.0944rad)
  sketch-geometry (4):
    g0: LineSegment StartX=-70.2384 StartY=-113.861 StartZ=0 EndX=-70.2384 EndY=-349.961 EndZ=0
    g1: LineSegment StartX=-70.2384 StartY=-349.961 StartZ=0 EndX=120.732 EndY=-349.961 EndZ=0
    g2: LineSegment StartX=120.732 StartY=-349.961 StartZ=0 EndX=120.732 EndY=-113.861 EndZ=0
    g3: LineSegment StartX=120.732 StartY=-113.861 StartZ=0 EndX=-70.2384 EndY=-113.861 EndZ=0
  constraints (8):
    c: Coincident(g0,g1)
    c: Coincident(g1,g2)
    c: Coincident(g2,g3)
    c: Coincident(g3,g0)
    c: Vertical(g0)
    c: Vertical(g2)
    c: Horizontal(g1)
    c: Horizontal(g3)
FEATURE [PartDesign::Pocket] Pocket062
  BaseFeature = -> Pocket061
  Direction = (-1,0,0)
  Length = 450
  Length2 = 5
  Profile = -> Sketch097
  ReferenceAxis = -> Sketch097 [N_Axis]
  Refine = true
  Reversed = true
  Suppressed = false
  Type = 0
FEATURE [PartDesign::Plane] DatumPlane016
  AttachmentOffset = pos=(0,0,-200) rot=(0,0,1;0rad)
  AttachmentSupport = -> [Pocket062]
  Length = 75.4951
  MapMode = 5
  Placement = pos=(650,0,0) rot=(0.57735,-0.57735,-0.57735;2.0944rad)
  ResizeMode = 0
  Width = 350.495
FEATURE [Sketcher::SketchObject] Sketch098
  ArcFitTolerance = 1e-06
  AttachmentSupport = -> [DatumPlane016]
  FullyConstrained = false
  MakeInternals = false
  MapMode = 5
  Placement = pos=(650,0,0) rot=(0.57735,-0.57735,-0.57735;2.0944rad)
  sketch-geometry (4):
    g0: LineSegment StartX=-61.1524 StartY=-155.39 StartZ=0 EndX=-61.1524 EndY=-324.593 EndZ=0
    g1: LineSegment StartX=-61.1524 StartY=-324.593 StartZ=0 EndX=77.808 EndY=-324.593 EndZ=0
    g2: LineSegment StartX=77.808 StartY=-324.593 StartZ=0 EndX=77.808 EndY=-155.39 EndZ=0
    g3: LineSegment StartX=77.808 StartY=-155.39 StartZ=0 EndX=-61.1524 EndY=-155.39 EndZ=0
  constraints (8):
    c: Coincident(g0,g1)
    c: Coincident(g1,g2)
    c: Coincident(g2,g3)
    c: Coincident(g3,g0)
    c: Vertical(g0)
    c: Vertical(g2)
    c: Horizontal(g1)
    c: Horizontal(g3)
FEATURE [PartDesign::Pocket] Pocket063
  BaseFeature = -> Pocket062
  Direction = (1,0,0)
  Length = 190
  Length2 = 5
  Profile = -> Sketch098
  ReferenceAxis = -> Sketch098 [N_Axis]
  Refine = true
  Reversed = true
  Suppressed = false
  Type = 0
FEATURE [Sketcher::SketchObject] Sketch099
  ArcFitTolerance = 1e-06
  AttachmentSupport = -> [Pocket063]
  FullyConstrained = false
  MakeInternals = false
  MapMode = 5
  Placement = pos=(450,0,0) rot=(0.57735,-0.57735,-0.57735;2.0944rad)
  sketch-geometry (19):
    g0: LineSegment StartX=-0.014802 StartY=-294.817 StartZ=0 EndX=-20.3991 EndY=-294.817 EndZ=0
    g1: LineSegment StartX=-20.3991 StartY=-294.817 StartZ=0 EndX=-19.6339 EndY=-278.452 EndZ=0
    g2: LineSegment StartX=-0.014802 StartY=-294.817 StartZ=0 EndX=0.341582 EndY=-275.2 EndZ=0
    g3: LineSegment StartX=0.341582 StartY=-275.2 StartZ=0 EndX=-19.1389 EndY=-263.433 EndZ=0
    g4: LineSegment StartX=-19.1389 StartY=-263.433 StartZ=0 EndX=-19.6339 EndY=-278.452 EndZ=0
    g5: LineSegment StartX=-0.339053 StartY=-269.441 StartZ=0 EndX=-18.7945 EndY=-258.294 EndZ=0
    g6: LineSegment StartX=-18.7945 StartY=-258.294 StartZ=0 EndX=-18.337 EndY=-249.039 EndZ=0
    g7: LineSegment StartX=-18.337 StartY=-249.039 StartZ=0 EndX=-17.9338 EndY=-237.967 EndZ=0
    g8: LineSegment StartX=-17.9338 StartY=-237.967 StartZ=0 EndX=-1.22662 EndY=-228.157 EndZ=0
    g9: LineSegment StartX=-1.22662 StartY=-228.157 StartZ=0 EndX=-0.862115 EndY=-245.611 EndZ=0
    g10: LineSegment StartX=-0.862115 StartY=-245.611 StartZ=0 EndX=-0.574632 EndY=-255.778 EndZ=0
    g11: LineSegment StartX=-0.574632 StartY=-255.778 StartZ=0 EndX=-0.49611 EndY=-263.631 EndZ=0
    g12: LineSegment StartX=-0.49611 StartY=-263.631 StartZ=0 EndX=-0.339053 EndY=-269.441 EndZ=0
    g13: LineSegment StartX=-18.0751 StartY=-233.296 StartZ=0 EndX=-1.40062 EndY=-223.505 EndZ=0
    g14: LineSegment StartX=-1.40062 StartY=-223.505 StartZ=0 EndX=-1.42578 EndY=-214.033 EndZ=0
    g15: LineSegment StartX=-1.42578 StartY=-214.033 StartZ=0 EndX=-16.9984 EndY=-214.033 EndZ=0
    g16: LineSegment StartX=-16.9984 StartY=-214.033 StartZ=0 EndX=-17.3382 EndY=-222.242 EndZ=0
    g17: LineSegment StartX=-17.3382 StartY=-222.242 StartZ=0 EndX=-17.7593 EndY=-228.927 EndZ=0
    g18: LineSegment StartX=-17.7593 StartY=-228.927 StartZ=0 EndX=-18.0751 EndY=-233.296 EndZ=0
  constraints (23):
    c: Horizontal(g0)
    c: Coincident(g0,g1)
    c: Coincident(g0,g2)
    c: Coincident(g2,g3)
    c: Coincident(g3,g4)
    c: Coincident(g4,g1)
    c: Coincident(g5,g6)
    c: Coincident(g6,g7)
    c: Coincident(g7,g8)
    c: Coincident(g8,g9)
    c: Coincident(g9,g10)
    c: Coincident(g10,g11)
    c: Coincident(g11,g12)
    c: Coincident(g12,g5)
    c: Coincident(g13,g14)
    c: Coincident(g14,g15)
    c: Horizontal(g15)
    c: Coincident(g15,g16)
    c: Coincident(g16,g17)
    c: Coincident(g17,g18)
    c: Coincident(g18,g13)
    c: Parallel(g3,g5)
    c: Parallel(g8,g13)
FEATURE [PartDesign::Pocket] Pocket064
  BaseFeature = -> Pocket063
  Direction = (1,0,0)
  Length = 15
  Length2 = 5
  Profile = -> Sketch099
  ReferenceAxis = -> Sketch099 [N_Axis]
  Refine = true
  Suppressed = false
  Type = 0
FEATURE [PartDesign::Body] Body013
  AllowCompound = false
  Group = -> [Sketch094,Sketch093,AdditiveLoft013,Sketch095,Pocket060,Sketch096,Pocket061,Sketch097,Pocket062,DatumPlane016,Sketch098,Pocket063,Sketch099,Pocket064]
  Origin = -> Origin013
  Placement = pos=(0,0,-100) rot=(0,0,1;0rad)
  Tip = -> Pocket064
FEATURE [Part::Mirroring] Part__Mirroring013  label="Body013 (Mirror #14)"
  Base = (0,0,0)
  Normal = (0,0,1)
  Source = -> Body013
FEATURE [Sketcher::SketchObject] Sketch100
  ArcFitTolerance = 1e-06
  FullyConstrained = false
  MakeInternals = false
  Placement = pos=(600,0,-600) rot=(0,0,1;0rad)
  sketch-geometry (123):
    g0: BSplineCurve PolesCount=61 KnotsCount=61 Degree=3 IsPeriodic=1
    g1-g61: Circle [constr] x61 (B-spline internal-alignment scaffolding for g0; pole/knot coordinates omitted)
    g62-g122: GeomPoint [constr] x61 (B-spline internal-alignment scaffolding for g0; pole/knot coordinates omitted)
  constraints (123):
    c: InternalAlignment(g1,g0)
    c: Weight(g1) = 1
    c: InternalAlignment(g2,g0)
    c: Equal(g2,g1)
    c: InternalAlignment(g3,g0)
    c: Equal(g3,g1)
    c: InternalAlignment(g4,g0)
    c: Equal(g4,g1)
    c: InternalAlignment(g5,g0)
    c: Equal(g5,g1)
    c: InternalAlignment(g6,g0)
    c: Equal(g6,g1)
    c: InternalAlignment(g7,g0)
    c: Equal(g7,g1)
    c: InternalAlignment(g8,g0)
    c: Equal(g8,g1)
    c: InternalAlignment(g9,g0)
    c: Equal(g9,g1)
    c: InternalAlignment(g10,g0)
    c: Equal(g10,g1)
    c: InternalAlignment(g11,g0)
    c: Equal(g11,g1)
    c: InternalAlignment(g12,g0)
    c: Equal(g12,g1)
    c: InternalAlignment(g13,g0)
    c: Equal(g13,g1)
    c: InternalAlignment(g14,g0)
    c: Equal(g14,g1)
    c: InternalAlignment(g15,g0)
    c: Equal(g15,g1)
    c: InternalAlignment(g16,g0)
    c: Equal(g16,g1)
    c: InternalAlignment(g17,g0)
    c: Equal(g17,g1)
    c: InternalAlignment(g18,g0)
    c: Equal(g18,g1)
    c: InternalAlignment(g19,g0)
    c: Equal(g19,g1)
    c: InternalAlignment(g20,g0)
    c: Equal(g20,g1)
    c: InternalAlignment(g21,g0)
    c: Equal(g21,g1)
    c: InternalAlignment(g22,g0)
    c: Equal(g22,g1)
    c: InternalAlignment(g23,g0)
    c: Equal(g23,g1)
    c: InternalAlignment(g24,g0)
    c: Equal(g24,g1)
    c: InternalAlignment(g25,g0)
    c: Equal(g25,g1)
    c: InternalAlignment(g26,g0)
    c: Equal(g26,g1)
    c: InternalAlignment(g27,g0)
    c: Equal(g27,g1)
    c: InternalAlignment(g28,g0)
    c: Equal(g28,g1)
    c: InternalAlignment(g29,g0)
    c: Equal(g29,g1)
    c: InternalAlignment(g30,g0)
    c: Equal(g30,g1)
    c: InternalAlignment(g31,g0)
    c: Equal(g31,g1)
    c: InternalAlignment(g32,g0)
    c: Equal(g32,g1)
    c: InternalAlignment(g33,g0)
    c: Equal(g33,g1)
    c: InternalAlignment(g34,g0)
    c: Equal(g34,g1)
    c: InternalAlignment(g35,g0)
    c: Equal(g35,g1)
    c: InternalAlignment(g36,g0)
    c: Equal(g36,g1)
    c: InternalAlignment(g37,g0)
    c: Equal(g37,g1)
    c: InternalAlignment(g38,g0)
    c: Equal(g38,g1)
    c: InternalAlignment(g39,g0)
    c: Equal(g39,g1)
    c: InternalAlignment(g40,g0)
    c: Equal(g40,g1)
    c: InternalAlignment(g41,g0)
    c: Equal(g41,g1)
    c: InternalAlignment(g42,g0)
    c: Equal(g42,g1)
    c: InternalAlignment(g43,g0)
    c: Equal(g43,g1)
    c: InternalAlignment(g44,g0)
    c: Equal(g44,g1)
    c: InternalAlignment(g45,g0)
    c: Equal(g45,g1)
    c: InternalAlignment(g46,g0)
    c: Equal(g46,g1)
    c: InternalAlignment(g47,g0)
    c: Equal(g47,g1)
    c: InternalAlignment(g48,g0)
    c: Equal(g48,g1)
    c: InternalAlignment(g49,g0)
    c: Equal(g49,g1)
    c: InternalAlignment(g50,g0)
    c: Equal(g50,g1)
    c: InternalAlignment(g51,g0)
    c: Equal(g51,g1)
    c: InternalAlignment(g52,g0)
    c: Equal(g52,g1)
    c: InternalAlignment(g53,g0)
    c: Equal(g53,g1)
    c: InternalAlignment(g54,g0)
    c: Equal(g54,g1)
    c: InternalAlignment(g55,g0)
    c: Equal(g55,g1)
    c: InternalAlignment(g56,g0)
    c: Equal(g56,g1)
    c: InternalAlignment(g57,g0)
    c: Equal(g57,g1)
    c: InternalAlignment(g58,g0)
    c: Equal(g58,g1)
    c: InternalAlignment(g59,g0)
    c: Equal(g59,g1)
    c: InternalAlignment(g60,g0)
    c: Equal(g60,g1)
    c: InternalAlignment(g61,g0)
    c: Equal(g61,g1)
    c: InternalAlignment(g62-g122 -> g0) x61
FEATURE [Sketcher::SketchObject] Sketch101
  ArcFitTolerance = 1e-06
  FullyConstrained = false
  MakeInternals = false
  sketch-geometry (123):
    g0: BSplineCurve PolesCount=61 KnotsCount=61 Degree=3 IsPeriodic=1
    g1-g61: Circle [constr] x61 (B-spline internal-alignment scaffolding for g0; pole/knot coordinates omitted)
    g62-g122: GeomPoint [constr] x61 (B-spline internal-alignment scaffolding for g0; pole/knot coordinates omitted)
  constraints (123):
    c: InternalAlignment(g1,g0)
    c: Weight(g1) = 1
    c: InternalAlignment(g2,g0)
    c: Equal(g2,g1)
    c: InternalAlignment(g3,g0)
    c: Equal(g3,g1)
    c: InternalAlignment(g4,g0)
    c: Equal(g4,g1)
    c: InternalAlignment(g5,g0)
    c: Equal(g5,g1)
    c: InternalAlignment(g6,g0)
    c: Equal(g6,g1)
    c: InternalAlignment(g7,g0)
    c: Equal(g7,g1)
    c: InternalAlignment(g8,g0)
    c: Equal(g8,g1)
    c: InternalAlignment(g9,g0)
    c: Equal(g9,g1)
    c: InternalAlignment(g10,g0)
    c: Equal(g10,g1)
    c: InternalAlignment(g11,g0)
    c: Equal(g11,g1)
    c: InternalAlignment(g12,g0)
    c: Equal(g12,g1)
    c: InternalAlignment(g13,g0)
    c: Equal(g13,g1)
    c: InternalAlignment(g14,g0)
    c: Equal(g14,g1)
    c: InternalAlignment(g15,g0)
    c: Equal(g15,g1)
    c: InternalAlignment(g16,g0)
    c: Equal(g16,g1)
    c: InternalAlignment(g17,g0)
    c: Equal(g17,g1)
    c: InternalAlignment(g18,g0)
    c: Equal(g18,g1)
    c: InternalAlignment(g19,g0)
    c: Equal(g19,g1)
    c: InternalAlignment(g20,g0)
    c: Equal(g20,g1)
    c: InternalAlignment(g21,g0)
    c: Equal(g21,g1)
    c: InternalAlignment(g22,g0)
    c: Equal(g22,g1)
    c: InternalAlignment(g23,g0)
    c: Equal(g23,g1)
    c: InternalAlignment(g24,g0)
    c: Equal(g24,g1)
    c: InternalAlignment(g25,g0)
    c: Equal(g25,g1)
    c: InternalAlignment(g26,g0)
    c: Equal(g26,g1)
    c: InternalAlignment(g27,g0)
    c: Equal(g27,g1)
    c: InternalAlignment(g28,g0)
    c: Equal(g28,g1)
    c: InternalAlignment(g29,g0)
    c: Equal(g29,g1)
    c: InternalAlignment(g30,g0)
    c: Equal(g30,g1)
    c: InternalAlignment(g31,g0)
    c: Equal(g31,g1)
    c: InternalAlignment(g32,g0)
    c: Equal(g32,g1)
    c: InternalAlignment(g33,g0)
    c: Equal(g33,g1)
    c: InternalAlignment(g34,g0)
    c: Equal(g34,g1)
    c: InternalAlignment(g35,g0)
    c: Equal(g35,g1)
    c: InternalAlignment(g36,g0)
    c: Equal(g36,g1)
    c: InternalAlignment(g37,g0)
    c: Equal(g37,g1)
    c: InternalAlignment(g38,g0)
    c: Equal(g38,g1)
    c: InternalAlignment(g39,g0)
    c: Equal(g39,g1)
    c: InternalAlignment(g40,g0)
    c: Equal(g40,g1)
    c: InternalAlignment(g41,g0)
    c: Equal(g41,g1)
    c: InternalAlignment(g42,g0)
    c: Equal(g42,g1)
    c: InternalAlignment(g43,g0)
    c: Equal(g43,g1)
    c: InternalAlignment(g44,g0)
    c: Equal(g44,g1)
    c: InternalAlignment(g45,g0)
    c: Equal(g45,g1)
    c: InternalAlignment(g46,g0)
    c: Equal(g46,g1)
    c: InternalAlignment(g47,g0)
    c: Equal(g47,g1)
    c: InternalAlignment(g48,g0)
    c: Equal(g48,g1)
    c: InternalAlignment(g49,g0)
    c: Equal(g49,g1)
    c: InternalAlignment(g50,g0)
    c: Equal(g50,g1)
    c: InternalAlignment(g51,g0)
    c: Equal(g51,g1)
    c: InternalAlignment(g52,g0)
    c: Equal(g52,g1)
    c: InternalAlignment(g53,g0)
    c: Equal(g53,g1)
    c: InternalAlignment(g54,g0)
    c: Equal(g54,g1)
    c: InternalAlignment(g55,g0)
    c: Equal(g55,g1)
    c: InternalAlignment(g56,g0)
    c: Equal(g56,g1)
    c: InternalAlignment(g57,g0)
    c: Equal(g57,g1)
    c: InternalAlignment(g58,g0)
    c: Equal(g58,g1)
    c: InternalAlignment(g59,g0)
    c: Equal(g59,g1)
    c: InternalAlignment(g60,g0)
    c: Equal(g60,g1)
    c: InternalAlignment(g61,g0)
    c: Equal(g61,g1)
    c: InternalAlignment(g62-g122 -> g0) x61
FEATURE [PartDesign::AdditiveLoft] AdditiveLoft014
  Closed = false
  Profile = -> Sketch101
  Refine = true
  Ruled = false
  Sections = -> [Sketch100]
  Suppressed = false
FEATURE [Sketcher::SketchObject] Sketch102
  ArcFitTolerance = 1e-06
  AttachmentSupport = -> [AdditiveLoft014]
  FullyConstrained = false
  MakeInternals = false
  MapMode = 5
  Placement = pos=(0,0,-600) rot=(1,0,0;3.14159rad)
  sketch-geometry (4):
    g0: LineSegment StartX=-34.2169 StartY=87.65 StartZ=0 EndX=-34.2169 EndY=-91.6403 EndZ=0
    g1: LineSegment StartX=-34.2169 StartY=-91.6403 StartZ=0 EndX=961.453 EndY=-91.6403 EndZ=0
    g2: LineSegment StartX=961.453 StartY=-91.6403 StartZ=0 EndX=961.453 EndY=87.65 EndZ=0
    g3: LineSegment StartX=961.453 StartY=87.65 StartZ=0 EndX=-34.2169 EndY=87.65 EndZ=0
  constraints (8):
    c: Coincident(g0,g1)
    c: Coincident(g1,g2)
    c: Coincident(g2,g3)
    c: Coincident(g3,g0)
    c: Vertical(g0)
    c: Vertical(g2)
    c: Horizontal(g1)
    c: Horizontal(g3)
FEATURE [PartDesign::Pocket] Pocket065
  BaseFeature = -> AdditiveLoft014
  Direction = (0,0,1)
  Length = 200
  Length2 = 5
  Profile = -> Sketch102
  ReferenceAxis = -> Sketch102 [N_Axis]
  Refine = true
  Suppressed = false
  Type = 0
FEATURE [Sketcher::SketchObject] Sketch103
  ArcFitTolerance = 1e-06
  AttachmentSupport = -> [Pocket065]
  FullyConstrained = false
  MakeInternals = false
  MapMode = 5
  sketch-geometry (4):
    g0: LineSegment StartX=-133.424 StartY=119.332 StartZ=0 EndX=-133.424 EndY=-141.213 EndZ=0
    g1: LineSegment StartX=-133.424 StartY=-141.213 StartZ=0 EndX=913.95 EndY=-141.213 EndZ=0
    g2: LineSegment StartX=913.95 StartY=-141.213 StartZ=0 EndX=913.95 EndY=119.332 EndZ=0
    g3: LineSegment StartX=913.95 StartY=119.332 StartZ=0 EndX=-133.424 EndY=119.332 EndZ=0
  constraints (8):
    c: Coincident(g0,g1)
    c: Coincident(g1,g2)
    c: Coincident(g2,g3)
    c: Coincident(g3,g0)
    c: Vertical(g0)
    c: Vertical(g2)
    c: Horizontal(g1)
    c: Horizontal(g3)
FEATURE [PartDesign::Pocket] Pocket066
  BaseFeature = -> Pocket065
  Direction = (0,0,-1)
  Length = 310
  Length2 = 5
  Profile = -> Sketch103
  ReferenceAxis = -> Sketch103 [N_Axis]
  Refine = true
  Suppressed = false
  Type = 0
FEATURE [Sketcher::SketchObject] Sketch104
  ArcFitTolerance = 1e-06
  AttachmentSupport = -> [YZ_Plane014]
  FullyConstrained = false
  MakeInternals = false
  MapMode = 5
  Placement = pos=(0,0,0) rot=(0.57735,0.57735,0.57735;2.0944rad)
  sketch-geometry (4):
    g0: LineSegment StartX=140.184 StartY=-572.082 StartZ=0 EndX=140.184 EndY=-172.98 EndZ=0
    g1: LineSegment StartX=140.184 StartY=-172.98 StartZ=0 EndX=-61.1981 EndY=-172.98 EndZ=0
    g2: LineSegment StartX=-61.1981 StartY=-172.98 StartZ=0 EndX=-61.1981 EndY=-572.082 EndZ=0
    g3: LineSegment StartX=-61.1981 StartY=-572.082 StartZ=0 EndX=140.184 EndY=-572.082 EndZ=0
  constraints (8):
    c: Coincident(g0,g1)
    c: Coincident(g1,g2)
    c: Coincident(g2,g3)
    c: Coincident(g3,g0)
    c: Vertical(g0)
    c: Vertical(g2)
    c: Horizontal(g1)
    c: Horizontal(g3)
FEATURE [PartDesign::Pocket] Pocket067
  BaseFeature = -> Pocket066
  Direction = (-1,0,0)
  Length = 510
  Length2 = 5
  Profile = -> Sketch104
  ReferenceAxis = -> Sketch104 [N_Axis]
  Refine = true
  Reversed = true
  Suppressed = false
  Type = 0
FEATURE [PartDesign::Plane] DatumPlane017
  AttachmentOffset = pos=(0,0,-220) rot=(0,0,1;0rad)
  AttachmentSupport = -> [Pocket067]
  Length = 79.1548
  MapMode = 5
  Placement = pos=(730,0,0) rot=(0.57735,-0.57735,-0.57735;2.0944rad)
  ResizeMode = 0
  Width = 454.155
FEATURE [Sketcher::SketchObject] Sketch105
  ArcFitTolerance = 1e-06
  AttachmentSupport = -> [DatumPlane017]
  FullyConstrained = false
  MakeInternals = false
  MapMode = 5
  Placement = pos=(730,0,0) rot=(0.57735,-0.57735,-0.57735;2.0944rad)
  sketch-geometry (4):
    g0: LineSegment StartX=-59.2595 StartY=-436.336 StartZ=0 EndX=94.1469 EndY=-436.336 EndZ=0
    g1: LineSegment StartX=94.1469 StartY=-436.336 StartZ=0 EndX=94.1469 EndY=-262.77 EndZ=0
    g2: LineSegment StartX=94.1469 StartY=-262.77 StartZ=0 EndX=-59.2595 EndY=-262.77 EndZ=0
    g3: LineSegment StartX=-59.2595 StartY=-262.77 StartZ=0 EndX=-59.2595 EndY=-436.336 EndZ=0
  constraints (8):
    c: Coincident(g0,g1)
    c: Coincident(g1,g2)
    c: Coincident(g2,g3)
    c: Coincident(g3,g0)
    c: Horizontal(g0)
    c: Horizontal(g2)
    c: Vertical(g1)
    c: Vertical(g3)
FEATURE [PartDesign::Pocket] Pocket068
  BaseFeature = -> Pocket067
  Direction = (1,0,0)
  Length = 210
  Length2 = 5
  Profile = -> Sketch105
  ReferenceAxis = -> Sketch105 [N_Axis]
  Refine = true
  Reversed = true
  Suppressed = false
  Type = 0
FEATURE [Sketcher::SketchObject] Sketch106
  ArcFitTolerance = 1e-06
  AttachmentSupport = -> [Pocket068]
  FullyConstrained = false
  MakeInternals = false
  MapMode = 5
  Placement = pos=(510,0,0) rot=(0.57735,-0.57735,-0.57735;2.0944rad)
  sketch-geometry (26):
    g0: LineSegment StartX=-19.2377 StartY=-395.515 StartZ=0 EndX=1.16551 EndY=-395.515 EndZ=0
    g1: LineSegment StartX=1.16551 StartY=-395.515 StartZ=0 EndX=0.8232 EndY=-382.336 EndZ=0
    g2: LineSegment StartX=0.8232 StartY=-382.336 StartZ=0 EndX=-18.6854 EndY=-370.973 EndZ=0
    g3: LineSegment StartX=-18.6854 StartY=-370.973 StartZ=0 EndX=-19.0671 EndY=-379.481 EndZ=0
    g4: LineSegment StartX=-19.0671 StartY=-379.481 StartZ=0 EndX=-19.1527 EndY=-385.615 EndZ=0
    g5: LineSegment StartX=-19.1527 StartY=-385.615 StartZ=0 EndX=-19.2091 EndY=-391.666 EndZ=0
    g6: LineSegment StartX=-19.2091 StartY=-391.666 StartZ=0 EndX=-19.2377 EndY=-395.515 EndZ=0
    g7: LineSegment StartX=0.714665 StartY=-378.158 StartZ=0 EndX=-18.7203 EndY=-366.838 EndZ=0
    g8: LineSegment StartX=-18.7203 StartY=-366.838 StartZ=0 EndX=-18.6623 EndY=-362.983 EndZ=0
    g9: LineSegment StartX=-18.6623 StartY=-362.983 StartZ=0 EndX=-18.5229 EndY=-358.175 EndZ=0
    g10: LineSegment StartX=-18.5229 StartY=-358.175 StartZ=0 EndX=-18.2464 EndY=-352.031 EndZ=0
    g11: LineSegment StartX=-18.2464 StartY=-352.031 StartZ=0 EndX=-17.9705 EndY=-340.851 EndZ=0
    g12: LineSegment StartX=-17.9705 StartY=-340.851 StartZ=0 EndX=-0.087226 EndY=-329.822 EndZ=0
    g13: LineSegment StartX=-0.087226 StartY=-329.822 StartZ=0 EndX=-0.10619 EndY=-342.519 EndZ=0
    g14: LineSegment StartX=-0.10619 StartY=-342.519 StartZ=0 EndX=-0.10619 EndY=-350.368 EndZ=0
    g15: LineSegment StartX=-0.10619 StartY=-350.368 StartZ=0 EndX=0.049742 EndY=-357.385 EndZ=0
    g16: LineSegment StartX=0.049742 StartY=-357.385 StartZ=0 EndX=0.153698 EndY=-361.959 EndZ=0
    g17: LineSegment StartX=0.153698 StartY=-361.959 StartZ=0 EndX=0.309631 EndY=-366.325 EndZ=0
    g18: LineSegment StartX=0.309631 StartY=-366.325 StartZ=0 EndX=0.413587 EndY=-371.575 EndZ=0
    g19: LineSegment StartX=0.413587 StartY=-371.575 StartZ=0 EndX=0.714665 EndY=-378.158 EndZ=0
    g20: LineSegment StartX=-0.365594 StartY=-315.639 StartZ=0 EndX=-16.1669 EndY=-315.639 EndZ=0
    g21: LineSegment StartX=-16.1669 StartY=-315.639 StartZ=0 EndX=-16.5547 EndY=-321.927 EndZ=0
    g22: LineSegment StartX=-16.5547 StartY=-321.927 StartZ=0 EndX=-16.8951 EndY=-328.608 EndZ=0
    g23: LineSegment StartX=-16.8951 StartY=-328.608 StartZ=0 EndX=-17.2291 EndY=-336.089 EndZ=0
    g24: LineSegment StartX=-17.2291 StartY=-336.089 StartZ=0 EndX=-0.136026 EndY=-325.548 EndZ=0
    g25: LineSegment StartX=-0.136026 StartY=-325.548 StartZ=0 EndX=-0.365594 EndY=-315.639 EndZ=0
  constraints (28):
    c: Horizontal(g0)
    c: Coincident(g0,g1)
    c: Coincident(g1,g2)
    c: Coincident(g2,g3)
    c: Coincident(g3,g4)
    c: Coincident(g4,g5)
    c: Coincident(g5,g6)
    c: Coincident(g6,g0)
    c: Coincident(g7,g8)
    c: Coincident(g8,g9)
    c: Coincident(g9,g10)
    c: Coincident(g10,g11)
    c: Coincident(g11,g12)
    c: Coincident(g12,g13)
    c: Coincident(g14,g15)
    c: Coincident(g15,g16)
    c: Coincident(g16,g17)
    c: Coincident(g17,g18)
    c: Coincident(g18,g19)
    c: Horizontal(g20)
    c: Coincident(g20,g21)
    c: Coincident(g21,g22)
    c: Coincident(g23,g24)
    c: Coincident(g24,g25)
    c: Coincident(g25,g20)
    c: Parallel(g12,g24)
    c: Coincident(g7,g19)
    c: Parallel(g2,g7)
FEATURE [PartDesign::Pocket] Pocket069
  BaseFeature = -> Pocket068
  Direction = (1,0,0)
  Length = 15
  Length2 = 5
  Profile = -> Sketch106
  ReferenceAxis = -> Sketch106 [N_Axis]
  Refine = true
  Suppressed = false
  Type = 0
FEATURE [PartDesign::Body] Body014
  AllowCompound = false
  Group = -> [Sketch101,Sketch100,AdditiveLoft014,Sketch102,Pocket065,Sketch103,Pocket066,Sketch104,Pocket067,DatumPlane017,Sketch105,Pocket068,Sketch106,Pocket069]
  Origin = -> Origin014
  Placement = pos=(0,0,-100) rot=(0,0,1;0rad)
  Tip = -> Pocket069
FEATURE [Part::Mirroring] Part__Mirroring014  label="Body014 (Mirror #15)"
  Base = (0,0,0)
  Normal = (0,0,1)
  Source = -> Body014
FEATURE [Sketcher::SketchObject] Sketch107
  ArcFitTolerance = 1e-06
  FullyConstrained = false
  MakeInternals = false
  Placement = pos=(600,0,-600) rot=(0,0,1;0rad)
  sketch-geometry (123):
    g0: BSplineCurve PolesCount=61 KnotsCount=61 Degree=3 IsPeriodic=1
    g1-g61: Circle [constr] x61 (B-spline internal-alignment scaffolding for g0; pole/knot coordinates omitted)
    g62-g122: GeomPoint [constr] x61 (B-spline internal-alignment scaffolding for g0; pole/knot coordinates omitted)
  constraints (123):
    c: InternalAlignment(g1,g0)
    c: Weight(g1) = 1
    c: InternalAlignment(g2,g0)
    c: Equal(g2,g1)
    c: InternalAlignment(g3,g0)
    c: Equal(g3,g1)
    c: InternalAlignment(g4,g0)
    c: Equal(g4,g1)
    c: InternalAlignment(g5,g0)
    c: Equal(g5,g1)
    c: InternalAlignment(g6,g0)
    c: Equal(g6,g1)
    c: InternalAlignment(g7,g0)
    c: Equal(g7,g1)
    c: InternalAlignment(g8,g0)
    c: Equal(g8,g1)
    c: InternalAlignment(g9,g0)
    c: Equal(g9,g1)
    c: InternalAlignment(g10,g0)
    c: Equal(g10,g1)
    c: InternalAlignment(g11,g0)
    c: Equal(g11,g1)
    c: InternalAlignment(g12,g0)
    c: Equal(g12,g1)
    c: InternalAlignment(g13,g0)
    c: Equal(g13,g1)
    c: InternalAlignment(g14,g0)
    c: Equal(g14,g1)
    c: InternalAlignment(g15,g0)
    c: Equal(g15,g1)
    c: InternalAlignment(g16,g0)
    c: Equal(g16,g1)
    c: InternalAlignment(g17,g0)
    c: Equal(g17,g1)
    c: InternalAlignment(g18,g0)
    c: Equal(g18,g1)
    c: InternalAlignment(g19,g0)
    c: Equal(g19,g1)
    c: InternalAlignment(g20,g0)
    c: Equal(g20,g1)
    c: InternalAlignment(g21,g0)
    c: Equal(g21,g1)
    c: InternalAlignment(g22,g0)
    c: Equal(g22,g1)
    c: InternalAlignment(g23,g0)
    c: Equal(g23,g1)
    c: InternalAlignment(g24,g0)
    c: Equal(g24,g1)
    c: InternalAlignment(g25,g0)
    c: Equal(g25,g1)
    c: InternalAlignment(g26,g0)
    c: Equal(g26,g1)
    c: InternalAlignment(g27,g0)
    c: Equal(g27,g1)
    c: InternalAlignment(g28,g0)
    c: Equal(g28,g1)
    c: InternalAlignment(g29,g0)
    c: Equal(g29,g1)
    c: InternalAlignment(g30,g0)
    c: Equal(g30,g1)
    c: InternalAlignment(g31,g0)
    c: Equal(g31,g1)
    c: InternalAlignment(g32,g0)
    c: Equal(g32,g1)
    c: InternalAlignment(g33,g0)
    c: Equal(g33,g1)
    c: InternalAlignment(g34,g0)
    c: Equal(g34,g1)
    c: InternalAlignment(g35,g0)
    c: Equal(g35,g1)
    c: InternalAlignment(g36,g0)
    c: Equal(g36,g1)
    c: InternalAlignment(g37,g0)
    c: Equal(g37,g1)
    c: InternalAlignment(g38,g0)
    c: Equal(g38,g1)
    c: InternalAlignment(g39,g0)
    c: Equal(g39,g1)
    c: InternalAlignment(g40,g0)
    c: Equal(g40,g1)
    c: InternalAlignment(g41,g0)
    c: Equal(g41,g1)
    c: InternalAlignment(g42,g0)
    c: Equal(g42,g1)
    c: InternalAlignment(g43,g0)
    c: Equal(g43,g1)
    c: InternalAlignment(g44,g0)
    c: Equal(g44,g1)
    c: InternalAlignment(g45,g0)
    c: Equal(g45,g1)
    c: InternalAlignment(g46,g0)
    c: Equal(g46,g1)
    c: InternalAlignment(g47,g0)
    c: Equal(g47,g1)
    c: InternalAlignment(g48,g0)
    c: Equal(g48,g1)
    c: InternalAlignment(g49,g0)
    c: Equal(g49,g1)
    c: InternalAlignment(g50,g0)
    c: Equal(g50,g1)
    c: InternalAlignment(g51,g0)
    c: Equal(g51,g1)
    c: InternalAlignment(g52,g0)
    c: Equal(g52,g1)
    c: InternalAlignment(g53,g0)
    c: Equal(g53,g1)
    c: InternalAlignment(g54,g0)
    c: Equal(g54,g1)
    c: InternalAlignment(g55,g0)
    c: Equal(g55,g1)
    c: InternalAlignment(g56,g0)
    c: Equal(g56,g1)
    c: InternalAlignment(g57,g0)
    c: Equal(g57,g1)
    c: InternalAlignment(g58,g0)
    c: Equal(g58,g1)
    c: InternalAlignment(g59,g0)
    c: Equal(g59,g1)
    c: InternalAlignment(g60,g0)
    c: Equal(g60,g1)
    c: InternalAlignment(g61,g0)
    c: Equal(g61,g1)
    c: InternalAlignment(g62-g122 -> g0) x61
FEATURE [Sketcher::SketchObject] Sketch108
  ArcFitTolerance = 1e-06
  FullyConstrained = false
  MakeInternals = false
  sketch-geometry (123):
    g0: BSplineCurve PolesCount=61 KnotsCount=61 Degree=3 IsPeriodic=1
    g1-g61: Circle [constr] x61 (B-spline internal-alignment scaffolding for g0; pole/knot coordinates omitted)
    g62-g122: GeomPoint [constr] x61 (B-spline internal-alignment scaffolding for g0; pole/knot coordinates omitted)
  constraints (123):
    c: InternalAlignment(g1,g0)
    c: Weight(g1) = 1
    c: InternalAlignment(g2,g0)
    c: Equal(g2,g1)
    c: InternalAlignment(g3,g0)
    c: Equal(g3,g1)
    c: InternalAlignment(g4,g0)
    c: Equal(g4,g1)
    c: InternalAlignment(g5,g0)
    c: Equal(g5,g1)
    c: InternalAlignment(g6,g0)
    c: Equal(g6,g1)
    c: InternalAlignment(g7,g0)
    c: Equal(g7,g1)
    c: InternalAlignment(g8,g0)
    c: Equal(g8,g1)
    c: InternalAlignment(g9,g0)
    c: Equal(g9,g1)
    c: InternalAlignment(g10,g0)
    c: Equal(g10,g1)
    c: InternalAlignment(g11,g0)
    c: Equal(g11,g1)
    c: InternalAlignment(g12,g0)
    c: Equal(g12,g1)
    c: InternalAlignment(g13,g0)
    c: Equal(g13,g1)
    c: InternalAlignment(g14,g0)
    c: Equal(g14,g1)
    c: InternalAlignment(g15,g0)
    c: Equal(g15,g1)
    c: InternalAlignment(g16,g0)
    c: Equal(g16,g1)
    c: InternalAlignment(g17,g0)
    c: Equal(g17,g1)
    c: InternalAlignment(g18,g0)
    c: Equal(g18,g1)
    c: InternalAlignment(g19,g0)
    c: Equal(g19,g1)
    c: InternalAlignment(g20,g0)
    c: Equal(g20,g1)
    c: InternalAlignment(g21,g0)
    c: Equal(g21,g1)
    c: InternalAlignment(g22,g0)
    c: Equal(g22,g1)
    c: InternalAlignment(g23,g0)
    c: Equal(g23,g1)
    c: InternalAlignment(g24,g0)
    c: Equal(g24,g1)
    c: InternalAlignment(g25,g0)
    c: Equal(g25,g1)
    c: InternalAlignment(g26,g0)
    c: Equal(g26,g1)
    c: InternalAlignment(g27,g0)
    c: Equal(g27,g1)
    c: InternalAlignment(g28,g0)
    c: Equal(g28,g1)
    c: InternalAlignment(g29,g0)
    c: Equal(g29,g1)
    c: InternalAlignment(g30,g0)
    c: Equal(g30,g1)
    c: InternalAlignment(g31,g0)
    c: Equal(g31,g1)
    c: InternalAlignment(g32,g0)
    c: Equal(g32,g1)
    c: InternalAlignment(g33,g0)
    c: Equal(g33,g1)
    c: InternalAlignment(g34,g0)
    c: Equal(g34,g1)
    c: InternalAlignment(g35,g0)
    c: Equal(g35,g1)
    c: InternalAlignment(g36,g0)
    c: Equal(g36,g1)
    c: InternalAlignment(g37,g0)
    c: Equal(g37,g1)
    c: InternalAlignment(g38,g0)
    c: Equal(g38,g1)
    c: InternalAlignment(g39,g0)
    c: Equal(g39,g1)
    c: InternalAlignment(g40,g0)
    c: Equal(g40,g1)
    c: InternalAlignment(g41,g0)
    c: Equal(g41,g1)
    c: InternalAlignment(g42,g0)
    c: Equal(g42,g1)
    c: InternalAlignment(g43,g0)
    c: Equal(g43,g1)
    c: InternalAlignment(g44,g0)
    c: Equal(g44,g1)
    c: InternalAlignment(g45,g0)
    c: Equal(g45,g1)
    c: InternalAlignment(g46,g0)
    c: Equal(g46,g1)
    c: InternalAlignment(g47,g0)
    c: Equal(g47,g1)
    c: InternalAlignment(g48,g0)
    c: Equal(g48,g1)
    c: InternalAlignment(g49,g0)
    c: Equal(g49,g1)
    c: InternalAlignment(g50,g0)
    c: Equal(g50,g1)
    c: InternalAlignment(g51,g0)
    c: Equal(g51,g1)
    c: InternalAlignment(g52,g0)
    c: Equal(g52,g1)
    c: InternalAlignment(g53,g0)
    c: Equal(g53,g1)
    c: InternalAlignment(g54,g0)
    c: Equal(g54,g1)
    c: InternalAlignment(g55,g0)
    c: Equal(g55,g1)
    c: InternalAlignment(g56,g0)
    c: Equal(g56,g1)
    c: InternalAlignment(g57,g0)
    c: Equal(g57,g1)
    c: InternalAlignment(g58,g0)
    c: Equal(g58,g1)
    c: InternalAlignment(g59,g0)
    c: Equal(g59,g1)
    c: InternalAlignment(g60,g0)
    c: Equal(g60,g1)
    c: InternalAlignment(g61,g0)
    c: Equal(g61,g1)
    c: InternalAlignment(g62-g122 -> g0) x61
FEATURE [PartDesign::AdditiveLoft] AdditiveLoft015
  Closed = false
  Profile = -> Sketch108
  Refine = true
  Ruled = false
  Sections = -> [Sketch107]
  Suppressed = false
FEATURE [Sketcher::SketchObject] Sketch109
  ArcFitTolerance = 1e-06
  AttachmentSupport = -> [AdditiveLoft015]
  FullyConstrained = false
  MakeInternals = false
  MapMode = 5
  Placement = pos=(0,0,-600) rot=(1,0,0;3.14159rad)
  sketch-geometry (4):
    g0: LineSegment StartX=-34.2169 StartY=87.65 StartZ=0 EndX=-34.2169 EndY=-91.6403 EndZ=0
    g1: LineSegment StartX=-34.2169 StartY=-91.6403 StartZ=0 EndX=961.453 EndY=-91.6403 EndZ=0
    g2: LineSegment StartX=961.453 StartY=-91.6403 StartZ=0 EndX=961.453 EndY=87.65 EndZ=0
    g3: LineSegment StartX=961.453 StartY=87.65 StartZ=0 EndX=-34.2169 EndY=87.65 EndZ=0
  constraints (8):
    c: Coincident(g0,g1)
    c: Coincident(g1,g2)
    c: Coincident(g2,g3)
    c: Coincident(g3,g0)
    c: Vertical(g0)
    c: Vertical(g2)
    c: Horizontal(g1)
    c: Horizontal(g3)
FEATURE [PartDesign::Pocket] Pocket070
  BaseFeature = -> AdditiveLoft015
  Direction = (0,0,1)
  Length = 100
  Length2 = 5
  Profile = -> Sketch109
  ReferenceAxis = -> Sketch109 [N_Axis]
  Refine = true
  Suppressed = false
  Type = 0
FEATURE [Sketcher::SketchObject] Sketch110
  ArcFitTolerance = 1e-06
  AttachmentSupport = -> [Pocket070]
  FullyConstrained = false
  MakeInternals = false
  MapMode = 5
  sketch-geometry (4):
    g0: LineSegment StartX=-133.424 StartY=119.332 StartZ=0 EndX=-133.424 EndY=-141.213 EndZ=0
    g1: LineSegment StartX=-133.424 StartY=-141.213 StartZ=0 EndX=913.95 EndY=-141.213 EndZ=0
    g2: LineSegment StartX=913.95 StartY=-141.213 StartZ=0 EndX=913.95 EndY=119.332 EndZ=0
    g3: LineSegment StartX=913.95 StartY=119.332 StartZ=0 EndX=-133.424 EndY=119.332 EndZ=0
  constraints (8):
    c: Coincident(g0,g1)
    c: Coincident(g1,g2)
    c: Coincident(g2,g3)
    c: Coincident(g3,g0)
    c: Vertical(g0)
    c: Vertical(g2)
    c: Horizontal(g1)
    c: Horizontal(g3)
FEATURE [PartDesign::Pocket] Pocket071
  BaseFeature = -> Pocket070
  Direction = (0,0,-1)
  Length = 410
  Length2 = 5
  Profile = -> Sketch110
  ReferenceAxis = -> Sketch110 [N_Axis]
  Refine = true
  Suppressed = false
  Type = 0
FEATURE [Sketcher::SketchObject] Sketch111
  ArcFitTolerance = 1e-06
  AttachmentSupport = -> [YZ_Plane015]
  FullyConstrained = false
  MakeInternals = false
  MapMode = 5
  Placement = pos=(0,0,0) rot=(0.57735,0.57735,0.57735;2.0944rad)
  sketch-geometry (4):
    g0: LineSegment StartX=128.87 StartY=-336.122 StartZ=0 EndX=-140.307 EndY=-336.122 EndZ=0
    g1: LineSegment StartX=-140.307 StartY=-336.122 StartZ=0 EndX=-140.307 EndY=-663.557 EndZ=0
    g2: LineSegment StartX=-140.307 StartY=-663.557 StartZ=0 EndX=128.87 EndY=-663.557 EndZ=0
    g3: LineSegment StartX=128.87 StartY=-663.557 StartZ=0 EndX=128.87 EndY=-336.122 EndZ=0
  constraints (8):
    c: Coincident(g0,g1)
    c: Coincident(g1,g2)
    c: Coincident(g2,g3)
    c: Coincident(g3,g0)
    c: Horizontal(g0)
    c: Horizontal(g2)
    c: Vertical(g1)
    c: Vertical(g3)
FEATURE [PartDesign::Pocket] Pocket072
  BaseFeature = -> Pocket071
  Direction = (-1,0,0)
  Length = 550
  Length2 = 5
  Profile = -> Sketch111
  ReferenceAxis = -> Sketch111 [N_Axis]
  Refine = true
  Reversed = true
  Suppressed = false
  Type = 0
FEATURE [PartDesign::Plane] DatumPlane018
  AttachmentOffset = pos=(0,0,-240) rot=(0,0,1;0rad)
  AttachmentSupport = -> [Pocket072]
  Length = 82.4037
  MapMode = 5
  Placement = pos=(790,0,0) rot=(0.57735,-0.57735,-0.57735;2.0944rad)
  ResizeMode = 0
  Width = 557.404
FEATURE [Sketcher::SketchObject] Sketch112
  ArcFitTolerance = 1e-06
  AttachmentSupport = -> [DatumPlane018]
  FullyConstrained = false
  MakeInternals = false
  MapMode = 5
  Placement = pos=(790,0,0) rot=(0.57735,-0.57735,-0.57735;2.0944rad)
  sketch-geometry (4):
    g0: LineSegment StartX=-95.9571 StartY=-331.056 StartZ=0 EndX=-95.9571 EndY=-543.568 EndZ=0
    g1: LineSegment StartX=-95.9571 StartY=-543.568 StartZ=0 EndX=92.8277 EndY=-543.568 EndZ=0
    g2: LineSegment StartX=92.8277 StartY=-543.568 StartZ=0 EndX=92.8277 EndY=-331.056 EndZ=0
    g3: LineSegment StartX=92.8277 StartY=-331.056 StartZ=0 EndX=-95.9571 EndY=-331.056 EndZ=0
  constraints (8):
    c: Coincident(g0,g1)
    c: Coincident(g1,g2)
    c: Coincident(g2,g3)
    c: Coincident(g3,g0)
    c: Vertical(g0)
    c: Vertical(g2)
    c: Horizontal(g1)
    c: Horizontal(g3)
FEATURE [PartDesign::Pocket] Pocket073
  BaseFeature = -> Pocket072
  Direction = (1,0,0)
  Length = 230
  Length2 = 5
  Profile = -> Sketch112
  ReferenceAxis = -> Sketch112 [N_Axis]
  Refine = true
  Reversed = true
  Suppressed = false
  Type = 0
FEATURE [Sketcher::SketchObject] Sketch113
  ArcFitTolerance = 1e-06
  AttachmentSupport = -> [Pocket073]
  FullyConstrained = false
  MakeInternals = false
  MapMode = 5
  Placement = pos=(550,0,0) rot=(0.57735,-0.57735,-0.57735;2.0944rad)
  sketch-geometry (31):
    g0: LineSegment StartX=-15.2336 StartY=-495.598 StartZ=0 EndX=2.51109 EndY=-495.598 EndZ=0
    g1: LineSegment StartX=2.51109 StartY=-495.598 StartZ=0 EndX=2.16267 EndY=-487.445 EndZ=0
    g2: LineSegment StartX=2.16267 StartY=-487.445 StartZ=0 EndX=2.02331 EndY=-481.313 EndZ=0
    g3: LineSegment StartX=2.02331 StartY=-481.313 StartZ=0 EndX=2.02331 EndY=-476.679 EndZ=0
    g4: LineSegment StartX=2.02331 StartY=-476.679 StartZ=0 EndX=2.0252 EndY=-472.878 EndZ=0
    g5: LineSegment StartX=2.0252 StartY=-472.878 StartZ=0 EndX=-17.4203 EndY=-462.71 EndZ=0
    g6: LineSegment StartX=-17.4203 StartY=-462.71 StartZ=0 EndX=-17.1397 EndY=-470.268 EndZ=0
    g7: LineSegment StartX=-17.1397 StartY=-470.268 StartZ=0 EndX=-16.9655 EndY=-473.926 EndZ=0
    g8: LineSegment StartX=-16.9655 StartY=-473.926 StartZ=0 EndX=-16.7907 EndY=-478.914 EndZ=0
    g9: LineSegment StartX=-16.7907 StartY=-478.914 StartZ=0 EndX=-16.4777 EndY=-483.473 EndZ=0
    g10: LineSegment StartX=-16.4777 StartY=-483.473 StartZ=0 EndX=-15.9894 EndY=-489.924 EndZ=0
    g11: LineSegment StartX=-15.9894 StartY=-489.924 StartZ=0 EndX=-15.2336 EndY=-495.598 EndZ=0
    g12: LineSegment StartX=2.17003 StartY=-468.789 StartZ=0 EndX=-17.6684 EndY=-458.416 EndZ=0
    g13: LineSegment StartX=-17.6684 StartY=-458.416 StartZ=0 EndX=-17.7321 EndY=-453.039 EndZ=0
    g14: LineSegment StartX=-17.7321 StartY=-453.039 StartZ=0 EndX=-17.7321 EndY=-448.474 EndZ=0
    g15: LineSegment StartX=-17.7321 StartY=-448.474 StartZ=0 EndX=-17.8366 EndY=-444.259 EndZ=0
    g16: LineSegment StartX=-17.8366 StartY=-444.259 StartZ=0 EndX=-17.8715 EndY=-440.078 EndZ=0
    g17: LineSegment StartX=-17.8715 StartY=-440.078 StartZ=0 EndX=-17.9352 EndY=-433.426 EndZ=0
    g18: LineSegment StartX=-17.9352 StartY=-433.426 StartZ=0 EndX=1.17967 EndY=-423.814 EndZ=0
    g19: LineSegment StartX=1.17967 StartY=-423.814 StartZ=0 EndX=1.57251 EndY=-439.458 EndZ=0
    g20: LineSegment StartX=1.57251 StartY=-439.458 StartZ=0 EndX=1.75192 EndY=-450.671 EndZ=0
    g21: LineSegment StartX=1.75192 StartY=-450.671 StartZ=0 EndX=1.99582 EndY=-461.751 EndZ=0
    g22: LineSegment StartX=1.99582 StartY=-461.751 StartZ=0 EndX=2.17003 EndY=-468.789 EndZ=0
    g23: LineSegment StartX=-17.5741 StartY=-428.887 StartZ=0 EndX=0.909163 EndY=-419.593 EndZ=0
    g24: LineSegment StartX=0.909163 StartY=-419.593 StartZ=0 EndX=0.734954 EndY=-414.813 EndZ=0
    g25: LineSegment StartX=0.734954 StartY=-414.813 StartZ=0 EndX=-17.4524 EndY=-414.813 EndZ=0
    g26: LineSegment StartX=-17.4524 StartY=-414.813 StartZ=0 EndX=-17.4873 EndY=-417.356 EndZ=0
    g27: LineSegment StartX=-17.4873 StartY=-417.356 StartZ=0 EndX=-17.5221 EndY=-419.342 EndZ=0
    g28: LineSegment StartX=-17.5221 StartY=-419.342 StartZ=0 EndX=-17.557 EndY=-421.816 EndZ=0
    g29: LineSegment StartX=-17.557 StartY=-421.816 StartZ=0 EndX=-17.5221 EndY=-424.812 EndZ=0
    g30: LineSegment StartX=-17.5221 StartY=-424.812 StartZ=0 EndX=-17.5741 EndY=-428.887 EndZ=0
  constraints (35):
    c: Horizontal(g0)
    c: Coincident(g0,g1)
    c: Coincident(g1,g2)
    c: Coincident(g2,g3)
    c: Coincident(g3,g4)
    c: Coincident(g4,g5)
    c: Coincident(g5,g6)
    c: Coincident(g6,g7)
    c: Coincident(g7,g8)
    c: Coincident(g8,g9)
    c: Coincident(g9,g10)
    c: Coincident(g10,g11)
    c: Coincident(g11,g0)
    c: Coincident(g12,g13)
    c: Coincident(g13,g14)
    c: Coincident(g14,g15)
    c: Coincident(g15,g16)
    c: Coincident(g16,g17)
    c: Coincident(g17,g18)
    c: Coincident(g18,g19)
    c: Coincident(g19,g20)
    c: Coincident(g20,g21)
    c: Coincident(g21,g22)
    c: Coincident(g22,g12)
    c: Coincident(g23,g24)
    c: Coincident(g24,g25)
    c: Horizontal(g25)
    c: Coincident(g25,g26)
    c: Coincident(g26,g27)
    c: Coincident(g27,g28)
    c: Coincident(g28,g29)
    c: Coincident(g29,g30)
    c: Coincident(g23,g30)
    c: Parallel(g12,g5)
    c: Parallel(g18,g23)
FEATURE [PartDesign::Pocket] Pocket074
  BaseFeature = -> Pocket073
  Direction = (1,0,0)
  Length = 15
  Length2 = 5
  Profile = -> Sketch113
  ReferenceAxis = -> Sketch113 [N_Axis]
  Refine = true
  Suppressed = false
  Type = 0
FEATURE [PartDesign::Body] Body015
  AllowCompound = false
  Group = -> [Sketch108,Sketch107,AdditiveLoft015,Sketch109,Pocket070,Sketch110,Pocket071,Sketch111,Pocket072,DatumPlane018,Sketch112,Pocket073,Sketch113,Pocket074]
  Origin = -> Origin015
  Placement = pos=(0,0,-100) rot=(0,0,1;0rad)
  Tip = -> Pocket074
FEATURE [Part::Mirroring] Part__Mirroring015  label="Body015 (Mirror #16)"
  Base = (0,0,0)
  Normal = (0,0,1)
  Source = -> Body015
FEATURE [PartDesign::ShapeBinder] CopyPocket028
  TraceSupport = false
FEATURE [PartDesign::Plane] DatumPlane019
  AttachmentOffset = pos=(550,0,-2) rot=(0,1,0;0.54042rad)
  AttachmentSupport = -> [CopyPocket028]
  Length = 716.467
  MapMode = 5
  Placement = pos=(550,0,-308) rot=(0.963715,0,0.266934;3.14159rad)
  ResizeMode = 0
  Width = 86.8673
FEATURE [Sketcher::SketchObject] Sketch114
  ArcFitTolerance = 1e-06
  AttachmentSupport = -> [DatumPlane019]
  FullyConstrained = true
  MakeInternals = false
  MapMode = 5
  Placement = pos=(550,0,-308) rot=(0.963715,0,0.266934;3.14159rad)
  sketch-geometry (2):
    g0: Circle CenterX=1.55 CenterY=-6.52 CenterZ=0 NormalX=0 NormalY=0 NormalZ=1 AngleXU=0 Radius=2.65
    g1: Circle CenterX=1.55 CenterY=-6.52 CenterZ=0 NormalX=0 NormalY=0 NormalZ=1 AngleXU=0 Radius=5.22
  constraints (5):
    c: Diameter(g0) = 5.3
    c: DistanceY(g0,g-1) = 6.52
    c: DistanceX(g-1,g0) = 1.55
    c: Coincident(g1,g0)
    c: Diameter(g1) = 10.44
FEATURE [PartDesign::Pad] Pad007
  Direction = (0.514496,0,-0.857493)
  Length = 10.5
  Length2 = 10
  Placement = pos=(550,0,-308) rot=(0.963715,0,0.266934;3.14159rad)
  Profile = -> Sketch114
  ReferenceAxis = -> Sketch114 [N_Axis]
  Refine = true
  Suppressed = false
  Type = 0
FEATURE [PartDesign::Plane] DatumPlane020
  AttachmentOffset = pos=(541,0,0) rot=(0,1,0;1.5708rad)
  AttachmentSupport = -> [CopyPocket028]
  Length = 370.117
  MapMode = 5
  Placement = pos=(541,0,-310) rot=(0.707107,0,0.707107;3.14159rad)
  ResizeMode = 0
  Width = 76.2256
FEATURE [Sketcher::SketchObject] Sketch115
  ArcFitTolerance = 1e-06
  AttachmentSupport = -> [DatumPlane020]
  FullyConstrained = false
  MakeInternals = false
  MapMode = 5
  Placement = pos=(541,0,-310) rot=(0.707107,0,0.707107;3.14159rad)
  sketch-geometry (4):
    g0: LineSegment StartX=0 StartY=0 StartZ=0 EndX=0 EndY=-14.1314 EndZ=0
    g1: LineSegment StartX=0 StartY=-14.1314 StartZ=0 EndX=7.20541 EndY=-14.1314 EndZ=0
    g2: LineSegment StartX=7.20541 StartY=-14.1314 StartZ=0 EndX=7.20541 EndY=0 EndZ=0
    g3: LineSegment StartX=7.20541 StartY=0 StartZ=0 EndX=0 EndY=0 EndZ=0
  constraints (9):
    c: Coincident(g0,g1)
    c: Coincident(g1,g2)
    c: Coincident(g2,g3)
    c: Coincident(g3,g0)
    c: Vertical(g0)
    c: Vertical(g2)
    c: Horizontal(g1)
    c: Horizontal(g3)
    c: Coincident(g0,g-1)
FEATURE [PartDesign::Pocket] Pocket075
  BaseFeature = -> Pad007
  Direction = (-1,0,2e-16)
  Length = 100
  Length2 = 5
  Placement = pos=(550,0,-308) rot=(0.963715,0,0.266934;3.14159rad)
  Profile = -> Sketch115
  ReferenceAxis = -> Sketch115 [N_Axis]
  Refine = true
  Reversed = true
  Suppressed = false
  Type = 0
FEATURE [PartDesign::Body] Body016
  AllowCompound = false
  Group = -> [DatumPlane019,CopyPocket028,Sketch114,Pad007,DatumPlane020,Sketch115,Pocket075]
  Origin = -> Origin016
  Placement = pos=(0,0,-100) rot=(0,0,1;0rad)
  Tip = -> Pocket075
FEATURE [Sketcher::SketchObject] Sketch116
  ArcFitTolerance = 1e-06
  FullyConstrained = false
  MakeInternals = false
  Placement = pos=(600,0,-600) rot=(0,0,1;0rad)
  sketch-geometry (123):
    g0: BSplineCurve PolesCount=61 KnotsCount=61 Degree=3 IsPeriodic=1
    g1-g61: Circle [constr] x61 (B-spline internal-alignment scaffolding for g0; pole/knot coordinates omitted)
    g62-g122: GeomPoint [constr] x61 (B-spline internal-alignment scaffolding for g0; pole/knot coordinates omitted)
  constraints (123):
    c: InternalAlignment(g1,g0)
    c: Weight(g1) = 1
    c: InternalAlignment(g2,g0)
    c: Equal(g2,g1)
    c: InternalAlignment(g3,g0)
    c: Equal(g3,g1)
    c: InternalAlignment(g4,g0)
    c: Equal(g4,g1)
    c: InternalAlignment(g5,g0)
    c: Equal(g5,g1)
    c: InternalAlignment(g6,g0)
    c: Equal(g6,g1)
    c: InternalAlignment(g7,g0)
    c: Equal(g7,g1)
    c: InternalAlignment(g8,g0)
    c: Equal(g8,g1)
    c: InternalAlignment(g9,g0)
    c: Equal(g9,g1)
    c: InternalAlignment(g10,g0)
    c: Equal(g10,g1)
    c: InternalAlignment(g11,g0)
    c: Equal(g11,g1)
    c: InternalAlignment(g12,g0)
    c: Equal(g12,g1)
    c: InternalAlignment(g13,g0)
    c: Equal(g13,g1)
    c: InternalAlignment(g14,g0)
    c: Equal(g14,g1)
    c: InternalAlignment(g15,g0)
    c: Equal(g15,g1)
    c: InternalAlignment(g16,g0)
    c: Equal(g16,g1)
    c: InternalAlignment(g17,g0)
    c: Equal(g17,g1)
    c: InternalAlignment(g18,g0)
    c: Equal(g18,g1)
    c: InternalAlignment(g19,g0)
    c: Equal(g19,g1)
    c: InternalAlignment(g20,g0)
    c: Equal(g20,g1)
    c: InternalAlignment(g21,g0)
    c: Equal(g21,g1)
    c: InternalAlignment(g22,g0)
    c: Equal(g22,g1)
    c: InternalAlignment(g23,g0)
    c: Equal(g23,g1)
    c: InternalAlignment(g24,g0)
    c: Equal(g24,g1)
    c: InternalAlignment(g25,g0)
    c: Equal(g25,g1)
    c: InternalAlignment(g26,g0)
    c: Equal(g26,g1)
    c: InternalAlignment(g27,g0)
    c: Equal(g27,g1)
    c: InternalAlignment(g28,g0)
    c: Equal(g28,g1)
    c: InternalAlignment(g29,g0)
    c: Equal(g29,g1)
    c: InternalAlignment(g30,g0)
    c: Equal(g30,g1)
    c: InternalAlignment(g31,g0)
    c: Equal(g31,g1)
    c: InternalAlignment(g32,g0)
    c: Equal(g32,g1)
    c: InternalAlignment(g33,g0)
    c: Equal(g33,g1)
    c: InternalAlignment(g34,g0)
    c: Equal(g34,g1)
    c: InternalAlignment(g35,g0)
    c: Equal(g35,g1)
    c: InternalAlignment(g36,g0)
    c: Equal(g36,g1)
    c: InternalAlignment(g37,g0)
    c: Equal(g37,g1)
    c: InternalAlignment(g38,g0)
    c: Equal(g38,g1)
    c: InternalAlignment(g39,g0)
    c: Equal(g39,g1)
    c: InternalAlignment(g40,g0)
    c: Equal(g40,g1)
    c: InternalAlignment(g41,g0)
    c: Equal(g41,g1)
    c: InternalAlignment(g42,g0)
    c: Equal(g42,g1)
    c: InternalAlignment(g43,g0)
    c: Equal(g43,g1)
    c: InternalAlignment(g44,g0)
    c: Equal(g44,g1)
    c: InternalAlignment(g45,g0)
    c: Equal(g45,g1)
    c: InternalAlignment(g46,g0)
    c: Equal(g46,g1)
    c: InternalAlignment(g47,g0)
    c: Equal(g47,g1)
    c: InternalAlignment(g48,g0)
    c: Equal(g48,g1)
    c: InternalAlignment(g49,g0)
    c: Equal(g49,g1)
    c: InternalAlignment(g50,g0)
    c: Equal(g50,g1)
    c: InternalAlignment(g51,g0)
    c: Equal(g51,g1)
    c: InternalAlignment(g52,g0)
    c: Equal(g52,g1)
    c: InternalAlignment(g53,g0)
    c: Equal(g53,g1)
    c: InternalAlignment(g54,g0)
    c: Equal(g54,g1)
    c: InternalAlignment(g55,g0)
    c: Equal(g55,g1)
    c: InternalAlignment(g56,g0)
    c: Equal(g56,g1)
    c: InternalAlignment(g57,g0)
    c: Equal(g57,g1)
    c: InternalAlignment(g58,g0)
    c: Equal(g58,g1)
    c: InternalAlignment(g59,g0)
    c: Equal(g59,g1)
    c: InternalAlignment(g60,g0)
    c: Equal(g60,g1)
    c: InternalAlignment(g61,g0)
    c: Equal(g61,g1)
    c: InternalAlignment(g62-g122 -> g0) x61
FEATURE [Sketcher::SketchObject] Sketch117
  ArcFitTolerance = 1e-06
  FullyConstrained = false
  MakeInternals = false
  sketch-geometry (123):
    g0: BSplineCurve PolesCount=61 KnotsCount=61 Degree=3 IsPeriodic=1
    g1-g61: Circle [constr] x61 (B-spline internal-alignment scaffolding for g0; pole/knot coordinates omitted)
    g62-g122: GeomPoint [constr] x61 (B-spline internal-alignment scaffolding for g0; pole/knot coordinates omitted)
  constraints (123):
    c: InternalAlignment(g1,g0)
    c: Weight(g1) = 1
    c: InternalAlignment(g2,g0)
    c: Equal(g2,g1)
    c: InternalAlignment(g3,g0)
    c: Equal(g3,g1)
    c: InternalAlignment(g4,g0)
    c: Equal(g4,g1)
    c: InternalAlignment(g5,g0)
    c: Equal(g5,g1)
    c: InternalAlignment(g6,g0)
    c: Equal(g6,g1)
    c: InternalAlignment(g7,g0)
    c: Equal(g7,g1)
    c: InternalAlignment(g8,g0)
    c: Equal(g8,g1)
    c: InternalAlignment(g9,g0)
    c: Equal(g9,g1)
    c: InternalAlignment(g10,g0)
    c: Equal(g10,g1)
    c: InternalAlignment(g11,g0)
    c: Equal(g11,g1)
    c: InternalAlignment(g12,g0)
    c: Equal(g12,g1)
    c: InternalAlignment(g13,g0)
    c: Equal(g13,g1)
    c: InternalAlignment(g14,g0)
    c: Equal(g14,g1)
    c: InternalAlignment(g15,g0)
    c: Equal(g15,g1)
    c: InternalAlignment(g16,g0)
    c: Equal(g16,g1)
    c: InternalAlignment(g17,g0)
    c: Equal(g17,g1)
    c: InternalAlignment(g18,g0)
    c: Equal(g18,g1)
    c: InternalAlignment(g19,g0)
    c: Equal(g19,g1)
    c: InternalAlignment(g20,g0)
    c: Equal(g20,g1)
    c: InternalAlignment(g21,g0)
    c: Equal(g21,g1)
    c: InternalAlignment(g22,g0)
    c: Equal(g22,g1)
    c: InternalAlignment(g23,g0)
    c: Equal(g23,g1)
    c: InternalAlignment(g24,g0)
    c: Equal(g24,g1)
    c: InternalAlignment(g25,g0)
    c: Equal(g25,g1)
    c: InternalAlignment(g26,g0)
    c: Equal(g26,g1)
    c: InternalAlignment(g27,g0)
    c: Equal(g27,g1)
    c: InternalAlignment(g28,g0)
    c: Equal(g28,g1)
    c: InternalAlignment(g29,g0)
    c: Equal(g29,g1)
    c: InternalAlignment(g30,g0)
    c: Equal(g30,g1)
    c: InternalAlignment(g31,g0)
    c: Equal(g31,g1)
    c: InternalAlignment(g32,g0)
    c: Equal(g32,g1)
    c: InternalAlignment(g33,g0)
    c: Equal(g33,g1)
    c: InternalAlignment(g34,g0)
    c: Equal(g34,g1)
    c: InternalAlignment(g35,g0)
    c: Equal(g35,g1)
    c: InternalAlignment(g36,g0)
    c: Equal(g36,g1)
    c: InternalAlignment(g37,g0)
    c: Equal(g37,g1)
    c: InternalAlignment(g38,g0)
    c: Equal(g38,g1)
    c: InternalAlignment(g39,g0)
    c: Equal(g39,g1)
    c: InternalAlignment(g40,g0)
    c: Equal(g40,g1)
    c: InternalAlignment(g41,g0)
    c: Equal(g41,g1)
    c: InternalAlignment(g42,g0)
    c: Equal(g42,g1)
    c: InternalAlignment(g43,g0)
    c: Equal(g43,g1)
    c: InternalAlignment(g44,g0)
    c: Equal(g44,g1)
    c: InternalAlignment(g45,g0)
    c: Equal(g45,g1)
    c: InternalAlignment(g46,g0)
    c: Equal(g46,g1)
    c: InternalAlignment(g47,g0)
    c: Equal(g47,g1)
    c: InternalAlignment(g48,g0)
    c: Equal(g48,g1)
    c: InternalAlignment(g49,g0)
    c: Equal(g49,g1)
    c: InternalAlignment(g50,g0)
    c: Equal(g50,g1)
    c: InternalAlignment(g51,g0)
    c: Equal(g51,g1)
    c: InternalAlignment(g52,g0)
    c: Equal(g52,g1)
    c: InternalAlignment(g53,g0)
    c: Equal(g53,g1)
    c: InternalAlignment(g54,g0)
    c: Equal(g54,g1)
    c: InternalAlignment(g55,g0)
    c: Equal(g55,g1)
    c: InternalAlignment(g56,g0)
    c: Equal(g56,g1)
    c: InternalAlignment(g57,g0)
    c: Equal(g57,g1)
    c: InternalAlignment(g58,g0)
    c: Equal(g58,g1)
    c: InternalAlignment(g59,g0)
    c: Equal(g59,g1)
    c: InternalAlignment(g60,g0)
    c: Equal(g60,g1)
    c: InternalAlignment(g61,g0)
    c: Equal(g61,g1)
    c: InternalAlignment(g62-g122 -> g0) x61
FEATURE [PartDesign::AdditiveLoft] AdditiveLoft016
  Closed = false
  Profile = -> Sketch117
  Refine = true
  Ruled = false
  Sections = -> [Sketch116]
  Suppressed = false
FEATURE [Sketcher::SketchObject] Sketch118
  ArcFitTolerance = 1e-06
  AttachmentSupport = -> [AdditiveLoft016]
  FullyConstrained = false
  MakeInternals = false
  MapMode = 5
  Placement = pos=(0,0,-600) rot=(1,0,0;3.14159rad)
  sketch-geometry (4):
    g0: LineSegment StartX=-34.2169 StartY=87.65 StartZ=0 EndX=-34.2169 EndY=-91.6403 EndZ=0
    g1: LineSegment StartX=-34.2169 StartY=-91.6403 StartZ=0 EndX=961.453 EndY=-91.6403 EndZ=0
    g2: LineSegment StartX=961.453 StartY=-91.6403 StartZ=0 EndX=961.453 EndY=87.65 EndZ=0
    g3: LineSegment StartX=961.453 StartY=87.65 StartZ=0 EndX=-34.2169 EndY=87.65 EndZ=0
  constraints (8):
    c: Coincident(g0,g1)
    c: Coincident(g1,g2)
    c: Coincident(g2,g3)
    c: Coincident(g3,g0)
    c: Vertical(g0)
    c: Vertical(g2)
    c: Horizontal(g1)
    c: Horizontal(g3)
FEATURE [PartDesign::Pocket] Pocket076
  BaseFeature = -> AdditiveLoft016
  Direction = (0,0,1)
  Length = 100
  Length2 = 5
  Profile = -> Sketch118
  ReferenceAxis = -> Sketch118 [N_Axis]
  Refine = true
  Suppressed = false
  Type = 0
FEATURE [Sketcher::SketchObject] Sketch119
  ArcFitTolerance = 1e-06
  AttachmentSupport = -> [Pocket076]
  FullyConstrained = false
  MakeInternals = false
  MapMode = 5
  sketch-geometry (4):
    g0: LineSegment StartX=-133.424 StartY=119.332 StartZ=0 EndX=-133.424 EndY=-141.213 EndZ=0
    g1: LineSegment StartX=-133.424 StartY=-141.213 StartZ=0 EndX=913.95 EndY=-141.213 EndZ=0
    g2: LineSegment StartX=913.95 StartY=-141.213 StartZ=0 EndX=913.95 EndY=119.332 EndZ=0
    g3: LineSegment StartX=913.95 StartY=119.332 StartZ=0 EndX=-133.424 EndY=119.332 EndZ=0
  constraints (8):
    c: Coincident(g0,g1)
    c: Coincident(g1,g2)
    c: Coincident(g2,g3)
    c: Coincident(g3,g0)
    c: Vertical(g0)
    c: Vertical(g2)
    c: Horizontal(g1)
    c: Horizontal(g3)
FEATURE [PartDesign::Pocket] Pocket077
  BaseFeature = -> Pocket076
  Direction = (0,0,-1)
  Length = 310
  Length2 = 5
  Profile = -> Sketch119
  ReferenceAxis = -> Sketch119 [N_Axis]
  Refine = true
  Suppressed = false
  Type = 0
FEATURE [Sketcher::SketchObject] Sketch120
  ArcFitTolerance = 1e-06
  AttachmentSupport = -> [YZ_Plane017]
  FullyConstrained = false
  MakeInternals = false
  MapMode = 5
  Placement = pos=(0,0,0) rot=(0.57735,0.57735,0.57735;2.0944rad)
  sketch-geometry (4):
    g0: LineSegment StartX=181.132 StartY=-284.822 StartZ=0 EndX=-92.4073 EndY=-284.822 EndZ=0
    g1: LineSegment StartX=-92.4073 StartY=-284.822 StartZ=0 EndX=-92.4073 EndY=-533.84 EndZ=0
    g2: LineSegment StartX=-92.4073 StartY=-533.84 StartZ=0 EndX=181.132 EndY=-533.84 EndZ=0
    g3: LineSegment StartX=181.132 StartY=-533.84 StartZ=0 EndX=181.132 EndY=-284.822 EndZ=0
  constraints (8):
    c: Coincident(g0,g1)
    c: Coincident(g1,g2)
    c: Coincident(g2,g3)
    c: Coincident(g3,g0)
    c: Horizontal(g0)
    c: Horizontal(g2)
    c: Vertical(g1)
    c: Vertical(g3)
FEATURE [PartDesign::Pocket] Pocket078
  BaseFeature = -> Pocket077
  Direction = (-1,0,0)
  Length = 546
  Length2 = 5
  Profile = -> Sketch120
  ReferenceAxis = -> Sketch120 [N_Axis]
  Refine = true
  Reversed = true
  Suppressed = false
  Type = 0
FEATURE [PartDesign::Plane] DatumPlane021
  AttachmentOffset = pos=(0,-500,0) rot=(1,0,0;0.54042rad)
  AttachmentSupport = -> [Pocket078]
  Length = 91.1887
  MapMode = 5
  Placement = pos=(546,0,-500) rot=(0.656451,-0.656451,-0.371676;2.42989rad)
  ResizeMode = 0
  Width = 889.443
FEATURE [Sketcher::SketchObject] Sketch121
  ArcFitTolerance = 1e-06
  AttachmentSupport = -> [DatumPlane021]
  FullyConstrained = false
  MakeInternals = false
  MapMode = 5
  Placement = pos=(546,0,-500) rot=(0.656451,-0.656451,-0.371676;2.42989rad)
  sketch-geometry (4):
    g0: LineSegment StartX=-114.047 StartY=197.232 StartZ=0 EndX=-114.047 EndY=-130.303 EndZ=0
    g1: LineSegment StartX=-114.047 StartY=-130.303 StartZ=0 EndX=149.633 EndY=-130.303 EndZ=0
    g2: LineSegment StartX=149.633 StartY=-130.303 StartZ=0 EndX=149.633 EndY=197.232 EndZ=0
    g3: LineSegment StartX=149.633 StartY=197.232 StartZ=0 EndX=-114.047 EndY=197.232 EndZ=0
  constraints (8):
    c: Coincident(g0,g1)
    c: Coincident(g1,g2)
    c: Coincident(g2,g3)
    c: Coincident(g3,g0)
    c: Vertical(g0)
    c: Vertical(g2)
    c: Horizontal(g1)
    c: Horizontal(g3)
FEATURE [PartDesign::Pocket] Pocket079
  BaseFeature = -> Pocket078
  Direction = (0.857493,-1e-16,0.514496)
  Length = 98
  Length2 = 5
  Profile = -> Sketch121
  ReferenceAxis = -> Sketch121 [N_Axis]
  Refine = true
  Suppressed = false
  Type = 0
FEATURE [Sketcher::SketchObject] Sketch122
  ArcFitTolerance = 1e-06
  AttachmentSupport = -> [Pocket079]
  FullyConstrained = false
  MakeInternals = false
  MapMode = 5
  Placement = pos=(0,0,-310) rot=(0,0,1;0rad)
  sketch-geometry (4):
    g0: LineSegment StartX=526.549 StartY=36.5917 StartZ=0 EndX=526.549 EndY=-47.1567 EndZ=0
    g1: LineSegment StartX=526.549 StartY=-47.1567 StartZ=0 EndX=693.06 EndY=-47.1567 EndZ=0
    g2: LineSegment StartX=693.06 StartY=-47.1567 StartZ=0 EndX=693.06 EndY=36.5917 EndZ=0
    g3: LineSegment StartX=693.06 StartY=36.5917 StartZ=0 EndX=526.549 EndY=36.5917 EndZ=0
  constraints (8):
    c: Coincident(g0,g1)
    c: Coincident(g1,g2)
    c: Coincident(g2,g3)
    c: Coincident(g3,g0)
    c: Vertical(g0)
    c: Vertical(g2)
    c: Horizontal(g1)
    c: Horizontal(g3)
FEATURE [PartDesign::Pocket] Pocket080
  BaseFeature = -> Pocket079
  Direction = (0,0,-1)
  Length = 4
  Length2 = 5
  Profile = -> Sketch122
  ReferenceAxis = -> Sketch122 [N_Axis]
  Refine = true
  Suppressed = false
  Type = 0
FEATURE [Sketcher::SketchObject] Sketch123
  ArcFitTolerance = 1e-06
  AttachmentSupport = -> [Pocket080]
  FullyConstrained = false
  MakeInternals = false
  MapMode = 5
  Placement = pos=(0,0,-500) rot=(1,0,0;3.14159rad)
  sketch-geometry (4):
    g0: LineSegment StartX=615.947 StartY=24.4678 StartZ=0 EndX=615.947 EndY=-56.6735 EndZ=0
    g1: LineSegment StartX=615.947 StartY=-56.6735 StartZ=0 EndX=839.377 EndY=-56.6735 EndZ=0
    g2: LineSegment StartX=839.377 StartY=-56.6735 StartZ=0 EndX=839.377 EndY=24.4678 EndZ=0
    g3: LineSegment StartX=839.377 StartY=24.4678 StartZ=0 EndX=615.947 EndY=24.4678 EndZ=0
  constraints (8):
    c: Coincident(g0,g1)
    c: Coincident(g1,g2)
    c: Coincident(g2,g3)
    c: Coincident(g3,g0)
    c: Vertical(g0)
    c: Vertical(g2)
    c: Horizontal(g1)
    c: Horizontal(g3)
FEATURE [PartDesign::Pocket] Pocket081
  BaseFeature = -> Pocket080
  Direction = (0,0,1)
  Length = 4
  Length2 = 5
  Profile = -> Sketch123
  ReferenceAxis = -> Sketch123 [N_Axis]
  Refine = true
  Suppressed = false
  Type = 0
FEATURE [PartDesign::Plane] DatumPlane022
  AttachmentOffset = pos=(548,0,0) rot=(0,-1,0;0.54042rad)
  AttachmentSupport = -> [Pocket081]
  Length = 980.514
  MapMode = 5
  Placement = pos=(548,0,-314) rot=(0,-1,0;0.54042rad)
  ResizeMode = 0
  Width = 93.2948
FEATURE [Sketcher::SketchObject] Sketch124
  ArcFitTolerance = 1e-06
  AttachmentSupport = -> [DatumPlane022]
  FullyConstrained = false
  MakeInternals = false
  MapMode = 5
  Placement = pos=(548,0,-314) rot=(0,-1,0;0.54042rad)
  sketch-geometry (4):
    g0: LineSegment StartX=-19.2548 StartY=36.3073 StartZ=0 EndX=-19.2548 EndY=-24.7493 EndZ=0
    g1: LineSegment StartX=-19.2548 StartY=-24.7493 StartZ=0 EndX=57.9391 EndY=-24.7493 EndZ=0
    g2: LineSegment StartX=57.9391 StartY=-24.7493 StartZ=0 EndX=57.9391 EndY=36.3073 EndZ=0
    g3: LineSegment StartX=57.9391 StartY=36.3073 StartZ=0 EndX=-19.2548 EndY=36.3073 EndZ=0
  constraints (8):
    c: Coincident(g0,g1)
    c: Coincident(g1,g2)
    c: Coincident(g2,g3)
    c: Coincident(g3,g0)
    c: Vertical(g0)
    c: Vertical(g2)
    c: Horizontal(g1)
    c: Horizontal(g3)
FEATURE [PartDesign::Pocket] Pocket082
  BaseFeature = -> Pocket081
  Direction = (0.514496,0,-0.857493)
  Length = 7
  Length2 = 5
  Profile = -> Sketch124
  ReferenceAxis = -> Sketch124 [N_Axis]
  Refine = true
  Suppressed = false
  Type = 0
FEATURE [Sketcher::SketchObject] Sketch125
  ArcFitTolerance = 1e-06
  AttachmentSupport = -> [Pocket082]
  FullyConstrained = false
  MakeInternals = false
  MapMode = 5
  Placement = pos=(287.19,0,-478.649) rot=(0,-1,0;0.54042rad)
  sketch-geometry (1):
    g0: Circle CenterX=314.674 CenterY=6.49479 CenterZ=0 NormalX=0 NormalY=0 NormalZ=1 AngleXU=0 Radius=3
  constraints (1):
    c: Diameter(g0) = 6
FEATURE [PartDesign::Pocket] Pocket083
  BaseFeature = -> Pocket082
  Direction = (0.514496,0,-0.857493)
  Length = 30
  Length2 = 5
  Profile = -> Sketch125
  ReferenceAxis = -> Sketch125 [N_Axis]
  Refine = true
  Suppressed = false
  Type = 0
FEATURE [PartDesign::Plane] DatumPlane023
  AttachmentOffset = pos=(680,0,0) rot=(0,1,0;0.54042rad)
  AttachmentSupport = -> [Pocket083]
  Length = 980.514
  MapMode = 5
  Placement = pos=(680,0,-496) rot=(0.963715,0,0.266934;3.14159rad)
  ResizeMode = 0
  Width = 93.2948
FEATURE [Sketcher::SketchObject] Sketch126
  ArcFitTolerance = 1e-06
  AttachmentSupport = -> [DatumPlane023]
  FullyConstrained = false
  MakeInternals = false
  MapMode = 5
  Placement = pos=(680,0,-496) rot=(0.963715,0,0.266934;3.14159rad)
  sketch-geometry (1):
    g0: Circle CenterX=-13.2038 CenterY=-6.51094 CenterZ=0 NormalX=0 NormalY=0 NormalZ=1 AngleXU=0 Radius=6.5
  constraints (1):
    c: Diameter(g0) = 13
FEATURE [PartDesign::Pocket] Pocket084
  BaseFeature = -> Pocket083
  Direction = (-0.514496,0,0.857493)
  Length = 12
  Length2 = 5
  Profile = -> Sketch126
  ReferenceAxis = -> Sketch126 [N_Axis]
  Refine = true
  Suppressed = false
  Type = 0
FEATURE [Sketcher::SketchObject] Sketch127
  ArcFitTolerance = 1e-06
  AttachmentSupport = -> [DatumPlane023]
  FullyConstrained = false
  MakeInternals = false
  MapMode = 5
  Placement = pos=(680,0,-496) rot=(0.963715,0,0.266934;3.14159rad)
  sketch-geometry (1):
    g0: Circle CenterX=-13.1956 CenterY=-6.50226 CenterZ=0 NormalX=0 NormalY=0 NormalZ=1 AngleXU=0 Radius=3
  constraints (1):
    c: Diameter(g0) = 6
FEATURE [PartDesign::Pocket] Pocket085
  BaseFeature = -> Pocket084
  Direction = (-0.514496,0,0.857493)
  Length = 30
  Length2 = 5
  Profile = -> Sketch127
  ReferenceAxis = -> Sketch127 [N_Axis]
  Refine = true
  Suppressed = false
  Type = 0
FEATURE [PartDesign::Fillet] Fillet
  Base = -> Pocket085 [Edge3,Edge5]
  BaseFeature = -> Pocket085
  Radius = 4.5
  Refine = true
  SupportTransform = false
  Suppressed = false
  UseAllEdges = false
FEATURE [PartDesign::Plane] DatumPlane024
  AttachmentOffset = pos=(0,0,-15) rot=(0,0,1;0rad)
  AttachmentSupport = -> [XZ_Plane017]
  Length = 907.902
  MapMode = 5
  Placement = pos=(0,15,-3.3e-15) rot=(1,0,0;1.5708rad)
  ResizeMode = 0
  Width = 648.527
FEATURE [Sketcher::SketchObject] Sketch128
  ArcFitTolerance = 1e-06
  AttachmentSupport = -> [DatumPlane024]
  FullyConstrained = false
  MakeInternals = false
  MapMode = 5
  Placement = pos=(0,15,-3.3e-15) rot=(1,0,0;1.5708rad)
  sketch-geometry (18):
    g0: LineSegment StartX=742.548 StartY=-488.8 StartZ=0 EndX=666.526 EndY=-488.8 EndZ=0
    g1: LineSegment StartX=666.526 StartY=-488.8 StartZ=0 EndX=645.222 EndY=-453.247 EndZ=0
    g2: LineSegment StartX=645.222 StartY=-453.247 StartZ=0 EndX=720.094 EndY=-453.247 EndZ=0
    g3: LineSegment StartX=720.094 StartY=-453.247 StartZ=0 EndX=742.548 EndY=-488.8 EndZ=0
    g4: LineSegment StartX=642.226 StartY=-448.247 StartZ=0 EndX=716.936 EndY=-448.247 EndZ=0
    g5: LineSegment StartX=716.936 StartY=-448.247 StartZ=0 EndX=691.774 EndY=-408.406 EndZ=0
    g6: LineSegment StartX=691.774 StartY=-408.406 StartZ=0 EndX=618.353 EndY=-408.406 EndZ=0
    g7: LineSegment StartX=618.353 StartY=-408.406 StartZ=0 EndX=642.226 EndY=-448.247 EndZ=0
    g8: LineSegment StartX=615.357 StartY=-403.406 StartZ=0 EndX=688.616 EndY=-403.406 EndZ=0
    g9: LineSegment StartX=688.616 StartY=-403.406 StartZ=0 EndX=663.693 EndY=-363.944 EndZ=0
    g10: LineSegment StartX=663.693 StartY=-363.944 StartZ=0 EndX=591.71 EndY=-363.944 EndZ=0
    g11: LineSegment StartX=591.71 StartY=-363.944 StartZ=0 EndX=615.357 EndY=-403.406 EndZ=0
    g12: LineSegment StartX=588.714 StartY=-358.944 StartZ=0 EndX=660.535 EndY=-358.944 EndZ=0
    g13: LineSegment StartX=660.535 StartY=-358.944 StartZ=0 EndX=637.231 EndY=-322.045 EndZ=0
    g14: LineSegment StartX=637.231 StartY=-322.045 StartZ=0 EndX=566.604 EndY=-322.045 EndZ=0
    g15: LineSegment StartX=566.604 StartY=-322.045 StartZ=0 EndX=588.714 EndY=-358.944 EndZ=0
    g16: LineSegment [constr] StartX=663.726 StartY=-495.8 StartZ=0 EndX=556.613 EndY=-317.045 EndZ=0
    g17: LineSegment [constr] StartX=755.399 StartY=-496.04 StartZ=0 EndX=640.429 EndY=-314 EndZ=0
  constraints (47):
    c: Horizontal(g0)
    c: Coincident(g0,g1)
    c: Coincident(g1,g2)
    c: Horizontal(g2)
    c: Coincident(g2,g3)
    c: Coincident(g3,g0)
    c: Horizontal(g4)
    c: Coincident(g4,g5)
    c: Coincident(g5,g6)
    c: Horizontal(g6)
    c: Coincident(g6,g7)
    c: Coincident(g7,g4)
    c: Horizontal(g8)
    c: Coincident(g8,g9)
    c: Coincident(g9,g10)
    c: Horizontal(g10)
    c: Coincident(g10,g11)
    c: Coincident(g11,g8)
    c: Horizontal(g12)
    c: Coincident(g12,g13)
    c: Coincident(g13,g14)
    c: Horizontal(g14)
    c: Coincident(g14,g15)
    c: Coincident(g15,g12)
    c: Distance(g0,g16) = 6
    c: Distance(g1,g16) = 6
    c: Block(g16)
    c: Distance(g4,g16) = 6
    c: Distance(g6,g16) = 6
    c: Distance(g8,g16) = 6
    c: Distance(g10,g16) = 6
    c: Distance(g12,g16) = 6
    c: Distance(g14,g16) = 6
    c: DistanceY(g2,g4) = 5
    c: DistanceY(g5,g8) = 5
    c: DistanceY(g9,g12) = 5
    c: DistanceY(g16,g0) = 7
    c: DistanceY(g14,g16) = 5
    c: Block(g17)
    c: Distance(g0,g17) = 7
    c: Distance(g2,g17) = 7
    c: Distance(g4,g17) = 7
    c: Distance(g5,g17) = 7
    c: Distance(g8,g17) = 7
    c: Distance(g9,g17) = 7
    c: Distance(g12,g17) = 7
    c: Distance(g13,g17) = 7
FEATURE [PartDesign::Pocket] Pocket086
  BaseFeature = -> Fillet
  Direction = (0,1,-2e-16)
  Length = 100
  Length2 = 5
  Profile = -> Sketch128
  ReferenceAxis = -> Sketch128 [N_Axis]
  Refine = true
  Reversed = true
  Suppressed = false
  Type = 0
FEATURE [PartDesign::Body] Body017
  AllowCompound = false
  Group = -> [Sketch117,Sketch116,AdditiveLoft016,Sketch118,Pocket076,Sketch119,Pocket077,Sketch120,Pocket078,DatumPlane021,Sketch121,Pocket079,Sketch122,Pocket080,Sketch123,Pocket081,DatumPlane022,Sketch124,Pocket082,Sketch125,Pocket083,DatumPlane023,Sketch126,Pocket084,Sketch127,Pocket085,Fillet,DatumPlane024,Sketch128,Pocket086]
  Origin = -> Origin017
  Placement = pos=(0,0,-100) rot=(0,0,1;0rad)
  Tip = -> Pocket086
FEATURE [Part::Mirroring] Part__Mirroring016  label="Body017 (Mirror #17)"
  Base = (0,0,0)
  Normal = (0,0,1)
  Source = -> Body017
FEATURE [Sketcher::SketchObject] Sketch129
  ArcFitTolerance = 1e-06
  FullyConstrained = false
  MakeInternals = false
  Placement = pos=(600,0,-600) rot=(0,0,1;0rad)
  sketch-geometry (123):
    g0: BSplineCurve PolesCount=61 KnotsCount=61 Degree=3 IsPeriodic=1
    g1-g61: Circle [constr] x61 (B-spline internal-alignment scaffolding for g0; pole/knot coordinates omitted)
    g62-g122: GeomPoint [constr] x61 (B-spline internal-alignment scaffolding for g0; pole/knot coordinates omitted)
  constraints (123):
    c: InternalAlignment(g1,g0)
    c: Weight(g1) = 1
    c: InternalAlignment(g2,g0)
    c: Equal(g2,g1)
    c: InternalAlignment(g3,g0)
    c: Equal(g3,g1)
    c: InternalAlignment(g4,g0)
    c: Equal(g4,g1)
    c: InternalAlignment(g5,g0)
    c: Equal(g5,g1)
    c: InternalAlignment(g6,g0)
    c: Equal(g6,g1)
    c: InternalAlignment(g7,g0)
    c: Equal(g7,g1)
    c: InternalAlignment(g8,g0)
    c: Equal(g8,g1)
    c: InternalAlignment(g9,g0)
    c: Equal(g9,g1)
    c: InternalAlignment(g10,g0)
    c: Equal(g10,g1)
    c: InternalAlignment(g11,g0)
    c: Equal(g11,g1)
    c: InternalAlignment(g12,g0)
    c: Equal(g12,g1)
    c: InternalAlignment(g13,g0)
    c: Equal(g13,g1)
    c: InternalAlignment(g14,g0)
    c: Equal(g14,g1)
    c: InternalAlignment(g15,g0)
    c: Equal(g15,g1)
    c: InternalAlignment(g16,g0)
    c: Equal(g16,g1)
    c: InternalAlignment(g17,g0)
    c: Equal(g17,g1)
    c: InternalAlignment(g18,g0)
    c: Equal(g18,g1)
    c: InternalAlignment(g19,g0)
    c: Equal(g19,g1)
    c: InternalAlignment(g20,g0)
    c: Equal(g20,g1)
    c: InternalAlignment(g21,g0)
    c: Equal(g21,g1)
    c: InternalAlignment(g22,g0)
    c: Equal(g22,g1)
    c: InternalAlignment(g23,g0)
    c: Equal(g23,g1)
    c: InternalAlignment(g24,g0)
    c: Equal(g24,g1)
    c: InternalAlignment(g25,g0)
    c: Equal(g25,g1)
    c: InternalAlignment(g26,g0)
    c: Equal(g26,g1)
    c: InternalAlignment(g27,g0)
    c: Equal(g27,g1)
    c: InternalAlignment(g28,g0)
    c: Equal(g28,g1)
    c: InternalAlignment(g29,g0)
    c: Equal(g29,g1)
    c: InternalAlignment(g30,g0)
    c: Equal(g30,g1)
    c: InternalAlignment(g31,g0)
    c: Equal(g31,g1)
    c: InternalAlignment(g32,g0)
    c: Equal(g32,g1)
    c: InternalAlignment(g33,g0)
    c: Equal(g33,g1)
    c: InternalAlignment(g34,g0)
    c: Equal(g34,g1)
    c: InternalAlignment(g35,g0)
    c: Equal(g35,g1)
    c: InternalAlignment(g36,g0)
    c: Equal(g36,g1)
    c: InternalAlignment(g37,g0)
    c: Equal(g37,g1)
    c: InternalAlignment(g38,g0)
    c: Equal(g38,g1)
    c: InternalAlignment(g39,g0)
    c: Equal(g39,g1)
    c: InternalAlignment(g40,g0)
    c: Equal(g40,g1)
    c: InternalAlignment(g41,g0)
    c: Equal(g41,g1)
    c: InternalAlignment(g42,g0)
    c: Equal(g42,g1)
    c: InternalAlignment(g43,g0)
    c: Equal(g43,g1)
    c: InternalAlignment(g44,g0)
    c: Equal(g44,g1)
    c: InternalAlignment(g45,g0)
    c: Equal(g45,g1)
    c: InternalAlignment(g46,g0)
    c: Equal(g46,g1)
    c: InternalAlignment(g47,g0)
    c: Equal(g47,g1)
    c: InternalAlignment(g48,g0)
    c: Equal(g48,g1)
    c: InternalAlignment(g49,g0)
    c: Equal(g49,g1)
    c: InternalAlignment(g50,g0)
    c: Equal(g50,g1)
    c: InternalAlignment(g51,g0)
    c: Equal(g51,g1)
    c: InternalAlignment(g52,g0)
    c: Equal(g52,g1)
    c: InternalAlignment(g53,g0)
    c: Equal(g53,g1)
    c: InternalAlignment(g54,g0)
    c: Equal(g54,g1)
    c: InternalAlignment(g55,g0)
    c: Equal(g55,g1)
    c: InternalAlignment(g56,g0)
    c: Equal(g56,g1)
    c: InternalAlignment(g57,g0)
    c: Equal(g57,g1)
    c: InternalAlignment(g58,g0)
    c: Equal(g58,g1)
    c: InternalAlignment(g59,g0)
    c: Equal(g59,g1)
    c: InternalAlignment(g60,g0)
    c: Equal(g60,g1)
    c: InternalAlignment(g61,g0)
    c: Equal(g61,g1)
    c: InternalAlignment(g62-g122 -> g0) x61
FEATURE [Sketcher::SketchObject] Sketch130
  ArcFitTolerance = 1e-06
  FullyConstrained = false
  MakeInternals = false
  sketch-geometry (123):
    g0: BSplineCurve PolesCount=61 KnotsCount=61 Degree=3 IsPeriodic=1
    g1-g61: Circle [constr] x61 (B-spline internal-alignment scaffolding for g0; pole/knot coordinates omitted)
    g62-g122: GeomPoint [constr] x61 (B-spline internal-alignment scaffolding for g0; pole/knot coordinates omitted)
  constraints (123):
    c: InternalAlignment(g1,g0)
    c: Weight(g1) = 1
    c: InternalAlignment(g2,g0)
    c: Equal(g2,g1)
    c: InternalAlignment(g3,g0)
    c: Equal(g3,g1)
    c: InternalAlignment(g4,g0)
    c: Equal(g4,g1)
    c: InternalAlignment(g5,g0)
    c: Equal(g5,g1)
    c: InternalAlignment(g6,g0)
    c: Equal(g6,g1)
    c: InternalAlignment(g7,g0)
    c: Equal(g7,g1)
    c: InternalAlignment(g8,g0)
    c: Equal(g8,g1)
    c: InternalAlignment(g9,g0)
    c: Equal(g9,g1)
    c: InternalAlignment(g10,g0)
    c: Equal(g10,g1)
    c: InternalAlignment(g11,g0)
    c: Equal(g11,g1)
    c: InternalAlignment(g12,g0)
    c: Equal(g12,g1)
    c: InternalAlignment(g13,g0)
    c: Equal(g13,g1)
    c: InternalAlignment(g14,g0)
    c: Equal(g14,g1)
    c: InternalAlignment(g15,g0)
    c: Equal(g15,g1)
    c: InternalAlignment(g16,g0)
    c: Equal(g16,g1)
    c: InternalAlignment(g17,g0)
    c: Equal(g17,g1)
    c: InternalAlignment(g18,g0)
    c: Equal(g18,g1)
    c: InternalAlignment(g19,g0)
    c: Equal(g19,g1)
    c: InternalAlignment(g20,g0)
    c: Equal(g20,g1)
    c: InternalAlignment(g21,g0)
    c: Equal(g21,g1)
    c: InternalAlignment(g22,g0)
    c: Equal(g22,g1)
    c: InternalAlignment(g23,g0)
    c: Equal(g23,g1)
    c: InternalAlignment(g24,g0)
    c: Equal(g24,g1)
    c: InternalAlignment(g25,g0)
    c: Equal(g25,g1)
    c: InternalAlignment(g26,g0)
    c: Equal(g26,g1)
    c: InternalAlignment(g27,g0)
    c: Equal(g27,g1)
    c: InternalAlignment(g28,g0)
    c: Equal(g28,g1)
    c: InternalAlignment(g29,g0)
    c: Equal(g29,g1)
    c: InternalAlignment(g30,g0)
    c: Equal(g30,g1)
    c: InternalAlignment(g31,g0)
    c: Equal(g31,g1)
    c: InternalAlignment(g32,g0)
    c: Equal(g32,g1)
    c: InternalAlignment(g33,g0)
    c: Equal(g33,g1)
    c: InternalAlignment(g34,g0)
    c: Equal(g34,g1)
    c: InternalAlignment(g35,g0)
    c: Equal(g35,g1)
    c: InternalAlignment(g36,g0)
    c: Equal(g36,g1)
    c: InternalAlignment(g37,g0)
    c: Equal(g37,g1)
    c: InternalAlignment(g38,g0)
    c: Equal(g38,g1)
    c: InternalAlignment(g39,g0)
    c: Equal(g39,g1)
    c: InternalAlignment(g40,g0)
    c: Equal(g40,g1)
    c: InternalAlignment(g41,g0)
    c: Equal(g41,g1)
    c: InternalAlignment(g42,g0)
    c: Equal(g42,g1)
    c: InternalAlignment(g43,g0)
    c: Equal(g43,g1)
    c: InternalAlignment(g44,g0)
    c: Equal(g44,g1)
    c: InternalAlignment(g45,g0)
    c: Equal(g45,g1)
    c: InternalAlignment(g46,g0)
    c: Equal(g46,g1)
    c: InternalAlignment(g47,g0)
    c: Equal(g47,g1)
    c: InternalAlignment(g48,g0)
    c: Equal(g48,g1)
    c: InternalAlignment(g49,g0)
    c: Equal(g49,g1)
    c: InternalAlignment(g50,g0)
    c: Equal(g50,g1)
    c: InternalAlignment(g51,g0)
    c: Equal(g51,g1)
    c: InternalAlignment(g52,g0)
    c: Equal(g52,g1)
    c: InternalAlignment(g53,g0)
    c: Equal(g53,g1)
    c: InternalAlignment(g54,g0)
    c: Equal(g54,g1)
    c: InternalAlignment(g55,g0)
    c: Equal(g55,g1)
    c: InternalAlignment(g56,g0)
    c: Equal(g56,g1)
    c: InternalAlignment(g57,g0)
    c: Equal(g57,g1)
    c: InternalAlignment(g58,g0)
    c: Equal(g58,g1)
    c: InternalAlignment(g59,g0)
    c: Equal(g59,g1)
    c: InternalAlignment(g60,g0)
    c: Equal(g60,g1)
    c: InternalAlignment(g61,g0)
    c: Equal(g61,g1)
    c: InternalAlignment(g62-g122 -> g0) x61
FEATURE [PartDesign::AdditiveLoft] AdditiveLoft017
  Closed = false
  Profile = -> Sketch130
  Refine = true
  Ruled = false
  Sections = -> [Sketch129]
  Suppressed = false
FEATURE [Sketcher::SketchObject] Sketch131
  ArcFitTolerance = 1e-06
  AttachmentSupport = -> [AdditiveLoft017]
  FullyConstrained = false
  MakeInternals = false
  MapMode = 5
  Placement = pos=(0,0,-600) rot=(1,0,0;3.14159rad)
  sketch-geometry (4):
    g0: LineSegment StartX=-34.2169 StartY=87.65 StartZ=0 EndX=-34.2169 EndY=-91.6403 EndZ=0
    g1: LineSegment StartX=-34.2169 StartY=-91.6403 StartZ=0 EndX=961.453 EndY=-91.6403 EndZ=0
    g2: LineSegment StartX=961.453 StartY=-91.6403 StartZ=0 EndX=961.453 EndY=87.65 EndZ=0
    g3: LineSegment StartX=961.453 StartY=87.65 StartZ=0 EndX=-34.2169 EndY=87.65 EndZ=0
  constraints (8):
    c: Coincident(g0,g1)
    c: Coincident(g1,g2)
    c: Coincident(g2,g3)
    c: Coincident(g3,g0)
    c: Vertical(g0)
    c: Vertical(g2)
    c: Horizontal(g1)
    c: Horizontal(g3)
FEATURE [PartDesign::Pocket] Pocket087
  BaseFeature = -> AdditiveLoft017
  Direction = (0,0,1)
  Length = 10
  Length2 = 5
  Profile = -> Sketch131
  ReferenceAxis = -> Sketch131 [N_Axis]
  Refine = true
  Suppressed = false
  Type = 0
FEATURE [Sketcher::SketchObject] Sketch132
  ArcFitTolerance = 1e-06
  AttachmentSupport = -> [Pocket087]
  FullyConstrained = false
  MakeInternals = false
  MapMode = 5
  sketch-geometry (4):
    g0: LineSegment StartX=-133.424 StartY=119.332 StartZ=0 EndX=-133.424 EndY=-141.213 EndZ=0
    g1: LineSegment StartX=-133.424 StartY=-141.213 StartZ=0 EndX=913.95 EndY=-141.213 EndZ=0
    g2: LineSegment StartX=913.95 StartY=-141.213 StartZ=0 EndX=913.95 EndY=119.332 EndZ=0
    g3: LineSegment StartX=913.95 StartY=119.332 StartZ=0 EndX=-133.424 EndY=119.332 EndZ=0
  constraints (8):
    c: Coincident(g0,g1)
    c: Coincident(g1,g2)
    c: Coincident(g2,g3)
    c: Coincident(g3,g0)
    c: Vertical(g0)
    c: Vertical(g2)
    c: Horizontal(g1)
    c: Horizontal(g3)
FEATURE [PartDesign::Pocket] Pocket088
  BaseFeature = -> Pocket087
  Direction = (0,0,-1)
  Length = 510
  Length2 = 5
  Profile = -> Sketch132
  ReferenceAxis = -> Sketch132 [N_Axis]
  Refine = true
  Suppressed = false
  Type = 0
FEATURE [Sketcher::SketchObject] Sketch133
  ArcFitTolerance = 1e-06
  AttachmentSupport = -> [YZ_Plane018]
  FullyConstrained = false
  MakeInternals = false
  MapMode = 5
  Placement = pos=(0,0,0) rot=(0.57735,0.57735,0.57735;2.0944rad)
  sketch-geometry (4):
    g0: LineSegment StartX=-107.246 StartY=-409.309 StartZ=0 EndX=-107.246 EndY=-702.534 EndZ=0
    g1: LineSegment StartX=-107.246 StartY=-702.534 StartZ=0 EndX=230.997 EndY=-702.534 EndZ=0
    g2: LineSegment StartX=230.997 StartY=-702.534 StartZ=0 EndX=230.997 EndY=-409.309 EndZ=0
    g3: LineSegment StartX=230.997 StartY=-409.309 StartZ=0 EndX=-107.246 EndY=-409.309 EndZ=0
  constraints (8):
    c: Coincident(g0,g1)
    c: Coincident(g1,g2)
    c: Coincident(g2,g3)
    c: Coincident(g3,g0)
    c: Vertical(g0)
    c: Vertical(g2)
    c: Horizontal(g1)
    c: Horizontal(g3)
FEATURE [PartDesign::Pocket] Pocket089
  BaseFeature = -> Pocket088
  Direction = (-1,0,0)
  Length = 685
  Length2 = 5
  Profile = -> Sketch133
  ReferenceAxis = -> Sketch133 [N_Axis]
  Refine = true
  Reversed = true
  Suppressed = false
  Type = 0
FEATURE [PartDesign::Plane] DatumPlane025
  AttachmentOffset = pos=(0,0,-200) rot=(0,0,1;0rad)
  AttachmentSupport = -> [Pocket089]
  Length = 85.0714
  MapMode = 5
  Placement = pos=(885,0,0) rot=(0.57735,-0.57735,-0.57735;2.0944rad)
  ResizeMode = 0
  Width = 650.071
FEATURE [Sketcher::SketchObject] Sketch134
  ArcFitTolerance = 1e-06
  AttachmentSupport = -> [DatumPlane025]
  FullyConstrained = false
  MakeInternals = false
  MapMode = 5
  Placement = pos=(885,0,0) rot=(0.57735,-0.57735,-0.57735;2.0944rad)
  sketch-geometry (4):
    g0: LineSegment StartX=-89.271 StartY=-435.29 StartZ=0 EndX=-89.271 EndY=-641.669 EndZ=0
    g1: LineSegment StartX=-89.271 StartY=-641.669 StartZ=0 EndX=88.6797 EndY=-641.669 EndZ=0
    g2: LineSegment StartX=88.6797 StartY=-641.669 StartZ=0 EndX=88.6797 EndY=-435.29 EndZ=0
    g3: LineSegment StartX=88.6797 StartY=-435.29 StartZ=0 EndX=-89.271 EndY=-435.29 EndZ=0
  constraints (8):
    c: Coincident(g0,g1)
    c: Coincident(g1,g2)
    c: Coincident(g2,g3)
    c: Coincident(g3,g0)
    c: Vertical(g0)
    c: Vertical(g2)
    c: Horizontal(g1)
    c: Horizontal(g3)
FEATURE [PartDesign::Pocket] Pocket090
  BaseFeature = -> Pocket089
  Direction = (1,0,0)
  Length = 190
  Length2 = 5
  Profile = -> Sketch134
  ReferenceAxis = -> Sketch134 [N_Axis]
  Refine = true
  Reversed = true
  Suppressed = false
  Type = 0
FEATURE [Sketcher::SketchObject] Sketch135
  ArcFitTolerance = 1e-06
  AttachmentSupport = -> [Pocket090]
  FullyConstrained = false
  MakeInternals = false
  MapMode = 5
  Placement = pos=(685,0,0) rot=(0.57735,-0.57735,-0.57735;2.0944rad)
  sketch-geometry (19):
    g0: LineSegment StartX=-0.529475 StartY=-585.56 StartZ=0 EndX=-12.971 EndY=-585.56 EndZ=0
    g1: LineSegment StartX=-12.971 StartY=-585.56 StartZ=0 EndX=-12.5148 EndY=-574.211 EndZ=0
    g2: LineSegment StartX=-12.5148 StartY=-574.211 StartZ=0 EndX=-12.2602 EndY=-567.188 EndZ=0
    g3: LineSegment StartX=-12.2602 StartY=-567.188 StartZ=0 EndX=-1.22185 EndY=-559.199 EndZ=0
    g4: LineSegment StartX=-1.22185 StartY=-559.199 StartZ=0 EndX=-0.935579 EndY=-571.753 EndZ=0
    g5: LineSegment StartX=-0.935579 StartY=-571.753 StartZ=0 EndX=-0.529475 EndY=-585.56 EndZ=0
    g6: LineSegment StartX=-12.5683 StartY=-562.842 StartZ=0 EndX=-1.329 EndY=-554.708 EndZ=0
    g7: LineSegment StartX=-1.329 StartY=-554.708 StartZ=0 EndX=-1.41925 EndY=-541.644 EndZ=0
    g8: LineSegment StartX=-1.41925 StartY=-541.644 StartZ=0 EndX=-1.56692 EndY=-533.3 EndZ=0
    g9: LineSegment StartX=-1.56692 StartY=-533.3 StartZ=0 EndX=-10.6702 EndY=-526.475 EndZ=0
    g10: LineSegment StartX=-10.6702 StartY=-526.475 StartZ=0 EndX=-11.6457 EndY=-544.782 EndZ=0
    g11: LineSegment StartX=-11.6457 StartY=-544.782 StartZ=0 EndX=-12.1622 EndY=-556.714 EndZ=0
    g12: LineSegment StartX=-12.1622 StartY=-556.714 StartZ=0 EndX=-12.5683 EndY=-562.842 EndZ=0
    g13: LineSegment StartX=-10.6668 StartY=-521.485 StartZ=0 EndX=-1.35614 EndY=-528.466 EndZ=0
    g14: LineSegment StartX=-1.35614 StartY=-528.466 StartZ=0 EndX=-1.53 EndY=-521.006 EndZ=0
    g15: LineSegment StartX=-1.53 StartY=-521.006 StartZ=0 EndX=-1.71459 EndY=-514.435 EndZ=0
    g16: LineSegment StartX=-1.71459 StartY=-514.435 StartZ=0 EndX=-10.1689 EndY=-514.435 EndZ=0
    g17: LineSegment StartX=-10.1689 StartY=-514.435 StartZ=0 EndX=-10.3904 EndY=-517.905 EndZ=0
    g18: LineSegment StartX=-10.3904 StartY=-517.905 StartZ=0 EndX=-10.6668 EndY=-521.485 EndZ=0
  constraints (23):
    c: Horizontal(g0)
    c: Coincident(g0,g1)
    c: Coincident(g1,g2)
    c: Coincident(g2,g3)
    c: Coincident(g3,g4)
    c: Coincident(g4,g5)
    c: Coincident(g5,g0)
    c: Coincident(g6,g7)
    c: Coincident(g7,g8)
    c: Coincident(g8,g9)
    c: Coincident(g9,g10)
    c: Coincident(g10,g11)
    c: Coincident(g11,g12)
    c: Coincident(g12,g6)
    c: Coincident(g13,g14)
    c: Coincident(g14,g15)
    c: Coincident(g15,g16)
    c: Horizontal(g16)
    c: Coincident(g16,g17)
    c: Coincident(g17,g18)
    c: Coincident(g18,g13)
    c: Parallel(g3,g6)
    c: Parallel(g9,g13)
FEATURE [PartDesign::Pocket] Pocket091
  BaseFeature = -> Pocket090
  Direction = (1,0,0)
  Length = 15
  Length2 = 5
  Profile = -> Sketch135
  ReferenceAxis = -> Sketch135 [N_Axis]
  Refine = true
  Suppressed = false
  Type = 0
FEATURE [PartDesign::Body] Body018
  AllowCompound = false
  Group = -> [Sketch130,Sketch129,AdditiveLoft017,Sketch131,Pocket087,Sketch132,Pocket088,Sketch133,Pocket089,DatumPlane025,Sketch134,Pocket090,Sketch135,Pocket091]
  Origin = -> Origin018
  Placement = pos=(0,0,-100) rot=(0,0,1;0rad)
  Tip = -> Pocket091
FEATURE [Part::Mirroring] Part__Mirroring017  label="Body018 (Mirror #18)"
  Base = (0,0,0)
  Normal = (0,0,1)
  Source = -> Body018
FEATURE [Sketcher::SketchObject] Sketch136
  ArcFitTolerance = 1e-06
  FullyConstrained = false
  MakeInternals = false
  Placement = pos=(600,0,-600) rot=(0,0,1;0rad)
  sketch-geometry (123):
    g0: BSplineCurve PolesCount=61 KnotsCount=61 Degree=3 IsPeriodic=1
    g1-g61: Circle [constr] x61 (B-spline internal-alignment scaffolding for g0; pole/knot coordinates omitted)
    g62-g122: GeomPoint [constr] x61 (B-spline internal-alignment scaffolding for g0; pole/knot coordinates omitted)
  constraints (123):
    c: InternalAlignment(g1,g0)
    c: Weight(g1) = 1
    c: InternalAlignment(g2,g0)
    c: Equal(g2,g1)
    c: InternalAlignment(g3,g0)
    c: Equal(g3,g1)
    c: InternalAlignment(g4,g0)
    c: Equal(g4,g1)
    c: InternalAlignment(g5,g0)
    c: Equal(g5,g1)
    c: InternalAlignment(g6,g0)
    c: Equal(g6,g1)
    c: InternalAlignment(g7,g0)
    c: Equal(g7,g1)
    c: InternalAlignment(g8,g0)
    c: Equal(g8,g1)
    c: InternalAlignment(g9,g0)
    c: Equal(g9,g1)
    c: InternalAlignment(g10,g0)
    c: Equal(g10,g1)
    c: InternalAlignment(g11,g0)
    c: Equal(g11,g1)
    c: InternalAlignment(g12,g0)
    c: Equal(g12,g1)
    c: InternalAlignment(g13,g0)
    c: Equal(g13,g1)
    c: InternalAlignment(g14,g0)
    c: Equal(g14,g1)
    c: InternalAlignment(g15,g0)
    c: Equal(g15,g1)
    c: InternalAlignment(g16,g0)
    c: Equal(g16,g1)
    c: InternalAlignment(g17,g0)
    c: Equal(g17,g1)
    c: InternalAlignment(g18,g0)
    c: Equal(g18,g1)
    c: InternalAlignment(g19,g0)
    c: Equal(g19,g1)
    c: InternalAlignment(g20,g0)
    c: Equal(g20,g1)
    c: InternalAlignment(g21,g0)
    c: Equal(g21,g1)
    c: InternalAlignment(g22,g0)
    c: Equal(g22,g1)
    c: InternalAlignment(g23,g0)
    c: Equal(g23,g1)
    c: InternalAlignment(g24,g0)
    c: Equal(g24,g1)
    c: InternalAlignment(g25,g0)
    c: Equal(g25,g1)
    c: InternalAlignment(g26,g0)
    c: Equal(g26,g1)
    c: InternalAlignment(g27,g0)
    c: Equal(g27,g1)
    c: InternalAlignment(g28,g0)
    c: Equal(g28,g1)
    c: InternalAlignment(g29,g0)
    c: Equal(g29,g1)
    c: InternalAlignment(g30,g0)
    c: Equal(g30,g1)
    c: InternalAlignment(g31,g0)
    c: Equal(g31,g1)
    c: InternalAlignment(g32,g0)
    c: Equal(g32,g1)
    c: InternalAlignment(g33,g0)
    c: Equal(g33,g1)
    c: InternalAlignment(g34,g0)
    c: Equal(g34,g1)
    c: InternalAlignment(g35,g0)
    c: Equal(g35,g1)
    c: InternalAlignment(g36,g0)
    c: Equal(g36,g1)
    c: InternalAlignment(g37,g0)
    c: Equal(g37,g1)
    c: InternalAlignment(g38,g0)
    c: Equal(g38,g1)
    c: InternalAlignment(g39,g0)
    c: Equal(g39,g1)
    c: InternalAlignment(g40,g0)
    c: Equal(g40,g1)
    c: InternalAlignment(g41,g0)
    c: Equal(g41,g1)
    c: InternalAlignment(g42,g0)
    c: Equal(g42,g1)
    c: InternalAlignment(g43,g0)
    c: Equal(g43,g1)
    c: InternalAlignment(g44,g0)
    c: Equal(g44,g1)
    c: InternalAlignment(g45,g0)
    c: Equal(g45,g1)
    c: InternalAlignment(g46,g0)
    c: Equal(g46,g1)
    c: InternalAlignment(g47,g0)
    c: Equal(g47,g1)
    c: InternalAlignment(g48,g0)
    c: Equal(g48,g1)
    c: InternalAlignment(g49,g0)
    c: Equal(g49,g1)
    c: InternalAlignment(g50,g0)
    c: Equal(g50,g1)
    c: InternalAlignment(g51,g0)
    c: Equal(g51,g1)
    c: InternalAlignment(g52,g0)
    c: Equal(g52,g1)
    c: InternalAlignment(g53,g0)
    c: Equal(g53,g1)
    c: InternalAlignment(g54,g0)
    c: Equal(g54,g1)
    c: InternalAlignment(g55,g0)
    c: Equal(g55,g1)
    c: InternalAlignment(g56,g0)
    c: Equal(g56,g1)
    c: InternalAlignment(g57,g0)
    c: Equal(g57,g1)
    c: InternalAlignment(g58,g0)
    c: Equal(g58,g1)
    c: InternalAlignment(g59,g0)
    c: Equal(g59,g1)
    c: InternalAlignment(g60,g0)
    c: Equal(g60,g1)
    c: InternalAlignment(g61,g0)
    c: Equal(g61,g1)
    c: InternalAlignment(g62-g122 -> g0) x61
FEATURE [Sketcher::SketchObject] Sketch137
  ArcFitTolerance = 1e-06
  FullyConstrained = false
  MakeInternals = false
  sketch-geometry (123):
    g0: BSplineCurve PolesCount=61 KnotsCount=61 Degree=3 IsPeriodic=1
    g1-g61: Circle [constr] x61 (B-spline internal-alignment scaffolding for g0; pole/knot coordinates omitted)
    g62-g122: GeomPoint [constr] x61 (B-spline internal-alignment scaffolding for g0; pole/knot coordinates omitted)
  constraints (123):
    c: InternalAlignment(g1,g0)
    c: Weight(g1) = 1
    c: InternalAlignment(g2,g0)
    c: Equal(g2,g1)
    c: InternalAlignment(g3,g0)
    c: Equal(g3,g1)
    c: InternalAlignment(g4,g0)
    c: Equal(g4,g1)
    c: InternalAlignment(g5,g0)
    c: Equal(g5,g1)
    c: InternalAlignment(g6,g0)
    c: Equal(g6,g1)
    c: InternalAlignment(g7,g0)
    c: Equal(g7,g1)
    c: InternalAlignment(g8,g0)
    c: Equal(g8,g1)
    c: InternalAlignment(g9,g0)
    c: Equal(g9,g1)
    c: InternalAlignment(g10,g0)
    c: Equal(g10,g1)
    c: InternalAlignment(g11,g0)
    c: Equal(g11,g1)
    c: InternalAlignment(g12,g0)
    c: Equal(g12,g1)
    c: InternalAlignment(g13,g0)
    c: Equal(g13,g1)
    c: InternalAlignment(g14,g0)
    c: Equal(g14,g1)
    c: InternalAlignment(g15,g0)
    c: Equal(g15,g1)
    c: InternalAlignment(g16,g0)
    c: Equal(g16,g1)
    c: InternalAlignment(g17,g0)
    c: Equal(g17,g1)
    c: InternalAlignment(g18,g0)
    c: Equal(g18,g1)
    c: InternalAlignment(g19,g0)
    c: Equal(g19,g1)
    c: InternalAlignment(g20,g0)
    c: Equal(g20,g1)
    c: InternalAlignment(g21,g0)
    c: Equal(g21,g1)
    c: InternalAlignment(g22,g0)
    c: Equal(g22,g1)
    c: InternalAlignment(g23,g0)
    c: Equal(g23,g1)
    c: InternalAlignment(g24,g0)
    c: Equal(g24,g1)
    c: InternalAlignment(g25,g0)
    c: Equal(g25,g1)
    c: InternalAlignment(g26,g0)
    c: Equal(g26,g1)
    c: InternalAlignment(g27,g0)
    c: Equal(g27,g1)
    c: InternalAlignment(g28,g0)
    c: Equal(g28,g1)
    c: InternalAlignment(g29,g0)
    c: Equal(g29,g1)
    c: InternalAlignment(g30,g0)
    c: Equal(g30,g1)
    c: InternalAlignment(g31,g0)
    c: Equal(g31,g1)
    c: InternalAlignment(g32,g0)
    c: Equal(g32,g1)
    c: InternalAlignment(g33,g0)
    c: Equal(g33,g1)
    c: InternalAlignment(g34,g0)
    c: Equal(g34,g1)
    c: InternalAlignment(g35,g0)
    c: Equal(g35,g1)
    c: InternalAlignment(g36,g0)
    c: Equal(g36,g1)
    c: InternalAlignment(g37,g0)
    c: Equal(g37,g1)
    c: InternalAlignment(g38,g0)
    c: Equal(g38,g1)
    c: InternalAlignment(g39,g0)
    c: Equal(g39,g1)
    c: InternalAlignment(g40,g0)
    c: Equal(g40,g1)
    c: InternalAlignment(g41,g0)
    c: Equal(g41,g1)
    c: InternalAlignment(g42,g0)
    c: Equal(g42,g1)
    c: InternalAlignment(g43,g0)
    c: Equal(g43,g1)
    c: InternalAlignment(g44,g0)
    c: Equal(g44,g1)
    c: InternalAlignment(g45,g0)
    c: Equal(g45,g1)
    c: InternalAlignment(g46,g0)
    c: Equal(g46,g1)
    c: InternalAlignment(g47,g0)
    c: Equal(g47,g1)
    c: InternalAlignment(g48,g0)
    c: Equal(g48,g1)
    c: InternalAlignment(g49,g0)
    c: Equal(g49,g1)
    c: InternalAlignment(g50,g0)
    c: Equal(g50,g1)
    c: InternalAlignment(g51,g0)
    c: Equal(g51,g1)
    c: InternalAlignment(g52,g0)
    c: Equal(g52,g1)
    c: InternalAlignment(g53,g0)
    c: Equal(g53,g1)
    c: InternalAlignment(g54,g0)
    c: Equal(g54,g1)
    c: InternalAlignment(g55,g0)
    c: Equal(g55,g1)
    c: InternalAlignment(g56,g0)
    c: Equal(g56,g1)
    c: InternalAlignment(g57,g0)
    c: Equal(g57,g1)
    c: InternalAlignment(g58,g0)
    c: Equal(g58,g1)
    c: InternalAlignment(g59,g0)
    c: Equal(g59,g1)
    c: InternalAlignment(g60,g0)
    c: Equal(g60,g1)
    c: InternalAlignment(g61,g0)
    c: Equal(g61,g1)
    c: InternalAlignment(g62-g122 -> g0) x61
FEATURE [PartDesign::AdditiveLoft] AdditiveLoft018
  Closed = false
  Profile = -> Sketch137
  Refine = true
  Ruled = false
  Sections = -> [Sketch136]
  Suppressed = false
FEATURE [PartDesign::Plane] DatumPlane026
  AttachmentOffset = pos=(0,0,0) rot=(0,-1,0;0.785398rad)
  AttachmentSupport = -> [AdditiveLoft018]
  Length = 206.104
  MapMode = 5
  Placement = pos=(0,0,0) rot=(0,-1,0;0.785398rad)
  ResizeMode = 0
  Width = 69.3275
FEATURE [Sketcher::SketchObject] Sketch138
  ArcFitTolerance = 1e-06
  AttachmentSupport = -> [DatumPlane026]
  FullyConstrained = false
  MakeInternals = false
  MapMode = 5
  Placement = pos=(0,0,0) rot=(0,-1,0;0.785398rad)
  sketch-geometry (1):
    g0: Circle CenterX=28.3343 CenterY=4.75298 CenterZ=0 NormalX=0 NormalY=0 NormalZ=1 AngleXU=0 Radius=4.1
  constraints (1):
    c: Diameter(g0) = 8.2
FEATURE [PartDesign::Pocket] Pocket092
  BaseFeature = -> AdditiveLoft018
  Direction = (0.707107,0,-0.707107)
  Length = 1000
  Length2 = 5
  Profile = -> Sketch138
  ReferenceAxis = -> Sketch138 [N_Axis]
  Refine = true
  Suppressed = false
  Type = 0
FEATURE [Sketcher::SketchObject] Sketch139
  ArcFitTolerance = 1e-06
  AttachmentSupport = -> [Pocket092]
  FullyConstrained = false
  MakeInternals = false
  MapMode = 5
  Placement = pos=(0,0,-600) rot=(1,0,0;3.14159rad)
  sketch-geometry (4):
    g0: LineSegment StartX=-85.1873 StartY=206.739 StartZ=0 EndX=-85.1873 EndY=-145.098 EndZ=0
    g1: LineSegment StartX=-85.1873 StartY=-145.098 StartZ=0 EndX=963.672 EndY=-145.098 EndZ=0
    g2: LineSegment StartX=963.672 StartY=-145.098 StartZ=0 EndX=963.672 EndY=206.739 EndZ=0
    g3: LineSegment StartX=963.672 StartY=206.739 StartZ=0 EndX=-85.1873 EndY=206.739 EndZ=0
  constraints (8):
    c: Coincident(g0,g1)
    c: Coincident(g1,g2)
    c: Coincident(g2,g3)
    c: Coincident(g3,g0)
    c: Vertical(g0)
    c: Vertical(g2)
    c: Horizontal(g1)
    c: Horizontal(g3)
FEATURE [PartDesign::Plane] DatumPlane027
  AttachmentOffset = pos=(0,0,0) rot=(0,-1,0;0.785398rad)
  AttachmentSupport = -> [Pocket092]
  Length = 206.104
  MapMode = 5
  Placement = pos=(0,0,0) rot=(0,-1,0;0.785398rad)
  ResizeMode = 0
  Width = 69.3275
FEATURE [Sketcher::SketchObject] Sketch140
  ArcFitTolerance = 1e-06
  AttachmentSupport = -> [DatumPlane027]
  FullyConstrained = false
  MakeInternals = false
  MapMode = 5
  Placement = pos=(0,0,0) rot=(0,-1,0;0.785398rad)
  sketch-geometry (4):
    g0: LineSegment StartX=10 StartY=77.8136 StartZ=0 EndX=10 EndY=-127.239 EndZ=0
    g1: LineSegment StartX=10 StartY=-127.239 StartZ=0 EndX=548.763 EndY=-127.239 EndZ=0
    g2: LineSegment StartX=548.763 StartY=-127.239 StartZ=0 EndX=548.763 EndY=77.8136 EndZ=0
    g3: LineSegment StartX=548.763 StartY=77.8136 StartZ=0 EndX=10 EndY=77.8136 EndZ=0
  constraints (9):
    c: Coincident(g0,g1)
    c: Coincident(g1,g2)
    c: Coincident(g2,g3)
    c: Coincident(g3,g0)
    c: Vertical(g0)
    c: Vertical(g2)
    c: Horizontal(g1)
    c: Horizontal(g3)
    c: Distance(g-1,g0) = 10
FEATURE [PartDesign::Pocket] Pocket093
  BaseFeature = -> Pocket092
  Direction = (0.707107,0,-0.707107)
  Length = 1000
  Length2 = 5
  Profile = -> Sketch140
  ReferenceAxis = -> Sketch140 [N_Axis]
  Refine = true
  Suppressed = false
  Type = 0
FEATURE [Sketcher::SketchObject] Sketch141
  ArcFitTolerance = 1e-06
  AttachmentSupport = -> [Pocket093]
  FullyConstrained = false
  MakeInternals = false
  MapMode = 5
  sketch-geometry (4):
    g0: LineSegment StartX=-129.575 StartY=195.424 StartZ=0 EndX=-129.575 EndY=-278.238 EndZ=0
    g1: LineSegment StartX=-129.575 StartY=-278.238 StartZ=0 EndX=1282.72 EndY=-278.238 EndZ=0
    g2: LineSegment StartX=1282.72 StartY=-278.238 StartZ=0 EndX=1282.72 EndY=195.424 EndZ=0
    g3: LineSegment StartX=1282.72 StartY=195.424 StartZ=0 EndX=-129.575 EndY=195.424 EndZ=0
  constraints (8):
    c: Coincident(g0,g1)
    c: Coincident(g1,g2)
    c: Coincident(g2,g3)
    c: Coincident(g3,g0)
    c: Vertical(g0)
    c: Vertical(g2)
    c: Horizontal(g1)
    c: Horizontal(g3)
FEATURE [Sketcher::SketchObject] Sketch142
  ArcFitTolerance = 1e-06
  FullyConstrained = false
  MakeInternals = false
  Placement = pos=(600,0,-600) rot=(0,0,1;0rad)
  sketch-geometry (123):
    g0: BSplineCurve PolesCount=61 KnotsCount=61 Degree=3 IsPeriodic=1
    g1-g61: Circle [constr] x61 (B-spline internal-alignment scaffolding for g0; pole/knot coordinates omitted)
    g62-g122: GeomPoint [constr] x61 (B-spline internal-alignment scaffolding for g0; pole/knot coordinates omitted)
  constraints (123):
    c: InternalAlignment(g1,g0)
    c: Weight(g1) = 1
    c: InternalAlignment(g2,g0)
    c: Equal(g2,g1)
    c: InternalAlignment(g3,g0)
    c: Equal(g3,g1)
    c: InternalAlignment(g4,g0)
    c: Equal(g4,g1)
    c: InternalAlignment(g5,g0)
    c: Equal(g5,g1)
    c: InternalAlignment(g6,g0)
    c: Equal(g6,g1)
    c: InternalAlignment(g7,g0)
    c: Equal(g7,g1)
    c: InternalAlignment(g8,g0)
    c: Equal(g8,g1)
    c: InternalAlignment(g9,g0)
    c: Equal(g9,g1)
    c: InternalAlignment(g10,g0)
    c: Equal(g10,g1)
    c: InternalAlignment(g11,g0)
    c: Equal(g11,g1)
    c: InternalAlignment(g12,g0)
    c: Equal(g12,g1)
    c: InternalAlignment(g13,g0)
    c: Equal(g13,g1)
    c: InternalAlignment(g14,g0)
    c: Equal(g14,g1)
    c: InternalAlignment(g15,g0)
    c: Equal(g15,g1)
    c: InternalAlignment(g16,g0)
    c: Equal(g16,g1)
    c: InternalAlignment(g17,g0)
    c: Equal(g17,g1)
    c: InternalAlignment(g18,g0)
    c: Equal(g18,g1)
    c: InternalAlignment(g19,g0)
    c: Equal(g19,g1)
    c: InternalAlignment(g20,g0)
    c: Equal(g20,g1)
    c: InternalAlignment(g21,g0)
    c: Equal(g21,g1)
    c: InternalAlignment(g22,g0)
    c: Equal(g22,g1)
    c: InternalAlignment(g23,g0)
    c: Equal(g23,g1)
    c: InternalAlignment(g24,g0)
    c: Equal(g24,g1)
    c: InternalAlignment(g25,g0)
    c: Equal(g25,g1)
    c: InternalAlignment(g26,g0)
    c: Equal(g26,g1)
    c: InternalAlignment(g27,g0)
    c: Equal(g27,g1)
    c: InternalAlignment(g28,g0)
    c: Equal(g28,g1)
    c: InternalAlignment(g29,g0)
    c: Equal(g29,g1)
    c: InternalAlignment(g30,g0)
    c: Equal(g30,g1)
    c: InternalAlignment(g31,g0)
    c: Equal(g31,g1)
    c: InternalAlignment(g32,g0)
    c: Equal(g32,g1)
    c: InternalAlignment(g33,g0)
    c: Equal(g33,g1)
    c: InternalAlignment(g34,g0)
    c: Equal(g34,g1)
    c: InternalAlignment(g35,g0)
    c: Equal(g35,g1)
    c: InternalAlignment(g36,g0)
    c: Equal(g36,g1)
    c: InternalAlignment(g37,g0)
    c: Equal(g37,g1)
    c: InternalAlignment(g38,g0)
    c: Equal(g38,g1)
    c: InternalAlignment(g39,g0)
    c: Equal(g39,g1)
    c: InternalAlignment(g40,g0)
    c: Equal(g40,g1)
    c: InternalAlignment(g41,g0)
    c: Equal(g41,g1)
    c: InternalAlignment(g42,g0)
    c: Equal(g42,g1)
    c: InternalAlignment(g43,g0)
    c: Equal(g43,g1)
    c: InternalAlignment(g44,g0)
    c: Equal(g44,g1)
    c: InternalAlignment(g45,g0)
    c: Equal(g45,g1)
    c: InternalAlignment(g46,g0)
    c: Equal(g46,g1)
    c: InternalAlignment(g47,g0)
    c: Equal(g47,g1)
    c: InternalAlignment(g48,g0)
    c: Equal(g48,g1)
    c: InternalAlignment(g49,g0)
    c: Equal(g49,g1)
    c: InternalAlignment(g50,g0)
    c: Equal(g50,g1)
    c: InternalAlignment(g51,g0)
    c: Equal(g51,g1)
    c: InternalAlignment(g52,g0)
    c: Equal(g52,g1)
    c: InternalAlignment(g53,g0)
    c: Equal(g53,g1)
    c: InternalAlignment(g54,g0)
    c: Equal(g54,g1)
    c: InternalAlignment(g55,g0)
    c: Equal(g55,g1)
    c: InternalAlignment(g56,g0)
    c: Equal(g56,g1)
    c: InternalAlignment(g57,g0)
    c: Equal(g57,g1)
    c: InternalAlignment(g58,g0)
    c: Equal(g58,g1)
    c: InternalAlignment(g59,g0)
    c: Equal(g59,g1)
    c: InternalAlignment(g60,g0)
    c: Equal(g60,g1)
    c: InternalAlignment(g61,g0)
    c: Equal(g61,g1)
    c: InternalAlignment(g62-g122 -> g0) x61
FEATURE [Sketcher::SketchObject] Sketch143
  ArcFitTolerance = 1e-06
  FullyConstrained = false
  MakeInternals = false
  sketch-geometry (123):
    g0: BSplineCurve PolesCount=61 KnotsCount=61 Degree=3 IsPeriodic=1
    g1-g61: Circle [constr] x61 (B-spline internal-alignment scaffolding for g0; pole/knot coordinates omitted)
    g62-g122: GeomPoint [constr] x61 (B-spline internal-alignment scaffolding for g0; pole/knot coordinates omitted)
  constraints (123):
    c: InternalAlignment(g1,g0)
    c: Weight(g1) = 1
    c: InternalAlignment(g2,g0)
    c: Equal(g2,g1)
    c: InternalAlignment(g3,g0)
    c: Equal(g3,g1)
    c: InternalAlignment(g4,g0)
    c: Equal(g4,g1)
    c: InternalAlignment(g5,g0)
    c: Equal(g5,g1)
    c: InternalAlignment(g6,g0)
    c: Equal(g6,g1)
    c: InternalAlignment(g7,g0)
    c: Equal(g7,g1)
    c: InternalAlignment(g8,g0)
    c: Equal(g8,g1)
    c: InternalAlignment(g9,g0)
    c: Equal(g9,g1)
    c: InternalAlignment(g10,g0)
    c: Equal(g10,g1)
    c: InternalAlignment(g11,g0)
    c: Equal(g11,g1)
    c: InternalAlignment(g12,g0)
    c: Equal(g12,g1)
    c: InternalAlignment(g13,g0)
    c: Equal(g13,g1)
    c: InternalAlignment(g14,g0)
    c: Equal(g14,g1)
    c: InternalAlignment(g15,g0)
    c: Equal(g15,g1)
    c: InternalAlignment(g16,g0)
    c: Equal(g16,g1)
    c: InternalAlignment(g17,g0)
    c: Equal(g17,g1)
    c: InternalAlignment(g18,g0)
    c: Equal(g18,g1)
    c: InternalAlignment(g19,g0)
    c: Equal(g19,g1)
    c: InternalAlignment(g20,g0)
    c: Equal(g20,g1)
    c: InternalAlignment(g21,g0)
    c: Equal(g21,g1)
    c: InternalAlignment(g22,g0)
    c: Equal(g22,g1)
    c: InternalAlignment(g23,g0)
    c: Equal(g23,g1)
    c: InternalAlignment(g24,g0)
    c: Equal(g24,g1)
    c: InternalAlignment(g25,g0)
    c: Equal(g25,g1)
    c: InternalAlignment(g26,g0)
    c: Equal(g26,g1)
    c: InternalAlignment(g27,g0)
    c: Equal(g27,g1)
    c: InternalAlignment(g28,g0)
    c: Equal(g28,g1)
    c: InternalAlignment(g29,g0)
    c: Equal(g29,g1)
    c: InternalAlignment(g30,g0)
    c: Equal(g30,g1)
    c: InternalAlignment(g31,g0)
    c: Equal(g31,g1)
    c: InternalAlignment(g32,g0)
    c: Equal(g32,g1)
    c: InternalAlignment(g33,g0)
    c: Equal(g33,g1)
    c: InternalAlignment(g34,g0)
    c: Equal(g34,g1)
    c: InternalAlignment(g35,g0)
    c: Equal(g35,g1)
    c: InternalAlignment(g36,g0)
    c: Equal(g36,g1)
    c: InternalAlignment(g37,g0)
    c: Equal(g37,g1)
    c: InternalAlignment(g38,g0)
    c: Equal(g38,g1)
    c: InternalAlignment(g39,g0)
    c: Equal(g39,g1)
    c: InternalAlignment(g40,g0)
    c: Equal(g40,g1)
    c: InternalAlignment(g41,g0)
    c: Equal(g41,g1)
    c: InternalAlignment(g42,g0)
    c: Equal(g42,g1)
    c: InternalAlignment(g43,g0)
    c: Equal(g43,g1)
    c: InternalAlignment(g44,g0)
    c: Equal(g44,g1)
    c: InternalAlignment(g45,g0)
    c: Equal(g45,g1)
    c: InternalAlignment(g46,g0)
    c: Equal(g46,g1)
    c: InternalAlignment(g47,g0)
    c: Equal(g47,g1)
    c: InternalAlignment(g48,g0)
    c: Equal(g48,g1)
    c: InternalAlignment(g49,g0)
    c: Equal(g49,g1)
    c: InternalAlignment(g50,g0)
    c: Equal(g50,g1)
    c: InternalAlignment(g51,g0)
    c: Equal(g51,g1)
    c: InternalAlignment(g52,g0)
    c: Equal(g52,g1)
    c: InternalAlignment(g53,g0)
    c: Equal(g53,g1)
    c: InternalAlignment(g54,g0)
    c: Equal(g54,g1)
    c: InternalAlignment(g55,g0)
    c: Equal(g55,g1)
    c: InternalAlignment(g56,g0)
    c: Equal(g56,g1)
    c: InternalAlignment(g57,g0)
    c: Equal(g57,g1)
    c: InternalAlignment(g58,g0)
    c: Equal(g58,g1)
    c: InternalAlignment(g59,g0)
    c: Equal(g59,g1)
    c: InternalAlignment(g60,g0)
    c: Equal(g60,g1)
    c: InternalAlignment(g61,g0)
    c: Equal(g61,g1)
    c: InternalAlignment(g62-g122 -> g0) x61
FEATURE [PartDesign::AdditiveLoft] AdditiveLoft019
  Closed = false
  Profile = -> Sketch143
  Refine = true
  Ruled = false
  Sections = -> [Sketch142]
  Suppressed = false
FEATURE [PartDesign::Plane] DatumPlane028
  AttachmentOffset = pos=(0,0,0) rot=(0,-1,0;0.785398rad)
  AttachmentSupport = -> [AdditiveLoft019]
  Length = 353.818
  MapMode = 5
  Placement = pos=(0,0,0) rot=(0,-1,0;0.785398rad)
  ResizeMode = 0
  Width = 75.6202
FEATURE [Sketcher::SketchObject] Sketch144
  ArcFitTolerance = 1e-06
  AttachmentSupport = -> [DatumPlane028]
  FullyConstrained = false
  MakeInternals = false
  MapMode = 5
  Placement = pos=(0,0,0) rot=(0,-1,0;0.785398rad)
  sketch-geometry (1):
    g0: Circle CenterX=28.3343 CenterY=4.75298 CenterZ=0 NormalX=0 NormalY=0 NormalZ=1 AngleXU=0 Radius=4.1
  constraints (1):
    c: Diameter(g0) = 8.2
FEATURE [PartDesign::Pocket] Pocket094
  BaseFeature = -> AdditiveLoft019
  Direction = (0.707107,0,-0.707107)
  Length = 1000
  Length2 = 5
  Profile = -> Sketch144
  ReferenceAxis = -> Sketch144 [N_Axis]
  Refine = true
  Suppressed = false
  Type = 0
FEATURE [PartDesign::Plane] DatumPlane029
  AttachmentOffset = pos=(0,0,0) rot=(0,-1,0;0.785398rad)
  AttachmentSupport = -> [Pocket094]
  Length = 353.818
  MapMode = 5
  Placement = pos=(0,0,0) rot=(0,-1,0;0.785398rad)
  ResizeMode = 0
  Width = 75.6202
FEATURE [Sketcher::SketchObject] Sketch145
  ArcFitTolerance = 1e-06
  AttachmentSupport = -> [Pocket094]
  FullyConstrained = false
  MakeInternals = false
  MapMode = 5
  Placement = pos=(0,0,-600) rot=(1,0,0;3.14159rad)
  sketch-geometry (4):
    g0: LineSegment StartX=-85.1873 StartY=206.739 StartZ=0 EndX=-85.1873 EndY=-145.098 EndZ=0
    g1: LineSegment StartX=-85.1873 StartY=-145.098 StartZ=0 EndX=963.672 EndY=-145.098 EndZ=0
    g2: LineSegment StartX=963.672 StartY=-145.098 StartZ=0 EndX=963.672 EndY=206.739 EndZ=0
    g3: LineSegment StartX=963.672 StartY=206.739 StartZ=0 EndX=-85.1873 EndY=206.739 EndZ=0
  constraints (8):
    c: Coincident(g0,g1)
    c: Coincident(g1,g2)
    c: Coincident(g2,g3)
    c: Coincident(g3,g0)
    c: Vertical(g0)
    c: Vertical(g2)
    c: Horizontal(g1)
    c: Horizontal(g3)
FEATURE [Sketcher::SketchObject] Sketch146
  ArcFitTolerance = 1e-06
  AttachmentSupport = -> [DatumPlane029]
  FullyConstrained = false
  MakeInternals = false
  MapMode = 5
  Placement = pos=(0,0,0) rot=(0,-1,0;0.785398rad)
  sketch-geometry (4):
    g0: LineSegment StartX=10 StartY=77.8136 StartZ=0 EndX=10 EndY=-127.239 EndZ=0
    g1: LineSegment StartX=10 StartY=-127.239 StartZ=0 EndX=548.763 EndY=-127.239 EndZ=0
    g2: LineSegment StartX=548.763 StartY=-127.239 StartZ=0 EndX=548.763 EndY=77.8136 EndZ=0
    g3: LineSegment StartX=548.763 StartY=77.8136 StartZ=0 EndX=10 EndY=77.8136 EndZ=0
  constraints (9):
    c: Coincident(g0,g1)
    c: Coincident(g1,g2)
    c: Coincident(g2,g3)
    c: Coincident(g3,g0)
    c: Vertical(g0)
    c: Vertical(g2)
    c: Horizontal(g1)
    c: Horizontal(g3)
    c: Distance(g-1,g0) = 10
FEATURE [PartDesign::Pocket] Pocket095
  BaseFeature = -> Pocket094
  Direction = (0.707107,0,-0.707107)
  Length = 1000
  Length2 = 5
  Profile = -> Sketch146
  ReferenceAxis = -> Sketch146 [N_Axis]
  Refine = true
  Suppressed = false
  Type = 0
FEATURE [Sketcher::SketchObject] Sketch147
  ArcFitTolerance = 1e-06
  AttachmentSupport = -> [Pocket095]
  FullyConstrained = false
  MakeInternals = false
  MapMode = 5
  sketch-geometry (4):
    g0: LineSegment StartX=-129.575 StartY=195.424 StartZ=0 EndX=-129.575 EndY=-278.238 EndZ=0
    g1: LineSegment StartX=-129.575 StartY=-278.238 StartZ=0 EndX=1282.72 EndY=-278.238 EndZ=0
    g2: LineSegment StartX=1282.72 StartY=-278.238 StartZ=0 EndX=1282.72 EndY=195.424 EndZ=0
    g3: LineSegment StartX=1282.72 StartY=195.424 StartZ=0 EndX=-129.575 EndY=195.424 EndZ=0
  constraints (8):
    c: Coincident(g0,g1)
    c: Coincident(g1,g2)
    c: Coincident(g2,g3)
    c: Coincident(g3,g0)
    c: Vertical(g0)
    c: Vertical(g2)
    c: Horizontal(g1)
    c: Horizontal(g3)
FEATURE [PartDesign::Pocket] Pocket096
  BaseFeature = -> Pocket093
  Direction = (0,0,-1)
  Length = 10
  Length2 = 5
  Profile = -> Sketch141
  ReferenceAxis = -> Sketch141 [N_Axis]
  Refine = true
  Suppressed = false
  Type = 0
FEATURE [PartDesign::Pocket] Pocket097
  BaseFeature = -> Pocket096
  Direction = (0,0,1)
  Length = 500
  Length2 = 5
  Profile = -> Sketch139
  ReferenceAxis = -> Sketch139 [N_Axis]
  Refine = true
  Suppressed = false
  Type = 0
FEATURE [PartDesign::Body] Body019
  AllowCompound = false
  Group = -> [Sketch137,Sketch136,AdditiveLoft018,DatumPlane026,Sketch138,Pocket092,Sketch139,DatumPlane027,Sketch140,Pocket093,Sketch141,Pocket096,Pocket097]
  Origin = -> Origin019
  Placement = pos=(0,0,-100) rot=(0,0,1;0rad)
  Tip = -> Pocket097
FEATURE [PartDesign::Pocket] Pocket098
  BaseFeature = -> Pocket095
  Direction = (0,0,-1)
  Length = 110
  Length2 = 5
  Profile = -> Sketch147
  ReferenceAxis = -> Sketch147 [N_Axis]
  Refine = true
  Suppressed = false
  Type = 0
FEATURE [PartDesign::Pocket] Pocket099
  BaseFeature = -> Pocket098
  Direction = (0,0,1)
  Length = 400
  Length2 = 5
  Profile = -> Sketch145
  ReferenceAxis = -> Sketch145 [N_Axis]
  Refine = true
  Suppressed = false
  Type = 0
FEATURE [PartDesign::Body] Body020
  AllowCompound = false
  Group = -> [Sketch143,Sketch142,AdditiveLoft019,DatumPlane028,Sketch144,Pocket094,Sketch145,DatumPlane029,Sketch146,Pocket095,Sketch147,Pocket098,Pocket099]
  Origin = -> Origin020
  Placement = pos=(0,0,-100) rot=(0,0,1;0rad)
  Tip = -> Pocket099
FEATURE [Sketcher::SketchObject] Sketch148
  ArcFitTolerance = 1e-06
  FullyConstrained = false
  MakeInternals = false
  Placement = pos=(600,0,-600) rot=(0,0,1;0rad)
  sketch-geometry (123):
    g0: BSplineCurve PolesCount=61 KnotsCount=61 Degree=3 IsPeriodic=1
    g1-g61: Circle [constr] x61 (B-spline internal-alignment scaffolding for g0; pole/knot coordinates omitted)
    g62-g122: GeomPoint [constr] x61 (B-spline internal-alignment scaffolding for g0; pole/knot coordinates omitted)
  constraints (123):
    c: InternalAlignment(g1,g0)
    c: Weight(g1) = 1
    c: InternalAlignment(g2,g0)
    c: Equal(g2,g1)
    c: InternalAlignment(g3,g0)
    c: Equal(g3,g1)
    c: InternalAlignment(g4,g0)
    c: Equal(g4,g1)
    c: InternalAlignment(g5,g0)
    c: Equal(g5,g1)
    c: InternalAlignment(g6,g0)
    c: Equal(g6,g1)
    c: InternalAlignment(g7,g0)
    c: Equal(g7,g1)
    c: InternalAlignment(g8,g0)
    c: Equal(g8,g1)
    c: InternalAlignment(g9,g0)
    c: Equal(g9,g1)
    c: InternalAlignment(g10,g0)
    c: Equal(g10,g1)
    c: InternalAlignment(g11,g0)
    c: Equal(g11,g1)
    c: InternalAlignment(g12,g0)
    c: Equal(g12,g1)
    c: InternalAlignment(g13,g0)
    c: Equal(g13,g1)
    c: InternalAlignment(g14,g0)
    c: Equal(g14,g1)
    c: InternalAlignment(g15,g0)
    c: Equal(g15,g1)
    c: InternalAlignment(g16,g0)
    c: Equal(g16,g1)
    c: InternalAlignment(g17,g0)
    c: Equal(g17,g1)
    c: InternalAlignment(g18,g0)
    c: Equal(g18,g1)
    c: InternalAlignment(g19,g0)
    c: Equal(g19,g1)
    c: InternalAlignment(g20,g0)
    c: Equal(g20,g1)
    c: InternalAlignment(g21,g0)
    c: Equal(g21,g1)
    c: InternalAlignment(g22,g0)
    c: Equal(g22,g1)
    c: InternalAlignment(g23,g0)
    c: Equal(g23,g1)
    c: InternalAlignment(g24,g0)
    c: Equal(g24,g1)
    c: InternalAlignment(g25,g0)
    c: Equal(g25,g1)
    c: InternalAlignment(g26,g0)
    c: Equal(g26,g1)
    c: InternalAlignment(g27,g0)
    c: Equal(g27,g1)
    c: InternalAlignment(g28,g0)
    c: Equal(g28,g1)
    c: InternalAlignment(g29,g0)
    c: Equal(g29,g1)
    c: InternalAlignment(g30,g0)
    c: Equal(g30,g1)
    c: InternalAlignment(g31,g0)
    c: Equal(g31,g1)
    c: InternalAlignment(g32,g0)
    c: Equal(g32,g1)
    c: InternalAlignment(g33,g0)
    c: Equal(g33,g1)
    c: InternalAlignment(g34,g0)
    c: Equal(g34,g1)
    c: InternalAlignment(g35,g0)
    c: Equal(g35,g1)
    c: InternalAlignment(g36,g0)
    c: Equal(g36,g1)
    c: InternalAlignment(g37,g0)
    c: Equal(g37,g1)
    c: InternalAlignment(g38,g0)
    c: Equal(g38,g1)
    c: InternalAlignment(g39,g0)
    c: Equal(g39,g1)
    c: InternalAlignment(g40,g0)
    c: Equal(g40,g1)
    c: InternalAlignment(g41,g0)
    c: Equal(g41,g1)
    c: InternalAlignment(g42,g0)
    c: Equal(g42,g1)
    c: InternalAlignment(g43,g0)
    c: Equal(g43,g1)
    c: InternalAlignment(g44,g0)
    c: Equal(g44,g1)
    c: InternalAlignment(g45,g0)
    c: Equal(g45,g1)
    c: InternalAlignment(g46,g0)
    c: Equal(g46,g1)
    c: InternalAlignment(g47,g0)
    c: Equal(g47,g1)
    c: InternalAlignment(g48,g0)
    c: Equal(g48,g1)
    c: InternalAlignment(g49,g0)
    c: Equal(g49,g1)
    c: InternalAlignment(g50,g0)
    c: Equal(g50,g1)
    c: InternalAlignment(g51,g0)
    c: Equal(g51,g1)
    c: InternalAlignment(g52,g0)
    c: Equal(g52,g1)
    c: InternalAlignment(g53,g0)
    c: Equal(g53,g1)
    c: InternalAlignment(g54,g0)
    c: Equal(g54,g1)
    c: InternalAlignment(g55,g0)
    c: Equal(g55,g1)
    c: InternalAlignment(g56,g0)
    c: Equal(g56,g1)
    c: InternalAlignment(g57,g0)
    c: Equal(g57,g1)
    c: InternalAlignment(g58,g0)
    c: Equal(g58,g1)
    c: InternalAlignment(g59,g0)
    c: Equal(g59,g1)
    c: InternalAlignment(g60,g0)
    c: Equal(g60,g1)
    c: InternalAlignment(g61,g0)
    c: Equal(g61,g1)
    c: InternalAlignment(g62-g122 -> g0) x61
FEATURE [Sketcher::SketchObject] Sketch149
  ArcFitTolerance = 1e-06
  FullyConstrained = false
  MakeInternals = false
  sketch-geometry (123):
    g0: BSplineCurve PolesCount=61 KnotsCount=61 Degree=3 IsPeriodic=1
    g1-g61: Circle [constr] x61 (B-spline internal-alignment scaffolding for g0; pole/knot coordinates omitted)
    g62-g122: GeomPoint [constr] x61 (B-spline internal-alignment scaffolding for g0; pole/knot coordinates omitted)
  constraints (123):
    c: InternalAlignment(g1,g0)
    c: Weight(g1) = 1
    c: InternalAlignment(g2,g0)
    c: Equal(g2,g1)
    c: InternalAlignment(g3,g0)
    c: Equal(g3,g1)
    c: InternalAlignment(g4,g0)
    c: Equal(g4,g1)
    c: InternalAlignment(g5,g0)
    c: Equal(g5,g1)
    c: InternalAlignment(g6,g0)
    c: Equal(g6,g1)
    c: InternalAlignment(g7,g0)
    c: Equal(g7,g1)
    c: InternalAlignment(g8,g0)
    c: Equal(g8,g1)
    c: InternalAlignment(g9,g0)
    c: Equal(g9,g1)
    c: InternalAlignment(g10,g0)
    c: Equal(g10,g1)
    c: InternalAlignment(g11,g0)
    c: Equal(g11,g1)
    c: InternalAlignment(g12,g0)
    c: Equal(g12,g1)
    c: InternalAlignment(g13,g0)
    c: Equal(g13,g1)
    c: InternalAlignment(g14,g0)
    c: Equal(g14,g1)
    c: InternalAlignment(g15,g0)
    c: Equal(g15,g1)
    c: InternalAlignment(g16,g0)
    c: Equal(g16,g1)
    c: InternalAlignment(g17,g0)
    c: Equal(g17,g1)
    c: InternalAlignment(g18,g0)
    c: Equal(g18,g1)
    c: InternalAlignment(g19,g0)
    c: Equal(g19,g1)
    c: InternalAlignment(g20,g0)
    c: Equal(g20,g1)
    c: InternalAlignment(g21,g0)
    c: Equal(g21,g1)
    c: InternalAlignment(g22,g0)
    c: Equal(g22,g1)
    c: InternalAlignment(g23,g0)
    c: Equal(g23,g1)
    c: InternalAlignment(g24,g0)
    c: Equal(g24,g1)
    c: InternalAlignment(g25,g0)
    c: Equal(g25,g1)
    c: InternalAlignment(g26,g0)
    c: Equal(g26,g1)
    c: InternalAlignment(g27,g0)
    c: Equal(g27,g1)
    c: InternalAlignment(g28,g0)
    c: Equal(g28,g1)
    c: InternalAlignment(g29,g0)
    c: Equal(g29,g1)
    c: InternalAlignment(g30,g0)
    c: Equal(g30,g1)
    c: InternalAlignment(g31,g0)
    c: Equal(g31,g1)
    c: InternalAlignment(g32,g0)
    c: Equal(g32,g1)
    c: InternalAlignment(g33,g0)
    c: Equal(g33,g1)
    c: InternalAlignment(g34,g0)
    c: Equal(g34,g1)
    c: InternalAlignment(g35,g0)
    c: Equal(g35,g1)
    c: InternalAlignment(g36,g0)
    c: Equal(g36,g1)
    c: InternalAlignment(g37,g0)
    c: Equal(g37,g1)
    c: InternalAlignment(g38,g0)
    c: Equal(g38,g1)
    c: InternalAlignment(g39,g0)
    c: Equal(g39,g1)
    c: InternalAlignment(g40,g0)
    c: Equal(g40,g1)
    c: InternalAlignment(g41,g0)
    c: Equal(g41,g1)
    c: InternalAlignment(g42,g0)
    c: Equal(g42,g1)
    c: InternalAlignment(g43,g0)
    c: Equal(g43,g1)
    c: InternalAlignment(g44,g0)
    c: Equal(g44,g1)
    c: InternalAlignment(g45,g0)
    c: Equal(g45,g1)
    c: InternalAlignment(g46,g0)
    c: Equal(g46,g1)
    c: InternalAlignment(g47,g0)
    c: Equal(g47,g1)
    c: InternalAlignment(g48,g0)
    c: Equal(g48,g1)
    c: InternalAlignment(g49,g0)
    c: Equal(g49,g1)
    c: InternalAlignment(g50,g0)
    c: Equal(g50,g1)
    c: InternalAlignment(g51,g0)
    c: Equal(g51,g1)
    c: InternalAlignment(g52,g0)
    c: Equal(g52,g1)
    c: InternalAlignment(g53,g0)
    c: Equal(g53,g1)
    c: InternalAlignment(g54,g0)
    c: Equal(g54,g1)
    c: InternalAlignment(g55,g0)
    c: Equal(g55,g1)
    c: InternalAlignment(g56,g0)
    c: Equal(g56,g1)
    c: InternalAlignment(g57,g0)
    c: Equal(g57,g1)
    c: InternalAlignment(g58,g0)
    c: Equal(g58,g1)
    c: InternalAlignment(g59,g0)
    c: Equal(g59,g1)
    c: InternalAlignment(g60,g0)
    c: Equal(g60,g1)
    c: InternalAlignment(g61,g0)
    c: Equal(g61,g1)
    c: InternalAlignment(g62-g122 -> g0) x61
FEATURE [PartDesign::AdditiveLoft] AdditiveLoft020
  Closed = false
  Profile = -> Sketch149
  Refine = true
  Ruled = false
  Sections = -> [Sketch148]
  Suppressed = false
FEATURE [PartDesign::Plane] DatumPlane030
  AttachmentOffset = pos=(0,0,0) rot=(0,-1,0;0.785398rad)
  AttachmentSupport = -> [AdditiveLoft020]
  Length = 500.266
  MapMode = 5
  Placement = pos=(0,0,0) rot=(0,-1,0;0.785398rad)
  ResizeMode = 0
  Width = 80.647
FEATURE [Sketcher::SketchObject] Sketch150
  ArcFitTolerance = 1e-06
  AttachmentSupport = -> [DatumPlane030]
  FullyConstrained = false
  MakeInternals = false
  MapMode = 5
  Placement = pos=(0,0,0) rot=(0,-1,0;0.785398rad)
  sketch-geometry (1):
    g0: Circle CenterX=28.3343 CenterY=4.75298 CenterZ=0 NormalX=0 NormalY=0 NormalZ=1 AngleXU=0 Radius=4.1
  constraints (1):
    c: Diameter(g0) = 8.2
FEATURE [PartDesign::Pocket] Pocket100
  BaseFeature = -> AdditiveLoft020
  Direction = (0.707107,0,-0.707107)
  Length = 1000
  Length2 = 5
  Profile = -> Sketch150
  ReferenceAxis = -> Sketch150 [N_Axis]
  Refine = true
  Suppressed = false
  Type = 0
FEATURE [PartDesign::Plane] DatumPlane031
  AttachmentOffset = pos=(0,0,0) rot=(0,-1,0;0.785398rad)
  AttachmentSupport = -> [Pocket100]
  Length = 500.266
  MapMode = 5
  Placement = pos=(0,0,0) rot=(0,-1,0;0.785398rad)
  ResizeMode = 0
  Width = 80.647
FEATURE [Sketcher::SketchObject] Sketch151
  ArcFitTolerance = 1e-06
  AttachmentSupport = -> [Pocket100]
  FullyConstrained = false
  MakeInternals = false
  MapMode = 5
  Placement = pos=(0,0,-600) rot=(1,0,0;3.14159rad)
  sketch-geometry (4):
    g0: LineSegment StartX=-85.1873 StartY=206.739 StartZ=0 EndX=-85.1873 EndY=-145.098 EndZ=0
    g1: LineSegment StartX=-85.1873 StartY=-145.098 StartZ=0 EndX=963.672 EndY=-145.098 EndZ=0
    g2: LineSegment StartX=963.672 StartY=-145.098 StartZ=0 EndX=963.672 EndY=206.739 EndZ=0
    g3: LineSegment StartX=963.672 StartY=206.739 StartZ=0 EndX=-85.1873 EndY=206.739 EndZ=0
  constraints (8):
    c: Coincident(g0,g1)
    c: Coincident(g1,g2)
    c: Coincident(g2,g3)
    c: Coincident(g3,g0)
    c: Vertical(g0)
    c: Vertical(g2)
    c: Horizontal(g1)
    c: Horizontal(g3)
FEATURE [Sketcher::SketchObject] Sketch152
  ArcFitTolerance = 1e-06
  AttachmentSupport = -> [DatumPlane031]
  FullyConstrained = false
  MakeInternals = false
  MapMode = 5
  Placement = pos=(0,0,0) rot=(0,-1,0;0.785398rad)
  sketch-geometry (4):
    g0: LineSegment StartX=10 StartY=77.8136 StartZ=0 EndX=10 EndY=-127.239 EndZ=0
    g1: LineSegment StartX=10 StartY=-127.239 StartZ=0 EndX=548.763 EndY=-127.239 EndZ=0
    g2: LineSegment StartX=548.763 StartY=-127.239 StartZ=0 EndX=548.763 EndY=77.8136 EndZ=0
    g3: LineSegment StartX=548.763 StartY=77.8136 StartZ=0 EndX=10 EndY=77.8136 EndZ=0
  constraints (9):
    c: Coincident(g0,g1)
    c: Coincident(g1,g2)
    c: Coincident(g2,g3)
    c: Coincident(g3,g0)
    c: Vertical(g0)
    c: Vertical(g2)
    c: Horizontal(g1)
    c: Horizontal(g3)
    c: Distance(g-1,g0) = 10
FEATURE [PartDesign::Pocket] Pocket101
  BaseFeature = -> Pocket100
  Direction = (0.707107,0,-0.707107)
  Length = 1000
  Length2 = 5
  Profile = -> Sketch152
  ReferenceAxis = -> Sketch152 [N_Axis]
  Refine = true
  Suppressed = false
  Type = 0
FEATURE [Sketcher::SketchObject] Sketch153
  ArcFitTolerance = 1e-06
  AttachmentSupport = -> [Pocket101]
  FullyConstrained = false
  MakeInternals = false
  MapMode = 5
  sketch-geometry (4):
    g0: LineSegment StartX=-129.575 StartY=195.424 StartZ=0 EndX=-129.575 EndY=-278.238 EndZ=0
    g1: LineSegment StartX=-129.575 StartY=-278.238 StartZ=0 EndX=1282.72 EndY=-278.238 EndZ=0
    g2: LineSegment StartX=1282.72 StartY=-278.238 StartZ=0 EndX=1282.72 EndY=195.424 EndZ=0
    g3: LineSegment StartX=1282.72 StartY=195.424 StartZ=0 EndX=-129.575 EndY=195.424 EndZ=0
  constraints (8):
    c: Coincident(g0,g1)
    c: Coincident(g1,g2)
    c: Coincident(g2,g3)
    c: Coincident(g3,g0)
    c: Vertical(g0)
    c: Vertical(g2)
    c: Horizontal(g1)
    c: Horizontal(g3)
FEATURE [PartDesign::Pocket] Pocket102
  BaseFeature = -> Pocket101
  Direction = (0,0,-1)
  Length = 210
  Length2 = 5
  Profile = -> Sketch153
  ReferenceAxis = -> Sketch153 [N_Axis]
  Refine = true
  Suppressed = false
  Type = 0
FEATURE [PartDesign::Pocket] Pocket103
  BaseFeature = -> Pocket102
  Direction = (0,0,1)
  Length = 300
  Length2 = 5
  Profile = -> Sketch151
  ReferenceAxis = -> Sketch151 [N_Axis]
  Refine = true
  Suppressed = false
  Type = 0
FEATURE [PartDesign::Body] Body021
  AllowCompound = false
  Group = -> [Sketch149,Sketch148,AdditiveLoft020,DatumPlane030,Sketch150,Pocket100,Sketch151,DatumPlane031,Sketch152,Pocket101,Sketch153,Pocket102,Pocket103]
  Origin = -> Origin021
  Placement = pos=(0,0,-100) rot=(0,0,1;0rad)
  Tip = -> Pocket103
FEATURE [Sketcher::SketchObject] Sketch154
  ArcFitTolerance = 1e-06
  FullyConstrained = false
  MakeInternals = false
  Placement = pos=(600,0,-600) rot=(0,0,1;0rad)
  sketch-geometry (123):
    g0: BSplineCurve PolesCount=61 KnotsCount=61 Degree=3 IsPeriodic=1
    g1-g61: Circle [constr] x61 (B-spline internal-alignment scaffolding for g0; pole/knot coordinates omitted)
    g62-g122: GeomPoint [constr] x61 (B-spline internal-alignment scaffolding for g0; pole/knot coordinates omitted)
  constraints (123):
    c: InternalAlignment(g1,g0)
    c: Weight(g1) = 1
    c: InternalAlignment(g2,g0)
    c: Equal(g2,g1)
    c: InternalAlignment(g3,g0)
    c: Equal(g3,g1)
    c: InternalAlignment(g4,g0)
    c: Equal(g4,g1)
    c: InternalAlignment(g5,g0)
    c: Equal(g5,g1)
    c: InternalAlignment(g6,g0)
    c: Equal(g6,g1)
    c: InternalAlignment(g7,g0)
    c: Equal(g7,g1)
    c: InternalAlignment(g8,g0)
    c: Equal(g8,g1)
    c: InternalAlignment(g9,g0)
    c: Equal(g9,g1)
    c: InternalAlignment(g10,g0)
    c: Equal(g10,g1)
    c: InternalAlignment(g11,g0)
    c: Equal(g11,g1)
    c: InternalAlignment(g12,g0)
    c: Equal(g12,g1)
    c: InternalAlignment(g13,g0)
    c: Equal(g13,g1)
    c: InternalAlignment(g14,g0)
    c: Equal(g14,g1)
    c: InternalAlignment(g15,g0)
    c: Equal(g15,g1)
    c: InternalAlignment(g16,g0)
    c: Equal(g16,g1)
    c: InternalAlignment(g17,g0)
    c: Equal(g17,g1)
    c: InternalAlignment(g18,g0)
    c: Equal(g18,g1)
    c: InternalAlignment(g19,g0)
    c: Equal(g19,g1)
    c: InternalAlignment(g20,g0)
    c: Equal(g20,g1)
    c: InternalAlignment(g21,g0)
    c: Equal(g21,g1)
    c: InternalAlignment(g22,g0)
    c: Equal(g22,g1)
    c: InternalAlignment(g23,g0)
    c: Equal(g23,g1)
    c: InternalAlignment(g24,g0)
    c: Equal(g24,g1)
    c: InternalAlignment(g25,g0)
    c: Equal(g25,g1)
    c: InternalAlignment(g26,g0)
    c: Equal(g26,g1)
    c: InternalAlignment(g27,g0)
    c: Equal(g27,g1)
    c: InternalAlignment(g28,g0)
    c: Equal(g28,g1)
    c: InternalAlignment(g29,g0)
    c: Equal(g29,g1)
    c: InternalAlignment(g30,g0)
    c: Equal(g30,g1)
    c: InternalAlignment(g31,g0)
    c: Equal(g31,g1)
    c: InternalAlignment(g32,g0)
    c: Equal(g32,g1)
    c: InternalAlignment(g33,g0)
    c: Equal(g33,g1)
    c: InternalAlignment(g34,g0)
    c: Equal(g34,g1)
    c: InternalAlignment(g35,g0)
    c: Equal(g35,g1)
    c: InternalAlignment(g36,g0)
    c: Equal(g36,g1)
    c: InternalAlignment(g37,g0)
    c: Equal(g37,g1)
    c: InternalAlignment(g38,g0)
    c: Equal(g38,g1)
    c: InternalAlignment(g39,g0)
    c: Equal(g39,g1)
    c: InternalAlignment(g40,g0)
    c: Equal(g40,g1)
    c: InternalAlignment(g41,g0)
    c: Equal(g41,g1)
    c: InternalAlignment(g42,g0)
    c: Equal(g42,g1)
    c: InternalAlignment(g43,g0)
    c: Equal(g43,g1)
    c: InternalAlignment(g44,g0)
    c: Equal(g44,g1)
    c: InternalAlignment(g45,g0)
    c: Equal(g45,g1)
    c: InternalAlignment(g46,g0)
    c: Equal(g46,g1)
    c: InternalAlignment(g47,g0)
    c: Equal(g47,g1)
    c: InternalAlignment(g48,g0)
    c: Equal(g48,g1)
    c: InternalAlignment(g49,g0)
    c: Equal(g49,g1)
    c: InternalAlignment(g50,g0)
    c: Equal(g50,g1)
    c: InternalAlignment(g51,g0)
    c: Equal(g51,g1)
    c: InternalAlignment(g52,g0)
    c: Equal(g52,g1)
    c: InternalAlignment(g53,g0)
    c: Equal(g53,g1)
    c: InternalAlignment(g54,g0)
    c: Equal(g54,g1)
    c: InternalAlignment(g55,g0)
    c: Equal(g55,g1)
    c: InternalAlignment(g56,g0)
    c: Equal(g56,g1)
    c: InternalAlignment(g57,g0)
    c: Equal(g57,g1)
    c: InternalAlignment(g58,g0)
    c: Equal(g58,g1)
    c: InternalAlignment(g59,g0)
    c: Equal(g59,g1)
    c: InternalAlignment(g60,g0)
    c: Equal(g60,g1)
    c: InternalAlignment(g61,g0)
    c: Equal(g61,g1)
    c: InternalAlignment(g62-g122 -> g0) x61
FEATURE [Sketcher::SketchObject] Sketch155
  ArcFitTolerance = 1e-06
  FullyConstrained = false
  MakeInternals = false
  sketch-geometry (123):
    g0: BSplineCurve PolesCount=61 KnotsCount=61 Degree=3 IsPeriodic=1
    g1-g61: Circle [constr] x61 (B-spline internal-alignment scaffolding for g0; pole/knot coordinates omitted)
    g62-g122: GeomPoint [constr] x61 (B-spline internal-alignment scaffolding for g0; pole/knot coordinates omitted)
  constraints (123):
    c: InternalAlignment(g1,g0)
    c: Weight(g1) = 1
    c: InternalAlignment(g2,g0)
    c: Equal(g2,g1)
    c: InternalAlignment(g3,g0)
    c: Equal(g3,g1)
    c: InternalAlignment(g4,g0)
    c: Equal(g4,g1)
    c: InternalAlignment(g5,g0)
    c: Equal(g5,g1)
    c: InternalAlignment(g6,g0)
    c: Equal(g6,g1)
    c: InternalAlignment(g7,g0)
    c: Equal(g7,g1)
    c: InternalAlignment(g8,g0)
    c: Equal(g8,g1)
    c: InternalAlignment(g9,g0)
    c: Equal(g9,g1)
    c: InternalAlignment(g10,g0)
    c: Equal(g10,g1)
    c: InternalAlignment(g11,g0)
    c: Equal(g11,g1)
    c: InternalAlignment(g12,g0)
    c: Equal(g12,g1)
    c: InternalAlignment(g13,g0)
    c: Equal(g13,g1)
    c: InternalAlignment(g14,g0)
    c: Equal(g14,g1)
    c: InternalAlignment(g15,g0)
    c: Equal(g15,g1)
    c: InternalAlignment(g16,g0)
    c: Equal(g16,g1)
    c: InternalAlignment(g17,g0)
    c: Equal(g17,g1)
    c: InternalAlignment(g18,g0)
    c: Equal(g18,g1)
    c: InternalAlignment(g19,g0)
    c: Equal(g19,g1)
    c: InternalAlignment(g20,g0)
    c: Equal(g20,g1)
    c: InternalAlignment(g21,g0)
    c: Equal(g21,g1)
    c: InternalAlignment(g22,g0)
    c: Equal(g22,g1)
    c: InternalAlignment(g23,g0)
    c: Equal(g23,g1)
    c: InternalAlignment(g24,g0)
    c: Equal(g24,g1)
    c: InternalAlignment(g25,g0)
    c: Equal(g25,g1)
    c: InternalAlignment(g26,g0)
    c: Equal(g26,g1)
    c: InternalAlignment(g27,g0)
    c: Equal(g27,g1)
    c: InternalAlignment(g28,g0)
    c: Equal(g28,g1)
    c: InternalAlignment(g29,g0)
    c: Equal(g29,g1)
    c: InternalAlignment(g30,g0)
    c: Equal(g30,g1)
    c: InternalAlignment(g31,g0)
    c: Equal(g31,g1)
    c: InternalAlignment(g32,g0)
    c: Equal(g32,g1)
    c: InternalAlignment(g33,g0)
    c: Equal(g33,g1)
    c: InternalAlignment(g34,g0)
    c: Equal(g34,g1)
    c: InternalAlignment(g35,g0)
    c: Equal(g35,g1)
    c: InternalAlignment(g36,g0)
    c: Equal(g36,g1)
    c: InternalAlignment(g37,g0)
    c: Equal(g37,g1)
    c: InternalAlignment(g38,g0)
    c: Equal(g38,g1)
    c: InternalAlignment(g39,g0)
    c: Equal(g39,g1)
    c: InternalAlignment(g40,g0)
    c: Equal(g40,g1)
    c: InternalAlignment(g41,g0)
    c: Equal(g41,g1)
    c: InternalAlignment(g42,g0)
    c: Equal(g42,g1)
    c: InternalAlignment(g43,g0)
    c: Equal(g43,g1)
    c: InternalAlignment(g44,g0)
    c: Equal(g44,g1)
    c: InternalAlignment(g45,g0)
    c: Equal(g45,g1)
    c: InternalAlignment(g46,g0)
    c: Equal(g46,g1)
    c: InternalAlignment(g47,g0)
    c: Equal(g47,g1)
    c: InternalAlignment(g48,g0)
    c: Equal(g48,g1)
    c: InternalAlignment(g49,g0)
    c: Equal(g49,g1)
    c: InternalAlignment(g50,g0)
    c: Equal(g50,g1)
    c: InternalAlignment(g51,g0)
    c: Equal(g51,g1)
    c: InternalAlignment(g52,g0)
    c: Equal(g52,g1)
    c: InternalAlignment(g53,g0)
    c: Equal(g53,g1)
    c: InternalAlignment(g54,g0)
    c: Equal(g54,g1)
    c: InternalAlignment(g55,g0)
    c: Equal(g55,g1)
    c: InternalAlignment(g56,g0)
    c: Equal(g56,g1)
    c: InternalAlignment(g57,g0)
    c: Equal(g57,g1)
    c: InternalAlignment(g58,g0)
    c: Equal(g58,g1)
    c: InternalAlignment(g59,g0)
    c: Equal(g59,g1)
    c: InternalAlignment(g60,g0)
    c: Equal(g60,g1)
    c: InternalAlignment(g61,g0)
    c: Equal(g61,g1)
    c: InternalAlignment(g62-g122 -> g0) x61
FEATURE [PartDesign::AdditiveLoft] AdditiveLoft021
  Closed = false
  Profile = -> Sketch155
  Refine = true
  Ruled = false
  Sections = -> [Sketch154]
  Suppressed = false
FEATURE [PartDesign::Plane] DatumPlane032
  AttachmentOffset = pos=(0,0,0) rot=(0,-1,0;0.785398rad)
  AttachmentSupport = -> [AdditiveLoft021]
  Length = 645.999
  MapMode = 5
  Placement = pos=(0,0,0) rot=(0,-1,0;0.785398rad)
  ResizeMode = 0
  Width = 84.9583
FEATURE [Sketcher::SketchObject] Sketch156
  ArcFitTolerance = 1e-06
  AttachmentSupport = -> [DatumPlane032]
  FullyConstrained = false
  MakeInternals = false
  MapMode = 5
  Placement = pos=(0,0,0) rot=(0,-1,0;0.785398rad)
  sketch-geometry (1):
    g0: Circle CenterX=28.3343 CenterY=4.75298 CenterZ=0 NormalX=0 NormalY=0 NormalZ=1 AngleXU=0 Radius=4.1
  constraints (1):
    c: Diameter(g0) = 8.2
FEATURE [PartDesign::Pocket] Pocket104
  BaseFeature = -> AdditiveLoft021
  Direction = (0.707107,0,-0.707107)
  Length = 1000
  Length2 = 5
  Profile = -> Sketch156
  ReferenceAxis = -> Sketch156 [N_Axis]
  Refine = true
  Suppressed = false
  Type = 0
FEATURE [PartDesign::Plane] DatumPlane033
  AttachmentOffset = pos=(0,0,0) rot=(0,-1,0;0.785398rad)
  AttachmentSupport = -> [Pocket104]
  Length = 645.999
  MapMode = 5
  Placement = pos=(0,0,0) rot=(0,-1,0;0.785398rad)
  ResizeMode = 0
  Width = 84.9583
FEATURE [Sketcher::SketchObject] Sketch157
  ArcFitTolerance = 1e-06
  AttachmentSupport = -> [Pocket104]
  FullyConstrained = false
  MakeInternals = false
  MapMode = 5
  Placement = pos=(0,0,-600) rot=(1,0,0;3.14159rad)
  sketch-geometry (4):
    g0: LineSegment StartX=-85.1873 StartY=206.739 StartZ=0 EndX=-85.1873 EndY=-145.098 EndZ=0
    g1: LineSegment StartX=-85.1873 StartY=-145.098 StartZ=0 EndX=963.672 EndY=-145.098 EndZ=0
    g2: LineSegment StartX=963.672 StartY=-145.098 StartZ=0 EndX=963.672 EndY=206.739 EndZ=0
    g3: LineSegment StartX=963.672 StartY=206.739 StartZ=0 EndX=-85.1873 EndY=206.739 EndZ=0
  constraints (8):
    c: Coincident(g0,g1)
    c: Coincident(g1,g2)
    c: Coincident(g2,g3)
    c: Coincident(g3,g0)
    c: Vertical(g0)
    c: Vertical(g2)
    c: Horizontal(g1)
    c: Horizontal(g3)
FEATURE [Sketcher::SketchObject] Sketch158
  ArcFitTolerance = 1e-06
  AttachmentSupport = -> [DatumPlane033]
  FullyConstrained = false
  MakeInternals = false
  MapMode = 5
  Placement = pos=(0,0,0) rot=(0,-1,0;0.785398rad)
  sketch-geometry (4):
    g0: LineSegment StartX=10 StartY=77.8136 StartZ=0 EndX=10 EndY=-127.239 EndZ=0
    g1: LineSegment StartX=10 StartY=-127.239 StartZ=0 EndX=548.763 EndY=-127.239 EndZ=0
    g2: LineSegment StartX=548.763 StartY=-127.239 StartZ=0 EndX=548.763 EndY=77.8136 EndZ=0
    g3: LineSegment StartX=548.763 StartY=77.8136 StartZ=0 EndX=10 EndY=77.8136 EndZ=0
  constraints (9):
    c: Coincident(g0,g1)
    c: Coincident(g1,g2)
    c: Coincident(g2,g3)
    c: Coincident(g3,g0)
    c: Vertical(g0)
    c: Vertical(g2)
    c: Horizontal(g1)
    c: Horizontal(g3)
    c: Distance(g-1,g0) = 10
FEATURE [PartDesign::Pocket] Pocket105
  BaseFeature = -> Pocket104
  Direction = (0.707107,0,-0.707107)
  Length = 1000
  Length2 = 5
  Profile = -> Sketch158
  ReferenceAxis = -> Sketch158 [N_Axis]
  Refine = true
  Suppressed = false
  Type = 0
FEATURE [Sketcher::SketchObject] Sketch159
  ArcFitTolerance = 1e-06
  AttachmentSupport = -> [Pocket105]
  FullyConstrained = false
  MakeInternals = false
  MapMode = 5
  sketch-geometry (4):
    g0: LineSegment StartX=-129.575 StartY=195.424 StartZ=0 EndX=-129.575 EndY=-278.238 EndZ=0
    g1: LineSegment StartX=-129.575 StartY=-278.238 StartZ=0 EndX=1282.72 EndY=-278.238 EndZ=0
    g2: LineSegment StartX=1282.72 StartY=-278.238 StartZ=0 EndX=1282.72 EndY=195.424 EndZ=0
    g3: LineSegment StartX=1282.72 StartY=195.424 StartZ=0 EndX=-129.575 EndY=195.424 EndZ=0
  constraints (8):
    c: Coincident(g0,g1)
    c: Coincident(g1,g2)
    c: Coincident(g2,g3)
    c: Coincident(g3,g0)
    c: Vertical(g0)
    c: Vertical(g2)
    c: Horizontal(g1)
    c: Horizontal(g3)
FEATURE [PartDesign::Pocket] Pocket106
  BaseFeature = -> Pocket105
  Direction = (0,0,-1)
  Length = 310
  Length2 = 5
  Profile = -> Sketch159
  ReferenceAxis = -> Sketch159 [N_Axis]
  Refine = true
  Suppressed = false
  Type = 0
FEATURE [PartDesign::Pocket] Pocket107
  BaseFeature = -> Pocket106
  Direction = (0,0,1)
  Length = 200
  Length2 = 5
  Profile = -> Sketch157
  ReferenceAxis = -> Sketch157 [N_Axis]
  Refine = true
  Suppressed = false
  Type = 0
FEATURE [PartDesign::Body] Body022
  AllowCompound = false
  Group = -> [Sketch155,Sketch154,AdditiveLoft021,DatumPlane032,Sketch156,Pocket104,Sketch157,DatumPlane033,Sketch158,Pocket105,Sketch159,Pocket106,Pocket107]
  Origin = -> Origin022
  Placement = pos=(0,0,-100) rot=(0,0,1;0rad)
  Tip = -> Pocket107
FEATURE [Sketcher::SketchObject] Sketch160
  ArcFitTolerance = 1e-06
  FullyConstrained = false
  MakeInternals = false
  Placement = pos=(600,0,-600) rot=(0,0,1;0rad)
  sketch-geometry (123):
    g0: BSplineCurve PolesCount=61 KnotsCount=61 Degree=3 IsPeriodic=1
    g1-g61: Circle [constr] x61 (B-spline internal-alignment scaffolding for g0; pole/knot coordinates omitted)
    g62-g122: GeomPoint [constr] x61 (B-spline internal-alignment scaffolding for g0; pole/knot coordinates omitted)
  constraints (123):
    c: InternalAlignment(g1,g0)
    c: Weight(g1) = 1
    c: InternalAlignment(g2,g0)
    c: Equal(g2,g1)
    c: InternalAlignment(g3,g0)
    c: Equal(g3,g1)
    c: InternalAlignment(g4,g0)
    c: Equal(g4,g1)
    c: InternalAlignment(g5,g0)
    c: Equal(g5,g1)
    c: InternalAlignment(g6,g0)
    c: Equal(g6,g1)
    c: InternalAlignment(g7,g0)
    c: Equal(g7,g1)
    c: InternalAlignment(g8,g0)
    c: Equal(g8,g1)
    c: InternalAlignment(g9,g0)
    c: Equal(g9,g1)
    c: InternalAlignment(g10,g0)
    c: Equal(g10,g1)
    c: InternalAlignment(g11,g0)
    c: Equal(g11,g1)
    c: InternalAlignment(g12,g0)
    c: Equal(g12,g1)
    c: InternalAlignment(g13,g0)
    c: Equal(g13,g1)
    c: InternalAlignment(g14,g0)
    c: Equal(g14,g1)
    c: InternalAlignment(g15,g0)
    c: Equal(g15,g1)
    c: InternalAlignment(g16,g0)
    c: Equal(g16,g1)
    c: InternalAlignment(g17,g0)
    c: Equal(g17,g1)
    c: InternalAlignment(g18,g0)
    c: Equal(g18,g1)
    c: InternalAlignment(g19,g0)
    c: Equal(g19,g1)
    c: InternalAlignment(g20,g0)
    c: Equal(g20,g1)
    c: InternalAlignment(g21,g0)
    c: Equal(g21,g1)
    c: InternalAlignment(g22,g0)
    c: Equal(g22,g1)
    c: InternalAlignment(g23,g0)
    c: Equal(g23,g1)
    c: InternalAlignment(g24,g0)
    c: Equal(g24,g1)
    c: InternalAlignment(g25,g0)
    c: Equal(g25,g1)
    c: InternalAlignment(g26,g0)
    c: Equal(g26,g1)
    c: InternalAlignment(g27,g0)
    c: Equal(g27,g1)
    c: InternalAlignment(g28,g0)
    c: Equal(g28,g1)
    c: InternalAlignment(g29,g0)
    c: Equal(g29,g1)
    c: InternalAlignment(g30,g0)
    c: Equal(g30,g1)
    c: InternalAlignment(g31,g0)
    c: Equal(g31,g1)
    c: InternalAlignment(g32,g0)
    c: Equal(g32,g1)
    c: InternalAlignment(g33,g0)
    c: Equal(g33,g1)
    c: InternalAlignment(g34,g0)
    c: Equal(g34,g1)
    c: InternalAlignment(g35,g0)
    c: Equal(g35,g1)
    c: InternalAlignment(g36,g0)
    c: Equal(g36,g1)
    c: InternalAlignment(g37,g0)
    c: Equal(g37,g1)
    c: InternalAlignment(g38,g0)
    c: Equal(g38,g1)
    c: InternalAlignment(g39,g0)
    c: Equal(g39,g1)
    c: InternalAlignment(g40,g0)
    c: Equal(g40,g1)
    c: InternalAlignment(g41,g0)
    c: Equal(g41,g1)
    c: InternalAlignment(g42,g0)
    c: Equal(g42,g1)
    c: InternalAlignment(g43,g0)
    c: Equal(g43,g1)
    c: InternalAlignment(g44,g0)
    c: Equal(g44,g1)
    c: InternalAlignment(g45,g0)
    c: Equal(g45,g1)
    c: InternalAlignment(g46,g0)
    c: Equal(g46,g1)
    c: InternalAlignment(g47,g0)
    c: Equal(g47,g1)
    c: InternalAlignment(g48,g0)
    c: Equal(g48,g1)
    c: InternalAlignment(g49,g0)
    c: Equal(g49,g1)
    c: InternalAlignment(g50,g0)
    c: Equal(g50,g1)
    c: InternalAlignment(g51,g0)
    c: Equal(g51,g1)
    c: InternalAlignment(g52,g0)
    c: Equal(g52,g1)
    c: InternalAlignment(g53,g0)
    c: Equal(g53,g1)
    c: InternalAlignment(g54,g0)
    c: Equal(g54,g1)
    c: InternalAlignment(g55,g0)
    c: Equal(g55,g1)
    c: InternalAlignment(g56,g0)
    c: Equal(g56,g1)
    c: InternalAlignment(g57,g0)
    c: Equal(g57,g1)
    c: InternalAlignment(g58,g0)
    c: Equal(g58,g1)
    c: InternalAlignment(g59,g0)
    c: Equal(g59,g1)
    c: InternalAlignment(g60,g0)
    c: Equal(g60,g1)
    c: InternalAlignment(g61,g0)
    c: Equal(g61,g1)
    c: InternalAlignment(g62-g122 -> g0) x61
FEATURE [Sketcher::SketchObject] Sketch161
  ArcFitTolerance = 1e-06
  FullyConstrained = false
  MakeInternals = false
  sketch-geometry (123):
    g0: BSplineCurve PolesCount=61 KnotsCount=61 Degree=3 IsPeriodic=1
    g1-g61: Circle [constr] x61 (B-spline internal-alignment scaffolding for g0; pole/knot coordinates omitted)
    g62-g122: GeomPoint [constr] x61 (B-spline internal-alignment scaffolding for g0; pole/knot coordinates omitted)
  constraints (123):
    c: InternalAlignment(g1,g0)
    c: Weight(g1) = 1
    c: InternalAlignment(g2,g0)
    c: Equal(g2,g1)
    c: InternalAlignment(g3,g0)
    c: Equal(g3,g1)
    c: InternalAlignment(g4,g0)
    c: Equal(g4,g1)
    c: InternalAlignment(g5,g0)
    c: Equal(g5,g1)
    c: InternalAlignment(g6,g0)
    c: Equal(g6,g1)
    c: InternalAlignment(g7,g0)
    c: Equal(g7,g1)
    c: InternalAlignment(g8,g0)
    c: Equal(g8,g1)
    c: InternalAlignment(g9,g0)
    c: Equal(g9,g1)
    c: InternalAlignment(g10,g0)
    c: Equal(g10,g1)
    c: InternalAlignment(g11,g0)
    c: Equal(g11,g1)
    c: InternalAlignment(g12,g0)
    c: Equal(g12,g1)
    c: InternalAlignment(g13,g0)
    c: Equal(g13,g1)
    c: InternalAlignment(g14,g0)
    c: Equal(g14,g1)
    c: InternalAlignment(g15,g0)
    c: Equal(g15,g1)
    c: InternalAlignment(g16,g0)
    c: Equal(g16,g1)
    c: InternalAlignment(g17,g0)
    c: Equal(g17,g1)
    c: InternalAlignment(g18,g0)
    c: Equal(g18,g1)
    c: InternalAlignment(g19,g0)
    c: Equal(g19,g1)
    c: InternalAlignment(g20,g0)
    c: Equal(g20,g1)
    c: InternalAlignment(g21,g0)
    c: Equal(g21,g1)
    c: InternalAlignment(g22,g0)
    c: Equal(g22,g1)
    c: InternalAlignment(g23,g0)
    c: Equal(g23,g1)
    c: InternalAlignment(g24,g0)
    c: Equal(g24,g1)
    c: InternalAlignment(g25,g0)
    c: Equal(g25,g1)
    c: InternalAlignment(g26,g0)
    c: Equal(g26,g1)
    c: InternalAlignment(g27,g0)
    c: Equal(g27,g1)
    c: InternalAlignment(g28,g0)
    c: Equal(g28,g1)
    c: InternalAlignment(g29,g0)
    c: Equal(g29,g1)
    c: InternalAlignment(g30,g0)
    c: Equal(g30,g1)
    c: InternalAlignment(g31,g0)
    c: Equal(g31,g1)
    c: InternalAlignment(g32,g0)
    c: Equal(g32,g1)
    c: InternalAlignment(g33,g0)
    c: Equal(g33,g1)
    c: InternalAlignment(g34,g0)
    c: Equal(g34,g1)
    c: InternalAlignment(g35,g0)
    c: Equal(g35,g1)
    c: InternalAlignment(g36,g0)
    c: Equal(g36,g1)
    c: InternalAlignment(g37,g0)
    c: Equal(g37,g1)
    c: InternalAlignment(g38,g0)
    c: Equal(g38,g1)
    c: InternalAlignment(g39,g0)
    c: Equal(g39,g1)
    c: InternalAlignment(g40,g0)
    c: Equal(g40,g1)
    c: InternalAlignment(g41,g0)
    c: Equal(g41,g1)
    c: InternalAlignment(g42,g0)
    c: Equal(g42,g1)
    c: InternalAlignment(g43,g0)
    c: Equal(g43,g1)
    c: InternalAlignment(g44,g0)
    c: Equal(g44,g1)
    c: InternalAlignment(g45,g0)
    c: Equal(g45,g1)
    c: InternalAlignment(g46,g0)
    c: Equal(g46,g1)
    c: InternalAlignment(g47,g0)
    c: Equal(g47,g1)
    c: InternalAlignment(g48,g0)
    c: Equal(g48,g1)
    c: InternalAlignment(g49,g0)
    c: Equal(g49,g1)
    c: InternalAlignment(g50,g0)
    c: Equal(g50,g1)
    c: InternalAlignment(g51,g0)
    c: Equal(g51,g1)
    c: InternalAlignment(g52,g0)
    c: Equal(g52,g1)
    c: InternalAlignment(g53,g0)
    c: Equal(g53,g1)
    c: InternalAlignment(g54,g0)
    c: Equal(g54,g1)
    c: InternalAlignment(g55,g0)
    c: Equal(g55,g1)
    c: InternalAlignment(g56,g0)
    c: Equal(g56,g1)
    c: InternalAlignment(g57,g0)
    c: Equal(g57,g1)
    c: InternalAlignment(g58,g0)
    c: Equal(g58,g1)
    c: InternalAlignment(g59,g0)
    c: Equal(g59,g1)
    c: InternalAlignment(g60,g0)
    c: Equal(g60,g1)
    c: InternalAlignment(g61,g0)
    c: Equal(g61,g1)
    c: InternalAlignment(g62-g122 -> g0) x61
FEATURE [PartDesign::AdditiveLoft] AdditiveLoft022
  Closed = false
  Profile = -> Sketch161
  Refine = true
  Ruled = false
  Sections = -> [Sketch160]
  Suppressed = false
FEATURE [PartDesign::Plane] DatumPlane034
  AttachmentOffset = pos=(0,0,0) rot=(0,-1,0;0.785398rad)
  AttachmentSupport = -> [AdditiveLoft022]
  Length = 791.255
  MapMode = 5
  Placement = pos=(0,0,0) rot=(0,-1,0;0.785398rad)
  ResizeMode = 0
  Width = 88.7934
FEATURE [Sketcher::SketchObject] Sketch162
  ArcFitTolerance = 1e-06
  AttachmentSupport = -> [DatumPlane034]
  FullyConstrained = false
  MakeInternals = false
  MapMode = 5
  Placement = pos=(0,0,0) rot=(0,-1,0;0.785398rad)
  sketch-geometry (1):
    g0: Circle CenterX=28.3343 CenterY=4.75298 CenterZ=0 NormalX=0 NormalY=0 NormalZ=1 AngleXU=0 Radius=4.1
  constraints (1):
    c: Diameter(g0) = 8.2
FEATURE [PartDesign::Pocket] Pocket108
  BaseFeature = -> AdditiveLoft022
  Direction = (0.707107,0,-0.707107)
  Length = 1000
  Length2 = 5
  Profile = -> Sketch162
  ReferenceAxis = -> Sketch162 [N_Axis]
  Refine = true
  Suppressed = false
  Type = 0
FEATURE [PartDesign::Plane] DatumPlane035
  AttachmentOffset = pos=(0,0,0) rot=(0,-1,0;0.785398rad)
  AttachmentSupport = -> [Pocket108]
  Length = 791.255
  MapMode = 5
  Placement = pos=(0,0,0) rot=(0,-1,0;0.785398rad)
  ResizeMode = 0
  Width = 88.7934
FEATURE [Sketcher::SketchObject] Sketch163
  ArcFitTolerance = 1e-06
  AttachmentSupport = -> [Pocket108]
  FullyConstrained = false
  MakeInternals = false
  MapMode = 5
  Placement = pos=(0,0,-600) rot=(1,0,0;3.14159rad)
  sketch-geometry (4):
    g0: LineSegment StartX=-85.1873 StartY=206.739 StartZ=0 EndX=-85.1873 EndY=-145.098 EndZ=0
    g1: LineSegment StartX=-85.1873 StartY=-145.098 StartZ=0 EndX=963.672 EndY=-145.098 EndZ=0
    g2: LineSegment StartX=963.672 StartY=-145.098 StartZ=0 EndX=963.672 EndY=206.739 EndZ=0
    g3: LineSegment StartX=963.672 StartY=206.739 StartZ=0 EndX=-85.1873 EndY=206.739 EndZ=0
  constraints (8):
    c: Coincident(g0,g1)
    c: Coincident(g1,g2)
    c: Coincident(g2,g3)
    c: Coincident(g3,g0)
    c: Vertical(g0)
    c: Vertical(g2)
    c: Horizontal(g1)
    c: Horizontal(g3)
FEATURE [Sketcher::SketchObject] Sketch164
  ArcFitTolerance = 1e-06
  AttachmentSupport = -> [DatumPlane035]
  FullyConstrained = false
  MakeInternals = false
  MapMode = 5
  Placement = pos=(0,0,0) rot=(0,-1,0;0.785398rad)
  sketch-geometry (4):
    g0: LineSegment StartX=10 StartY=77.8136 StartZ=0 EndX=10 EndY=-127.239 EndZ=0
    g1: LineSegment StartX=10 StartY=-127.239 StartZ=0 EndX=548.763 EndY=-127.239 EndZ=0
    g2: LineSegment StartX=548.763 StartY=-127.239 StartZ=0 EndX=548.763 EndY=77.8136 EndZ=0
    g3: LineSegment StartX=548.763 StartY=77.8136 StartZ=0 EndX=10 EndY=77.8136 EndZ=0
  constraints (9):
    c: Coincident(g0,g1)
    c: Coincident(g1,g2)
    c: Coincident(g2,g3)
    c: Coincident(g3,g0)
    c: Vertical(g0)
    c: Vertical(g2)
    c: Horizontal(g1)
    c: Horizontal(g3)
    c: Distance(g-1,g0) = 10
FEATURE [PartDesign::Pocket] Pocket109
  BaseFeature = -> Pocket108
  Direction = (0.707107,0,-0.707107)
  Length = 1000
  Length2 = 5
  Profile = -> Sketch164
  ReferenceAxis = -> Sketch164 [N_Axis]
  Refine = true
  Suppressed = false
  Type = 0
FEATURE [Sketcher::SketchObject] Sketch165
  ArcFitTolerance = 1e-06
  AttachmentSupport = -> [Pocket109]
  FullyConstrained = false
  MakeInternals = false
  MapMode = 5
  sketch-geometry (4):
    g0: LineSegment StartX=-129.575 StartY=195.424 StartZ=0 EndX=-129.575 EndY=-278.238 EndZ=0
    g1: LineSegment StartX=-129.575 StartY=-278.238 StartZ=0 EndX=1282.72 EndY=-278.238 EndZ=0
    g2: LineSegment StartX=1282.72 StartY=-278.238 StartZ=0 EndX=1282.72 EndY=195.424 EndZ=0
    g3: LineSegment StartX=1282.72 StartY=195.424 StartZ=0 EndX=-129.575 EndY=195.424 EndZ=0
  constraints (8):
    c: Coincident(g0,g1)
    c: Coincident(g1,g2)
    c: Coincident(g2,g3)
    c: Coincident(g3,g0)
    c: Vertical(g0)
    c: Vertical(g2)
    c: Horizontal(g1)
    c: Horizontal(g3)
FEATURE [PartDesign::Pocket] Pocket110
  BaseFeature = -> Pocket109
  Direction = (0,0,-1)
  Length = 410
  Length2 = 5
  Profile = -> Sketch165
  ReferenceAxis = -> Sketch165 [N_Axis]
  Refine = true
  Suppressed = false
  Type = 0
FEATURE [PartDesign::Pocket] Pocket111
  BaseFeature = -> Pocket110
  Direction = (0,0,1)
  Length = 100
  Length2 = 5
  Profile = -> Sketch163
  ReferenceAxis = -> Sketch163 [N_Axis]
  Refine = true
  Suppressed = false
  Type = 0
FEATURE [PartDesign::Body] Body023
  AllowCompound = false
  Group = -> [Sketch161,Sketch160,AdditiveLoft022,DatumPlane034,Sketch162,Pocket108,Sketch163,DatumPlane035,Sketch164,Pocket109,Sketch165,Pocket110,Pocket111]
  Origin = -> Origin023
  Placement = pos=(0,0,-100) rot=(0,0,1;0rad)
  Tip = -> Pocket111
FEATURE [Sketcher::SketchObject] Sketch166
  ArcFitTolerance = 1e-06
  FullyConstrained = false
  MakeInternals = false
  Placement = pos=(600,0,-600) rot=(0,0,1;0rad)
  sketch-geometry (123):
    g0: BSplineCurve PolesCount=61 KnotsCount=61 Degree=3 IsPeriodic=1
    g1-g61: Circle [constr] x61 (B-spline internal-alignment scaffolding for g0; pole/knot coordinates omitted)
    g62-g122: GeomPoint [constr] x61 (B-spline internal-alignment scaffolding for g0; pole/knot coordinates omitted)
  constraints (123):
    c: InternalAlignment(g1,g0)
    c: Weight(g1) = 1
    c: InternalAlignment(g2,g0)
    c: Equal(g2,g1)
    c: InternalAlignment(g3,g0)
    c: Equal(g3,g1)
    c: InternalAlignment(g4,g0)
    c: Equal(g4,g1)
    c: InternalAlignment(g5,g0)
    c: Equal(g5,g1)
    c: InternalAlignment(g6,g0)
    c: Equal(g6,g1)
    c: InternalAlignment(g7,g0)
    c: Equal(g7,g1)
    c: InternalAlignment(g8,g0)
    c: Equal(g8,g1)
    c: InternalAlignment(g9,g0)
    c: Equal(g9,g1)
    c: InternalAlignment(g10,g0)
    c: Equal(g10,g1)
    c: InternalAlignment(g11,g0)
    c: Equal(g11,g1)
    c: InternalAlignment(g12,g0)
    c: Equal(g12,g1)
    c: InternalAlignment(g13,g0)
    c: Equal(g13,g1)
    c: InternalAlignment(g14,g0)
    c: Equal(g14,g1)
    c: InternalAlignment(g15,g0)
    c: Equal(g15,g1)
    c: InternalAlignment(g16,g0)
    c: Equal(g16,g1)
    c: InternalAlignment(g17,g0)
    c: Equal(g17,g1)
    c: InternalAlignment(g18,g0)
    c: Equal(g18,g1)
    c: InternalAlignment(g19,g0)
    c: Equal(g19,g1)
    c: InternalAlignment(g20,g0)
    c: Equal(g20,g1)
    c: InternalAlignment(g21,g0)
    c: Equal(g21,g1)
    c: InternalAlignment(g22,g0)
    c: Equal(g22,g1)
    c: InternalAlignment(g23,g0)
    c: Equal(g23,g1)
    c: InternalAlignment(g24,g0)
    c: Equal(g24,g1)
    c: InternalAlignment(g25,g0)
    c: Equal(g25,g1)
    c: InternalAlignment(g26,g0)
    c: Equal(g26,g1)
    c: InternalAlignment(g27,g0)
    c: Equal(g27,g1)
    c: InternalAlignment(g28,g0)
    c: Equal(g28,g1)
    c: InternalAlignment(g29,g0)
    c: Equal(g29,g1)
    c: InternalAlignment(g30,g0)
    c: Equal(g30,g1)
    c: InternalAlignment(g31,g0)
    c: Equal(g31,g1)
    c: InternalAlignment(g32,g0)
    c: Equal(g32,g1)
    c: InternalAlignment(g33,g0)
    c: Equal(g33,g1)
    c: InternalAlignment(g34,g0)
    c: Equal(g34,g1)
    c: InternalAlignment(g35,g0)
    c: Equal(g35,g1)
    c: InternalAlignment(g36,g0)
    c: Equal(g36,g1)
    c: InternalAlignment(g37,g0)
    c: Equal(g37,g1)
    c: InternalAlignment(g38,g0)
    c: Equal(g38,g1)
    c: InternalAlignment(g39,g0)
    c: Equal(g39,g1)
    c: InternalAlignment(g40,g0)
    c: Equal(g40,g1)
    c: InternalAlignment(g41,g0)
    c: Equal(g41,g1)
    c: InternalAlignment(g42,g0)
    c: Equal(g42,g1)
    c: InternalAlignment(g43,g0)
    c: Equal(g43,g1)
    c: InternalAlignment(g44,g0)
    c: Equal(g44,g1)
    c: InternalAlignment(g45,g0)
    c: Equal(g45,g1)
    c: InternalAlignment(g46,g0)
    c: Equal(g46,g1)
    c: InternalAlignment(g47,g0)
    c: Equal(g47,g1)
    c: InternalAlignment(g48,g0)
    c: Equal(g48,g1)
    c: InternalAlignment(g49,g0)
    c: Equal(g49,g1)
    c: InternalAlignment(g50,g0)
    c: Equal(g50,g1)
    c: InternalAlignment(g51,g0)
    c: Equal(g51,g1)
    c: InternalAlignment(g52,g0)
    c: Equal(g52,g1)
    c: InternalAlignment(g53,g0)
    c: Equal(g53,g1)
    c: InternalAlignment(g54,g0)
    c: Equal(g54,g1)
    c: InternalAlignment(g55,g0)
    c: Equal(g55,g1)
    c: InternalAlignment(g56,g0)
    c: Equal(g56,g1)
    c: InternalAlignment(g57,g0)
    c: Equal(g57,g1)
    c: InternalAlignment(g58,g0)
    c: Equal(g58,g1)
    c: InternalAlignment(g59,g0)
    c: Equal(g59,g1)
    c: InternalAlignment(g60,g0)
    c: Equal(g60,g1)
    c: InternalAlignment(g61,g0)
    c: Equal(g61,g1)
    c: InternalAlignment(g62-g122 -> g0) x61
FEATURE [Sketcher::SketchObject] Sketch167
  ArcFitTolerance = 1e-06
  FullyConstrained = false
  MakeInternals = false
  sketch-geometry (123):
    g0: BSplineCurve PolesCount=61 KnotsCount=61 Degree=3 IsPeriodic=1
    g1-g61: Circle [constr] x61 (B-spline internal-alignment scaffolding for g0; pole/knot coordinates omitted)
    g62-g122: GeomPoint [constr] x61 (B-spline internal-alignment scaffolding for g0; pole/knot coordinates omitted)
  constraints (123):
    c: InternalAlignment(g1,g0)
    c: Weight(g1) = 1
    c: InternalAlignment(g2,g0)
    c: Equal(g2,g1)
    c: InternalAlignment(g3,g0)
    c: Equal(g3,g1)
    c: InternalAlignment(g4,g0)
    c: Equal(g4,g1)
    c: InternalAlignment(g5,g0)
    c: Equal(g5,g1)
    c: InternalAlignment(g6,g0)
    c: Equal(g6,g1)
    c: InternalAlignment(g7,g0)
    c: Equal(g7,g1)
    c: InternalAlignment(g8,g0)
    c: Equal(g8,g1)
    c: InternalAlignment(g9,g0)
    c: Equal(g9,g1)
    c: InternalAlignment(g10,g0)
    c: Equal(g10,g1)
    c: InternalAlignment(g11,g0)
    c: Equal(g11,g1)
    c: InternalAlignment(g12,g0)
    c: Equal(g12,g1)
    c: InternalAlignment(g13,g0)
    c: Equal(g13,g1)
    c: InternalAlignment(g14,g0)
    c: Equal(g14,g1)
    c: InternalAlignment(g15,g0)
    c: Equal(g15,g1)
    c: InternalAlignment(g16,g0)
    c: Equal(g16,g1)
    c: InternalAlignment(g17,g0)
    c: Equal(g17,g1)
    c: InternalAlignment(g18,g0)
    c: Equal(g18,g1)
    c: InternalAlignment(g19,g0)
    c: Equal(g19,g1)
    c: InternalAlignment(g20,g0)
    c: Equal(g20,g1)
    c: InternalAlignment(g21,g0)
    c: Equal(g21,g1)
    c: InternalAlignment(g22,g0)
    c: Equal(g22,g1)
    c: InternalAlignment(g23,g0)
    c: Equal(g23,g1)
    c: InternalAlignment(g24,g0)
    c: Equal(g24,g1)
    c: InternalAlignment(g25,g0)
    c: Equal(g25,g1)
    c: InternalAlignment(g26,g0)
    c: Equal(g26,g1)
    c: InternalAlignment(g27,g0)
    c: Equal(g27,g1)
    c: InternalAlignment(g28,g0)
    c: Equal(g28,g1)
    c: InternalAlignment(g29,g0)
    c: Equal(g29,g1)
    c: InternalAlignment(g30,g0)
    c: Equal(g30,g1)
    c: InternalAlignment(g31,g0)
    c: Equal(g31,g1)
    c: InternalAlignment(g32,g0)
    c: Equal(g32,g1)
    c: InternalAlignment(g33,g0)
    c: Equal(g33,g1)
    c: InternalAlignment(g34,g0)
    c: Equal(g34,g1)
    c: InternalAlignment(g35,g0)
    c: Equal(g35,g1)
    c: InternalAlignment(g36,g0)
    c: Equal(g36,g1)
    c: InternalAlignment(g37,g0)
    c: Equal(g37,g1)
    c: InternalAlignment(g38,g0)
    c: Equal(g38,g1)
    c: InternalAlignment(g39,g0)
    c: Equal(g39,g1)
    c: InternalAlignment(g40,g0)
    c: Equal(g40,g1)
    c: InternalAlignment(g41,g0)
    c: Equal(g41,g1)
    c: InternalAlignment(g42,g0)
    c: Equal(g42,g1)
    c: InternalAlignment(g43,g0)
    c: Equal(g43,g1)
    c: InternalAlignment(g44,g0)
    c: Equal(g44,g1)
    c: InternalAlignment(g45,g0)
    c: Equal(g45,g1)
    c: InternalAlignment(g46,g0)
    c: Equal(g46,g1)
    c: InternalAlignment(g47,g0)
    c: Equal(g47,g1)
    c: InternalAlignment(g48,g0)
    c: Equal(g48,g1)
    c: InternalAlignment(g49,g0)
    c: Equal(g49,g1)
    c: InternalAlignment(g50,g0)
    c: Equal(g50,g1)
    c: InternalAlignment(g51,g0)
    c: Equal(g51,g1)
    c: InternalAlignment(g52,g0)
    c: Equal(g52,g1)
    c: InternalAlignment(g53,g0)
    c: Equal(g53,g1)
    c: InternalAlignment(g54,g0)
    c: Equal(g54,g1)
    c: InternalAlignment(g55,g0)
    c: Equal(g55,g1)
    c: InternalAlignment(g56,g0)
    c: Equal(g56,g1)
    c: InternalAlignment(g57,g0)
    c: Equal(g57,g1)
    c: InternalAlignment(g58,g0)
    c: Equal(g58,g1)
    c: InternalAlignment(g59,g0)
    c: Equal(g59,g1)
    c: InternalAlignment(g60,g0)
    c: Equal(g60,g1)
    c: InternalAlignment(g61,g0)
    c: Equal(g61,g1)
    c: InternalAlignment(g62-g122 -> g0) x61
FEATURE [PartDesign::AdditiveLoft] AdditiveLoft023
  Closed = false
  Profile = -> Sketch167
  Refine = true
  Ruled = false
  Sections = -> [Sketch166]
  Suppressed = false
FEATURE [PartDesign::Plane] DatumPlane036
  AttachmentOffset = pos=(0,0,0) rot=(0,-1,0;0.785398rad)
  AttachmentSupport = -> [AdditiveLoft023]
  Length = 921.688
  MapMode = 5
  Placement = pos=(0,0,0) rot=(0,-1,0;0.785398rad)
  ResizeMode = 0
  Width = 91.9462
FEATURE [Sketcher::SketchObject] Sketch168
  ArcFitTolerance = 1e-06
  AttachmentSupport = -> [DatumPlane036]
  FullyConstrained = false
  MakeInternals = false
  MapMode = 5
  Placement = pos=(0,0,0) rot=(0,-1,0;0.785398rad)
  sketch-geometry (1):
    g0: Circle CenterX=28.3343 CenterY=4.75298 CenterZ=0 NormalX=0 NormalY=0 NormalZ=1 AngleXU=0 Radius=4.1
  constraints (1):
    c: Diameter(g0) = 8.2
FEATURE [PartDesign::Pocket] Pocket112
  BaseFeature = -> AdditiveLoft023
  Direction = (0.707107,0,-0.707107)
  Length = 1000
  Length2 = 5
  Profile = -> Sketch168
  ReferenceAxis = -> Sketch168 [N_Axis]
  Refine = true
  Suppressed = false
  Type = 0
FEATURE [PartDesign::Plane] DatumPlane037
  AttachmentOffset = pos=(0,0,0) rot=(0,-1,0;0.785398rad)
  AttachmentSupport = -> [Pocket112]
  Length = 921.688
  MapMode = 5
  Placement = pos=(0,0,0) rot=(0,-1,0;0.785398rad)
  ResizeMode = 0
  Width = 91.9462
FEATURE [Sketcher::SketchObject] Sketch169
  ArcFitTolerance = 1e-06
  AttachmentSupport = -> [Pocket112]
  FullyConstrained = false
  MakeInternals = false
  MapMode = 5
  Placement = pos=(0,0,-600) rot=(1,0,0;3.14159rad)
  sketch-geometry (4):
    g0: LineSegment StartX=-85.1873 StartY=206.739 StartZ=0 EndX=-85.1873 EndY=-145.098 EndZ=0
    g1: LineSegment StartX=-85.1873 StartY=-145.098 StartZ=0 EndX=963.672 EndY=-145.098 EndZ=0
    g2: LineSegment StartX=963.672 StartY=-145.098 StartZ=0 EndX=963.672 EndY=206.739 EndZ=0
    g3: LineSegment StartX=963.672 StartY=206.739 StartZ=0 EndX=-85.1873 EndY=206.739 EndZ=0
  constraints (8):
    c: Coincident(g0,g1)
    c: Coincident(g1,g2)
    c: Coincident(g2,g3)
    c: Coincident(g3,g0)
    c: Vertical(g0)
    c: Vertical(g2)
    c: Horizontal(g1)
    c: Horizontal(g3)
FEATURE [Sketcher::SketchObject] Sketch170
  ArcFitTolerance = 1e-06
  AttachmentSupport = -> [DatumPlane037]
  FullyConstrained = false
  MakeInternals = false
  MapMode = 5
  Placement = pos=(0,0,0) rot=(0,-1,0;0.785398rad)
  sketch-geometry (4):
    g0: LineSegment StartX=10 StartY=77.8136 StartZ=0 EndX=10 EndY=-127.239 EndZ=0
    g1: LineSegment StartX=10 StartY=-127.239 StartZ=0 EndX=548.763 EndY=-127.239 EndZ=0
    g2: LineSegment StartX=548.763 StartY=-127.239 StartZ=0 EndX=548.763 EndY=77.8136 EndZ=0
    g3: LineSegment StartX=548.763 StartY=77.8136 StartZ=0 EndX=10 EndY=77.8136 EndZ=0
  constraints (9):
    c: Coincident(g0,g1)
    c: Coincident(g1,g2)
    c: Coincident(g2,g3)
    c: Coincident(g3,g0)
    c: Vertical(g0)
    c: Vertical(g2)
    c: Horizontal(g1)
    c: Horizontal(g3)
    c: Distance(g-1,g0) = 10
FEATURE [PartDesign::Pocket] Pocket113
  BaseFeature = -> Pocket112
  Direction = (0.707107,0,-0.707107)
  Length = 1000
  Length2 = 5
  Profile = -> Sketch170
  ReferenceAxis = -> Sketch170 [N_Axis]
  Refine = true
  Suppressed = false
  Type = 0
FEATURE [Sketcher::SketchObject] Sketch171
  ArcFitTolerance = 1e-06
  AttachmentSupport = -> [Pocket113]
  FullyConstrained = false
  MakeInternals = false
  MapMode = 5
  sketch-geometry (4):
    g0: LineSegment StartX=-129.575 StartY=195.424 StartZ=0 EndX=-129.575 EndY=-278.238 EndZ=0
    g1: LineSegment StartX=-129.575 StartY=-278.238 StartZ=0 EndX=1282.72 EndY=-278.238 EndZ=0
    g2: LineSegment StartX=1282.72 StartY=-278.238 StartZ=0 EndX=1282.72 EndY=195.424 EndZ=0
    g3: LineSegment StartX=1282.72 StartY=195.424 StartZ=0 EndX=-129.575 EndY=195.424 EndZ=0
  constraints (8):
    c: Coincident(g0,g1)
    c: Coincident(g1,g2)
    c: Coincident(g2,g3)
    c: Coincident(g3,g0)
    c: Vertical(g0)
    c: Vertical(g2)
    c: Horizontal(g1)
    c: Horizontal(g3)
FEATURE [PartDesign::Pocket] Pocket114
  BaseFeature = -> Pocket113
  Direction = (0,0,-1)
  Length = 510
  Length2 = 5
  Profile = -> Sketch171
  ReferenceAxis = -> Sketch171 [N_Axis]
  Refine = true
  Suppressed = false
  Type = 0
FEATURE [PartDesign::Pocket] Pocket115
  BaseFeature = -> Pocket114
  Direction = (0,0,1)
  Length = 10
  Length2 = 5
  Profile = -> Sketch169
  ReferenceAxis = -> Sketch169 [N_Axis]
  Refine = true
  Suppressed = false
  Type = 0
FEATURE [PartDesign::Body] Body024
  AllowCompound = false
  Group = -> [Sketch167,Sketch166,AdditiveLoft023,DatumPlane036,Sketch168,Pocket112,Sketch169,DatumPlane037,Sketch170,Pocket113,Sketch171,Pocket114,Pocket115]
  Origin = -> Origin024
  Placement = pos=(0,0,-100) rot=(0,0,1;0rad)
  Tip = -> Pocket115
FEATURE [Part::Mirroring] Part__Mirroring018  label="Body019 (Mirror #19)"
  Base = (0,0,0)
  Normal = (0,0,1)
  Source = -> Body019
FEATURE [Part::Mirroring] Part__Mirroring019  label="Body020 (Mirror #20)"
  Base = (0,0,0)
  Normal = (0,0,1)
  Source = -> Body020
FEATURE [Part::Mirroring] Part__Mirroring020  label="Body021 (Mirror #21)"
  Base = (0,0,0)
  Normal = (0,0,1)
  Source = -> Body021
FEATURE [Part::Mirroring] Part__Mirroring021  label="Body022 (Mirror #22)"
  Base = (0,0,0)
  Normal = (0,0,1)
  Source = -> Body022
FEATURE [Part::Mirroring] Part__Mirroring022  label="Body023 (Mirror #23)"
  Base = (0,0,0)
  Normal = (0,0,1)
  Source = -> Body023
FEATURE [Part::Mirroring] Part__Mirroring023  label="Body024 (Mirror #24)"
  Base = (0,0,0)
  Normal = (0,0,1)
  Source = -> Body024
FEATURE [Sketcher::SketchObject] Sketch173
  ArcFitTolerance = 1e-06
  FullyConstrained = false
  MakeInternals = false
  sketch-geometry (123):
    g0: BSplineCurve PolesCount=61 KnotsCount=61 Degree=3 IsPeriodic=1
    g1-g61: Circle [constr] x61 (B-spline internal-alignment scaffolding for g0; pole/knot coordinates omitted)
    g62-g122: GeomPoint [constr] x61 (B-spline internal-alignment scaffolding for g0; pole/knot coordinates omitted)
  constraints (123):
    c: InternalAlignment(g1,g0)
    c: Weight(g1) = 1
    c: InternalAlignment(g2,g0)
    c: Equal(g2,g1)
    c: InternalAlignment(g3,g0)
    c: Equal(g3,g1)
    c: InternalAlignment(g4,g0)
    c: Equal(g4,g1)
    c: InternalAlignment(g5,g0)
    c: Equal(g5,g1)
    c: InternalAlignment(g6,g0)
    c: Equal(g6,g1)
    c: InternalAlignment(g7,g0)
    c: Equal(g7,g1)
    c: InternalAlignment(g8,g0)
    c: Equal(g8,g1)
    c: InternalAlignment(g9,g0)
    c: Equal(g9,g1)
    c: InternalAlignment(g10,g0)
    c: Equal(g10,g1)
    c: InternalAlignment(g11,g0)
    c: Equal(g11,g1)
    c: InternalAlignment(g12,g0)
    c: Equal(g12,g1)
    c: InternalAlignment(g13,g0)
    c: Equal(g13,g1)
    c: InternalAlignment(g14,g0)
    c: Equal(g14,g1)
    c: InternalAlignment(g15,g0)
    c: Equal(g15,g1)
    c: InternalAlignment(g16,g0)
    c: Equal(g16,g1)
    c: InternalAlignment(g17,g0)
    c: Equal(g17,g1)
    c: InternalAlignment(g18,g0)
    c: Equal(g18,g1)
    c: InternalAlignment(g19,g0)
    c: Equal(g19,g1)
    c: InternalAlignment(g20,g0)
    c: Equal(g20,g1)
    c: InternalAlignment(g21,g0)
    c: Equal(g21,g1)
    c: InternalAlignment(g22,g0)
    c: Equal(g22,g1)
    c: InternalAlignment(g23,g0)
    c: Equal(g23,g1)
    c: InternalAlignment(g24,g0)
    c: Equal(g24,g1)
    c: InternalAlignment(g25,g0)
    c: Equal(g25,g1)
    c: InternalAlignment(g26,g0)
    c: Equal(g26,g1)
    c: InternalAlignment(g27,g0)
    c: Equal(g27,g1)
    c: InternalAlignment(g28,g0)
    c: Equal(g28,g1)
    c: InternalAlignment(g29,g0)
    c: Equal(g29,g1)
    c: InternalAlignment(g30,g0)
    c: Equal(g30,g1)
    c: InternalAlignment(g31,g0)
    c: Equal(g31,g1)
    c: InternalAlignment(g32,g0)
    c: Equal(g32,g1)
    c: InternalAlignment(g33,g0)
    c: Equal(g33,g1)
    c: InternalAlignment(g34,g0)
    c: Equal(g34,g1)
    c: InternalAlignment(g35,g0)
    c: Equal(g35,g1)
    c: InternalAlignment(g36,g0)
    c: Equal(g36,g1)
    c: InternalAlignment(g37,g0)
    c: Equal(g37,g1)
    c: InternalAlignment(g38,g0)
    c: Equal(g38,g1)
    c: InternalAlignment(g39,g0)
    c: Equal(g39,g1)
    c: InternalAlignment(g40,g0)
    c: Equal(g40,g1)
    c: InternalAlignment(g41,g0)
    c: Equal(g41,g1)
    c: InternalAlignment(g42,g0)
    c: Equal(g42,g1)
    c: InternalAlignment(g43,g0)
    c: Equal(g43,g1)
    c: InternalAlignment(g44,g0)
    c: Equal(g44,g1)
    c: InternalAlignment(g45,g0)
    c: Equal(g45,g1)
    c: InternalAlignment(g46,g0)
    c: Equal(g46,g1)
    c: InternalAlignment(g47,g0)
    c: Equal(g47,g1)
    c: InternalAlignment(g48,g0)
    c: Equal(g48,g1)
    c: InternalAlignment(g49,g0)
    c: Equal(g49,g1)
    c: InternalAlignment(g50,g0)
    c: Equal(g50,g1)
    c: InternalAlignment(g51,g0)
    c: Equal(g51,g1)
    c: InternalAlignment(g52,g0)
    c: Equal(g52,g1)
    c: InternalAlignment(g53,g0)
    c: Equal(g53,g1)
    c: InternalAlignment(g54,g0)
    c: Equal(g54,g1)
    c: InternalAlignment(g55,g0)
    c: Equal(g55,g1)
    c: InternalAlignment(g56,g0)
    c: Equal(g56,g1)
    c: InternalAlignment(g57,g0)
    c: Equal(g57,g1)
    c: InternalAlignment(g58,g0)
    c: Equal(g58,g1)
    c: InternalAlignment(g59,g0)
    c: Equal(g59,g1)
    c: InternalAlignment(g60,g0)
    c: Equal(g60,g1)
    c: InternalAlignment(g61,g0)
    c: Equal(g61,g1)
    c: InternalAlignment(g62-g122 -> g0) x61
FEATURE [PartDesign::Plane] DatumPlane038
  AttachmentOffset = pos=(0,0,-50) rot=(0,0,1;0rad)
  AttachmentSupport = -> [XZ_Plane025]
  Length = 531.958
  MapMode = 5
  Placement = pos=(0,50,-1.11e-14) rot=(1,0,0;1.5708rad)
  ResizeMode = 0
  Width = 289.839
FEATURE [Sketcher::SketchObject] Sketch174
  ArcFitTolerance = 1e-06
  AttachmentSupport = -> [DatumPlane038]
  FullyConstrained = false
  MakeInternals = false
  MapMode = 5
  Placement = pos=(0,50,-1.11e-14) rot=(1,0,0;1.5708rad)
  sketch-geometry (16):
    g0: LineSegment StartX=430 StartY=190 StartZ=0 EndX=15 EndY=190 EndZ=0
    g1: LineSegment StartX=15 StartY=190 StartZ=0 EndX=15 EndY=10 EndZ=0
    g2: LineSegment StartX=15 StartY=10 StartZ=0 EndX=430 EndY=10 EndZ=0
    g3: LineSegment StartX=430 StartY=190 StartZ=0 EndX=430 EndY=163.313 EndZ=0
    g4: LineSegment StartX=430 StartY=163.313 StartZ=0 EndX=300 EndY=133.415 EndZ=0
    g5: LineSegment StartX=300 StartY=133.415 StartZ=0 EndX=300 EndY=66.5851 EndZ=0
    g6: LineSegment StartX=300 StartY=66.5851 StartZ=0 EndX=430 EndY=36.6872 EndZ=0
    g7: LineSegment StartX=430 StartY=36.6872 StartZ=0 EndX=430 EndY=10 EndZ=0
    g8: LineSegment StartX=455.007 StartY=144.201 StartZ=0 EndX=415 EndY=135 EndZ=0
    g9: LineSegment StartX=415 StartY=135 StartZ=0 EndX=415 EndY=65 EndZ=0
    g10: LineSegment StartX=415 StartY=65 StartZ=0 EndX=455.007 EndY=55.7991 EndZ=0
    g11: LineSegment StartX=455.007 StartY=55.7991 StartZ=0 EndX=455.007 EndY=144.201 EndZ=0
    g12: Circle CenterX=350 CenterY=115 CenterZ=0 NormalX=0 NormalY=0 NormalZ=1 AngleXU=0 Radius=1.5
    g13: Circle CenterX=350 CenterY=85 CenterZ=0 NormalX=0 NormalY=0 NormalZ=1 AngleXU=0 Radius=1.5
    g14: Circle CenterX=380 CenterY=80 CenterZ=0 NormalX=0 NormalY=0 NormalZ=1 AngleXU=0 Radius=1.5
    g15: Circle CenterX=380 CenterY=120 CenterZ=0 NormalX=0 NormalY=0 NormalZ=1 AngleXU=0 Radius=1.5
  constraints (35):
    c: Coincident(g0,g1)
    c: Coincident(g1,g2)
    c: Vertical(g1)
    c: Horizontal(g0)
    c: Horizontal(g2)
    c: DistanceY(g-1,g1) = 10
    c: DistanceY(g1,g1) = 180
    c: DistanceX(g-1,g1) = 15
    c: DistanceX(g-1,g2) = 430
    c: Block(g0)
    c: Coincident(g0,g3)
    c: Vertical(g3)
    c: Coincident(g3,g4)
    c: Coincident(g4,g5)
    c: Coincident(g5,g6)
    c: Coincident(g6,g7)
    c: Coincident(g7,g2)
    c: Vertical(g7)
    c: Coincident(g8,g9)
    c: Coincident(g9,g10)
    c: Coincident(g10,g11)
    c: Coincident(g11,g8)
    c: Vertical(g11)
    c: Parallel(g4,g8)
    c: Parallel(g6,g10)
    c: DistanceX(g5,g2) = 130
    c: DistanceY(g9,g9) = 70
    c: Diameter(g12) = 3
    c: Diameter(g13) = 3
    c: Diameter(g14) = 3
    c: Diameter(g15) = 3
    c: DistanceX(g-1,g13) = 350
    c: DistanceY(g13,g12) = 30
    c: DistanceY(g14,g15) = 40
    c: DistanceX(g13,g14) = 30
FEATURE [Sketcher::SketchObject] Sketch175
  ArcFitTolerance = 1e-06
  FullyConstrained = false
  MakeInternals = false
  Placement = pos=(600,0,-600) rot=(0,0,1;0rad)
  sketch-geometry (123):
    g0: BSplineCurve PolesCount=61 KnotsCount=61 Degree=3 IsPeriodic=1
    g1-g61: Circle [constr] x61 (B-spline internal-alignment scaffolding for g0; pole/knot coordinates omitted)
    g62-g122: GeomPoint [constr] x61 (B-spline internal-alignment scaffolding for g0; pole/knot coordinates omitted)
  constraints (123):
    c: InternalAlignment(g1,g0)
    c: Weight(g1) = 1
    c: InternalAlignment(g2,g0)
    c: Equal(g2,g1)
    c: InternalAlignment(g3,g0)
    c: Equal(g3,g1)
    c: InternalAlignment(g4,g0)
    c: Equal(g4,g1)
    c: InternalAlignment(g5,g0)
    c: Equal(g5,g1)
    c: InternalAlignment(g6,g0)
    c: Equal(g6,g1)
    c: InternalAlignment(g7,g0)
    c: Equal(g7,g1)
    c: InternalAlignment(g8,g0)
    c: Equal(g8,g1)
    c: InternalAlignment(g9,g0)
    c: Equal(g9,g1)
    c: InternalAlignment(g10,g0)
    c: Equal(g10,g1)
    c: InternalAlignment(g11,g0)
    c: Equal(g11,g1)
    c: InternalAlignment(g12,g0)
    c: Equal(g12,g1)
    c: InternalAlignment(g13,g0)
    c: Equal(g13,g1)
    c: InternalAlignment(g14,g0)
    c: Equal(g14,g1)
    c: InternalAlignment(g15,g0)
    c: Equal(g15,g1)
    c: InternalAlignment(g16,g0)
    c: Equal(g16,g1)
    c: InternalAlignment(g17,g0)
    c: Equal(g17,g1)
    c: InternalAlignment(g18,g0)
    c: Equal(g18,g1)
    c: InternalAlignment(g19,g0)
    c: Equal(g19,g1)
    c: InternalAlignment(g20,g0)
    c: Equal(g20,g1)
    c: InternalAlignment(g21,g0)
    c: Equal(g21,g1)
    c: InternalAlignment(g22,g0)
    c: Equal(g22,g1)
    c: InternalAlignment(g23,g0)
    c: Equal(g23,g1)
    c: InternalAlignment(g24,g0)
    c: Equal(g24,g1)
    c: InternalAlignment(g25,g0)
    c: Equal(g25,g1)
    c: InternalAlignment(g26,g0)
    c: Equal(g26,g1)
    c: InternalAlignment(g27,g0)
    c: Equal(g27,g1)
    c: InternalAlignment(g28,g0)
    c: Equal(g28,g1)
    c: InternalAlignment(g29,g0)
    c: Equal(g29,g1)
    c: InternalAlignment(g30,g0)
    c: Equal(g30,g1)
    c: InternalAlignment(g31,g0)
    c: Equal(g31,g1)
    c: InternalAlignment(g32,g0)
    c: Equal(g32,g1)
    c: InternalAlignment(g33,g0)
    c: Equal(g33,g1)
    c: InternalAlignment(g34,g0)
    c: Equal(g34,g1)
    c: InternalAlignment(g35,g0)
    c: Equal(g35,g1)
    c: InternalAlignment(g36,g0)
    c: Equal(g36,g1)
    c: InternalAlignment(g37,g0)
    c: Equal(g37,g1)
    c: InternalAlignment(g38,g0)
    c: Equal(g38,g1)
    c: InternalAlignment(g39,g0)
    c: Equal(g39,g1)
    c: InternalAlignment(g40,g0)
    c: Equal(g40,g1)
    c: InternalAlignment(g41,g0)
    c: Equal(g41,g1)
    c: InternalAlignment(g42,g0)
    c: Equal(g42,g1)
    c: InternalAlignment(g43,g0)
    c: Equal(g43,g1)
    c: InternalAlignment(g44,g0)
    c: Equal(g44,g1)
    c: InternalAlignment(g45,g0)
    c: Equal(g45,g1)
    c: InternalAlignment(g46,g0)
    c: Equal(g46,g1)
    c: InternalAlignment(g47,g0)
    c: Equal(g47,g1)
    c: InternalAlignment(g48,g0)
    c: Equal(g48,g1)
    c: InternalAlignment(g49,g0)
    c: Equal(g49,g1)
    c: InternalAlignment(g50,g0)
    c: Equal(g50,g1)
    c: InternalAlignment(g51,g0)
    c: Equal(g51,g1)
    c: InternalAlignment(g52,g0)
    c: Equal(g52,g1)
    c: InternalAlignment(g53,g0)
    c: Equal(g53,g1)
    c: InternalAlignment(g54,g0)
    c: Equal(g54,g1)
    c: InternalAlignment(g55,g0)
    c: Equal(g55,g1)
    c: InternalAlignment(g56,g0)
    c: Equal(g56,g1)
    c: InternalAlignment(g57,g0)
    c: Equal(g57,g1)
    c: InternalAlignment(g58,g0)
    c: Equal(g58,g1)
    c: InternalAlignment(g59,g0)
    c: Equal(g59,g1)
    c: InternalAlignment(g60,g0)
    c: Equal(g60,g1)
    c: InternalAlignment(g61,g0)
    c: Equal(g61,g1)
    c: InternalAlignment(g62-g122 -> g0) x61
FEATURE [Sketcher::SketchObject] Sketch176
  ArcFitTolerance = 1e-06
  FullyConstrained = false
  MakeInternals = false
  sketch-geometry (123):
    g0: BSplineCurve PolesCount=61 KnotsCount=61 Degree=3 IsPeriodic=1
    g1-g61: Circle [constr] x61 (B-spline internal-alignment scaffolding for g0; pole/knot coordinates omitted)
    g62-g122: GeomPoint [constr] x61 (B-spline internal-alignment scaffolding for g0; pole/knot coordinates omitted)
  constraints (123):
    c: InternalAlignment(g1,g0)
    c: Weight(g1) = 1
    c: InternalAlignment(g2,g0)
    c: Equal(g2,g1)
    c: InternalAlignment(g3,g0)
    c: Equal(g3,g1)
    c: InternalAlignment(g4,g0)
    c: Equal(g4,g1)
    c: InternalAlignment(g5,g0)
    c: Equal(g5,g1)
    c: InternalAlignment(g6,g0)
    c: Equal(g6,g1)
    c: InternalAlignment(g7,g0)
    c: Equal(g7,g1)
    c: InternalAlignment(g8,g0)
    c: Equal(g8,g1)
    c: InternalAlignment(g9,g0)
    c: Equal(g9,g1)
    c: InternalAlignment(g10,g0)
    c: Equal(g10,g1)
    c: InternalAlignment(g11,g0)
    c: Equal(g11,g1)
    c: InternalAlignment(g12,g0)
    c: Equal(g12,g1)
    c: InternalAlignment(g13,g0)
    c: Equal(g13,g1)
    c: InternalAlignment(g14,g0)
    c: Equal(g14,g1)
    c: InternalAlignment(g15,g0)
    c: Equal(g15,g1)
    c: InternalAlignment(g16,g0)
    c: Equal(g16,g1)
    c: InternalAlignment(g17,g0)
    c: Equal(g17,g1)
    c: InternalAlignment(g18,g0)
    c: Equal(g18,g1)
    c: InternalAlignment(g19,g0)
    c: Equal(g19,g1)
    c: InternalAlignment(g20,g0)
    c: Equal(g20,g1)
    c: InternalAlignment(g21,g0)
    c: Equal(g21,g1)
    c: InternalAlignment(g22,g0)
    c: Equal(g22,g1)
    c: InternalAlignment(g23,g0)
    c: Equal(g23,g1)
    c: InternalAlignment(g24,g0)
    c: Equal(g24,g1)
    c: InternalAlignment(g25,g0)
    c: Equal(g25,g1)
    c: InternalAlignment(g26,g0)
    c: Equal(g26,g1)
    c: InternalAlignment(g27,g0)
    c: Equal(g27,g1)
    c: InternalAlignment(g28,g0)
    c: Equal(g28,g1)
    c: InternalAlignment(g29,g0)
    c: Equal(g29,g1)
    c: InternalAlignment(g30,g0)
    c: Equal(g30,g1)
    c: InternalAlignment(g31,g0)
    c: Equal(g31,g1)
    c: InternalAlignment(g32,g0)
    c: Equal(g32,g1)
    c: InternalAlignment(g33,g0)
    c: Equal(g33,g1)
    c: InternalAlignment(g34,g0)
    c: Equal(g34,g1)
    c: InternalAlignment(g35,g0)
    c: Equal(g35,g1)
    c: InternalAlignment(g36,g0)
    c: Equal(g36,g1)
    c: InternalAlignment(g37,g0)
    c: Equal(g37,g1)
    c: InternalAlignment(g38,g0)
    c: Equal(g38,g1)
    c: InternalAlignment(g39,g0)
    c: Equal(g39,g1)
    c: InternalAlignment(g40,g0)
    c: Equal(g40,g1)
    c: InternalAlignment(g41,g0)
    c: Equal(g41,g1)
    c: InternalAlignment(g42,g0)
    c: Equal(g42,g1)
    c: InternalAlignment(g43,g0)
    c: Equal(g43,g1)
    c: InternalAlignment(g44,g0)
    c: Equal(g44,g1)
    c: InternalAlignment(g45,g0)
    c: Equal(g45,g1)
    c: InternalAlignment(g46,g0)
    c: Equal(g46,g1)
    c: InternalAlignment(g47,g0)
    c: Equal(g47,g1)
    c: InternalAlignment(g48,g0)
    c: Equal(g48,g1)
    c: InternalAlignment(g49,g0)
    c: Equal(g49,g1)
    c: InternalAlignment(g50,g0)
    c: Equal(g50,g1)
    c: InternalAlignment(g51,g0)
    c: Equal(g51,g1)
    c: InternalAlignment(g52,g0)
    c: Equal(g52,g1)
    c: InternalAlignment(g53,g0)
    c: Equal(g53,g1)
    c: InternalAlignment(g54,g0)
    c: Equal(g54,g1)
    c: InternalAlignment(g55,g0)
    c: Equal(g55,g1)
    c: InternalAlignment(g56,g0)
    c: Equal(g56,g1)
    c: InternalAlignment(g57,g0)
    c: Equal(g57,g1)
    c: InternalAlignment(g58,g0)
    c: Equal(g58,g1)
    c: InternalAlignment(g59,g0)
    c: Equal(g59,g1)
    c: InternalAlignment(g60,g0)
    c: Equal(g60,g1)
    c: InternalAlignment(g61,g0)
    c: Equal(g61,g1)
    c: InternalAlignment(g62-g122 -> g0) x61
FEATURE [PartDesign::AdditiveLoft] AdditiveLoft024
  Closed = false
  Profile = -> Sketch176
  Refine = true
  Ruled = false
  Sections = -> [Sketch175]
  Suppressed = false
FEATURE [Sketcher::SketchObject] Sketch177
  ArcFitTolerance = 1e-06
  AttachmentSupport = -> [AdditiveLoft024]
  FullyConstrained = false
  MakeInternals = false
  MapMode = 5
  Placement = pos=(0,0,-600) rot=(1,0,0;3.14159rad)
  sketch-geometry (4):
    g0: LineSegment StartX=-65.1827 StartY=101.59 StartZ=0 EndX=-65.1827 EndY=-166.389 EndZ=0
    g1: LineSegment StartX=-65.1827 StartY=-166.389 StartZ=0 EndX=998.087 EndY=-166.389 EndZ=0
    g2: LineSegment StartX=998.087 StartY=-166.389 StartZ=0 EndX=998.087 EndY=101.59 EndZ=0
    g3: LineSegment StartX=998.087 StartY=101.59 StartZ=0 EndX=-65.1827 EndY=101.59 EndZ=0
  constraints (8):
    c: Coincident(g0,g1)
    c: Coincident(g1,g2)
    c: Coincident(g2,g3)
    c: Coincident(g3,g0)
    c: Vertical(g0)
    c: Vertical(g2)
    c: Horizontal(g1)
    c: Horizontal(g3)
FEATURE [PartDesign::Pocket] Pocket117
  BaseFeature = -> AdditiveLoft024
  Direction = (0,0,1)
  Length = 100
  Length2 = 5
  Profile = -> Sketch177
  ReferenceAxis = -> Sketch177 [N_Axis]
  Refine = true
  Suppressed = false
  Type = 0
FEATURE [Sketcher::SketchObject] Sketch178
  ArcFitTolerance = 1e-06
  AttachmentSupport = -> [Pocket117]
  FullyConstrained = false
  MakeInternals = false
  MapMode = 5
  sketch-geometry (4):
    g0: LineSegment StartX=-195.266 StartY=329.272 StartZ=0 EndX=-195.266 EndY=-247.112 EndZ=0
    g1: LineSegment StartX=-195.266 StartY=-247.112 StartZ=0 EndX=978.416 EndY=-247.112 EndZ=0
    g2: LineSegment StartX=978.416 StartY=-247.112 StartZ=0 EndX=978.416 EndY=329.272 EndZ=0
    g3: LineSegment StartX=978.416 StartY=329.272 StartZ=0 EndX=-195.266 EndY=329.272 EndZ=0
  constraints (8):
    c: Coincident(g0,g1)
    c: Coincident(g1,g2)
    c: Coincident(g2,g3)
    c: Coincident(g3,g0)
    c: Vertical(g0)
    c: Vertical(g2)
    c: Horizontal(g1)
    c: Horizontal(g3)
FEATURE [PartDesign::Pocket] Pocket118
  BaseFeature = -> Pocket117
  Direction = (0,0,-1)
  Length = 410
  Length2 = 5
  Profile = -> Sketch178
  ReferenceAxis = -> Sketch178 [N_Axis]
  Refine = true
  Suppressed = false
  Type = 0
FEATURE [PartDesign::Plane] DatumPlane039
  AttachmentOffset = pos=(0,0,-50) rot=(0,0,1;0.540354rad)
  AttachmentSupport = -> [XZ_Plane026]
  Length = 1006.21
  MapMode = 5
  Placement = pos=(0,50,-1.11e-14) rot=(0.931129,-0.257875,0.257875;1.64209rad)
  ResizeMode = 0
  Width = 957.253
FEATURE [Sketcher::SketchObject] Sketch179
  ArcFitTolerance = 1e-06
  AttachmentSupport = -> [DatumPlane039]
  FullyConstrained = false
  MakeInternals = false
  MapMode = 5
  Placement = pos=(0,50,-1.11e-14) rot=(0.931129,-0.257875,0.257875;1.64209rad)
  sketch-geometry (8):
    g0: LineSegment StartX=259.377 StartY=-774.22 StartZ=0 EndX=293.911 EndY=-774.22 EndZ=0
    g1: LineSegment StartX=293.911 StartY=-774.22 StartZ=0 EndX=293.911 EndY=-706.383 EndZ=0
    g2: LineSegment StartX=293.911 StartY=-706.383 StartZ=0 EndX=259.377 EndY=-706.383 EndZ=0
    g3: LineSegment StartX=259.377 StartY=-706.383 StartZ=0 EndX=259.377 EndY=-774.22 EndZ=0
    g4: LineSegment StartX=125.141 StartY=-946.934 StartZ=0 EndX=475.805 EndY=-946.934 EndZ=0
    g5: LineSegment StartX=475.805 StartY=-946.934 StartZ=0 EndX=475.805 EndY=-487.14 EndZ=0
    g6: LineSegment StartX=475.805 StartY=-487.14 StartZ=0 EndX=125.141 EndY=-487.14 EndZ=0
    g7: LineSegment StartX=125.141 StartY=-487.14 StartZ=0 EndX=125.141 EndY=-946.934 EndZ=0
  constraints (16):
    c: Coincident(g0,g1)
    c: Coincident(g1,g2)
    c: Coincident(g2,g3)
    c: Coincident(g3,g0)
    c: Horizontal(g0)
    c: Horizontal(g2)
    c: Vertical(g1)
    c: Vertical(g3)
    c: Coincident(g4,g5)
    c: Coincident(g5,g6)
    c: Coincident(g6,g7)
    c: Coincident(g7,g4)
    c: Horizontal(g4)
    c: Horizontal(g6)
    c: Vertical(g5)
    c: Vertical(g7)
FEATURE [PartDesign::Pocket] Pocket119
  BaseFeature = -> Pocket118
  Direction = (0,1,0)
  Length = 100
  Length2 = 5
  Profile = -> Sketch179
  ReferenceAxis = -> Sketch179 [N_Axis]
  Refine = true
  Reversed = true
  Suppressed = false
  Type = 0
FEATURE [Sketcher::SketchObject] Sketch180
  ArcFitTolerance = 1e-06
  AttachmentSupport = -> [DatumPlane039]
  FullyConstrained = false
  MakeInternals = false
  MapMode = 5
  Placement = pos=(0,50,-1.11e-14) rot=(0.931129,-0.257875,0.257875;1.64209rad)
  sketch-geometry (20):
    g0: LineSegment StartX=264.29 StartY=-709.229 StartZ=0 EndX=264.29 EndY=-723.829 EndZ=0
    g1: LineSegment StartX=264.29 StartY=-733.729 StartZ=0 EndX=268.283 EndY=-733.729 EndZ=0
    g2: LineSegment StartX=288.29 StartY=-733.729 StartZ=0 EndX=288.29 EndY=-727.529 EndZ=0
    g3: LineSegment StartX=288.29 StartY=-709.229 StartZ=0 EndX=286.89 EndY=-709.229 EndZ=0
    g4: LineSegment StartX=264.29 StartY=-723.829 StartZ=0 EndX=261.04 EndY=-723.829 EndZ=0
    g5: LineSegment StartX=261.04 StartY=-723.829 StartZ=0 EndX=261.04 EndY=-727.529 EndZ=0
    g6: LineSegment StartX=261.04 StartY=-727.529 StartZ=0 EndX=264.29 EndY=-727.529 EndZ=0
    g7: LineSegment StartX=288.29 StartY=-727.529 StartZ=0 EndX=291.54 EndY=-727.529 EndZ=0
    g8: LineSegment StartX=291.54 StartY=-727.529 StartZ=0 EndX=291.54 EndY=-723.829 EndZ=0
    g9: LineSegment StartX=291.54 StartY=-723.829 StartZ=0 EndX=288.29 EndY=-723.829 EndZ=0
    g10: LineSegment StartX=298.283 StartY=-741.729 StartZ=0 EndX=268.283 EndY=-741.729 EndZ=0
    g11: LineSegment StartX=268.283 StartY=-741.729 StartZ=0 EndX=268.283 EndY=-733.729 EndZ=0
    g12: LineSegment StartX=264.29 StartY=-727.529 StartZ=0 EndX=264.29 EndY=-733.729 EndZ=0
    g13: LineSegment StartX=288.29 StartY=-723.829 StartZ=0 EndX=288.29 EndY=-709.229 EndZ=0
    g14: LineSegment StartX=288.29 StartY=-733.729 StartZ=0 EndX=298.283 EndY=-733.729 EndZ=0
    g15: LineSegment StartX=298.283 StartY=-733.729 StartZ=0 EndX=298.283 EndY=-741.729 EndZ=0
    g16: LineSegment StartX=281.89 StartY=-709.229 StartZ=0 EndX=281.89 EndY=-705.06 EndZ=0
    g17: LineSegment StartX=281.89 StartY=-705.06 StartZ=0 EndX=286.89 EndY=-705.06 EndZ=0
    g18: LineSegment StartX=286.89 StartY=-705.06 StartZ=0 EndX=286.89 EndY=-709.229 EndZ=0
    g19: LineSegment StartX=281.89 StartY=-709.229 StartZ=0 EndX=264.29 EndY=-709.229 EndZ=0
  constraints (57):
    c: Coincident(g12,g1)
    c: Coincident(g13,g3)
    c: Coincident(g19,g0)
    c: Vertical(g0)
    c: Vertical(g2)
    c: Horizontal(g1)
    c: Horizontal(g3)
    c: DistanceY(g2,g13) = 24.5
    c: DistanceX(g19,g3) = 24
    c: Horizontal(g4)
    c: Coincident(g4,g5)
    c: Vertical(g5)
    c: Coincident(g5,g6)
    c: PointOnObject(g6,g12)
    c: Horizontal(g6)
    c: Horizontal(g7)
    c: Coincident(g7,g8)
    c: Coincident(g8,g9)
    c: PointOnObject(g9,g13)
    c: Horizontal(g9)
    c: Vertical(g8)
    c: Equal(g6,g7)
    c: DistanceX(g5,g7) = 30.5
    c: DistanceY(g8,g13) = 14.6
    c: DistanceY(g8,g8) = 3.7
    c: Equal(g5,g8)
    c: DistanceY(g4,g0) = 14.6
    c: Coincident(g14,g2)
    c: Coincident(g10,g15)
    c: Horizontal(g10)
    c: Coincident(g11,g10)
    c: Vertical(g11)
    c: Coincident(g0,g4)
    c: PointOnObject(g12,g6)
    c: Coincident(g2,g7)
    c: PointOnObject(g13,g9)
    c: Coincident(g1,g11)
    c: Vertical(g12)
    c: Vertical(g13)
    c: DistanceX(g1,g2) = 24
    c: Equal(g4,g9)
    c: Coincident(g14,g15)
    c: Vertical(g15)
    c: Horizontal(g14)
    c: DistanceY(g10,g3) = 32.5
    c: DistanceX(g10,g10) = 30
    c: DistanceY(g1,g0) = 24.5
    c: PointOnObject(g16,g19)
    c: Vertical(g16)
    c: Coincident(g16,g17)
    c: Horizontal(g17)
    c: Coincident(g17,g18)
    c: Vertical(g18)
    c: DistanceX(g17,g17) = 5
    c: DistanceX(g17,g3) = 1.4
    c: Coincident(g3,g18)
    c: PointOnObject(g19,g16)
FEATURE [PartDesign::Pocket] Pocket120
  BaseFeature = -> Pocket119
  Direction = (0,1,0)
  Length = 46
  Length2 = 5
  Profile = -> Sketch180
  ReferenceAxis = -> Sketch180 [N_Axis]
  Refine = true
  Reversed = true
  Suppressed = false
  Type = 0
FEATURE [PartDesign::Body] Body026
  AllowCompound = false
  Group = -> [Sketch176,Sketch175,AdditiveLoft024,Sketch177,Pocket117,Sketch178,Pocket118,DatumPlane039,Sketch179,Pocket119,Sketch180,Pocket120]
  Origin = -> Origin026
  Placement = pos=(0,0,-100) rot=(0,0,1;0rad)
  Tip = -> Pocket120
FEATURE [Part::Mirroring] Part__Mirroring024  label="Body026 (Mirror #25)"
  Base = (0,0,0)
  Normal = (0,0,1)
  Source = -> Body026
FEATURE [Sketcher::SketchObject] Sketch181
  ArcFitTolerance = 1e-06
  AttachmentSupport = -> [Pocket043]
  FullyConstrained = true
  MakeInternals = false
  MapMode = 5
  Placement = pos=(0,0,-100) rot=(0,0,1;0rad)
  sketch-geometry (1):
    g0: Circle CenterX=310 CenterY=12 CenterZ=0 NormalX=0 NormalY=0 NormalZ=1 AngleXU=0 Radius=4.1
  constraints (3):
    c: Diameter(g0) = 8.2
    c: DistanceY(g-1,g0) = 12
    c: DistanceX(g-1,g0) = 310
FEATURE [PartDesign::Pocket] Pocket121
  BaseFeature = -> Pocket043
  Direction = (0,0,-1)
  Length = 15
  Length2 = 5
  Profile = -> Sketch181
  ReferenceAxis = -> Sketch181 [N_Axis]
  Refine = true
  Suppressed = false
  Type = 0
FEATURE [PartDesign::Body] Body001
  AllowCompound = false
  Group = -> [Sketch004,Sketch003,AdditiveLoft001,DatumPlane001,Sketch005,Pocket001,Sketch022,Pocket008,Sketch023,Pocket009,Sketch062,Pocket037,Sketch069,Pocket043,Sketch181,Pocket121]
  Origin = -> Origin001
  Placement = pos=(0,0,-100) rot=(0,0,1;0rad)
  Tip = -> Pocket121
FEATURE [Part::Mirroring] Part__Mirroring001  label="Body001 (Mirror #2)"
  Base = (0,0,0)
  Normal = (0,0,1)
  Source = -> Body001
FEATURE [Sketcher::SketchObject] Sketch182
  ArcFitTolerance = 1e-06
  FullyConstrained = true
  MakeInternals = false
  MapMode = 5
  Placement = pos=(0,2.2e-15,10) rot=(0,0,1;0rad)
  sketch-geometry (1):
    g0: Circle CenterX=310 CenterY=12 CenterZ=0 NormalX=0 NormalY=0 NormalZ=1 AngleXU=0 Radius=4.1
  constraints (3):
    c: Diameter(g0) = 8.2
    c: DistanceY(g-1,g0) = 12
    c: DistanceX(g-1,g0) = 310
FEATURE [PartDesign::Plane] DatumPlane041
  AttachmentOffset = pos=(0,0,-50) rot=(0,0,1;0rad)
  AttachmentSupport = -> [XZ_Plane025]
  Length = 531.958
  MapMode = 5
  Placement = pos=(0,50,-1.11e-14) rot=(1,0,0;1.5708rad)
  ResizeMode = 0
  Width = 289.839
FEATURE [PartDesign::Plane] DatumPlane042
  AttachmentOffset = pos=(0,0,-50) rot=(0,0,1;0rad)
  AttachmentSupport = -> [XZ_Plane027]
  Length = 341.088
  MapMode = 5
  Placement = pos=(0,50,-1.11e-14) rot=(1,0,0;1.5708rad)
  ResizeMode = 0
  Width = 276.088
FEATURE [Sketcher::SketchObject] Sketch183
  ArcFitTolerance = 1e-06
  FullyConstrained = false
  MakeInternals = false
  sketch-geometry (123):
    g0: BSplineCurve PolesCount=61 KnotsCount=61 Degree=3 IsPeriodic=1
    g1-g61: Circle [constr] x61 (B-spline internal-alignment scaffolding for g0; pole/knot coordinates omitted)
    g62-g122: GeomPoint [constr] x61 (B-spline internal-alignment scaffolding for g0; pole/knot coordinates omitted)
  constraints (123):
    c: InternalAlignment(g1,g0)
    c: Weight(g1) = 1
    c: InternalAlignment(g2,g0)
    c: Equal(g2,g1)
    c: InternalAlignment(g3,g0)
    c: Equal(g3,g1)
    c: InternalAlignment(g4,g0)
    c: Equal(g4,g1)
    c: InternalAlignment(g5,g0)
    c: Equal(g5,g1)
    c: InternalAlignment(g6,g0)
    c: Equal(g6,g1)
    c: InternalAlignment(g7,g0)
    c: Equal(g7,g1)
    c: InternalAlignment(g8,g0)
    c: Equal(g8,g1)
    c: InternalAlignment(g9,g0)
    c: Equal(g9,g1)
    c: InternalAlignment(g10,g0)
    c: Equal(g10,g1)
    c: InternalAlignment(g11,g0)
    c: Equal(g11,g1)
    c: InternalAlignment(g12,g0)
    c: Equal(g12,g1)
    c: InternalAlignment(g13,g0)
    c: Equal(g13,g1)
    c: InternalAlignment(g14,g0)
    c: Equal(g14,g1)
    c: InternalAlignment(g15,g0)
    c: Equal(g15,g1)
    c: InternalAlignment(g16,g0)
    c: Equal(g16,g1)
    c: InternalAlignment(g17,g0)
    c: Equal(g17,g1)
    c: InternalAlignment(g18,g0)
    c: Equal(g18,g1)
    c: InternalAlignment(g19,g0)
    c: Equal(g19,g1)
    c: InternalAlignment(g20,g0)
    c: Equal(g20,g1)
    c: InternalAlignment(g21,g0)
    c: Equal(g21,g1)
    c: InternalAlignment(g22,g0)
    c: Equal(g22,g1)
    c: InternalAlignment(g23,g0)
    c: Equal(g23,g1)
    c: InternalAlignment(g24,g0)
    c: Equal(g24,g1)
    c: InternalAlignment(g25,g0)
    c: Equal(g25,g1)
    c: InternalAlignment(g26,g0)
    c: Equal(g26,g1)
    c: InternalAlignment(g27,g0)
    c: Equal(g27,g1)
    c: InternalAlignment(g28,g0)
    c: Equal(g28,g1)
    c: InternalAlignment(g29,g0)
    c: Equal(g29,g1)
    c: InternalAlignment(g30,g0)
    c: Equal(g30,g1)
    c: InternalAlignment(g31,g0)
    c: Equal(g31,g1)
    c: InternalAlignment(g32,g0)
    c: Equal(g32,g1)
    c: InternalAlignment(g33,g0)
    c: Equal(g33,g1)
    c: InternalAlignment(g34,g0)
    c: Equal(g34,g1)
    c: InternalAlignment(g35,g0)
    c: Equal(g35,g1)
    c: InternalAlignment(g36,g0)
    c: Equal(g36,g1)
    c: InternalAlignment(g37,g0)
    c: Equal(g37,g1)
    c: InternalAlignment(g38,g0)
    c: Equal(g38,g1)
    c: InternalAlignment(g39,g0)
    c: Equal(g39,g1)
    c: InternalAlignment(g40,g0)
    c: Equal(g40,g1)
    c: InternalAlignment(g41,g0)
    c: Equal(g41,g1)
    c: InternalAlignment(g42,g0)
    c: Equal(g42,g1)
    c: InternalAlignment(g43,g0)
    c: Equal(g43,g1)
    c: InternalAlignment(g44,g0)
    c: Equal(g44,g1)
    c: InternalAlignment(g45,g0)
    c: Equal(g45,g1)
    c: InternalAlignment(g46,g0)
    c: Equal(g46,g1)
    c: InternalAlignment(g47,g0)
    c: Equal(g47,g1)
    c: InternalAlignment(g48,g0)
    c: Equal(g48,g1)
    c: InternalAlignment(g49,g0)
    c: Equal(g49,g1)
    c: InternalAlignment(g50,g0)
    c: Equal(g50,g1)
    c: InternalAlignment(g51,g0)
    c: Equal(g51,g1)
    c: InternalAlignment(g52,g0)
    c: Equal(g52,g1)
    c: InternalAlignment(g53,g0)
    c: Equal(g53,g1)
    c: InternalAlignment(g54,g0)
    c: Equal(g54,g1)
    c: InternalAlignment(g55,g0)
    c: Equal(g55,g1)
    c: InternalAlignment(g56,g0)
    c: Equal(g56,g1)
    c: InternalAlignment(g57,g0)
    c: Equal(g57,g1)
    c: InternalAlignment(g58,g0)
    c: Equal(g58,g1)
    c: InternalAlignment(g59,g0)
    c: Equal(g59,g1)
    c: InternalAlignment(g60,g0)
    c: Equal(g60,g1)
    c: InternalAlignment(g61,g0)
    c: Equal(g61,g1)
    c: InternalAlignment(g62-g122 -> g0) x61
FEATURE [PartDesign::Pad] Pad009
  Direction = (0,0,1)
  Length = 200
  Length2 = 10
  Profile = -> Sketch183
  ReferenceAxis = -> Sketch183 [N_Axis]
  Refine = true
  Suppressed = false
  Type = 0
FEATURE [Sketcher::SketchObject] Sketch184
  ArcFitTolerance = 1e-06
  AttachmentSupport = -> [DatumPlane042]
  FullyConstrained = false
  MakeInternals = false
  MapMode = 5
  Placement = pos=(0,50,-1.11e-14) rot=(1,0,0;1.5708rad)
  sketch-geometry (22):
    g0: LineSegment StartX=15 StartY=190 StartZ=0 EndX=15 EndY=10 EndZ=0
    g1: LineSegment StartX=20.8485 StartY=190 StartZ=0 EndX=20.8485 EndY=10 EndZ=0
    g2: LineSegment StartX=85.8485 StartY=190 StartZ=0 EndX=85.8485 EndY=10 EndZ=0
    g3: LineSegment StartX=20.8485 StartY=190 StartZ=0 EndX=15 EndY=190 EndZ=0
    g4: LineSegment StartX=15 StartY=10 StartZ=0 EndX=20.8485 EndY=10 EndZ=0
    g5: LineSegment [constr] StartX=20.8485 StartY=190 StartZ=0 EndX=85.8485 EndY=190 EndZ=0
    g6: LineSegment [constr] StartX=20.8485 StartY=10 StartZ=0 EndX=85.8485 EndY=10 EndZ=0
    g7: LineSegment StartX=85.8485 StartY=190 StartZ=0 EndX=143.07 EndY=190 EndZ=0
    g8: LineSegment StartX=143.07 StartY=190 StartZ=0 EndX=143.07 EndY=10 EndZ=0
    g9: LineSegment StartX=143.07 StartY=10 StartZ=0 EndX=85.8485 EndY=10 EndZ=0
    g10: LineSegment [constr] StartX=143.07 StartY=190 StartZ=0 EndX=153.07 EndY=190 EndZ=0
    g11: LineSegment [constr] StartX=143.07 StartY=10 StartZ=0 EndX=153.07 EndY=10 EndZ=0
    g12: LineSegment StartX=153.07 StartY=190 StartZ=0 EndX=153.07 EndY=10 EndZ=0
    g13: LineSegment StartX=153.07 StartY=10 StartZ=0 EndX=250.656 EndY=10 EndZ=0
    g14: LineSegment StartX=250.656 StartY=10 StartZ=0 EndX=250.656 EndY=190 EndZ=0
    g15: LineSegment StartX=250.656 StartY=190 StartZ=0 EndX=153.07 EndY=190 EndZ=0
    g16: LineSegment [constr] StartX=250.656 StartY=190 StartZ=0 EndX=260.656 EndY=190 EndZ=0
    g17: LineSegment [constr] StartX=250.656 StartY=10 StartZ=0 EndX=260.656 EndY=10 EndZ=0
    g18: LineSegment StartX=260.656 StartY=190 StartZ=0 EndX=260.656 EndY=10 EndZ=0
    g19: LineSegment StartX=260.656 StartY=10 StartZ=0 EndX=363.152 EndY=10 EndZ=0
    g20: LineSegment StartX=363.152 StartY=10 StartZ=0 EndX=363.152 EndY=190 EndZ=0
    g21: LineSegment StartX=363.152 StartY=190 StartZ=0 EndX=260.656 EndY=190 EndZ=0
  constraints (60):
    c: Coincident(g3,g0)
    c: Vertical(g0)
    c: DistanceY(g-1,g0) = 10
    c: DistanceY(g0,g0) = 180
    c: DistanceX(g-1,g0) = 15
    c: Vertical(g1)
    c: Vertical(g2)
    c: DistanceX(g1,g2) = 65
    c: Coincident(g4,g0)
    c: Coincident(g4,g1)
    c: Horizontal(g4)
    c: Horizontal(g5)
    c: Coincident(g6,g1)
    c: Coincident(g6,g2)
    c: Horizontal(g6)
    c: Coincident(g5,g1)
    c: Block(g1)
    c: Block(g3)
    c: Block(g0)
    c: Block(g4)
    c: Block(g2)
    c: Block(g5)
    c: Block(g6)
    c: Coincident(g2,g7)
    c: Horizontal(g7)
    c: Coincident(g7,g8)
    c: Vertical(g8)
    c: Coincident(g8,g9)
    c: Coincident(g9,g2)
    c: Horizontal(g9)
    c: Coincident(g10,g7)
    c: Horizontal(g10)
    c: Coincident(g11,g8)
    c: Horizontal(g11)
    c: Equal(g11,g10)
    c: DistanceX(g10,g10) = 10
    c: Coincident(g12,g13)
    c: Coincident(g13,g14)
    c: Coincident(g14,g15)
    c: Coincident(g15,g12)
    c: Vertical(g14)
    c: Horizontal(g13)
    c: Horizontal(g15)
    c: Coincident(g12,g10)
    c: Coincident(g12,g11)
    c: Coincident(g16,g14)
    c: Horizontal(g16)
    c: Coincident(g17,g13)
    c: Horizontal(g17)
    c: Equal(g16,g17)
    c: DistanceX(g16,g16) = 10
    c: Coincident(g18,g19)
    c: Coincident(g19,g20)
    c: Coincident(g20,g21)
    c: Coincident(g21,g18)
    c: Vertical(g20)
    c: Horizontal(g19)
    c: Horizontal(g21)
    c: Coincident(g18,g16)
    c: Coincident(g18,g17)
FEATURE [PartDesign::Pocket] Pocket123
  BaseFeature = -> Pad009
  Direction = (0,1,-2e-16)
  Length = 100
  Length2 = 5
  Profile = -> Sketch184
  ReferenceAxis = -> Sketch184 [N_Axis]
  Refine = true
  Reversed = true
  Suppressed = false
  Type = 0
FEATURE [Sketcher::SketchObject] Sketch186
  ArcFitTolerance = 1e-06
  AttachmentSupport = -> [DatumPlane041]
  FullyConstrained = false
  MakeInternals = false
  MapMode = 5
  Placement = pos=(0,50,-1.11e-14) rot=(1,0,0;1.5708rad)
  sketch-geometry (4):
    g0: LineSegment StartX=-39.3315 StartY=271.097 StartZ=0 EndX=-39.3315 EndY=-37.2702 EndZ=0
    g1: LineSegment StartX=-39.3315 StartY=-37.2702 StartZ=0 EndX=265 EndY=-37.2702 EndZ=0
    g2: LineSegment StartX=265 StartY=-37.2702 StartZ=0 EndX=265 EndY=271.097 EndZ=0
    g3: LineSegment StartX=265 StartY=271.097 StartZ=0 EndX=-39.3315 EndY=271.097 EndZ=0
  constraints (9):
    c: Coincident(g0,g1)
    c: Coincident(g1,g2)
    c: Coincident(g2,g3)
    c: Coincident(g3,g0)
    c: Vertical(g0)
    c: Vertical(g2)
    c: Horizontal(g1)
    c: Horizontal(g3)
    c: Distance(g-1,g2) = 265
FEATURE [Sketcher::SketchObject] Sketch185
  ArcFitTolerance = 1e-06
  AttachmentSupport = -> [Pocket123]
  FullyConstrained = true
  MakeInternals = false
  MapMode = 5
  Placement = pos=(0,2.2e-15,10) rot=(0,0,1;0rad)
  sketch-geometry (4):
    g0: Circle CenterX=100 CenterY=4 CenterZ=0 NormalX=0 NormalY=0 NormalZ=1 AngleXU=0 Radius=4.1
    g1: Circle CenterX=170 CenterY=17 CenterZ=0 NormalX=0 NormalY=0 NormalZ=1 AngleXU=0 Radius=4.1
    g2: Circle CenterX=240 CenterY=5 CenterZ=0 NormalX=0 NormalY=0 NormalZ=1 AngleXU=0 Radius=4.1
    g3: Circle CenterX=310 CenterY=12 CenterZ=0 NormalX=0 NormalY=0 NormalZ=1 AngleXU=0 Radius=4.1
  constraints (12):
    c: Diameter(g0) = 8.2
    c: Diameter(g1) = 8.2
    c: Diameter(g2) = 8.2
    c: Diameter(g3) = 8.2
    c: DistanceX(g-1,g0) = 100
    c: DistanceY(g-1,g0) = 4
    c: DistanceX(g0,g1) = 70
    c: DistanceX(g1,g2) = 70
    c: DistanceX(g2,g3) = 70
    c: DistanceY(g-1,g1) = 17
    c: DistanceY(g-1,g2) = 5
    c: DistanceY(g-1,g3) = 12
FEATURE [Sketcher::SketchObject] Sketch188
  ArcFitTolerance = 1e-06
  AttachmentSupport = -> [DatumPlane042]
  FullyConstrained = false
  MakeInternals = false
  MapMode = 5
  Placement = pos=(0,50,-1.11e-14) rot=(1,0,0;1.5708rad)
  sketch-geometry (4):
    g0: LineSegment StartX=18.8003 StartY=10 StartZ=0 EndX=90.9393 EndY=10 EndZ=0
    g1: LineSegment StartX=90.9393 StartY=10 StartZ=0 EndX=90.9393 EndY=190 EndZ=0
    g2: LineSegment StartX=90.9393 StartY=190 StartZ=0 EndX=18.8003 EndY=190 EndZ=0
    g3: LineSegment StartX=18.8003 StartY=190 StartZ=0 EndX=18.8003 EndY=10 EndZ=0
  constraints (10):
    c: Coincident(g0,g1)
    c: Coincident(g1,g2)
    c: Coincident(g2,g3)
    c: Coincident(g3,g0)
    c: Horizontal(g0)
    c: Horizontal(g2)
    c: Vertical(g1)
    c: Vertical(g3)
    c: DistanceY(g3,g3) = 180
    c: DistanceY(g-1,g0) = 10
FEATURE [PartDesign::Pocket] Pocket124
  BaseFeature = -> Pocket123
  Direction = (0,0,-1)
  Length = 500
  Length2 = 5
  Midplane = true
  Profile = -> Sketch185
  ReferenceAxis = -> Sketch185 [N_Axis]
  Refine = true
  Suppressed = false
  Type = 0
FEATURE [PartDesign::Plane] DatumPlane043
  AttachmentOffset = pos=(0,0,-50) rot=(0,0,1;0rad)
  AttachmentSupport = -> [XZ_Plane027]
  Length = 341.088
  MapMode = 5
  Placement = pos=(0,50,-1.11e-14) rot=(1,0,0;1.5708rad)
  ResizeMode = 0
  Width = 276.088
FEATURE [Sketcher::SketchObject] Sketch187
  ArcFitTolerance = 1e-06
  AttachmentSupport = -> [DatumPlane043]
  FullyConstrained = false
  MakeInternals = false
  MapMode = 5
  Placement = pos=(0,50,-1.11e-14) rot=(1,0,0;1.5708rad)
  sketch-geometry (4):
    g0: LineSegment StartX=265 StartY=235.121 StartZ=0 EndX=265 EndY=-60.4994 EndZ=0
    g1: LineSegment StartX=265 StartY=-60.4994 StartZ=0 EndX=525.816 EndY=-60.4994 EndZ=0
    g2: LineSegment StartX=525.816 StartY=-60.4994 StartZ=0 EndX=525.816 EndY=235.121 EndZ=0
    g3: LineSegment StartX=525.816 StartY=235.121 StartZ=0 EndX=265 EndY=235.121 EndZ=0
  constraints (9):
    c: Coincident(g0,g1)
    c: Coincident(g1,g2)
    c: Coincident(g2,g3)
    c: Coincident(g3,g0)
    c: Vertical(g0)
    c: Vertical(g2)
    c: Horizontal(g1)
    c: Horizontal(g3)
    c: Distance(g-1,g0) = 265
FEATURE [PartDesign::Pocket] Pocket126
  BaseFeature = -> Pocket124
  Direction = (0,1,-2e-16)
  Length = 200
  Length2 = 5
  Profile = -> Sketch187
  ReferenceAxis = -> Sketch187 [N_Axis]
  Refine = true
  Reversed = true
  Suppressed = false
  Type = 0
FEATURE [PartDesign::Pocket] Pocket127
  BaseFeature = -> Pocket126
  Direction = (0,1,-2e-16)
  Length = 55
  Length2 = 5
  Profile = -> Sketch188
  ReferenceAxis = -> Sketch188 [N_Axis]
  Refine = true
  Reversed = true
  Suppressed = false
  Type = 0
FEATURE [Sketcher::SketchObject] Sketch189
  ArcFitTolerance = 1e-06
  AttachmentSupport = -> [Pocket127]
  FullyConstrained = false
  MakeInternals = false
  MapMode = 5
  Placement = pos=(153.07,0,0) rot=(0.57735,0.57735,0.57735;2.0944rad)
  sketch-geometry (4):
    g0: LineSegment StartX=-2.90898 StartY=190 StartZ=0 EndX=-2.90898 EndY=10 EndZ=0
    g1: LineSegment StartX=-2.90898 StartY=10 StartZ=0 EndX=29.2582 EndY=10 EndZ=0
    g2: LineSegment StartX=29.2582 StartY=10 StartZ=0 EndX=29.2582 EndY=190 EndZ=0
    g3: LineSegment StartX=29.2582 StartY=190 StartZ=0 EndX=-2.90898 EndY=190 EndZ=0
  constraints (10):
    c: Coincident(g0,g1)
    c: Coincident(g1,g2)
    c: Coincident(g2,g3)
    c: Coincident(g3,g0)
    c: Vertical(g0)
    c: Vertical(g2)
    c: Horizontal(g1)
    c: Horizontal(g3)
    c: DistanceY(g-1,g1) = 10
    c: DistanceY(g2,g2) = 180
FEATURE [PartDesign::Pocket] Pocket128
  BaseFeature = -> Pocket127
  Direction = (-1,0,0)
  Length = 15
  Length2 = 5
  Profile = -> Sketch189
  ReferenceAxis = -> Sketch189 [N_Axis]
  Refine = true
  Suppressed = false
  Type = 0
FEATURE [Sketcher::SketchObject] Sketch190
  ArcFitTolerance = 1e-06
  AttachmentSupport = -> [Pocket128]
  FullyConstrained = false
  MakeInternals = false
  MapMode = 5
  Placement = pos=(260.656,0,0) rot=(0.57735,0.57735,0.57735;2.0944rad)
  sketch-geometry (4):
    g0: LineSegment StartX=0.73189 StartY=190 StartZ=0 EndX=0.73189 EndY=10 EndZ=0
    g1: LineSegment StartX=0.73189 StartY=10 StartZ=0 EndX=23.6206 EndY=10 EndZ=0
    g2: LineSegment StartX=23.6206 StartY=10 StartZ=0 EndX=23.6206 EndY=190 EndZ=0
    g3: LineSegment StartX=23.6206 StartY=190 StartZ=0 EndX=0.73189 EndY=190 EndZ=0
  constraints (10):
    c: Coincident(g0,g1)
    c: Coincident(g1,g2)
    c: Coincident(g2,g3)
    c: Coincident(g3,g0)
    c: Vertical(g0)
    c: Vertical(g2)
    c: Horizontal(g1)
    c: Horizontal(g3)
    c: DistanceY(g-1,g1) = 10
    c: DistanceY(g2,g2) = 180
FEATURE [PartDesign::Pocket] Pocket129
  BaseFeature = -> Pocket128
  Direction = (-1,0,0)
  Length = 15
  Length2 = 5
  Profile = -> Sketch190
  ReferenceAxis = -> Sketch190 [N_Axis]
  Refine = true
  Suppressed = false
  Type = 0
FEATURE [Sketcher::SketchObject] Sketch191
  ArcFitTolerance = 1e-06
  AttachmentSupport = -> [Pocket129]
  FullyConstrained = false
  MakeInternals = false
  MapMode = 5
  Placement = pos=(0,-5,1.2e-15) rot=(0,0.707107,0.707107;3.14159rad)
  sketch-geometry (5):
    g0: Circle CenterX=-81.422 CenterY=125 CenterZ=0 NormalX=0 NormalY=0 NormalZ=1 AngleXU=0 Radius=1.55
    g1: Circle CenterX=-31.422 CenterY=125 CenterZ=0 NormalX=0 NormalY=0 NormalZ=1 AngleXU=0 Radius=1.55
    g2: Circle CenterX=-81.422 CenterY=75 CenterZ=0 NormalX=0 NormalY=0 NormalZ=1 AngleXU=0 Radius=1.55
    g3: Circle CenterX=-31.422 CenterY=75 CenterZ=0 NormalX=0 NormalY=0 NormalZ=1 AngleXU=0 Radius=1.55
    g4: LineSegment [constr] StartX=-100.519 StartY=100 StartZ=0 EndX=-14.7137 EndY=100 EndZ=0
  constraints (11):
    c: Horizontal(g4)
    c: DistanceY(g-1,g4) = 100
    c: Diameter(g3) = 3.1
    c: Diameter(g2) = 3.1
    c: Diameter(g1) = 3.1
    c: Diameter(g0) = 3.1
    c: Symmetric(g0,g2,g4)
    c: Symmetric(g1,g3,g4)
    c: DistanceY(g3,g1) = 50
    c: DistanceX(g0,g1) = 50
    c: DistanceY(g2,g0) = 50
FEATURE [PartDesign::Pocket] Pocket130
  BaseFeature = -> Pocket129
  Direction = (0,-1,2e-16)
  Length = 20
  Length2 = 5
  Profile = -> Sketch191
  ReferenceAxis = -> Sketch191 [N_Axis]
  Refine = true
  Suppressed = false
  Type = 0
FEATURE [Sketcher::SketchObject] Sketch192
  ArcFitTolerance = 1e-06
  FullyConstrained = true
  MakeInternals = false
  MapMode = 5
  Placement = pos=(0,0,10) rot=(0,0,1;0rad)
  sketch-geometry (4):
    g0: LineSegment StartX=120 StartY=11 StartZ=0 EndX=120 EndY=5 EndZ=0
    g1: LineSegment StartX=120 StartY=5 StartZ=0 EndX=133 EndY=5 EndZ=0
    g2: LineSegment StartX=133 StartY=5 StartZ=0 EndX=133 EndY=11 EndZ=0
    g3: LineSegment StartX=133 StartY=11 StartZ=0 EndX=120 EndY=11 EndZ=0
  constraints (12):
    c: Coincident(g0,g1)
    c: Coincident(g1,g2)
    c: Coincident(g2,g3)
    c: Coincident(g3,g0)
    c: Vertical(g0)
    c: Vertical(g2)
    c: Horizontal(g1)
    c: Horizontal(g3)
    c: DistanceX(g3,g3) = 13
    c: DistanceY(g2,g2) = 6
    c: DistanceX(g-1,g0) = 120
    c: DistanceY(g-1,g0) = 5
FEATURE [PartDesign::Pocket] Pocket131
  BaseFeature = -> Pocket130
  Direction = (0,0,-1)
  Length = 500
  Length2 = 5
  Midplane = true
  Profile = -> Sketch192
  ReferenceAxis = -> Sketch192 [N_Axis]
  Refine = true
  Suppressed = false
  Type = 0
FEATURE [Sketcher::SketchObject] Sketch193
  ArcFitTolerance = 1e-06
  AttachmentSupport = -> [Pocket049]
  FullyConstrained = true
  MakeInternals = false
  MapMode = 5
  sketch-geometry (4):
    g0: LineSegment StartX=120 StartY=11 StartZ=0 EndX=120 EndY=5 EndZ=0
    g1: LineSegment StartX=120 StartY=5 StartZ=0 EndX=133 EndY=5 EndZ=0
    g2: LineSegment StartX=133 StartY=5 StartZ=0 EndX=133 EndY=11 EndZ=0
    g3: LineSegment StartX=133 StartY=11 StartZ=0 EndX=120 EndY=11 EndZ=0
  constraints (12):
    c: Coincident(g0,g1)
    c: Coincident(g1,g2)
    c: Coincident(g2,g3)
    c: Coincident(g3,g0)
    c: Vertical(g0)
    c: Vertical(g2)
    c: Horizontal(g1)
    c: Horizontal(g3)
    c: DistanceX(g3,g3) = 13
    c: DistanceY(g2,g2) = 6
    c: DistanceY(g-1,g0) = 5
    c: DistanceX(g-1,g0) = 120
FEATURE [PartDesign::Pocket] Pocket132
  BaseFeature = -> Pocket049
  Direction = (0,0,-1)
  Length = 20
  Length2 = 5
  Profile = -> Sketch193
  ReferenceAxis = -> Sketch193 [N_Axis]
  Refine = true
  Suppressed = false
  Type = 0
FEATURE [PartDesign::Body] Body010
  AllowCompound = false
  Group = -> [Sketch074,Sketch073,AdditiveLoft010,DatumPlane013,Sketch075,Pocket045,Sketch076,Pocket046,Sketch077,Pocket047,Sketch078,Pocket049,Sketch193,Pocket132]
  Origin = -> Origin010
  Placement = pos=(0,0,-100) rot=(0,0,1;0rad)
  Tip = -> Pocket132
FEATURE [Part::Mirroring] Part__Mirroring006  label="Body010 (Mirror #7)"
  Base = (0,0,0)
  Normal = (0,0,1)
  Source = -> Body010
FEATURE [PartDesign::Plane] DatumPlane045
  AttachmentOffset = pos=(0,0,340) rot=(0,0,1;0rad)
  AttachmentSupport = -> [YZ_Plane029]
  Length = 64.0665
  MapMode = 5
  Placement = pos=(340,0,0) rot=(0.57735,0.57735,0.57735;2.0944rad)
  ResizeMode = 0
  Width = 82.0665
FEATURE [PartDesign::Plane] DatumPlane046
  AttachmentOffset = pos=(0,0,430) rot=(0,0,1;0rad)
  AttachmentSupport = -> [YZ_Plane029]
  Length = 64.0665
  MapMode = 5
  Placement = pos=(430,0,0) rot=(0.57735,0.57735,0.57735;2.0944rad)
  ResizeMode = 0
  Width = 82.0665
FEATURE [Sketcher::SketchObject] Sketch198
  ArcFitTolerance = 1e-06
  AttachmentSupport = -> [DatumPlane045]
  FullyConstrained = true
  MakeInternals = false
  MapMode = 5
  Placement = pos=(340,0,0) rot=(0.57735,0.57735,0.57735;2.0944rad)
  sketch-geometry (4):
    g0: LineSegment StartX=20.6 StartY=30 StartZ=0 EndX=-3 EndY=30 EndZ=0
    g1: LineSegment StartX=-3 StartY=30 StartZ=0 EndX=-3 EndY=-30 EndZ=0
    g2: LineSegment StartX=-3 StartY=-30 StartZ=0 EndX=20.6 EndY=-30 EndZ=0
    g3: LineSegment StartX=20.6 StartY=-30 StartZ=0 EndX=20.6 EndY=30 EndZ=0
  constraints (11):
    c: Coincident(g0,g1)
    c: Coincident(g1,g2)
    c: Coincident(g2,g3)
    c: Coincident(g3,g0)
    c: Horizontal(g0)
    c: Horizontal(g2)
    c: Vertical(g1)
    c: Symmetric(g0,g2,g-1)
    c: DistanceY(g3,g3) = 60
    c: DistanceX(g-1,g2) = 20.6
    c: DistanceX(g1,g-1) = 3
FEATURE [PartDesign::Plane] DatumPlane047
  AttachmentOffset = pos=(0,0,400) rot=(0,0,1;0rad)
  AttachmentSupport = -> [YZ_Plane029]
  Length = 64.0665
  MapMode = 5
  Placement = pos=(400,0,0) rot=(0.57735,0.57735,0.57735;2.0944rad)
  ResizeMode = 0
  Width = 82.0665
FEATURE [Sketcher::SketchObject] Sketch199
  ArcFitTolerance = 1e-06
  AttachmentSupport = -> [DatumPlane047]
  FullyConstrained = true
  MakeInternals = false
  MapMode = 5
  Placement = pos=(400,0,0) rot=(0.57735,0.57735,0.57735;2.0944rad)
  sketch-geometry (4):
    g0: LineSegment StartX=10.35 StartY=35 StartZ=0 EndX=-2.1 EndY=35 EndZ=0
    g1: LineSegment StartX=-2.1 StartY=35 StartZ=0 EndX=-2.1 EndY=-35 EndZ=0
    g2: LineSegment StartX=-2.1 StartY=-35 StartZ=0 EndX=10.35 EndY=-35 EndZ=0
    g3: LineSegment StartX=10.35 StartY=-35 StartZ=0 EndX=10.35 EndY=35 EndZ=0
  constraints (11):
    c: Coincident(g0,g1)
    c: Coincident(g1,g2)
    c: Coincident(g2,g3)
    c: Coincident(g3,g0)
    c: Horizontal(g0)
    c: Horizontal(g2)
    c: Vertical(g1)
    c: Symmetric(g0,g2,g-1)
    c: DistanceY(g3,g3) = 70
    c: DistanceX(g-1,g2) = 10.35
    c: DistanceX(g1,g-1) = 2.1
FEATURE [PartDesign::AdditiveLoft] AdditiveLoft025
  Closed = false
  Placement = pos=(340,0,0) rot=(0.57735,0.57735,0.57735;2.0944rad)
  Profile = -> Sketch198
  Refine = true
  Ruled = false
  Sections = -> [Sketch199]
  Suppressed = false
FEATURE [Sketcher::SketchObject] Sketch200
  ArcFitTolerance = 1e-06
  AttachmentSupport = -> [DatumPlane046]
  FullyConstrained = true
  MakeInternals = false
  MapMode = 5
  Placement = pos=(430,0,0) rot=(0.57735,0.57735,0.57735;2.0944rad)
  sketch-geometry (36):
    g0: LineSegment StartX=5 StartY=22 StartZ=0 EndX=5 EndY=8 EndZ=0
    g1: LineSegment StartX=8 StartY=5 StartZ=0 EndX=22 EndY=5 EndZ=0
    g2: LineSegment StartX=26 StartY=1 StartZ=0 EndX=26 EndY=-1 EndZ=0
    g3: LineSegment StartX=22 StartY=-5 StartZ=0 EndX=8 EndY=-5 EndZ=0
    g4: LineSegment StartX=5 StartY=-8 StartZ=0 EndX=5 EndY=-22 EndZ=0
    g5: LineSegment StartX=1 StartY=-26 StartZ=0 EndX=-1 EndY=-26 EndZ=0
    g6: LineSegment StartX=-5 StartY=-22 StartZ=0 EndX=-5 EndY=-8 EndZ=0
    g7: LineSegment StartX=-8 StartY=-5 StartZ=0 EndX=-22 EndY=-5 EndZ=0
    g8: LineSegment StartX=-26 StartY=-1 StartZ=0 EndX=-26 EndY=1 EndZ=0
    g9: LineSegment StartX=-22 StartY=5 StartZ=0 EndX=-8 EndY=5 EndZ=0
    g10: LineSegment StartX=-5 StartY=8 StartZ=0 EndX=-5 EndY=22 EndZ=0
    g11: LineSegment StartX=-1 StartY=26 StartZ=0 EndX=1 EndY=26 EndZ=0
    g12: ArcOfCircle CenterX=22 CenterY=1 CenterZ=0 NormalX=0 NormalY=0 NormalZ=1 AngleXU=0 Radius=4 StartAngle=0 EndAngle=1.5708
    g13: GeomPoint [constr] X=26 Y=5 Z=0
    g14: ArcOfCircle CenterX=22 CenterY=-1 CenterZ=0 NormalX=0 NormalY=0 NormalZ=1 AngleXU=0 Radius=4 StartAngle=4.71239 EndAngle=6.28319
    g15: GeomPoint [constr] X=26 Y=-5 Z=0
    g16: ArcOfCircle CenterX=8 CenterY=-8 CenterZ=0 NormalX=0 NormalY=0 NormalZ=1 AngleXU=0 Radius=3 StartAngle=1.5708 EndAngle=3.14159
    g17: GeomPoint [constr] X=5 Y=-5 Z=0
    g18: ArcOfCircle CenterX=1 CenterY=-22 CenterZ=0 NormalX=0 NormalY=0 NormalZ=1 AngleXU=0 Radius=4 StartAngle=4.71239 EndAngle=6.28319
    g19: GeomPoint [constr] X=5 Y=-26 Z=0
    g20: ArcOfCircle CenterX=-1 CenterY=-22 CenterZ=0 NormalX=0 NormalY=0 NormalZ=1 AngleXU=0 Radius=4 StartAngle=3.14159 EndAngle=4.71239
    g21: GeomPoint [constr] X=-5 Y=-26 Z=0
    g22: ArcOfCircle CenterX=-8 CenterY=-8 CenterZ=0 NormalX=0 NormalY=0 NormalZ=1 AngleXU=0 Radius=3 StartAngle=3e-16 EndAngle=1.5708
    g23: GeomPoint [constr] X=-5 Y=-5 Z=0
    g24: ArcOfCircle CenterX=-8 CenterY=8 CenterZ=0 NormalX=0 NormalY=0 NormalZ=1 AngleXU=0 Radius=3 StartAngle=4.71239 EndAngle=6.28319
    g25: GeomPoint [constr] X=-5 Y=5 Z=0
    g26: ArcOfCircle CenterX=8 CenterY=8 CenterZ=0 NormalX=0 NormalY=0 NormalZ=1 AngleXU=0 Radius=3 StartAngle=3.14159 EndAngle=4.71239
    g27: GeomPoint [constr] X=5 Y=5 Z=0
    g28: ArcOfCircle CenterX=1 CenterY=22 CenterZ=0 NormalX=0 NormalY=0 NormalZ=1 AngleXU=0 Radius=4 StartAngle=-9e-16 EndAngle=1.5708
    g29: GeomPoint [constr] X=5 Y=26 Z=0
    g30: ArcOfCircle CenterX=-1 CenterY=22 CenterZ=0 NormalX=0 NormalY=0 NormalZ=1 AngleXU=0 Radius=4 StartAngle=1.5708 EndAngle=3.14159
    g31: GeomPoint [constr] X=-5 Y=26 Z=0
    g32: ArcOfCircle CenterX=-22 CenterY=1 CenterZ=0 NormalX=0 NormalY=0 NormalZ=1 AngleXU=0 Radius=4 StartAngle=1.5708 EndAngle=3.14159
    g33: GeomPoint [constr] X=-26 Y=5 Z=0
    g34: ArcOfCircle CenterX=-22 CenterY=-1 CenterZ=0 NormalX=0 NormalY=0 NormalZ=1 AngleXU=0 Radius=4 StartAngle=3.14159 EndAngle=4.71239
    g35: GeomPoint [constr] X=-26 Y=-5 Z=0
  constraints (75):
    c: Symmetric(g35,g33,g-1)
    c: Symmetric(g31,g29,g-2)
    c: Symmetric(g25,g23,g-1)
    c: Symmetric(g23,g17,g-2)
    c: Symmetric(g21,g19,g-2)
    c: Symmetric(g13,g15,g-1)
    c: Symmetric(g27,g25,g-2)
    c: DistanceY(g35,g33) = 10
    c: DistanceY(g21,g31) = 52
    c: DistanceX(g33,g13) = 52
    c: Horizontal(g9)
    c: Vertical(g0)
    c: DistanceX(g21,g19) = 10
    c: Symmetric(g29,g19,g-1)
    c: Symmetric(g13,g33,g-2)
    c: PointOnObject(g13,g1)
    c: PointOnObject(g13,g2)
    c: Tangent(g1,g12) = 1.5708
    c: Tangent(g2,g12) = 1.5708
    c: PointOnObject(g15,g2)
    c: PointOnObject(g15,g3)
    c: Tangent(g2,g14) = 1.5708
    c: Tangent(g3,g14) = 1.5708
    c: PointOnObject(g17,g3)
    c: PointOnObject(g17,g4)
    c: Tangent(g3,g16) = -1.5708
    c: Tangent(g4,g16) = -1.5708
    c: PointOnObject(g19,g4)
    c: PointOnObject(g19,g5)
    c: Tangent(g4,g18) = 1.5708
    c: Tangent(g5,g18) = 1.5708
    c: PointOnObject(g21,g5)
    c: PointOnObject(g21,g6)
    c: Tangent(g5,g20) = 1.5708
    c: Tangent(g6,g20) = 1.5708
    c: PointOnObject(g23,g6)
    c: PointOnObject(g23,g7)
    c: Tangent(g6,g22) = -1.5708
    c: Tangent(g7,g22) = -1.5708
    c: PointOnObject(g25,g9)
    c: PointOnObject(g25,g10)
    c: Tangent(g9,g24) = -1.5708
    c: Tangent(g10,g24) = -1.5708
    c: PointOnObject(g27,g0)
    c: PointOnObject(g27,g1)
    c: Tangent(g0,g26) = -1.5708
    c: Tangent(g1,g26) = -1.5708
    c: PointOnObject(g29,g0)
    c: PointOnObject(g29,g11)
    c: Tangent(g0,g28) = 1.5708
    c: Tangent(g11,g28) = 1.5708
    c: PointOnObject(g31,g10)
    c: PointOnObject(g31,g11)
    c: Tangent(g10,g30) = 1.5708
    c: Tangent(g11,g30) = 1.5708
    c: PointOnObject(g33,g8)
    c: PointOnObject(g33,g9)
    c: Tangent(g8,g32) = 1.5708
    c: Tangent(g9,g32) = 1.5708
    c: PointOnObject(g35,g7)
    c: PointOnObject(g35,g8)
    c: Tangent(g7,g34) = 1.5708
    c: Tangent(g8,g34) = 1.5708
    c: Radius(g12) = 4
    c: Radius(g14) = 4
    c: Radius(g18) = 4
    c: Radius(g20) = 4
    c: Radius(g34) = 4
    c: Radius(g32) = 4
    c: Radius(g30) = 4
    c: Radius(g28) = 4
    c: Radius(g26) = 3
    c: Radius(g24) = 3
    c: Radius(g16) = 3
    c: Radius(g22) = 3
FEATURE [PartDesign::AdditiveLoft] AdditiveLoft026
  BaseFeature = -> AdditiveLoft025
  Closed = false
  Placement = pos=(340,0,0) rot=(0.57735,0.57735,0.57735;2.0944rad)
  Profile = -> Sketch199
  Refine = true
  Ruled = false
  Sections = -> [Sketch200]
  Suppressed = false
FEATURE [Sketcher::SketchObject] Sketch201
  ArcFitTolerance = 1e-06
  AttachmentSupport = -> [AdditiveLoft026]
  FullyConstrained = true
  MakeInternals = false
  MapMode = 5
  Placement = pos=(430,0,0) rot=(0.57735,0.57735,0.57735;2.0944rad)
  sketch-geometry (5):
    g0: Circle CenterX=0 CenterY=0 CenterZ=0 NormalX=0 NormalY=0 NormalZ=1 AngleXU=0 Radius=3.5
    g1: Circle CenterX=-21 CenterY=0 CenterZ=0 NormalX=0 NormalY=0 NormalZ=1 AngleXU=0 Radius=1.5
    g2: Circle CenterX=0 CenterY=21 CenterZ=0 NormalX=0 NormalY=0 NormalZ=1 AngleXU=0 Radius=1.5
    g3: Circle CenterX=21 CenterY=0 CenterZ=0 NormalX=0 NormalY=0 NormalZ=1 AngleXU=0 Radius=1.5
    g4: Circle CenterX=0 CenterY=-21 CenterZ=0 NormalX=0 NormalY=0 NormalZ=1 AngleXU=0 Radius=1.5
  constraints (12):
    c: Coincident(g0,g-1)
    c: Diameter(g0) = 7
    c: PointOnObject(g1,g-1)
    c: PointOnObject(g4,g-2)
    c: Diameter(g2) = 3
    c: Diameter(g3) = 3
    c: Diameter(g4) = 3
    c: Diameter(g1) = 3
    c: Symmetric(g1,g3,g-2)
    c: Symmetric(g2,g4,g0)
    c: DistanceX(g1,g3) = 42
    c: DistanceY(g4,g2) = 42
FEATURE [PartDesign::Pocket] Pocket134
  BaseFeature = -> AdditiveLoft026
  Direction = (-1,0,0)
  Length = 15
  Length2 = 5
  Placement = pos=(340,0,0) rot=(0.57735,0.57735,0.57735;2.0944rad)
  Profile = -> Sketch201
  ReferenceAxis = -> Sketch201 [N_Axis]
  Refine = true
  Suppressed = false
  Type = 0
FEATURE [Sketcher::SketchObject] Sketch202
  ArcFitTolerance = 1e-06
  FullyConstrained = false
  MakeInternals = false
  sketch-geometry (110):
    g0: BSplineCurve PolesCount=55 KnotsCount=53 Degree=3 IsPeriodic=0
    g1: LineSegment StartX=414.999 StartY=4.52571 StartZ=0 EndX=414.999 EndY=0.880232 EndZ=0
    g2-g56: Circle [constr] x55 (B-spline internal-alignment scaffolding for g0; pole/knot coordinates omitted)
    g57-g109: GeomPoint [constr] x53 (B-spline internal-alignment scaffolding for g0; pole/knot coordinates omitted)
  constraints (115):
    c: Vertical(g1)
    c: Distance(g1,g-1) = 415
    c: Coincident(g0,g1)
    c: Coincident(g0,g1)
    c: InternalAlignment(g2,g0)
    c: Weight(g2) = 1
    c: InternalAlignment(g3,g0)
    c: Equal(g3,g2)
    c: InternalAlignment(g4,g0)
    c: Equal(g4,g2)
    c: InternalAlignment(g5,g0)
    c: Equal(g5,g2)
    c: InternalAlignment(g6,g0)
    c: Equal(g6,g2)
    c: InternalAlignment(g7,g0)
    c: Equal(g7,g2)
    c: InternalAlignment(g8,g0)
    c: Equal(g8,g2)
    c: InternalAlignment(g9,g0)
    c: Equal(g9,g2)
    c: InternalAlignment(g10,g0)
    c: Equal(g10,g2)
    c: InternalAlignment(g11,g0)
    c: Equal(g11,g2)
    c: InternalAlignment(g12,g0)
    c: Equal(g12,g2)
    c: InternalAlignment(g13,g0)
    c: Equal(g13,g2)
    c: InternalAlignment(g14,g0)
    c: Equal(g14,g2)
    c: InternalAlignment(g15,g0)
    c: Equal(g15,g2)
    c: InternalAlignment(g16,g0)
    c: Equal(g16,g2)
    c: InternalAlignment(g17,g0)
    c: Equal(g17,g2)
    c: InternalAlignment(g18,g0)
    c: Equal(g18,g2)
    c: InternalAlignment(g19,g0)
    c: Equal(g19,g2)
    c: InternalAlignment(g20,g0)
    c: Equal(g20,g2)
    c: InternalAlignment(g21,g0)
    c: Equal(g21,g2)
    c: InternalAlignment(g22,g0)
    c: Equal(g22,g2)
    c: InternalAlignment(g23,g0)
    c: Equal(g23,g2)
    c: InternalAlignment(g24,g0)
    c: Equal(g24,g2)
    c: InternalAlignment(g25,g0)
    c: Equal(g25,g2)
    c: InternalAlignment(g26,g0)
    c: Equal(g26,g2)
    c: InternalAlignment(g27,g0)
    c: Equal(g27,g2)
    c: InternalAlignment(g28,g0)
    c: Equal(g28,g2)
    c: InternalAlignment(g29,g0)
    c: Equal(g29,g2)
    c: InternalAlignment(g30,g0)
    c: Equal(g30,g2)
    c: InternalAlignment(g31,g0)
    c: Equal(g31,g2)
    c: InternalAlignment(g32,g0)
    c: Equal(g32,g2)
    c: InternalAlignment(g33,g0)
    c: Equal(g33,g2)
    c: InternalAlignment(g34,g0)
    c: Equal(g34,g2)
    c: InternalAlignment(g35,g0)
    c: Equal(g35,g2)
    c: InternalAlignment(g36,g0)
    c: Equal(g36,g2)
    c: InternalAlignment(g37,g0)
    c: Equal(g37,g2)
    c: InternalAlignment(g38,g0)
    c: Equal(g38,g2)
    c: InternalAlignment(g39,g0)
    c: Equal(g39,g2)
    c: InternalAlignment(g40,g0)
    c: Equal(g40,g2)
    c: InternalAlignment(g41,g0)
    c: Equal(g41,g2)
    c: InternalAlignment(g42,g0)
    c: Equal(g42,g2)
    c: InternalAlignment(g43,g0)
    c: Equal(g43,g2)
    c: InternalAlignment(g44,g0)
    c: Equal(g44,g2)
    c: InternalAlignment(g45,g0)
    c: Equal(g45,g2)
    c: InternalAlignment(g46,g0)
    c: Equal(g46,g2)
    c: InternalAlignment(g47,g0)
    c: Equal(g47,g2)
    c: InternalAlignment(g48,g0)
    c: Equal(g48,g2)
    c: InternalAlignment(g49,g0)
    c: Equal(g49,g2)
    c: InternalAlignment(g50,g0)
    c: Equal(g50,g2)
    c: InternalAlignment(g51,g0)
    c: Equal(g51,g2)
    c: InternalAlignment(g52,g0)
    c: Equal(g52,g2)
    c: InternalAlignment(g53,g0)
    c: Equal(g53,g2)
    c: InternalAlignment(g54,g0)
    c: Equal(g54,g2)
    c: InternalAlignment(g55,g0)
    c: Equal(g55,g2)
    c: InternalAlignment(g56,g0)
    c: Equal(g56,g2)
    c: InternalAlignment(g57-g109 -> g0) x53
FEATURE [PartDesign::Pocket] Pocket135
  BaseFeature = -> Pocket134
  Direction = (0,0,-1)
  Length = 500
  Length2 = 5
  Midplane = true
  Placement = pos=(340,0,0) rot=(0.57735,0.57735,0.57735;2.0944rad)
  Profile = -> Sketch202
  ReferenceAxis = -> Sketch202 [N_Axis]
  Refine = true
  Suppressed = false
  Type = 0
FEATURE [PartDesign::Plane] DatumPlane048
  AttachmentOffset = pos=(0,0,-30) rot=(0,0,1;0rad)
  AttachmentSupport = -> [XZ_Plane029]
  Length = 490.693
  MapMode = 5
  Placement = pos=(0,30,-6.7e-15) rot=(1,0,0;1.5708rad)
  ResizeMode = 0
  Width = 105.693
FEATURE [Sketcher::SketchObject] Sketch203
  ArcFitTolerance = 1e-06
  AttachmentSupport = -> [DatumPlane048]
  FullyConstrained = true
  MakeInternals = false
  MapMode = 5
  Placement = pos=(0,30,-6.7e-15) rot=(1,0,0;1.5708rad)
  sketch-geometry (4):
    g0: Circle CenterX=350 CenterY=15 CenterZ=0 NormalX=0 NormalY=0 NormalZ=1 AngleXU=0 Radius=1.5
    g1: Circle CenterX=350 CenterY=-15 CenterZ=0 NormalX=0 NormalY=0 NormalZ=1 AngleXU=0 Radius=1.5
    g2: Circle CenterX=380 CenterY=-20 CenterZ=0 NormalX=0 NormalY=0 NormalZ=1 AngleXU=0 Radius=1.5
    g3: Circle CenterX=380 CenterY=20 CenterZ=0 NormalX=0 NormalY=0 NormalZ=1 AngleXU=0 Radius=1.5
  constraints (10):
    c: Diameter(g0) = 3
    c: Diameter(g1) = 3
    c: Diameter(g2) = 3
    c: Diameter(g3) = 3
    c: Symmetric(g0,g1,g-1)
    c: Symmetric(g3,g2,g-1)
    c: DistanceY(g1,g0) = 30
    c: DistanceY(g2,g3) = 40
    c: DistanceX(g0,g3) = 30
    c: DistanceX(g-1,g0) = 350
FEATURE [PartDesign::Pocket] Pocket136
  BaseFeature = -> Pocket135
  Direction = (0,1,-2e-16)
  Length = 500
  Length2 = 5
  Placement = pos=(340,0,0) rot=(0.57735,0.57735,0.57735;2.0944rad)
  Profile = -> Sketch203
  ReferenceAxis = -> Sketch203 [N_Axis]
  Refine = true
  Reversed = true
  Suppressed = false
  Type = 0
FEATURE [PartDesign::Chamfer] Chamfer001
  Angle = 45
  Base = -> Pocket136 [Edge23,Edge22,Edge18,Edge19,Edge21,Edge20,Edge25,Edge24]
  BaseFeature = -> Pocket136
  ChamferType = 0
  FlipDirection = false
  Placement = pos=(340,0,0) rot=(0.57735,0.57735,0.57735;2.0944rad)
  Refine = true
  Size = 1.5
  Size2 = 1
  SupportTransform = false
  Suppressed = false
  UseAllEdges = false
FEATURE [Sketcher::SketchObject] Sketch204
  ArcFitTolerance = 1e-06
  AttachmentSupport = -> [DatumPlane047]
  FullyConstrained = true
  MakeInternals = false
  MapMode = 5
  Placement = pos=(400,0,0) rot=(0.57735,0.57735,0.57735;2.0944rad)
  sketch-geometry (2):
    g0: Circle CenterX=21 CenterY=0 CenterZ=0 NormalX=0 NormalY=0 NormalZ=1 AngleXU=0 Radius=2.7
    g1: Circle CenterX=-21 CenterY=0 CenterZ=0 NormalX=0 NormalY=0 NormalZ=1 AngleXU=0 Radius=2.7
  constraints (6):
    c: PointOnObject(g0,g-1)
    c: PointOnObject(g1,g-1)
    c: DistanceX(g1,g-1) = 21
    c: DistanceX(g-1,g0) = 21
    c: Diameter(g1) = 5.4
    c: Diameter(g0) = 5.4
FEATURE [PartDesign::Pocket] Pocket137
  BaseFeature = -> Chamfer001
  Direction = (-1,0,0)
  Length = 25
  Length2 = 5
  Placement = pos=(340,0,0) rot=(0.57735,0.57735,0.57735;2.0944rad)
  Profile = -> Sketch204
  ReferenceAxis = -> Sketch204 [N_Axis]
  Refine = true
  Reversed = true
  Suppressed = false
  Type = 0
FEATURE [PartDesign::Plane] DatumPlane049
  AttachmentOffset = pos=(0,0,33) rot=(0,0,1;0rad)
  AttachmentSupport = -> [XY_Plane029]
  Length = 485.764
  MapMode = 5
  Placement = pos=(0,0,33) rot=(0,0,1;0rad)
  ResizeMode = 0
  Width = 82.7636
FEATURE [Sketcher::SketchObject] Sketch205
  ArcFitTolerance = 1e-06
  AttachmentSupport = -> [DatumPlane049]
  FullyConstrained = true
  MakeInternals = false
  MapMode = 5
  Placement = pos=(0,0,33) rot=(0,0,1;0rad)
  sketch-geometry (4):
    g0: LineSegment StartX=420.3 StartY=2.85 StartZ=0 EndX=420.3 EndY=-2.85 EndZ=0
    g1: LineSegment StartX=420.3 StartY=-2.85 StartZ=0 EndX=425 EndY=-2.85 EndZ=0
    g2: LineSegment StartX=425 StartY=-2.85 StartZ=0 EndX=425 EndY=2.85 EndZ=0
    g3: LineSegment StartX=425 StartY=2.85 StartZ=0 EndX=420.3 EndY=2.85 EndZ=0
  constraints (11):
    c: Coincident(g0,g1)
    c: Coincident(g1,g2)
    c: Coincident(g2,g3)
    c: Coincident(g3,g0)
    c: Vertical(g0)
    c: Horizontal(g1)
    c: Horizontal(g3)
    c: Symmetric(g1,g2,g-1)
    c: DistanceY(g2,g2) = 5.7
    c: DistanceX(g3,g3) = 4.7
    c: DistanceX(g-1,g2) = 425
FEATURE [PartDesign::Pocket] Pocket138
  BaseFeature = -> Pocket137
  Direction = (0,0,-1)
  Length = 16
  Length2 = 5
  Placement = pos=(340,0,0) rot=(0.57735,0.57735,0.57735;2.0944rad)
  Profile = -> Sketch205
  ReferenceAxis = -> Sketch205 [N_Axis]
  Refine = true
  Suppressed = false
  Type = 0
FEATURE [PartDesign::Plane] DatumPlane050
  AttachmentOffset = pos=(0,0,-33) rot=(0,0,1;0rad)
  AttachmentSupport = -> [XY_Plane029]
  Length = 485.764
  MapMode = 5
  Placement = pos=(0,0,-33) rot=(0,0,1;0rad)
  ResizeMode = 0
  Width = 82.7636
FEATURE [Sketcher::SketchObject] Sketch206
  ArcFitTolerance = 1e-06
  AttachmentSupport = -> [DatumPlane050]
  FullyConstrained = true
  MakeInternals = false
  MapMode = 5
  Placement = pos=(0,0,-33) rot=(0,0,1;0rad)
  sketch-geometry (4):
    g0: LineSegment StartX=425 StartY=2.85 StartZ=0 EndX=420.3 EndY=2.85 EndZ=0
    g1: LineSegment StartX=420.3 StartY=2.85 StartZ=0 EndX=420.3 EndY=-2.85 EndZ=0
    g2: LineSegment StartX=420.3 StartY=-2.85 StartZ=0 EndX=425 EndY=-2.85 EndZ=0
    g3: LineSegment StartX=425 StartY=-2.85 StartZ=0 EndX=425 EndY=2.85 EndZ=0
  constraints (11):
    c: Coincident(g0,g1)
    c: Coincident(g1,g2)
    c: Coincident(g2,g3)
    c: Coincident(g3,g0)
    c: Horizontal(g0)
    c: Horizontal(g2)
    c: Vertical(g1)
    c: Symmetric(g0,g2,g-1)
    c: DistanceY(g3,g3) = 5.7
    c: Distance(g0,g0) = 4.7
    c: DistanceX(g-1,g0) = 425
FEATURE [PartDesign::Pocket] Pocket139
  BaseFeature = -> Pocket138
  Direction = (0,0,-1)
  Length = 16
  Length2 = 5
  Placement = pos=(340,0,0) rot=(0.57735,0.57735,0.57735;2.0944rad)
  Profile = -> Sketch206
  ReferenceAxis = -> Sketch206 [N_Axis]
  Refine = true
  Reversed = true
  Suppressed = false
  Type = 0
FEATURE [PartDesign::Body] Body029  label="Motor Mount V2"
  AllowCompound = false
  Group = -> [DatumPlane045,DatumPlane046,Sketch198,DatumPlane047,Sketch199,AdditiveLoft025,Sketch200,AdditiveLoft026,Sketch201,Pocket134,Sketch202,Pocket135,DatumPlane048,Sketch203,Pocket136,Chamfer001,Sketch204,Pocket137,DatumPlane049,Sketch205,Pocket138,DatumPlane050,Sketch206,Pocket139]
  Origin = -> Origin029
  Tip = -> Pocket139
FEATURE [PartDesign::Chamfer] Chamfer
  Angle = 45
  Base = -> Pocket131 [Edge16,Edge15,Edge39,Edge40,Edge13,Edge14,Edge38,Edge37]
  BaseFeature = -> Pocket131
  ChamferType = 0
  FlipDirection = false
  Refine = true
  Size = 1.75
  Size2 = 1
  SupportTransform = false
  Suppressed = false
  UseAllEdges = false
FEATURE [PartDesign::Body] Body027
  AllowCompound = false
  Group = -> [Sketch183,Pad009,DatumPlane042,Sketch184,Pocket123,Sketch185,Pocket124,DatumPlane043,Sketch187,Pocket126,Sketch188,Pocket127,Sketch189,Pocket128,Sketch190,Pocket129,Sketch191,Pocket130,Sketch192,Pocket131,Chamfer]
  Origin = -> Origin027
  Placement = pos=(0,0,-100) rot=(0,0,1;0rad)
  Tip = -> Chamfer
FEATURE [PartDesign::Body] Body030
  AllowCompound = false
  Origin = -> Origin030
FEATURE [Sketcher::SketchObject] Sketch207
  ArcFitTolerance = 1e-06
  FullyConstrained = false
  MakeInternals = false
  Placement = pos=(0,0,200) rot=(0,0,1;0rad)
  sketch-geometry (123):
    g0: BSplineCurve PolesCount=61 KnotsCount=61 Degree=3 IsPeriodic=1
    g1-g61: Circle [constr] x61 (B-spline internal-alignment scaffolding for g0; pole/knot coordinates omitted)
    g62-g122: GeomPoint [constr] x61 (B-spline internal-alignment scaffolding for g0; pole/knot coordinates omitted)
  constraints (123):
    c: InternalAlignment(g1,g0)
    c: Weight(g1) = 1
    c: InternalAlignment(g2,g0)
    c: Equal(g2,g1)
    c: InternalAlignment(g3,g0)
    c: Equal(g3,g1)
    c: InternalAlignment(g4,g0)
    c: Equal(g4,g1)
    c: InternalAlignment(g5,g0)
    c: Equal(g5,g1)
    c: InternalAlignment(g6,g0)
    c: Equal(g6,g1)
    c: InternalAlignment(g7,g0)
    c: Equal(g7,g1)
    c: InternalAlignment(g8,g0)
    c: Equal(g8,g1)
    c: InternalAlignment(g9,g0)
    c: Equal(g9,g1)
    c: InternalAlignment(g10,g0)
    c: Equal(g10,g1)
    c: InternalAlignment(g11,g0)
    c: Equal(g11,g1)
    c: InternalAlignment(g12,g0)
    c: Equal(g12,g1)
    c: InternalAlignment(g13,g0)
    c: Equal(g13,g1)
    c: InternalAlignment(g14,g0)
    c: Equal(g14,g1)
    c: InternalAlignment(g15,g0)
    c: Equal(g15,g1)
    c: InternalAlignment(g16,g0)
    c: Equal(g16,g1)
    c: InternalAlignment(g17,g0)
    c: Equal(g17,g1)
    c: InternalAlignment(g18,g0)
    c: Equal(g18,g1)
    c: InternalAlignment(g19,g0)
    c: Equal(g19,g1)
    c: InternalAlignment(g20,g0)
    c: Equal(g20,g1)
    c: InternalAlignment(g21,g0)
    c: Equal(g21,g1)
    c: InternalAlignment(g22,g0)
    c: Equal(g22,g1)
    c: InternalAlignment(g23,g0)
    c: Equal(g23,g1)
    c: InternalAlignment(g24,g0)
    c: Equal(g24,g1)
    c: InternalAlignment(g25,g0)
    c: Equal(g25,g1)
    c: InternalAlignment(g26,g0)
    c: Equal(g26,g1)
    c: InternalAlignment(g27,g0)
    c: Equal(g27,g1)
    c: InternalAlignment(g28,g0)
    c: Equal(g28,g1)
    c: InternalAlignment(g29,g0)
    c: Equal(g29,g1)
    c: InternalAlignment(g30,g0)
    c: Equal(g30,g1)
    c: InternalAlignment(g31,g0)
    c: Equal(g31,g1)
    c: InternalAlignment(g32,g0)
    c: Equal(g32,g1)
    c: InternalAlignment(g33,g0)
    c: Equal(g33,g1)
    c: InternalAlignment(g34,g0)
    c: Equal(g34,g1)
    c: InternalAlignment(g35,g0)
    c: Equal(g35,g1)
    c: InternalAlignment(g36,g0)
    c: Equal(g36,g1)
    c: InternalAlignment(g37,g0)
    c: Equal(g37,g1)
    c: InternalAlignment(g38,g0)
    c: Equal(g38,g1)
    c: InternalAlignment(g39,g0)
    c: Equal(g39,g1)
    c: InternalAlignment(g40,g0)
    c: Equal(g40,g1)
    c: InternalAlignment(g41,g0)
    c: Equal(g41,g1)
    c: InternalAlignment(g42,g0)
    c: Equal(g42,g1)
    c: InternalAlignment(g43,g0)
    c: Equal(g43,g1)
    c: InternalAlignment(g44,g0)
    c: Equal(g44,g1)
    c: InternalAlignment(g45,g0)
    c: Equal(g45,g1)
    c: InternalAlignment(g46,g0)
    c: Equal(g46,g1)
    c: InternalAlignment(g47,g0)
    c: Equal(g47,g1)
    c: InternalAlignment(g48,g0)
    c: Equal(g48,g1)
    c: InternalAlignment(g49,g0)
    c: Equal(g49,g1)
    c: InternalAlignment(g50,g0)
    c: Equal(g50,g1)
    c: InternalAlignment(g51,g0)
    c: Equal(g51,g1)
    c: InternalAlignment(g52,g0)
    c: Equal(g52,g1)
    c: InternalAlignment(g53,g0)
    c: Equal(g53,g1)
    c: InternalAlignment(g54,g0)
    c: Equal(g54,g1)
    c: InternalAlignment(g55,g0)
    c: Equal(g55,g1)
    c: InternalAlignment(g56,g0)
    c: Equal(g56,g1)
    c: InternalAlignment(g57,g0)
    c: Equal(g57,g1)
    c: InternalAlignment(g58,g0)
    c: Equal(g58,g1)
    c: InternalAlignment(g59,g0)
    c: Equal(g59,g1)
    c: InternalAlignment(g60,g0)
    c: Equal(g60,g1)
    c: InternalAlignment(g61,g0)
    c: Equal(g61,g1)
    c: InternalAlignment(g62-g122 -> g0) x61
FEATURE [PartDesign::AdditiveLoft] AdditiveLoft027
  Closed = false
  Placement = pos=(0,0,200) rot=(0,0,1;0rad)
  Profile = -> Sketch207
  Refine = true
  Ruled = false
  Sections = -> [Sketch173]
  Suppressed = false
FEATURE [PartDesign::Pocket] Pocket141
  BaseFeature = -> AdditiveLoft027
  Direction = (0,0,-1)
  Length = 500
  Length2 = 5
  Midplane = true
  Placement = pos=(0,0,200) rot=(0,0,1;0rad)
  Profile = -> Sketch182
  ReferenceAxis = -> Sketch182 [N_Axis]
  Refine = true
  Suppressed = false
  Type = 0
FEATURE [PartDesign::Pocket] Pocket142
  BaseFeature = -> Pocket141
  Direction = (0,1,-2e-16)
  Length = 500
  Length2 = 5
  Placement = pos=(0,0,200) rot=(0,0,1;0rad)
  Profile = -> Sketch186
  ReferenceAxis = -> Sketch186 [N_Axis]
  Refine = true
  Reversed = true
  Suppressed = false
  Type = 0
FEATURE [PartDesign::Pocket] Pocket143
  BaseFeature = -> Pocket142
  Direction = (0,1,-2e-16)
  Length = 160
  Length2 = 5
  Midplane = true
  Placement = pos=(0,0,200) rot=(0,0,1;0rad)
  Profile = -> Sketch174
  ReferenceAxis = -> Sketch174 [N_Axis]
  Refine = true
  Suppressed = false
  Type = 0
FEATURE [PartDesign::Body] Body025
  AllowCompound = false
  Group = -> [Sketch173,DatumPlane038,AdditiveLoft027,Sketch174,Sketch182,DatumPlane041,Sketch186,Sketch207,Pocket141,Pocket142,Pocket143]
  Origin = -> Origin025
  Placement = pos=(0,0,-100) rot=(0,0,1;0rad)
  Tip = -> Pocket143
FEATURE [Sketcher::SketchObject] Sketch208
  ArcFitTolerance = 1e-06
  AttachmentSupport = -> [XY_Plane031]
  FullyConstrained = true
  MakeInternals = false
  MapMode = 5
  sketch-geometry (19):
    g0: GeomPoint X=170.515 Y=17 Z=0
    g1: GeomPoint X=310 Y=12 Z=0
    g2: ArcOfCircle CenterX=170.515 CenterY=17 CenterZ=0 NormalX=0 NormalY=0 NormalZ=1 AngleXU=0 Radius=4.15 StartAngle=3e-16 EndAngle=3.14159
    g3: LineSegment StartX=166.365 StartY=17 StartZ=0 EndX=166.365 EndY=12.5 EndZ=0
    g4: LineSegment StartX=166.365 StartY=12.5 StartZ=0 EndX=164.365 EndY=12.5 EndZ=0
    g5: LineSegment StartX=164.365 StartY=12.5 StartZ=0 EndX=164.365 EndY=23.15 EndZ=0
    g6: LineSegment StartX=164.365 StartY=23.15 StartZ=0 EndX=176.665 EndY=23.15 EndZ=0
    g7: LineSegment StartX=305.85 StartY=2 StartZ=0 EndX=174.665 EndY=2 EndZ=0
    g8: LineSegment StartX=174.665 StartY=2 StartZ=0 EndX=174.665 EndY=17 EndZ=0
    g9: LineSegment StartX=176.665 StartY=23.15 StartZ=0 EndX=176.665 EndY=4.5 EndZ=0
    g10: LineSegment StartX=176.665 StartY=4.5 StartZ=0 EndX=303.85 EndY=4.5 EndZ=0
    g11: ArcOfCircle CenterX=310 CenterY=12 CenterZ=0 NormalX=0 NormalY=0 NormalZ=1 AngleXU=0 Radius=4.15 StartAngle=0 EndAngle=3.14159
    g12: LineSegment StartX=305.85 StartY=2 StartZ=0 EndX=305.85 EndY=12 EndZ=0
    g13: LineSegment StartX=303.85 StartY=4.5 StartZ=0 EndX=303.85 EndY=18.15 EndZ=0
    g14: LineSegment StartX=303.85 StartY=18.15 StartZ=0 EndX=316.15 EndY=18.15 EndZ=0
    g15: LineSegment StartX=316.15 StartY=18.15 StartZ=0 EndX=316.15 EndY=7.5 EndZ=0
    g16: LineSegment StartX=316.15 StartY=7.5 StartZ=0 EndX=314.15 EndY=7.5 EndZ=0
    g17: LineSegment StartX=314.15 StartY=7.5 StartZ=0 EndX=314.15 EndY=12 EndZ=0
    g18: LineSegment [constr] StartX=166.365 StartY=17 StartZ=0 EndX=314.15 EndY=12 EndZ=0
  constraints (53):
    c: DistanceY(g-1,g0) = 17
    c: DistanceX(g-1,g1) = 310
    c: DistanceY(g-1,g1) = 12
    c: Coincident(g2,g0)
    c: Radius(g2) = 4.15
    c: DistanceY(g-1,g2) = 17
    c: DistanceY(g-1,g2) = 17
    c: Tangent(g2,g3) = -1.5708
    c: Coincident(g3,g4)
    c: Horizontal(g4)
    c: Coincident(g4,g5)
    c: Vertical(g5)
    c: Coincident(g5,g6)
    c: Horizontal(g6)
    c: Coincident(g7,g8)
    c: Coincident(g8,g2)
    c: Vertical(g8)
    c: DistanceX(g4,g4) = 2
    c: DistanceY(g0,g6) = 6.15
    c: DistanceY(g3,g3) = 4.5
    c: DistanceX(g6,g6) = 12.3
    c: Coincident(g6,g9)
    c: Vertical(g9)
    c: Coincident(g9,g10)
    c: Horizontal(g10)
    c: Angle(g11) = 3.14159
    c: Coincident(g11,g1)
    c: Radius(g11) = 4.15
    c: DistanceY(g-1,g11) = 12
    c: Coincident(g12,g7)
    c: Coincident(g12,g11)
    c: Vertical(g12)
    c: DistanceX(g10,g7) = 2
    c: Coincident(g10,g13)
    c: Vertical(g13)
    c: Coincident(g13,g14)
    c: Horizontal(g14)
    c: Coincident(g14,g15)
    c: Vertical(g15)
    c: Coincident(g15,g16)
    c: Horizontal(g16)
    c: Coincident(g16,g17)
    c: Coincident(g17,g11)
    c: Vertical(g17)
    c: DistanceX(g16,g16) = 2
    c: DistanceY(g1,g14) = 6.15
    c: DistanceY(g17,g17) = 4.5
    c: Coincident(g18,g2)
    c: Distance(g18,g18) = 147.87
    c: Coincident(g18,g11)
    c: Horizontal(g7)
    c: DistanceY(g7,g9) = 2.5
    c: DistanceY(g-1,g7) = 2
FEATURE [PartDesign::Pad] Pad010
  Direction = (0,0,1)
  Length = 160
  Length2 = 10
  Midplane = true
  Profile = -> Sketch208
  ReferenceAxis = -> Sketch208 [N_Axis]
  Refine = true
  Suppressed = false
  Type = 0
FEATURE [Sketcher::SketchObject] Sketch209
  ArcFitTolerance = 1e-06
  AttachmentSupport = -> [Pad010]
  FullyConstrained = false
  MakeInternals = false
  MapMode = 5
  Placement = pos=(0,18.15,0) rot=(0,0.707107,0.707107;3.14159rad)
  sketch-geometry (4):
    g0: LineSegment StartX=-319.791 StartY=43.9069 StartZ=0 EndX=-295.273 EndY=38.2538 EndZ=0
    g1: LineSegment StartX=-295.273 StartY=38.2538 StartZ=0 EndX=-295.273 EndY=-36.6788 EndZ=0
    g2: LineSegment StartX=-295.273 StartY=-36.6788 StartZ=0 EndX=-319.791 EndY=-43.9655 EndZ=0
    g3: LineSegment StartX=-319.791 StartY=-43.9655 StartZ=0 EndX=-319.791 EndY=43.9069 EndZ=0
  constraints (6):
    c: Coincident(g0,g1)
    c: Vertical(g1)
    c: Coincident(g1,g2)
    c: Coincident(g2,g3)
    c: Coincident(g3,g0)
    c: Vertical(g3)
FEATURE [PartDesign::Pocket] Pocket144
  BaseFeature = -> Pad010
  Direction = (0,-1,2e-16)
  Length = 100
  Length2 = 5
  Profile = -> Sketch209
  ReferenceAxis = -> Sketch209 [N_Axis]
  Refine = true
  Suppressed = false
  Type = 0
FEATURE [Sketcher::SketchObject] Sketch210
  ArcFitTolerance = 1e-06
  AttachmentSupport = -> [Pocket144]
  FullyConstrained = false
  MakeInternals = false
  MapMode = 5
  Placement = pos=(0,4.5,0) rot=(0,0.707107,0.707107;3.14159rad)
  sketch-geometry (13):
    g0: Circle CenterX=-265 CenterY=25 CenterZ=0 NormalX=0 NormalY=0 NormalZ=1 AngleXU=0 Radius=1.55
    g1: Circle CenterX=-215 CenterY=25 CenterZ=0 NormalX=0 NormalY=0 NormalZ=1 AngleXU=0 Radius=1.55
    g2: Circle CenterX=-215 CenterY=-25 CenterZ=0 NormalX=0 NormalY=0 NormalZ=1 AngleXU=0 Radius=1.55
    g3: Circle CenterX=-265 CenterY=-25 CenterZ=0 NormalX=0 NormalY=0 NormalZ=1 AngleXU=0 Radius=1.55
    g4: LineSegment StartX=-267.5 StartY=80 StartZ=0 EndX=-212.5 EndY=80 EndZ=0
    g5: LineSegment StartX=-212.5 StartY=80 StartZ=0 EndX=-225 EndY=55 EndZ=0
    g6: LineSegment StartX=-225 StartY=55 StartZ=0 EndX=-255 EndY=55 EndZ=0
    g7: LineSegment StartX=-255 StartY=55 StartZ=0 EndX=-267.5 EndY=80 EndZ=0
    g8: LineSegment StartX=-267.5 StartY=-80 StartZ=0 EndX=-212.5 EndY=-80 EndZ=0
    g9: LineSegment StartX=-212.5 StartY=-80 StartZ=0 EndX=-225 EndY=-55 EndZ=0
    g10: LineSegment StartX=-225 StartY=-55 StartZ=0 EndX=-255 EndY=-55 EndZ=0
    g11: LineSegment StartX=-255 StartY=-55 StartZ=0 EndX=-267.5 EndY=-80 EndZ=0
    g12: LineSegment [constr] StartX=-240 StartY=92.293 StartZ=0 EndX=-240 EndY=-109.674 EndZ=0
  constraints (34):
    c: Diameter(g0) = 3.1
    c: Diameter(g1) = 3.1
    c: Diameter(g3) = 3.1
    c: Diameter(g2) = 3.1
    c: DistanceX(g3,g2) = 50
    c: Symmetric(g2,g1,g-1)
    c: Symmetric(g0,g3,g-1)
    c: DistanceY(g2,g1) = 50
    c: DistanceY(g3,g0) = 50
    c: Horizontal(g4)
    c: Coincident(g4,g5)
    c: Coincident(g5,g6)
    c: Coincident(g6,g7)
    c: Coincident(g7,g4)
    c: Equal(g7,g5)
    c: Horizontal(g8)
    c: Coincident(g8,g9)
    c: Coincident(g9,g10)
    c: Coincident(g10,g11)
    c: Coincident(g11,g8)
    c: Equal(g11,g9)
    c: Vertical(g12)
    c: DistanceX(g12,g-1) = 240
    c: Symmetric(g10,g9,g12)
    c: Symmetric(g6,g5,g12)
    c: DistanceY(g-1,g4) = 80
    c: DistanceY(g5,g5) = 25
    c: DistanceX(g4,g4) = 55
    c: DistanceX(g6,g6) = 30
    c: DistanceY(g8,g-1) = 80
    c: DistanceX(g10,g10) = 30
    c: DistanceX(g8,g8) = 55
    c: DistanceY(g9,g9) = 25
    c: Distance(g2,g12) = 25
FEATURE [PartDesign::Pocket] Pocket145
  BaseFeature = -> Pocket144
  Direction = (0,-1,2e-16)
  Length = 10
  Length2 = 5
  Profile = -> Sketch210
  ReferenceAxis = -> Sketch210 [N_Axis]
  Refine = true
  Suppressed = false
  Type = 0
FEATURE [Sketcher::SketchObject] Sketch211
  ArcFitTolerance = 1e-06
  AttachmentSupport = -> [Pocket145]
  FullyConstrained = false
  MakeInternals = false
  MapMode = 5
  Placement = pos=(176.665,0,0) rot=(0.57735,0.57735,0.57735;2.0944rad)
  sketch-geometry (14):
    g0: LineSegment StartX=4.5 StartY=67.5 StartZ=0 EndX=4.5 EndY=52.5 EndZ=0
    g1: LineSegment StartX=4.5 StartY=67.5 StartZ=0 EndX=9 EndY=63.5 EndZ=0
    g2: LineSegment StartX=9 StartY=63.5 StartZ=0 EndX=9 EndY=56.5 EndZ=0
    g3: LineSegment StartX=9 StartY=56.5 StartZ=0 EndX=4.5 EndY=52.5 EndZ=0
    g4: LineSegment StartX=4.5 StartY=7.5 StartZ=0 EndX=4.5 EndY=-7.5 EndZ=0
    g5: LineSegment StartX=4.5 StartY=-7.5 StartZ=0 EndX=9 EndY=-3.5 EndZ=0
    g6: LineSegment StartX=9 StartY=-3.5 StartZ=0 EndX=9 EndY=3.5 EndZ=0
    g7: LineSegment StartX=9 StartY=3.5 StartZ=0 EndX=4.5 EndY=7.5 EndZ=0
    g8: LineSegment StartX=4.5 StartY=-52.5 StartZ=0 EndX=4.5 EndY=-67.5 EndZ=0
    g9: LineSegment StartX=4.5 StartY=-67.5 StartZ=0 EndX=9 EndY=-63.5 EndZ=0
    g10: LineSegment StartX=9 StartY=-63.5 StartZ=0 EndX=9 EndY=-56.5 EndZ=0
    g11: LineSegment StartX=9 StartY=-56.5 StartZ=0 EndX=4.5 EndY=-52.5 EndZ=0
    g12: LineSegment [constr] StartX=0 StartY=60 StartZ=0 EndX=16.9591 EndY=60 EndZ=0
    g13: LineSegment [constr] StartX=0 StartY=-60 StartZ=0 EndX=16.053 EndY=-60 EndZ=0
  constraints (36):
    c: Coincident(g0,g1)
    c: Coincident(g1,g2)
    c: Coincident(g2,g3)
    c: Coincident(g3,g0)
    c: Coincident(g4,g5)
    c: Coincident(g5,g6)
    c: Coincident(g6,g7)
    c: Coincident(g7,g4)
    c: Coincident(g8,g9)
    c: Coincident(g9,g10)
    c: Coincident(g10,g11)
    c: Coincident(g11,g8)
    c: Symmetric(g6,g5,g-1)
    c: Symmetric(g4,g4,g-1)
    c: DistanceY(g4,g4) = 15
    c: DistanceY(g6,g6) = 7
    c: DistanceX(g5,g5) = 4.5
    c: DistanceX(g-1,g4) = 4.5
    c: PointOnObject(g12,g-2)
    c: Horizontal(g12)
    c: PointOnObject(g13,g-2)
    c: Horizontal(g13)
    c: Symmetric(g1,g2,g12)
    c: Symmetric(g0,g0,g12)
    c: DistanceY(g0,g0) = 15
    c: DistanceY(g2,g2) = 7
    c: DistanceX(g3,g3) = 4.5
    c: DistanceX(g-1,g0) = 4.5
    c: DistanceY(g-1,g12) = 60
    c: DistanceY(g13,g-1) = 60
    c: Symmetric(g10,g9,g13)
    c: Symmetric(g8,g8,g13)
    c: DistanceY(g8,g8) = 15
    c: DistanceY(g10,g10) = 7
    c: DistanceX(g9,g9) = 4.5
    c: DistanceX(g-1,g8) = 4.5
FEATURE [PartDesign::Pocket] Pocket146
  BaseFeature = -> Pocket145
  Direction = (-1,0,0)
  Length = 5
  Length2 = 5
  Profile = -> Sketch211
  ReferenceAxis = -> Sketch211 [N_Axis]
  Refine = true
  Suppressed = false
  Type = 0
FEATURE [PartDesign::Chamfer] Chamfer002
  Angle = 45
  Base = -> Pocket146 [Edge18,Edge20,Edge19,Edge17]
  BaseFeature = -> Pocket146
  ChamferType = 0
  FlipDirection = false
  Refine = true
  Size = 1.5
  Size2 = 1
  SupportTransform = false
  Suppressed = false
  UseAllEdges = false
FEATURE [PartDesign::Body] Body031
  AllowCompound = false
  Group = -> [Sketch208,Pad010,Sketch209,Pocket144,Sketch210,Pocket145,Sketch211,Pocket146,Chamfer002]
  Origin = -> Origin031
  Tip = -> Chamfer002
FEATURE [Sketcher::SketchObject] Sketch212
  ArcFitTolerance = 1e-06
  AttachmentSupport = -> [XY_Plane032]
  FullyConstrained = true
  MakeInternals = false
  MapMode = 5
  sketch-geometry (12):
    g0: LineSegment StartX=20 StartY=0 StartZ=0 EndX=20 EndY=-11 EndZ=0
    g1: LineSegment StartX=20 StartY=-11 StartZ=0 EndX=7 EndY=-14 EndZ=0
    g2: LineSegment StartX=7 StartY=-14 StartZ=0 EndX=5 EndY=-8 EndZ=0
    g3: LineSegment StartX=5 StartY=-8 StartZ=0 EndX=0 EndY=-6 EndZ=0
    g4: LineSegment StartX=0 StartY=-6 StartZ=0 EndX=2 EndY=-12 EndZ=0
    g5: LineSegment StartX=2 StartY=-12 StartZ=0 EndX=-1.66667 EndY=-11 EndZ=0
    g6: LineSegment StartX=-1.66667 StartY=-11 StartZ=0 EndX=-3.5 EndY=-5.5 EndZ=0
    g7: LineSegment StartX=-3.5 StartY=-5.5 StartZ=0 EndX=-3.5 EndY=0 EndZ=0
    g8: LineSegment StartX=-3.5 StartY=0 StartZ=0 EndX=15 EndY=0 EndZ=0
    g9: LineSegment StartX=15 StartY=0 StartZ=0 EndX=15 EndY=23 EndZ=0
    g10: LineSegment StartX=15 StartY=23 StartZ=0 EndX=20 EndY=23 EndZ=0
    g11: LineSegment StartX=20 StartY=23 StartZ=0 EndX=20 EndY=0 EndZ=0
  constraints (36):
    c: PointOnObject(g0,g-1)
    c: Vertical(g0)
    c: Coincident(g0,g1)
    c: Coincident(g1,g2)
    c: Coincident(g2,g3)
    c: Coincident(g3,g4)
    c: Coincident(g4,g5)
    c: Coincident(g5,g6)
    c: Coincident(g6,g7)
    c: Coincident(g7,g8)
    c: Coincident(g8,g9)
    c: Vertical(g9)
    c: Coincident(g9,g10)
    c: Horizontal(g10)
    c: Coincident(g10,g11)
    c: Coincident(g11,g0)
    c: Vertical(g11)
    c: PointOnObject(g3,g-2)
    c: DistanceX(g3,g3) = 5
    c: Parallel(g4,g2)
    c: Distance(g4,g-2) = 2
    c: DistanceX(g4,g1) = 5
    c: DistanceY(g1,g2) = 6
    c: DistanceX(g-1,g0) = 20
    c: DistanceX(g-1,g8) = 15
    c: DistanceY(g2,g-1) = 8
    c: DistanceY(g2,g3) = 2
    c: DistanceY(g5,g-1) = 11
    c: Parallel(g6,g4)
    c: DistanceY(g6,g-1) = 5.5
    c: DistanceX(g6,g-1) = 3.5
    c: Vertical(g7)
    c: PointOnObject(g7,g-1)
    c: Horizontal(g8)
    c: DistanceY(g0,g-1) = 11
    c: DistanceY(g-1,g9) = 23
FEATURE [PartDesign::Pad] Pad011
  Direction = (0,0,1)
  Length = 25
  Length2 = 10
  Midplane = true
  Profile = -> Sketch212
  ReferenceAxis = -> Sketch212 [N_Axis]
  Refine = true
  Suppressed = false
  Type = 0
FEATURE [PartDesign::FeatureBase] Clone
  BaseFeature = -> Body027
  Placement = pos=(0,0,-100) rot=(0,0,1;0rad)
  Suppressed = false
FEATURE [PartDesign::Body] Body033  label="Main_Body_Frame_Bigger_For_Tolerances"
  AllowCompound = false
  Group = -> [Clone]
  Origin = -> Origin033
  Tip = -> Clone
FEATURE [Part::Scale] Scale
  Base = -> Body033
  Uniform = true
  UniformScale = 1.02
  XScale = 1
  YScale = 1
  ZScale = 1
FEATURE [Sketcher::SketchObject] Sketch213
  ArcFitTolerance = 1e-06
  AttachmentSupport = -> [Pad011]
  FullyConstrained = true
  MakeInternals = false
  MapMode = 5
  Placement = pos=(15,0,0) rot=(0.57735,-0.57735,-0.57735;2.0944rad)
  sketch-geometry (8):
    g0: ArcOfCircle CenterX=-19 CenterY=7 CenterZ=0 NormalX=0 NormalY=0 NormalZ=1 AngleXU=0 Radius=2 StartAngle=1.5708 EndAngle=4.71239
    g1: ArcOfCircle CenterX=-17 CenterY=7 CenterZ=0 NormalX=0 NormalY=0 NormalZ=1 AngleXU=0 Radius=2 StartAngle=4.71239 EndAngle=7.85398
    g2: LineSegment StartX=-19 StartY=9 StartZ=0 EndX=-17 EndY=9 EndZ=0
    g3: LineSegment StartX=-19 StartY=5 StartZ=0 EndX=-17 EndY=5 EndZ=0
    g4: ArcOfCircle CenterX=-19 CenterY=-7 CenterZ=0 NormalX=0 NormalY=0 NormalZ=1 AngleXU=0 Radius=2 StartAngle=1.5708 EndAngle=4.71239
    g5: ArcOfCircle CenterX=-17 CenterY=-7 CenterZ=0 NormalX=0 NormalY=0 NormalZ=1 AngleXU=0 Radius=2 StartAngle=4.71239 EndAngle=7.85398
    g6: LineSegment StartX=-19 StartY=-5 StartZ=0 EndX=-17 EndY=-5 EndZ=0
    g7: LineSegment StartX=-19 StartY=-9 StartZ=0 EndX=-17 EndY=-9 EndZ=0
  constraints (18):
    c: Tangent(g0,g2) = 1.5708
    c: Tangent(g0,g3) = -1.5708
    c: Tangent(g1,g2) = 1.5708
    c: Tangent(g1,g3) = -1.5708
    c: Equal(g0,g1)
    c: Tangent(g4,g6) = 1.5708
    c: Tangent(g4,g7) = -1.5708
    c: Tangent(g5,g6) = 1.5708
    c: Tangent(g5,g7) = -1.5708
    c: Equal(g4,g5)
    c: Radius(g5) = 2
    c: Radius(g1) = 2
    c: Symmetric(g0,g4,g-1)
    c: Horizontal(g6)
    c: Symmetric(g1,g5,g-1)
    c: DistanceY(g5,g-1) = 7
    c: DistanceX(g5,g-1) = 17
    c: DistanceX(g4,g5) = 2
FEATURE [PartDesign::Pocket] Pocket147
  BaseFeature = -> Pad011
  Direction = (1,0,0)
  Length = 5
  Length2 = 5
  Profile = -> Sketch213
  ReferenceAxis = -> Sketch213 [N_Axis]
  Refine = true
  Suppressed = false
  Type = 0
FEATURE [PartDesign::Body] Body032
  AllowCompound = false
  Group = -> [Sketch212,Pad011,Sketch213,Pocket147]
  Origin = -> Origin032
  Tip = -> Pocket147
FEATURE [Part::Cut] Cut
  Base = -> Body032
  Refine = true
  Tool = -> Scale
FEATURE [Sketcher::SketchObject] Sketch214
  ArcFitTolerance = 1e-06
  AttachmentSupport = -> [XY_Plane034]
  FullyConstrained = false
  MakeInternals = false
  MapMode = 5
  sketch-geometry (28):
    g0: LineSegment StartX=14.96 StartY=23 StartZ=0 EndX=14.96 EndY=14.0825 EndZ=0
    g1: LineSegment StartX=14.96 StartY=14.0825 StartZ=0 EndX=14.2061 EndY=13.1218 EndZ=0
    g2: LineSegment StartX=14.2061 StartY=13.1218 StartZ=0 EndX=14.2061 EndY=0 EndZ=0
    g3: LineSegment StartX=14.2061 StartY=0 StartZ=0 EndX=0 EndY=0.070405 EndZ=0
    g4: LineSegment StartX=0 StartY=0.070405 StartZ=0 EndX=-3.57861 EndY=0.070405 EndZ=0
    g5: LineSegment StartX=-3.57861 StartY=0.070405 StartZ=0 EndX=-3.57861 EndY=-5.51045 EndZ=0
    g6: LineSegment StartX=-3.57861 StartY=-5.51045 StartZ=0 EndX=-1.72809 EndY=-11.1152 EndZ=0
    g7: LineSegment StartX=-1.72809 StartY=-11.1152 StartZ=0 EndX=2.12835 EndY=-12.1253 EndZ=0
    g8: LineSegment StartX=2.12835 StartY=-12.1253 StartZ=0 EndX=0.150399 EndY=-6.16684 EndZ=0
    g9: LineSegment StartX=0.150399 StartY=-6.16684 StartZ=0 EndX=4.91985 EndY=-8.08274 EndZ=0
    g10: LineSegment StartX=4.91985 StartY=-8.08274 StartZ=0 EndX=6.93936 EndY=-14.1292 EndZ=0
    g11: LineSegment StartX=6.93936 StartY=-14.1292 StartZ=0 EndX=8.10163 EndY=-13.8685 EndZ=0
    g12: LineSegment StartX=8.10163 StartY=-13.8685 StartZ=0 EndX=6.53884 EndY=-16.4471 EndZ=0
    g13: LineSegment StartX=6.53884 StartY=-16.4471 StartZ=0 EndX=-5.07807 EndY=-13.5943 EndZ=0
    g14: LineSegment StartX=-5.07807 StartY=-13.5943 StartZ=0 EndX=-7.48302 EndY=-6.12472 EndZ=0
    g15: LineSegment StartX=-7.48302 StartY=-6.12472 StartZ=0 EndX=-7.48302 EndY=1.00418 EndZ=0
    g16: LineSegment StartX=-7.48302 StartY=1.00418 StartZ=0 EndX=-6.25629 EndY=2.02712 EndZ=0
    g17: LineSegment StartX=-6.25629 StartY=2.02712 StartZ=0 EndX=-4.23586 EndY=3.71923 EndZ=0
    g18: LineSegment StartX=-4.23586 StartY=3.71923 StartZ=0 EndX=-2.16506 EndY=5.91907 EndZ=0
    g19: LineSegment StartX=-2.16506 StartY=5.91907 StartZ=0 EndX=0.107928 EndY=8.36884 EndZ=0
    g20: LineSegment StartX=0.107928 StartY=8.36884 StartZ=0 EndX=2.35566 EndY=10.263 EndZ=0
    g21: LineSegment StartX=2.35566 StartY=10.263 StartZ=0 EndX=4.55288 EndY=11.8541 EndZ=0
    g22: LineSegment StartX=4.55288 StartY=11.8541 StartZ=0 EndX=5.81564 EndY=12.6623 EndZ=0
    g23: LineSegment StartX=5.81564 StartY=12.6623 StartZ=0 EndX=7.05316 EndY=13.3441 EndZ=0
    g24: LineSegment StartX=7.05316 StartY=13.3441 StartZ=0 EndX=8.10178 EndY=13.9783 EndZ=0
    g25: LineSegment StartX=8.10178 StartY=13.9783 StartZ=0 EndX=9.50784 EndY=14.7847 EndZ=0
    g26: LineSegment StartX=9.50784 StartY=14.7847 StartZ=0 EndX=9.50784 EndY=23 EndZ=0
    g27: LineSegment StartX=9.50784 StartY=23 StartZ=0 EndX=14.96 EndY=23 EndZ=0
  constraints (39):
    c: Vertical(g0)
    c: Coincident(g0,g1)
    c: Coincident(g1,g2)
    c: PointOnObject(g2,g-1)
    c: Vertical(g2)
    c: Coincident(g2,g3)
    c: PointOnObject(g3,g-2)
    c: Coincident(g3,g4)
    c: Horizontal(g4)
    c: Coincident(g4,g5)
    c: Vertical(g5)
    c: Coincident(g5,g6)
    c: Coincident(g6,g7)
    c: Coincident(g7,g8)
    c: Coincident(g8,g9)
    c: Coincident(g9,g10)
    c: Coincident(g10,g11)
    c: Coincident(g11,g12)
    c: Coincident(g12,g13)
    c: Coincident(g13,g14)
    c: Coincident(g14,g15)
    c: Vertical(g15)
    c: Coincident(g15,g16)
    c: Coincident(g16,g17)
    c: Coincident(g17,g18)
    c: Coincident(g18,g19)
    c: Coincident(g19,g20)
    c: Coincident(g20,g21)
    c: Coincident(g21,g22)
    c: Coincident(g22,g23)
    c: Coincident(g23,g24)
    c: Coincident(g24,g25)
    c: Coincident(g25,g26)
    c: Vertical(g26)
    c: Coincident(g26,g27)
    c: Coincident(g27,g0)
    c: Horizontal(g27)
    c: DistanceX(g-1,g0) = 14.96
    c: DistanceY(g-1,g26) = 23
FEATURE [PartDesign::Pad] Pad012
  Direction = (0,0,1)
  Length = 25
  Length2 = 10
  Midplane = true
  Profile = -> Sketch214
  ReferenceAxis = -> Sketch214 [N_Axis]
  Refine = true
  Suppressed = false
  Type = 0
FEATURE [Sketcher::SketchObject] Sketch215
  ArcFitTolerance = 1e-06
  AttachmentSupport = -> [Pad012]
  FullyConstrained = true
  MakeInternals = false
  MapMode = 5
  Placement = pos=(9.50784,0,0) rot=(0.57735,-0.57735,-0.57735;2.0944rad)
  sketch-geometry (2):
    g0: Circle CenterX=-18 CenterY=-7 CenterZ=0 NormalX=0 NormalY=0 NormalZ=1 AngleXU=0 Radius=2.05
    g1: Circle CenterX=-18 CenterY=7 CenterZ=0 NormalX=0 NormalY=0 NormalZ=1 AngleXU=0 Radius=2.05
  constraints (5):
    c: Diameter(g1) = 4.1
    c: Diameter(g0) = 4.1
    c: Symmetric(g1,g0,g-1)
    c: DistanceY(g0,g-1) = 7
    c: DistanceX(g0,g-1) = 18
FEATURE [PartDesign::Pocket] Pocket148
  BaseFeature = -> Pad012
  Direction = (1,0,0)
  Length = 6
  Length2 = 5
  Profile = -> Sketch215
  ReferenceAxis = -> Sketch215 [N_Axis]
  Refine = true
  Suppressed = false
  Type = 0
FEATURE [Sketcher::SketchObject] Sketch216
  ArcFitTolerance = 1e-06
  AttachmentSupport = -> [Pocket148]
  FullyConstrained = true
  MakeInternals = false
  MapMode = 5
  Placement = pos=(9.50784,0,0) rot=(0.57735,-0.57735,-0.57735;2.0944rad)
  sketch-geometry (2):
    g0: Circle CenterX=-18 CenterY=-7 CenterZ=0 NormalX=0 NormalY=0 NormalZ=1 AngleXU=0 Radius=4.5
    g1: Circle CenterX=-18 CenterY=7 CenterZ=0 NormalX=0 NormalY=0 NormalZ=1 AngleXU=0 Radius=4.5
  constraints (5):
    c: Symmetric(g1,g0,g-1)
    c: DistanceY(g0,g-1) = 7
    c: DistanceX(g0,g-1) = 18
    c: Diameter(g0) = 9
    c: Diameter(g1) = 9
FEATURE [PartDesign::Pocket] Pocket149
  BaseFeature = -> Pocket148
  Direction = (1,0,0)
  Length = 5
  Length2 = 5
  Profile = -> Sketch216
  ReferenceAxis = -> Sketch216 [N_Axis]
  Refine = true
  Reversed = true
  Suppressed = false
  Type = 0
FEATURE [PartDesign::Chamfer] Chamfer003
  Angle = 45
  Base = -> Pocket149 [Edge7]
  BaseFeature = -> Pocket149
  ChamferType = 0
  FlipDirection = false
  Refine = true
  Size = 1.5
  Size2 = 1
  SupportTransform = false
  Suppressed = false
  UseAllEdges = false
FEATURE [PartDesign::Fillet] Fillet001
  Base = -> Chamfer003 [Edge103]
  BaseFeature = -> Chamfer003
  Radius = 3
  Refine = true
  SupportTransform = false
  Suppressed = false
  UseAllEdges = false
FEATURE [Sketcher::SketchObject] Sketch217
  ArcFitTolerance = 1e-06
  AttachmentSupport = -> [Fillet001]
  FullyConstrained = false
  MakeInternals = false
  MapMode = 5
  Placement = pos=(0,0,12.5) rot=(0,0,1;0rad)
  sketch-geometry (7):
    g0: LineSegment StartX=-17.4218 StartY=-8.11966 StartZ=0 EndX=-21.1793 EndY=2.95446 EndZ=0
    g1: LineSegment StartX=-21.1793 StartY=2.95446 StartZ=0 EndX=-6.51503 EndY=0.793169 EndZ=0
    g2: LineSegment StartX=-6.51503 StartY=0.793169 StartZ=0 EndX=0 EndY=7.06546 EndZ=0
    g3: LineSegment StartX=0 StartY=7.06546 StartZ=0 EndX=-3.73529 EndY=7.51512 EndZ=0
    g4: LineSegment StartX=-3.73529 StartY=7.51512 StartZ=0 EndX=-27.567 EndY=7.51512 EndZ=0
    g5: LineSegment StartX=-27.567 StartY=7.51512 StartZ=0 EndX=-23.3515 EndY=-8.11966 EndZ=0
    g6: LineSegment StartX=-23.3515 StartY=-8.11966 StartZ=0 EndX=-17.4218 EndY=-8.11966 EndZ=0
  constraints (10):
    c: Coincident(g0,g1)
    c: Coincident(g1,g2)
    c: PointOnObject(g2,g-2)
    c: Coincident(g2,g3)
    c: Coincident(g3,g4)
    c: Horizontal(g4)
    c: Coincident(g4,g5)
    c: Coincident(g5,g6)
    c: Coincident(g6,g0)
    c: Horizontal(g6)
FEATURE [PartDesign::Pad] Pad013
  BaseFeature = -> Fillet001
  Direction = (0,0,1)
  Length = 25
  Length2 = 10
  Profile = -> Sketch217
  ReferenceAxis = -> Sketch217 [N_Axis]
  Refine = true
  Reversed = true
  Suppressed = false
  Type = 0
FEATURE [PartDesign::Chamfer] Chamfer004
  Angle = 45
  Base = -> Pad013 [Edge114]
  BaseFeature = -> Pad013
  ChamferType = 0
  FlipDirection = false
  Refine = true
  Size = 5.7
  Size2 = 1
  SupportTransform = false
  Suppressed = false
  UseAllEdges = false
FEATURE [PartDesign::Fillet] Fillet002
  Base = -> Chamfer004 [Edge81]
  BaseFeature = -> Chamfer004
  Radius = 3
  Refine = true
  SupportTransform = false
  Suppressed = false
  UseAllEdges = false
FEATURE [PartDesign::Fillet] Fillet003
  Base = -> Fillet002 [Edge38]
  BaseFeature = -> Fillet002
  Radius = 2
  Refine = true
  SupportTransform = false
  Suppressed = false
  UseAllEdges = false
FEATURE [PartDesign::Fillet] Fillet004
  Base = -> Fillet003 [Edge49]
  BaseFeature = -> Fillet003
  Radius = 3
  Refine = true
  SupportTransform = false
  Suppressed = false
  UseAllEdges = false
FEATURE [PartDesign::Fillet] Fillet005
  Base = -> Fillet004 [Edge57]
  BaseFeature = -> Fillet004
  Radius = 4
  Refine = true
  SupportTransform = false
  Suppressed = false
  UseAllEdges = false
FEATURE [PartDesign::Fillet] Fillet006
  Base = -> Fillet005 [Edge40]
  BaseFeature = -> Fillet005
  Radius = 5
  Refine = true
  SupportTransform = false
  Suppressed = false
  UseAllEdges = false
FEATURE [PartDesign::FeatureBase] Clone001
  BaseFeature = -> Body033
  Suppressed = false
FEATURE [PartDesign::Body] Body035
  AllowCompound = false
  Group = -> [Clone001]
  Origin = -> Origin035
  Tip = -> Clone001
FEATURE [Part::Scale] Scale001
  Base = -> Body035
  Uniform = true
  UniformScale = 1.02
  XScale = 1
  YScale = 1
  ZScale = 1
FEATURE [PartDesign::Fillet] Fillet007
  Base = -> Fillet006 [Edge8,Edge10,Edge60,Edge56,Edge12,Edge64]
  BaseFeature = -> Fillet006
  Radius = 2
  Refine = true
  SupportTransform = false
  Suppressed = false
  UseAllEdges = false
FEATURE [PartDesign::Body] Body034
  AllowCompound = false
  Group = -> [Sketch214,Pad012,Sketch215,Pocket148,Sketch216,Pocket149,Chamfer003,Fillet001,Sketch217,Pad013,Chamfer004,Fillet002,Fillet003,Fillet004,Fillet005,Fillet006,Fillet007]
  Origin = -> Origin034
  Tip = -> Fillet007
FEATURE [Part::Cut] Cut001
  Base = -> Body034
  Refine = true
  Tool = -> Scale001
